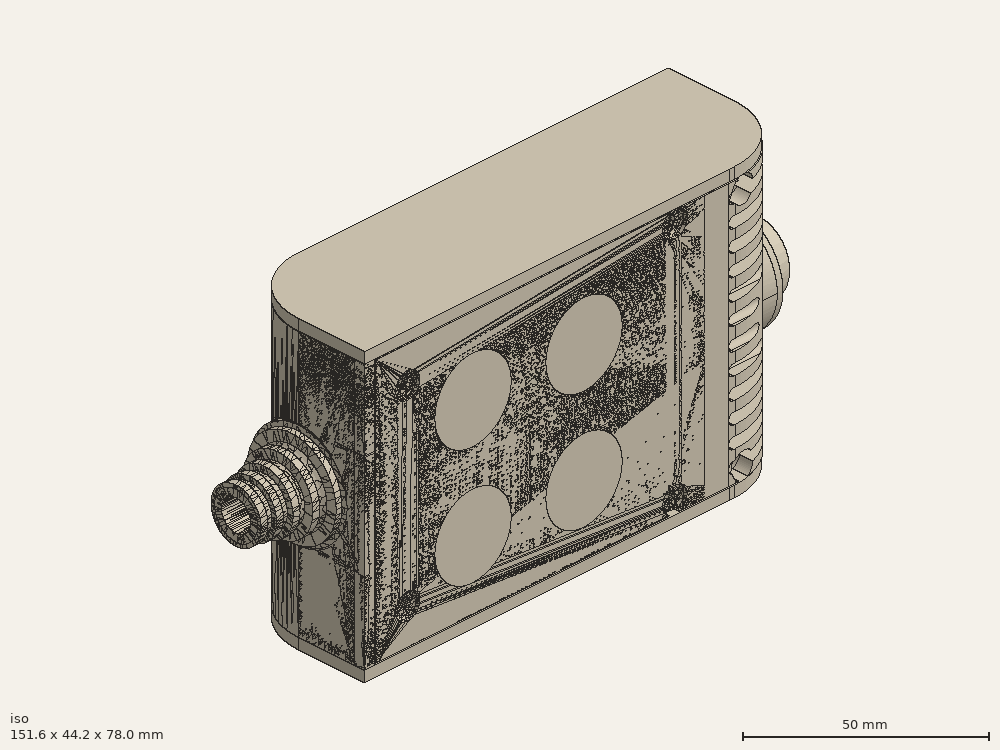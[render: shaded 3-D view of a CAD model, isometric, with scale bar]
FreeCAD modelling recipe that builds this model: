
FCSTD DOCUMENT  (FreeCAD 0.19R0.19.2)
Label: enclosure_202FCStd
License: All rights reserved
LicenseURL: http://en.wikipedia.org/wiki/All_rights_reserved
objects: Part::Revolution×152, Part::MultiFuse×146, Part::Feature×146, Sketcher::SketchObject×84, Part::Cut×70, Part::Cylinder×70, Part::Extrusion×67, Part::Fillet×58, Part::Box×36, App::MeasureDistance×4, PartDesign::Body×2, Image::ImagePlane×1
note: 831 computed .brp shape members not serialized (recipe doc carries the construction recipe); baked Part::Feature solids carry a one-line shape summary decoded from their .brp

FEATURE [Sketcher::SketchObject] Sketch  label="topSketch"
  FullyConstrained = true
  sketch-geometry (20):
    g0: LineSegment StartX=5.21097e-06 StartY=3 StartZ=0 EndX=5.21097e-06 EndY=19 EndZ=0
    g1: ArcOfCircle CenterX=19 CenterY=19 CenterZ=0 NormalX=0 NormalY=0 NormalZ=1 AngleXU=0 Radius=19 StartAngle=1.5708 EndAngle=3.14159
    g2: ArcOfCircle CenterX=19 CenterY=19 CenterZ=0 NormalX=0 NormalY=0 NormalZ=1 AngleXU=0 Radius=16 StartAngle=1.5708 EndAngle=3.14159
    g3: LineSegment StartX=114 StartY=35 StartZ=0 EndX=19 EndY=35 EndZ=0
    g4: LineSegment StartX=5.21097e-06 StartY=3 StartZ=0 EndX=5.21097e-06 EndY=0 EndZ=0
    g5: LineSegment StartX=3 StartY=0 StartZ=0 EndX=5.21097e-06 EndY=0 EndZ=0
    g6: LineSegment StartX=3 StartY=19 StartZ=0 EndX=3 EndY=0 EndZ=0
    g7: LineSegment StartX=19 StartY=38 StartZ=0 EndX=124 EndY=38 EndZ=0
    g8: Circle CenterX=119 CenterY=35 CenterZ=0 NormalX=0 NormalY=0 NormalZ=1 AngleXU=0 Radius=1
    g9: Circle CenterX=121 CenterY=35 CenterZ=0 NormalX=0 NormalY=0 NormalZ=1 AngleXU=0 Radius=1
    g10: Circle CenterX=121 CenterY=33 CenterZ=0 NormalX=0 NormalY=0 NormalZ=1 AngleXU=0 Radius=1
    g11: BSplineCurve PolesCount=3 KnotsCount=2 Degree=2 IsPeriodic=0
    g12: GeomPoint X=119 Y=35 Z=0
    g13: GeomPoint X=121 Y=33 Z=0
    g14: LineSegment StartX=119 StartY=35 StartZ=0 EndX=114 EndY=35 EndZ=0
    g15: ArcOfCircle CenterX=105 CenterY=19 CenterZ=0 NormalX=0 NormalY=0 NormalZ=1 AngleXU=0 Radius=19 StartAngle=5.7297 EndAngle=6.28319
    g16: ArcOfCircle CenterX=105 CenterY=19 CenterZ=0 NormalX=0 NormalY=0 NormalZ=1 AngleXU=0 Radius=16 StartAngle=5.60905 EndAngle=6.28319
    g17: LineSegment StartX=121 StartY=33 StartZ=0 EndX=121 EndY=19 EndZ=0
    g18: LineSegment StartX=124 StartY=38 StartZ=0 EndX=124 EndY=19 EndZ=0
    g19: LineSegment StartX=117.5 StartY=9.01251 StartZ=0 EndX=121.163 EndY=9.0125 EndZ=0
  constraints (46):
    c: Vertical(g0)
    c: Block(g0)
    c: Coincident(g1,g0)
    c: Block(g1)
    c: Coincident(g2,g1)
    c: Block(g2)
    c: Coincident(g3,g2)
    c: Horizontal(g3)
    c: Tangent(g3,g2)
    c: Coincident(g4,g0)
    c: Distance(g4) = 3
    c: Vertical(g4)
    c: Coincident(g5,g4)
    c: Horizontal(g5)
    c: Coincident(g6,g2)
    c: Coincident(g6,g5)
    c: Vertical(g6)
    c: Horizontal(g7)
    c: Distance(g7) = 105
    c: Coincident(g7,g1)
    c: Block(g3)
    c: Weight(g8) = 1
    c: Equal(g8,g9)
    c: Equal(g8,g10)
    c: InternalAlignment(g8,g11)
    c: InternalAlignment(g9,g11)
    c: InternalAlignment(g10,g11)
    c: InternalAlignment(g12,g11)
    c: InternalAlignment(g13,g11)
    c: Block(g11)
    c: Coincident(g14,g11)
    c: Coincident(g14,g3)
    c: Horizontal(g14)
    c: Block(g15)
    c: Coincident(g16,g15)
    c: Block(g16)
    c: Coincident(g17,g11)
    c: Coincident(g17,g16)
    c: Vertical(g17)
    c: Distance(g17) = 14
    c: Coincident(g18,g7)
    c: Coincident(g18,g15)
    c: Vertical(g18)
    c: Distance(g18) = 19
    c: Coincident(g19,g16)
    c: Coincident(g19,g15)
FEATURE [Sketcher::SketchObject] Sketch001  label="bottomSketch"
  FullyConstrained = true
  sketch-geometry (32):
    g0: LineSegment StartX=3.3 StartY=-6.03275e-07 StartZ=0 EndX=98 EndY=-6.03275e-07 EndZ=0
    g1: ArcOfCircle CenterX=98 CenterY=19 CenterZ=0 NormalX=0 NormalY=0 NormalZ=1 AngleXU=0 Radius=19 StartAngle=4.71239 EndAngle=5.71103
    g2: LineSegment StartX=6.3 StartY=8 StartZ=0 EndX=3.3 EndY=8 EndZ=0
    g3: LineSegment StartX=3.3 StartY=8 StartZ=0 EndX=3.3 EndY=-6.03275e-07 EndZ=0
    g4: ArcOfCircle CenterX=8.3 CenterY=5 CenterZ=0 NormalX=0 NormalY=0 NormalZ=1 AngleXU=0 Radius=2 StartAngle=3.14159 EndAngle=4.71239
    g5: LineSegment StartX=6.3 StartY=8 StartZ=0 EndX=6.3 EndY=5 EndZ=0
    g6: ArcOfCircle CenterX=98 CenterY=19 CenterZ=0 NormalX=0 NormalY=0 NormalZ=1 AngleXU=0 Radius=12.7 StartAngle=4.71239 EndAngle=6.28319
    g7: LineSegment StartX=94.7 StartY=3 StartZ=0 EndX=8.3 EndY=3 EndZ=0
    g8-g12: Circle x5 (B-spline internal-alignment scaffolding for g13; pole/knot coordinates omitted)
    g13: BSplineCurve PolesCount=5 KnotsCount=3 Degree=3 IsPeriodic=0
    g14: GeomPoint X=98 Y=6.3 Z=0
    g15: GeomPoint X=96.3938 Y=4.71946 Z=0
    g16: GeomPoint X=94.7 Y=3 Z=0
    g17-g23: Circle x7 (B-spline internal-alignment scaffolding for g24; pole/knot coordinates omitted)
    g24: BSplineCurve PolesCount=7 KnotsCount=5 Degree=3 IsPeriodic=0
    g25-g29: GeomPoint x5 (B-spline internal-alignment scaffolding for g24; pole/knot coordinates omitted)
    g30: ArcOfCircle CenterX=98 CenterY=19 CenterZ=0 NormalX=0 NormalY=0 NormalZ=1 AngleXU=0 Radius=15.7 StartAngle=5.81226 EndAngle=6.28319
    g31: LineSegment StartX=110.7 StartY=19 StartZ=0 EndX=113.7 EndY=19 EndZ=0
  constraints (41):
    c: Horizontal(g0)
    c: Coincident(g1,g0)
    c: Block(g1)
    c: Horizontal(g2)
    c: Distance(g2) = 3
    c: Coincident(g3,g2)
    c: Vertical(g3)
    c: Coincident(g3,g0)
    c: Block(g4)
    c: Block(g2)
    c: Coincident(g5,g2)
    c: Coincident(g5,g4)
    c: Vertical(g5)
    c: Coincident(g6,g1)
    c: Block(g6)
    c: Coincident(g7,g4)
    c: Horizontal(g7)
    c: Block(g0)
    c: Block(g7)
    c: Block(g3)
    c: Coincident(g13,g6)
    c: Weight(g8) = 1
    c: Equal(g8, g9-g12) x4
    c: Coincident(g13,g7)
    c: InternalAlignment(g8-g12 -> g13) x5
    c: InternalAlignment(g14,g13)
    c: InternalAlignment(g15,g13)
    c: InternalAlignment(g16,g13)
    c: Block(g13)
    c: Weight(g17) = 1
    c: Equal(g17, g18-g23) x6
    c: Coincident(g24,g1)
    c: InternalAlignment(g17-g23 -> g24) x7
    c: InternalAlignment(g25-g29 -> g24) x5
    c: Block(g24)
    c: Coincident(g30,g24)
    c: Coincident(g31,g6)
    c: Coincident(g31,g30)
    c: Horizontal(g31)
    c: Block(g31)
    c: Block(g30)
FEATURE [Part::Extrusion] Extrude  label="top"
  Base = -> Sketch
  Dir = (0,0,1)
  DirMode = 2
  FaceMakerClass = Part::FaceMakerBullseye
  LengthFwd = 72
  LengthRev = 0
  Solid = true
  Symmetric = false
FEATURE [Part::Extrusion] Extrude001  label="bottom"
  Base = -> Sketch001
  Dir = (0,0,1)
  DirMode = 2
  FaceMakerClass = Part::FaceMakerBullseye
  LengthFwd = 71.4
  LengthRev = 0
  Placement = pos=(0,0,0.3) rot=(0,0,1;0rad)
  Solid = true
  Symmetric = false
FEATURE [Sketcher::SketchObject] Sketch002  label="topSketch001"
  FullyConstrained = true
  sketch-geometry (8):
    g0: ArcOfCircle CenterX=19 CenterY=19.0975 CenterZ=0 NormalX=0 NormalY=0 NormalZ=1 AngleXU=0 Radius=18.9025 StartAngle=1.5708 EndAngle=3.14674
    g1: LineSegment StartX=0.0977805 StartY=19.0003 StartZ=0 EndX=0.0977805 EndY=0.000251602 EndZ=0
    g2: LineSegment StartX=19 StartY=38 StartZ=0 EndX=124 EndY=38 EndZ=0
    g3: LineSegment StartX=0.0977805 StartY=0.000251602 StartZ=0 EndX=105.098 EndY=0.000251602 EndZ=0
    g4: LineSegment StartX=124 StartY=38 StartZ=0 EndX=125.616 EndY=38 EndZ=0
    g5: LineSegment StartX=105.098 StartY=0.000251602 StartZ=0 EndX=106.713 EndY=0.000251602 EndZ=0
    g6: ArcOfCircle CenterX=106.616 CenterY=19 CenterZ=0 NormalX=0 NormalY=0 NormalZ=1 AngleXU=0 Radius=19 StartAngle=4.71754 EndAngle=6.28319
    g7: LineSegment StartX=125.616 StartY=38 StartZ=0 EndX=125.616 EndY=19 EndZ=0
  constraints (21):
    c: Block(g0)
    c: Coincident(g1,g0)
    c: Vertical(g1)
    c: Horizontal(g2)
    c: Distance(g2) = 105
    c: Coincident(g2,g0)
    c: Distance(g1) = 19
    c: Coincident(g3,g1)
    c: Horizontal(g3)
    c: Distance(g3) = 105
    c: Coincident(g4,g2)
    c: Horizontal(g4)
    c: Distance(g4) = 1.61553
    c: Horizontal(g5)
    c: Equal(g4,g5) = 1.61553
    c: Coincident(g5,g3)
    c: Block(g6)
    c: Coincident(g6,g5)
    c: Coincident(g7,g4)
    c: Coincident(g7,g6)
    c: Vertical(g7)
FEATURE [Part::Extrusion] Extrude002  label="sideA"
  Base = -> Sketch002
  Dir = (0,0,1)
  DirMode = 2
  FaceMakerClass = Part::FaceMakerBullseye
  LengthFwd = 3
  LengthRev = 0
  Placement = pos=(0,0,-3) rot=(0,0,1;0rad)
  Solid = true
  Symmetric = false
FEATURE [Sketcher::SketchObject] Sketch003  label="topSketch002"
  FullyConstrained = true
  sketch-geometry (6):
    g0: LineSegment StartX=19 StartY=38 StartZ=0 EndX=117 EndY=38 EndZ=0
    g1: ArcOfCircle CenterX=19 CenterY=19 CenterZ=0 NormalX=0 NormalY=0 NormalZ=1 AngleXU=0 Radius=19 StartAngle=1.5708 EndAngle=3.14159
    g2: LineSegment StartX=117 StartY=38 StartZ=0 EndX=117 EndY=19 EndZ=0
    g3: LineSegment StartX=98 StartY=1.0161e-12 StartZ=0 EndX=5.22862e-06 EndY=1.0161e-12 EndZ=0
    g4: LineSegment StartX=5.22862e-06 StartY=19 StartZ=0 EndX=5.22862e-06 EndY=1.0161e-12 EndZ=0
    g5: ArcOfCircle CenterX=98 CenterY=19 CenterZ=0 NormalX=0 NormalY=0 NormalZ=1 AngleXU=0 Radius=19 StartAngle=4.71239 EndAngle=6.28319
  constraints (16):
    c: Horizontal(g0)
    c: Distance(g0) = 98
    c: Coincident(g1,g0)
    c: Block(g1)
    c: Coincident(g2,g0)
    c: Vertical(g2)
    c: Distance(g2) = 19
    c: Horizontal(g3)
    c: Coincident(g4,g1)
    c: Vertical(g4)
    c: Coincident(g3,g4)
    c: Block(g3)
    c: Coincident(g5,g2)
    c: Coincident(g5,g3)
    c: Block(g0)
    c: Block(g5)
FEATURE [Sketcher::SketchObject] Sketch004
  FullyConstrained = true
  MapMode = 3
  Placement = pos=(0,0,0) rot=(1,0,0;1.5708rad)
  Support = -> [Extrude]
  sketch-geometry (8):
    g0: Circle CenterX=80.351 CenterY=-67.6202 CenterZ=0 NormalX=0 NormalY=0 NormalZ=1 AngleXU=0 Radius=2
    g1: Circle CenterX=80.351 CenterY=-67.6202 CenterZ=0 NormalX=0 NormalY=0 NormalZ=1 AngleXU=0 Radius=3
    g2: Circle CenterX=80.351 CenterY=-4.92017 CenterZ=0 NormalX=0 NormalY=0 NormalZ=1 AngleXU=0 Radius=2
    g3: Circle CenterX=80.351 CenterY=-4.92017 CenterZ=0 NormalX=0 NormalY=0 NormalZ=1 AngleXU=0 Radius=3
    g4: Circle CenterX=23.851 CenterY=-4.92017 CenterZ=0 NormalX=0 NormalY=0 NormalZ=1 AngleXU=0 Radius=2
    g5: Circle CenterX=23.851 CenterY=-4.92017 CenterZ=0 NormalX=0 NormalY=0 NormalZ=1 AngleXU=0 Radius=3
    g6: Circle CenterX=23.851 CenterY=-67.6202 CenterZ=0 NormalX=0 NormalY=0 NormalZ=1 AngleXU=0 Radius=2
    g7: Circle CenterX=23.851 CenterY=-67.6202 CenterZ=0 NormalX=0 NormalY=0 NormalZ=1 AngleXU=0 Radius=3
  constraints (8):
    c: Block(g3)
    c: Block(g2)
    c: Block(g1)
    c: Block(g0)
    c: Block(g6)
    c: Block(g7)
    c: Block(g4)
    c: Block(g5)
FEATURE [Part::Extrusion] Extrude004
  Base = -> Sketch004
  Dir = (0,-1,2e-16)
  DirMode = 2
  FaceMakerClass = Part::FaceMakerBullseye
  LengthFwd = 6
  LengthRev = 0
  Placement = pos=(0,9,0) rot=(0,0,1;0rad)
  Solid = true
  Symmetric = false
FEATURE [Sketcher::SketchObject] Sketch005
  FullyConstrained = true
  MapMode = 3
  Placement = pos=(0,0,0) rot=(1,0,0;1.5708rad)
  Support = -> [Extrude]
  sketch-geometry (8):
    g0: Circle CenterX=80.351 CenterY=-67.6202 CenterZ=0 NormalX=0 NormalY=0 NormalZ=1 AngleXU=0 Radius=3
    g1: Circle CenterX=80.351 CenterY=-4.92017 CenterZ=0 NormalX=0 NormalY=0 NormalZ=1 AngleXU=0 Radius=3
    g2: Circle CenterX=23.851 CenterY=-4.92017 CenterZ=0 NormalX=0 NormalY=0 NormalZ=1 AngleXU=0 Radius=3
    g3: Circle CenterX=23.851 CenterY=-67.6202 CenterZ=0 NormalX=0 NormalY=0 NormalZ=1 AngleXU=0 Radius=3
    g4: Circle CenterX=23.851 CenterY=-67.6202 CenterZ=0 NormalX=0 NormalY=0 NormalZ=1 AngleXU=0 Radius=5
    g5: Circle CenterX=80.351 CenterY=-67.6202 CenterZ=0 NormalX=0 NormalY=0 NormalZ=1 AngleXU=0 Radius=5
    g6: Circle CenterX=23.851 CenterY=-4.92017 CenterZ=0 NormalX=0 NormalY=0 NormalZ=1 AngleXU=0 Radius=5
    g7: Circle CenterX=80.351 CenterY=-4.92017 CenterZ=0 NormalX=0 NormalY=0 NormalZ=1 AngleXU=0 Radius=5
  constraints (8):
    c: Block(g1)
    c: Block(g0)
    c: Block(g3)
    c: Block(g2)
    c: Block(g5)
    c: Block(g4)
    c: Block(g6)
    c: Block(g7)
FEATURE [Part::Extrusion] Extrude005
  Base = -> Sketch005
  Dir = (0,-1,2e-16)
  DirMode = 2
  FaceMakerClass = Part::FaceMakerBullseye
  LengthFwd = 2
  LengthRev = 0
  Solid = true
  Symmetric = false
FEATURE [Sketcher::SketchObject] Sketch006
  FullyConstrained = true
  MapMode = 3
  Placement = pos=(0,0,0) rot=(1,0,0;1.5708rad)
  sketch-geometry (8):
    g0: Circle CenterX=80.351 CenterY=-67.6202 CenterZ=0 NormalX=0 NormalY=0 NormalZ=1 AngleXU=0 Radius=3
    g1: Circle CenterX=80.351 CenterY=-4.92017 CenterZ=0 NormalX=0 NormalY=0 NormalZ=1 AngleXU=0 Radius=3
    g2: Circle CenterX=23.851 CenterY=-4.92017 CenterZ=0 NormalX=0 NormalY=0 NormalZ=1 AngleXU=0 Radius=3
    g3: Circle CenterX=23.851 CenterY=-67.6202 CenterZ=0 NormalX=0 NormalY=0 NormalZ=1 AngleXU=0 Radius=3
    g4: Circle CenterX=23.851 CenterY=-67.6202 CenterZ=0 NormalX=0 NormalY=0 NormalZ=1 AngleXU=0 Radius=5
    g5: Circle CenterX=80.351 CenterY=-67.6202 CenterZ=0 NormalX=0 NormalY=0 NormalZ=1 AngleXU=0 Radius=5
    g6: Circle CenterX=23.851 CenterY=-4.92017 CenterZ=0 NormalX=0 NormalY=0 NormalZ=1 AngleXU=0 Radius=5
    g7: Circle CenterX=80.351 CenterY=-4.92017 CenterZ=0 NormalX=0 NormalY=0 NormalZ=1 AngleXU=0 Radius=5
  constraints (8):
    c: Block(g1)
    c: Block(g0)
    c: Block(g3)
    c: Block(g2)
    c: Block(g5)
    c: Block(g4)
    c: Block(g6)
    c: Block(g7)
FEATURE [Part::Extrusion] Extrude007
  Base = -> Sketch006
  Dir = (0,-1,2e-16)
  DirMode = 2
  FaceMakerClass = Part::FaceMakerBullseye
  LengthFwd = 2
  LengthRev = 0
  Solid = true
  Symmetric = false
FEATURE [Part::Fillet] Fillet
  Base = -> Extrude007
  Edges = 4 edges r=1.99: [Edge6,Edge12,Edge18,Edge24]
FEATURE [Part::Cut] Cut
  Base = -> Extrude005
  Placement = pos=(0,5,0) rot=(0,0,1;0rad)
  Tool = -> Fillet
FEATURE [Part::MultiFuse] Fusion  label="pCBScrews"
  Placement = pos=(-2.5,0,72.3) rot=(0,0,1;0rad)
  Shapes = -> [Extrude004,Cut]
FEATURE [App::MeasureDistance] Distance  label="Distance: 0.69 mm"
  Distance = 0.685967
  P1 = (24.0138,2.9647,0.3)
  P2 = (23.8901,3,-0.373787)
FEATURE [App::MeasureDistance] Distance001  label="Distance: 0.53 mm"
  Distance = 0.533607
  P1 = (80.2939,3,72.2334)
  P2 = (80.281,2.99661,71.7)
FEATURE [Part::Fillet] Fillet001
  Base = -> Extrude001
  Edges = 1 edges r=2.4: [Edge17]
FEATURE [Part::Fillet] Fillet002  label="bottom001"
  Base = -> Fillet001
  Edges = 1 edges r=2.4: [Edge36]
FEATURE [Part::Fillet] Fillet003  label="top001"
  Base = -> Extrude
  Edges = 1 edges r=2: [Edge1]
FEATURE [Sketcher::SketchObject] Sketch007
  FullyConstrained = true
  sketch-geometry (16):
    g0: LineSegment StartX=4 StartY=0 StartZ=0 EndX=4 EndY=2.4 EndZ=0
    g1: LineSegment StartX=4 StartY=2.4 StartZ=0 EndX=7 EndY=2.4 EndZ=0
    g2: LineSegment StartX=4 StartY=0 StartZ=0 EndX=5.7 EndY=0 EndZ=0
    g3: LineSegment StartX=5.7 StartY=0 StartZ=0 EndX=5.7 EndY=-5.6 EndZ=0
    g4-g8: Circle x5 (B-spline internal-alignment scaffolding for g9; pole/knot coordinates omitted)
    g9: BSplineCurve PolesCount=5 KnotsCount=3 Degree=3 IsPeriodic=0
    g10: GeomPoint X=7 Y=2.4 Z=0
    g11: GeomPoint X=10.4582 Y=-1.55472 Z=0
    g12: GeomPoint X=14 Y=-5.6 Z=0
    g13: LineSegment StartX=14 StartY=-5.6 StartZ=0 EndX=14 EndY=-14.1 EndZ=0
    g14: LineSegment StartX=14 StartY=-14.1 StartZ=0 EndX=6.5 EndY=-14.1 EndZ=0
    g15: LineSegment StartX=5.7 StartY=-5.6 StartZ=0 EndX=6.5 EndY=-14.1 EndZ=0
  constraints (28):
    c: Distance(g0) = 2.4
    c: Vertical(g0)
    c: Block(g0)
    c: Coincident(g1,g0)
    c: Horizontal(g1)
    c: Distance(g1) = 3
    c: Coincident(g2,g0)
    c: Horizontal(g2)
    c: Distance(g2) = 1.7
    c: Coincident(g3,g2)
    c: Vertical(g3)
    c: Distance(g3) = 5.6
    c: Coincident(g9,g1)
    c: Weight(g4) = 1
    c: Equal(g4, g5-g8) x4
    c: InternalAlignment(g4-g8 -> g9) x5
    c: InternalAlignment(g10,g9)
    c: InternalAlignment(g11,g9)
    c: InternalAlignment(g12,g9)
    c: Block(g9)
    c: Coincident(g13,g9)
    c: Vertical(g13)
    c: Distance(g13) = 8.5
    c: Coincident(g14,g13)
    c: Horizontal(g14)
    c: Distance(g14) = 7.5
    c: Coincident(g15,g3)
    c: Coincident(g15,g14)
FEATURE [Part::Feature] Face
  shape: bbox 10 x 16.5 x 2e-07 mm, 1 faces, 0 solids (baked)
FEATURE [Part::Revolution] Revolve  label="plugHousing"
  Angle = 360
  Axis = (0,1,0)
  Base = (0,0,0)
  FaceMakerClass = Part::FaceMakerBullseye
  Placement = pos=(0,0,36.15) rot=(0,0,1;0rad)
  Solid = false
  Source = -> Face
  Symmetric = false
FEATURE [Part::Feature] Face001
  shape: bbox 10 x 16.5 x 2e-07 mm, 1 faces, 0 solids (baked)
FEATURE [Part::Revolution] Revolve001  label="plugHousing001"
  Angle = 360
  Axis = (0,1,0)
  Base = (0,0,0)
  FaceMakerClass = Part::FaceMakerBullseye
  Placement = pos=(0,0,36.15) rot=(0,0,1;0rad)
  Solid = false
  Source = -> Face001
  Symmetric = false
FEATURE [Part::MultiFuse] Fusion001  label="plugHousing002"
  Placement = pos=(0,0,0) rot=(0,0,1;1.5708rad)
  Shapes = -> [Revolve001,Revolve]
FEATURE [Part::Feature] Face002
  shape: bbox 10 x 16.5 x 2e-07 mm, 1 faces, 0 solids (baked)
FEATURE [Part::Revolution] Revolve003  label="plugHousing005"
  Angle = 360
  Axis = (0,1,0)
  Base = (0,0,0)
  FaceMakerClass = Part::FaceMakerBullseye
  Placement = pos=(0,0,36.15) rot=(0,0,1;0rad)
  Solid = false
  Source = -> Face002
  Symmetric = false
FEATURE [Part::Feature] Face003
  shape: bbox 10 x 16.5 x 2e-07 mm, 1 faces, 0 solids (baked)
FEATURE [Part::Revolution] Revolve002  label="plugHousing003"
  Angle = 360
  Axis = (0,1,0)
  Base = (0,0,0)
  FaceMakerClass = Part::FaceMakerBullseye
  Placement = pos=(0,0,36.15) rot=(0,0,1;0rad)
  Solid = false
  Source = -> Face003
  Symmetric = false
FEATURE [Part::MultiFuse] Fusion002  label="plugHousing004"
  Placement = pos=(0,0,0) rot=(0,0,1;1.5708rad)
  Shapes = -> [Revolve002,Revolve003]
FEATURE [Part::MultiFuse] Fusion003  label="plugHousing006"
  Placement = pos=(0,19,0) rot=(0,0,1;3.14159rad)
  Shapes = -> [Fusion002,Fusion001]
FEATURE [Part::Feature] Face004
  shape: bbox 10 x 16.5 x 2e-07 mm, 1 faces, 0 solids (baked)
FEATURE [Part::Revolution] Revolve006  label="plugHousing010"
  Angle = 360
  Axis = (0,1,0)
  Base = (0,0,0)
  FaceMakerClass = Part::FaceMakerBullseye
  Placement = pos=(0,0,36.15) rot=(0,0,1;0rad)
  Solid = false
  Source = -> Face004
  Symmetric = false
FEATURE [Part::Feature] Face005
  shape: bbox 10 x 16.5 x 2e-07 mm, 1 faces, 0 solids (baked)
FEATURE [Part::Revolution] Revolve007  label="plugHousing011"
  Angle = 360
  Axis = (0,1,0)
  Base = (0,0,0)
  FaceMakerClass = Part::FaceMakerBullseye
  Placement = pos=(0,0,36.15) rot=(0,0,1;0rad)
  Solid = false
  Source = -> Face005
  Symmetric = false
FEATURE [Part::Feature] Face006
  shape: bbox 10 x 16.5 x 2e-07 mm, 1 faces, 0 solids (baked)
FEATURE [Part::Revolution] Revolve004  label="plugHousing007"
  Angle = 360
  Axis = (0,1,0)
  Base = (0,0,0)
  FaceMakerClass = Part::FaceMakerBullseye
  Placement = pos=(0,0,36.15) rot=(0,0,1;0rad)
  Solid = false
  Source = -> Face006
  Symmetric = false
FEATURE [Part::MultiFuse] Fusion004  label="plugHousing009"
  Placement = pos=(0,0,0) rot=(0,0,1;1.5708rad)
  Shapes = -> [Revolve004,Revolve007]
FEATURE [Part::Feature] Face007
  shape: bbox 10 x 16.5 x 2e-07 mm, 1 faces, 0 solids (baked)
FEATURE [Part::Revolution] Revolve005  label="plugHousing008"
  Angle = 360
  Axis = (0,1,0)
  Base = (0,0,0)
  FaceMakerClass = Part::FaceMakerBullseye
  Placement = pos=(0,0,36.15) rot=(0,0,1;0rad)
  Solid = false
  Source = -> Face007
  Symmetric = false
FEATURE [Part::MultiFuse] Fusion005  label="plugHousing012"
  Placement = pos=(0,0,0) rot=(0,0,1;1.5708rad)
  Shapes = -> [Revolve006,Revolve005]
FEATURE [Part::MultiFuse] Fusion006  label="plugHousing013"
  Placement = pos=(0,19,0) rot=(0,0,1;3.14159rad)
  Shapes = -> [Fusion005,Fusion004]
FEATURE [Part::MultiFuse] Fusion007  label="plugHousing014"
  Placement = pos=(122.621,0,-0.15) rot=(0,0,1;0rad)
  Shapes = -> [Fusion003,Fusion006]
FEATURE [Part::Cylinder] Cylinder002
  Angle = 360
  AttacherType = Attacher::AttachEngine3D
  Height = 20
  Placement = pos=(0,0,36.15) rot=(0,0,1;0rad)
  Radius = 4
FEATURE [Part::Cylinder] Cylinder003
  Angle = 360
  AttacherType = Attacher::AttachEngine3D
  Height = 10
  Placement = pos=(0,0,36.15) rot=(0,0,1;0rad)
  Radius = 4
FEATURE [Part::MultiFuse] Fusion009  label="removeToCreateHoleForPlugHousing"
  Placement = pos=(70,19,36.15) rot=(0,1,0;1.5708rad)
  Shapes = -> [Cylinder002,Cylinder003]
FEATURE [Part::Cylinder] Cylinder004
  Angle = 360
  AttacherType = Attacher::AttachEngine3D
  Height = 20
  Placement = pos=(0,0,36.15) rot=(0,0,1;0rad)
  Radius = 4
FEATURE [Part::Cylinder] Cylinder005
  Angle = 360
  AttacherType = Attacher::AttachEngine3D
  Height = 10
  Placement = pos=(0,0,36.15) rot=(0,0,1;0rad)
  Radius = 4
FEATURE [Part::MultiFuse] Fusion010  label="removeToCreateHoleForPlugHousing001"
  Placement = pos=(70,19,36.15) rot=(0,1,0;1.5708rad)
  Shapes = -> [Cylinder004,Cylinder005]
FEATURE [Part::Cut] Cut001
  Base = -> Fillet003
  Tool = -> Fusion010
FEATURE [Part::Cut] Cut002  label="Bottom"
  Base = -> Fillet002
  Tool = -> Fusion009
FEATURE [Part::Feature] Face008
  shape: bbox 10 x 16.5 x 2e-07 mm, 1 faces, 0 solids (baked)
FEATURE [Part::Revolution] Revolve011  label="plugHousing021"
  Angle = 360
  Axis = (0,1,0)
  Base = (0,0,0)
  FaceMakerClass = Part::FaceMakerBullseye
  Placement = pos=(0,0,36.15) rot=(0,0,1;0rad)
  Solid = false
  Source = -> Face008
  Symmetric = false
FEATURE [Part::Feature] Face009
  shape: bbox 10 x 16.5 x 2e-07 mm, 1 faces, 0 solids (baked)
FEATURE [Part::Revolution] Revolve012  label="plugHousing022"
  Angle = 360
  Axis = (0,1,0)
  Base = (0,0,0)
  FaceMakerClass = Part::FaceMakerBullseye
  Placement = pos=(0,0,36.15) rot=(0,0,1;0rad)
  Solid = false
  Source = -> Face009
  Symmetric = false
FEATURE [Part::Feature] Face010 .. Face013  x4 (patterned run collapsed; names and placements below)
  shape: bbox 10 x 16.5 x 2e-07 mm, 1 faces, 0 solids (baked)
FEATURE [Part::Revolution] Revolve015  label="plugHousing027"
  Angle = 360
  Axis = (0,1,0)
  Base = (0,0,0)
  FaceMakerClass = Part::FaceMakerBullseye
  Placement = pos=(0,0,36.15) rot=(0,0,1;0rad)
  Solid = false
  Source = -> Face013
  Symmetric = false
FEATURE [Part::Feature] Face014
  shape: bbox 10 x 16.5 x 2e-07 mm, 1 faces, 0 solids (baked)
FEATURE [Part::Feature] Face015
  shape: bbox 10 x 16.5 x 2e-07 mm, 1 faces, 0 solids (baked)
FEATURE [Part::Feature] Face016
  shape: bbox 10 x 16.5 x 2e-07 mm, 1 faces, 0 solids (baked)
FEATURE [Part::Revolution] Revolve019  label="plugHousing033"
  Angle = 360
  Axis = (0,1,0)
  Base = (0,0,0)
  FaceMakerClass = Part::FaceMakerBullseye
  Placement = pos=(0,0,36.15) rot=(0,0,1;0rad)
  Solid = false
  Source = -> Face016
  Symmetric = false
FEATURE [Part::Feature] Face017
  shape: bbox 10 x 16.5 x 2e-07 mm, 1 faces, 0 solids (baked)
FEATURE [Part::Revolution] Revolve020  label="plugHousing034"
  Angle = 360
  Axis = (0,1,0)
  Base = (0,0,0)
  FaceMakerClass = Part::FaceMakerBullseye
  Placement = pos=(0,0,36.15) rot=(0,0,1;0rad)
  Solid = false
  Source = -> Face017
  Symmetric = false
FEATURE [Part::Feature] Face018
  shape: bbox 10 x 16.5 x 2e-07 mm, 1 faces, 0 solids (baked)
FEATURE [Part::Revolution] Revolve016  label="plugHousing030"
  Angle = 360
  Axis = (0,1,0)
  Base = (0,0,0)
  FaceMakerClass = Part::FaceMakerBullseye
  Placement = pos=(0,0,36.15) rot=(0,0,1;0rad)
  Solid = false
  Source = -> Face018
  Symmetric = false
FEATURE [Part::MultiFuse] Fusion020  label="plugHousing038"
  Placement = pos=(0,0,0) rot=(0,0,1;1.5708rad)
  Shapes = -> [Revolve016,Revolve020]
FEATURE [Part::Feature] Face019
  shape: bbox 10 x 16.5 x 2e-07 mm, 1 faces, 0 solids (baked)
FEATURE [Part::Feature] Face020
  shape: bbox 10 x 16.5 x 2e-07 mm, 1 faces, 0 solids (baked)
FEATURE [Part::Revolution] Revolve017  label="plugHousing031"
  Angle = 360
  Axis = (0,1,0)
  Base = (0,0,0)
  FaceMakerClass = Part::FaceMakerBullseye
  Placement = pos=(0,0,36.15) rot=(0,0,1;0rad)
  Solid = false
  Source = -> Face020
  Symmetric = false
FEATURE [Part::MultiFuse] Fusion021  label="plugHousing039"
  Placement = pos=(0,0,0) rot=(0,0,1;1.5708rad)
  Shapes = -> [Revolve019,Revolve017]
FEATURE [Part::MultiFuse] Fusion023  label="plugHousing041"
  Placement = pos=(0,19,0) rot=(0,0,1;3.14159rad)
  Shapes = -> [Fusion021,Fusion020]
FEATURE [Part::Revolution] Revolve022  label="plugHousing043"
  Angle = 360
  Axis = (0,1,0)
  Base = (0,0,0)
  FaceMakerClass = Part::FaceMakerBullseye
  Placement = pos=(0,0,36.15) rot=(0,0,1;0rad)
  Solid = false
  Source = -> Face019
  Symmetric = false
FEATURE [Part::Feature] Face021
  shape: bbox 10 x 16.5 x 2e-07 mm, 1 faces, 0 solids (baked)
FEATURE [Part::Revolution] Revolve023  label="plugHousing044"
  Angle = 360
  Axis = (0,1,0)
  Base = (0,0,0)
  FaceMakerClass = Part::FaceMakerBullseye
  Placement = pos=(0,0,36.15) rot=(0,0,1;0rad)
  Solid = false
  Source = -> Face021
  Symmetric = false
FEATURE [Part::Feature] Face022
  shape: bbox 10 x 16.5 x 2e-07 mm, 1 faces, 0 solids (baked)
FEATURE [Part::Revolution] Revolve018  label="plugHousing032"
  Angle = 360
  Axis = (0,1,0)
  Base = (0,0,0)
  FaceMakerClass = Part::FaceMakerBullseye
  Placement = pos=(0,0,36.15) rot=(0,0,1;0rad)
  Solid = false
  Source = -> Face022
  Symmetric = false
FEATURE [Part::MultiFuse] Fusion022  label="plugHousing040"
  Placement = pos=(0,0,0) rot=(0,0,1;1.5708rad)
  Shapes = -> [Revolve018,Revolve023]
FEATURE [Part::Feature] Face023
  shape: bbox 10 x 16.5 x 2e-07 mm, 1 faces, 0 solids (baked)
FEATURE [Part::Revolution] Revolve021  label="plugHousing035"
  Angle = 360
  Axis = (0,1,0)
  Base = (0,0,0)
  FaceMakerClass = Part::FaceMakerBullseye
  Placement = pos=(0,0,36.15) rot=(0,0,1;0rad)
  Solid = false
  Source = -> Face023
  Symmetric = false
FEATURE [Part::MultiFuse] Fusion018  label="plugHousing036"
  Placement = pos=(0,0,0) rot=(0,0,1;1.5708rad)
  Shapes = -> [Revolve022,Revolve021]
FEATURE [Part::MultiFuse] Fusion019  label="plugHousing037"
  Placement = pos=(0,19,0) rot=(0,0,1;3.14159rad)
  Shapes = -> [Fusion018,Fusion022]
FEATURE [Part::MultiFuse] Fusion024  label="plugHousing042"
  Placement = pos=(122.621,0,-0.15) rot=(0,0,1;0rad)
  Shapes = -> [Fusion023,Fusion019]
FEATURE [Part::Cylinder] Cylinder006
  Angle = 360
  AttacherType = Attacher::AttachEngine3D
  Height = 20
  Placement = pos=(0,0,36.15) rot=(0,0,1;0rad)
  Radius = 14.3
FEATURE [Part::Cylinder] Cylinder007
  Angle = 360
  AttacherType = Attacher::AttachEngine3D
  Height = 10
  Placement = pos=(0,0,36.15) rot=(0,0,1;0rad)
  Radius = 4
FEATURE [Part::MultiFuse] Fusion026  label="removeToCreteHoleForPlugHousing"
  Placement = pos=(70,19,36) rot=(0,1,0;1.5708rad)
  Shapes = -> [Cylinder006,Cylinder007]
FEATURE [Part::Box] Box001  label="Cube001"
  AttacherType = Attacher::AttachEngine3D
  Height = 28
  Length = 3
  Placement = pos=(110.7,19,22) rot=(0,0,1;0rad)
  Width = 15.7
FEATURE [Part::Cut] Cut003  label="top002"
  Base = -> Cut001
  Tool = -> Fusion007
FEATURE [Part::Revolution] Revolve008  label="plugHousing015"
  Angle = 360
  Axis = (0,1,0)
  Base = (0,0,0)
  FaceMakerClass = Part::FaceMakerBullseye
  Placement = pos=(0,0,36.15) rot=(0,0,1;0rad)
  Solid = false
  Source = -> Face010
  Symmetric = false
FEATURE [Part::MultiFuse] Fusion013  label="plugHousing020"
  Placement = pos=(0,0,0) rot=(0,0,1;1.5708rad)
  Shapes = -> [Revolve008,Revolve012]
FEATURE [Part::Cut] Cut004  label="top003"
  Base = -> Cut003
  Placement = pos=(1,0,0) rot=(0,0,1;0rad)
  Tool = -> Fusion026
FEATURE [Part::Cylinder] Cylinder008
  Angle = 360
  AttacherType = Attacher::AttachEngine3D
  Height = 20
  Placement = pos=(0,0,36.15) rot=(0,0,1;0rad)
  Radius = 10.3
FEATURE [Part::Cylinder] Cylinder009
  Angle = 360
  AttacherType = Attacher::AttachEngine3D
  Height = 10
  Placement = pos=(0,0,36.15) rot=(0,0,1;0rad)
  Radius = 4
FEATURE [Part::MultiFuse] Fusion027  label="removeToCreteHoleForPlugHousing001"
  Placement = pos=(70,19,36) rot=(0,1,0;1.5708rad)
  Shapes = -> [Cylinder008,Cylinder009]
FEATURE [Part::Cut] Cut005  label="plugHousingTab"
  Base = -> Box001
  Tool = -> Fusion027
FEATURE [Part::MultiFuse] Fusion028  label="plugHousing045"
  Shapes = -> [Fusion024,Cut005]
FEATURE [Part::Box] Box002  label="Cube002"
  AttacherType = Attacher::AttachEngine3D
  Height = 28.8
  Length = 3
  Placement = pos=(107.3,28,21.6) rot=(0,0,1;0rad)
  Width = 7
FEATURE [Part::Box] Box003  label="Cube003"
  AttacherType = Attacher::AttachEngine3D
  Height = 3
  Length = 6.4
  Placement = pos=(107.3,28,18.6) rot=(0,0,1;0rad)
  Width = 7
FEATURE [Part::Box] Box004  label="Cube004"
  AttacherType = Attacher::AttachEngine3D
  Height = 3
  Length = 6.4
  Placement = pos=(107.3,28,50.4) rot=(0,0,1;0rad)
  Width = 7
FEATURE [Part::MultiFuse] Fusion029  label="plugHousingBracketHolder"
  Shapes = -> [Box004,Box002,Box003]
FEATURE [Part::Cylinder] Cylinder010
  Angle = 360
  AttacherType = Attacher::AttachEngine3D
  Height = 20
  Placement = pos=(0,0,36.15) rot=(0,0,1;0rad)
  Radius = 14.3
FEATURE [Part::Cylinder] Cylinder011
  Angle = 360
  AttacherType = Attacher::AttachEngine3D
  Height = 10
  Placement = pos=(0,0,36.15) rot=(0,0,1;0rad)
  Radius = 4
FEATURE [Part::MultiFuse] Fusion030  label="removeToCreteHoleForPlugHousing002"
  Placement = pos=(70,19,36) rot=(0,1,0;1.5708rad)
  Shapes = -> [Cylinder010,Cylinder011]
FEATURE [Part::Cut] Cut006  label="plugHousingBracketHolder001"
  Base = -> Fusion029
  Tool = -> Fusion030
FEATURE [Part::Cylinder] Cylinder012
  Angle = 360
  AttacherType = Attacher::AttachEngine3D
  Height = 20
  Placement = pos=(0,0,36.15) rot=(0,0,1;0rad)
  Radius = 7
FEATURE [Part::Cylinder] Cylinder013
  Angle = 360
  AttacherType = Attacher::AttachEngine3D
  Height = 10
  Placement = pos=(0,0,36.15) rot=(0,0,1;0rad)
  Radius = 4
FEATURE [Part::MultiFuse] Fusion032  label="removeToCreteHoleForPlugHousing003"
  Placement = pos=(70,19,36) rot=(0,1,0;1.5708rad)
  Shapes = -> [Cylinder012,Cylinder013]
FEATURE [Part::Cut] Cut007  label="bottom002"
  Base = -> Cut002
  Tool = -> Fusion032
FEATURE [Sketcher::SketchObject] Sketch008
  FullyConstrained = true
  sketch-geometry (54):
    g0: LineSegment StartX=-4.2 StartY=0 StartZ=0 EndX=-6.2 EndY=0 EndZ=0
    g1: LineSegment StartX=-14 StartY=-18 StartZ=0 EndX=-14 EndY=-26.5 EndZ=0
    g2: LineSegment StartX=-4.2 StartY=0 StartZ=0 EndX=-4.2 EndY=-13.4877 EndZ=0
    g3: Circle CenterX=-4.2 CenterY=-13.4877 CenterZ=0 NormalX=0 NormalY=0 NormalZ=1 AngleXU=0 Radius=1
    g4: Circle CenterX=-4.2 CenterY=-26.5 CenterZ=0 NormalX=0 NormalY=0 NormalZ=1 AngleXU=0 Radius=1
    g5: Circle CenterX=-8.2 CenterY=-26.5 CenterZ=0 NormalX=0 NormalY=0 NormalZ=1 AngleXU=0 Radius=1
    g6: BSplineCurve PolesCount=3 KnotsCount=2 Degree=2 IsPeriodic=0
    g7: GeomPoint X=-4.2 Y=-13.4877 Z=0
    g8: GeomPoint X=-8.2 Y=-26.5 Z=0
    g9: LineSegment StartX=-14 StartY=-26.5 StartZ=0 EndX=-8.2 EndY=-26.5 EndZ=0
    g10: LineSegment StartX=-10.15 StartY=-12 StartZ=0 EndX=-10.15 EndY=-14 EndZ=0
    g11: LineSegment StartX=-12.8401 StartY=-16 StartZ=0 EndX=-10.1571 EndY=-16 EndZ=0
    g12: LineSegment StartX=-10.15 StartY=-14 StartZ=0 EndX=-8.70761 EndY=-14 EndZ=0
    g13: LineSegment StartX=-12.8401 StartY=-16 StartZ=0 EndX=-12.8401 EndY=-17.6958 EndZ=0
    g14: LineSegment StartX=-10.15 StartY=-12 StartZ=0 EndX=-7.79258 EndY=-12 EndZ=0
    g15: Circle CenterX=-6.2215 CenterY=-2 CenterZ=0 NormalX=0 NormalY=0 NormalZ=1 AngleXU=0 Radius=1
    g16: Circle CenterX=-6.22762 CenterY=-2.58724 CenterZ=0 NormalX=0 NormalY=0 NormalZ=1 AngleXU=0 Radius=1
    g17: Circle CenterX=-6.32538 CenterY=-4 CenterZ=0 NormalX=0 NormalY=0 NormalZ=1 AngleXU=0 Radius=1
    g18: BSplineCurve PolesCount=3 KnotsCount=2 Degree=2 IsPeriodic=0
    g19: GeomPoint X=-6.2215 Y=-2 Z=0
    g20: GeomPoint X=-6.32538 Y=-4 Z=0
    g21: Circle CenterX=-6.48644 CenterY=-5.99526 CenterZ=0 NormalX=0 NormalY=0 NormalZ=1 AngleXU=0 Radius=1
    g22: Circle CenterX=-6.58486 CenterY=-6.99526 CenterZ=0 NormalX=0 NormalY=0 NormalZ=1 AngleXU=0 Radius=1
    g23: Circle CenterX=-6.77343 CenterY=-8 CenterZ=0 NormalX=0 NormalY=0 NormalZ=1 AngleXU=0 Radius=1
    g24: BSplineCurve PolesCount=3 KnotsCount=2 Degree=2 IsPeriodic=0
    g25: GeomPoint X=-6.48644 Y=-5.99526 Z=0
    g26: GeomPoint X=-6.77343 Y=-8 Z=0
    g27: Circle CenterX=-7.19003 CenterY=-10 CenterZ=0 NormalX=0 NormalY=0 NormalZ=1 AngleXU=0 Radius=1
    g28: Circle CenterX=-7.44407 CenterY=-11.0915 CenterZ=0 NormalX=0 NormalY=0 NormalZ=1 AngleXU=0 Radius=1
    g29: Circle CenterX=-7.79258 CenterY=-12 CenterZ=0 NormalX=0 NormalY=0 NormalZ=1 AngleXU=0 Radius=1
    g30: BSplineCurve PolesCount=3 KnotsCount=2 Degree=2 IsPeriodic=0
    g31: GeomPoint X=-7.19003 Y=-10 Z=0
    g32: GeomPoint X=-7.79258 Y=-12 Z=0
    g33: Circle CenterX=-8.70761 CenterY=-14 CenterZ=0 NormalX=0 NormalY=0 NormalZ=1 AngleXU=0 Radius=1
    g34: Circle CenterX=-9.33087 CenterY=-15.1837 CenterZ=0 NormalX=0 NormalY=0 NormalZ=1 AngleXU=0 Radius=1
    g35: Circle CenterX=-10.1571 CenterY=-16 CenterZ=0 NormalX=0 NormalY=0 NormalZ=1 AngleXU=0 Radius=1
    g36: BSplineCurve PolesCount=3 KnotsCount=2 Degree=2 IsPeriodic=0
    g37: GeomPoint X=-8.70761 Y=-14 Z=0
    g38: GeomPoint X=-10.1571 Y=-16 Z=0
    g39: Circle CenterX=-12.8401 CenterY=-17.6958 CenterZ=0 NormalX=0 NormalY=0 NormalZ=1 AngleXU=0 Radius=1
    g40: Circle CenterX=-13.3521 CenterY=-17.9027 CenterZ=0 NormalX=0 NormalY=0 NormalZ=1 AngleXU=0 Radius=1
    g41: Circle CenterX=-14 CenterY=-18 CenterZ=0 NormalX=0 NormalY=0 NormalZ=1 AngleXU=0 Radius=1
    g42: BSplineCurve PolesCount=3 KnotsCount=2 Degree=2 IsPeriodic=0
    g43: GeomPoint X=-12.8401 Y=-17.6958 Z=0
    g44: GeomPoint X=-14 Y=-18 Z=0
    g45: LineSegment StartX=-6.2 StartY=0 StartZ=0 EndX=-7.2 EndY=0 EndZ=0
    g46: LineSegment StartX=-7.2 StartY=0 StartZ=0 EndX=-7.2 EndY=-2 EndZ=0
    g47: LineSegment StartX=-7.2 StartY=-2 StartZ=0 EndX=-6.2215 EndY=-2 EndZ=0
    g48: LineSegment StartX=-6.32538 StartY=-4 StartZ=0 EndX=-7.65538 EndY=-4 EndZ=0
    g49: LineSegment StartX=-7.65538 StartY=-4 StartZ=0 EndX=-7.65538 EndY=-5.99526 EndZ=0
    g50: LineSegment StartX=-7.65538 StartY=-5.99526 StartZ=0 EndX=-6.48644 EndY=-5.99526 EndZ=0
    g51: LineSegment StartX=-6.77343 StartY=-8 StartZ=0 EndX=-8.43343 EndY=-8 EndZ=0
    g52: LineSegment StartX=-8.43343 StartY=-8 StartZ=0 EndX=-8.43343 EndY=-10 EndZ=0
    g53: LineSegment StartX=-8.43343 StartY=-10 StartZ=0 EndX=-7.19003 EndY=-10 EndZ=0
  constraints (112):
    c: Horizontal(g0)
    c: Distance(g0) = 2
    c: Block(g0)
    c: Vertical(g1)
    c: Coincident(g2,g0)
    c: Vertical(g2)
    c: Block(g2)
    c: Coincident(g6,g2)
    c: Weight(g3) = 1
    c: Equal(g3,g4)
    c: Equal(g3,g5)
    c: InternalAlignment(g3,g6)
    c: InternalAlignment(g4,g6)
    c: InternalAlignment(g5,g6)
    c: InternalAlignment(g7,g6)
    c: InternalAlignment(g8,g6)
    c: Block(g6)
    c: Coincident(g9,g1)
    c: Coincident(g9,g6)
    c: Horizontal(g9)
    c: Vertical(g10)
    c: Block(g10)
    c: Horizontal(g11)
    c: Block(g11)
    c: Coincident(g12,g10)
    c: Horizontal(g12)
    c: Block(g12)
    c: Coincident(g13,g11)
    c: Vertical(g13)
    c: Block(g13)
    c: Coincident(g14,g10)
    c: Horizontal(g14)
    c: Block(g14)
    c: Block(g9)
    c: Block(g1)
    c: Weight(g15) = 1
    c: Equal(g15,g16)
    c: Equal(g15,g17)
    c: InternalAlignment(g15,g18)
    c: InternalAlignment(g16,g18)
    c: InternalAlignment(g17,g18)
    c: InternalAlignment(g19,g18)
    c: InternalAlignment(g20,g18)
    c: Weight(g21) = 1
    c: Equal(g21,g22)
    c: Equal(g21,g23)
    c: InternalAlignment(g21,g24)
    c: InternalAlignment(g22,g24)
    c: InternalAlignment(g23,g24)
    c: InternalAlignment(g25,g24)
    c: InternalAlignment(g26,g24)
    c: Weight(g27) = 1
    c: Equal(g27,g28)
    c: Equal(g27,g29)
    c: Coincident(g30,g14)
    c: InternalAlignment(g27,g30)
    c: InternalAlignment(g28,g30)
    c: InternalAlignment(g29,g30)
    c: InternalAlignment(g31,g30)
    c: InternalAlignment(g32,g30)
    c: Coincident(g36,g12)
    c: Weight(g33) = 1
    c: Equal(g33,g34)
    c: Equal(g33,g35)
    c: Coincident(g36,g11)
    c: InternalAlignment(g33,g36)
    c: InternalAlignment(g34,g36)
    c: InternalAlignment(g35,g36)
    c: InternalAlignment(g37,g36)
    c: InternalAlignment(g38,g36)
    c: Coincident(g42,g13)
    c: Weight(g39) = 1
    c: Equal(g39,g40)
    c: Equal(g39,g41)
    c: Coincident(g42,g1)
    c: InternalAlignment(g39,g42)
    c: InternalAlignment(g40,g42)
    c: InternalAlignment(g41,g42)
    c: InternalAlignment(g43,g42)
    c: InternalAlignment(g44,g42)
    c: Block(g18)
    c: Block(g24)
    c: Block(g30)
    c: Block(g36)
    c: Block(g42)
    c: Horizontal(g45)
    c: Coincident(g45,g0)
    c: Vertical(g46)
    c: Coincident(g46,g45)
    c: Coincident(g47,g46)
    c: Coincident(g47,g18)
    c: Horizontal(g47)
    c: Block(g46)
    c: Coincident(g48,g18)
    c: Horizontal(g48)
    c: Distance(g48) = 1.33
    c: Vertical(g49)
    c: Coincident(g49,g48)
    c: Coincident(g50,g49)
    c: Coincident(g50,g24)
    c: Horizontal(g50)
    c: Tangent(g50,g22)
    c: Horizontal(g51)
    c: Coincident(g51,g24)
    c: Block(g51)
    c: Vertical(g52)
    c: Block(g52)
    c: Coincident(g52,g51)
    c: Coincident(g53,g52)
    c: Coincident(g53,g30)
    c: Horizontal(g53)
    c: Distance(g1) = 8.5
FEATURE [Part::Feature] Face024
  shape: bbox 9.8 x 26.5 x 2e-07 mm, 1 faces, 0 solids (baked)
FEATURE [Part::Revolution] Revolve024
  Angle = 360
  Axis = (0,1,0)
  Base = (0,0,0)
  FaceMakerClass = Part::FaceMakerBullseye
  Placement = pos=(0,0,0) rot=(0,0,1;1.5708rad)
  Solid = false
  Source = -> Face024
  Symmetric = false
FEATURE [Part::Feature] Face025
  shape: bbox 9.8 x 26.5 x 2e-07 mm, 1 faces, 0 solids (baked)
FEATURE [Part::Revolution] Revolve025
  Angle = 360
  Axis = (0,1,0)
  Base = (0,0,0)
  FaceMakerClass = Part::FaceMakerBullseye
  Placement = pos=(0,0,0) rot=(0,0,1;1.5708rad)
  Solid = false
  Source = -> Face025
  Symmetric = false
FEATURE [Part::MultiFuse] Fusion033
  Placement = pos=(-18,19,36) rot=(0,0,1;0rad)
  Shapes = -> [Revolve025,Revolve024]
FEATURE [Part::Cylinder] Cylinder014
  Angle = 360
  AttacherType = Attacher::AttachEngine3D
  Height = 20
  Placement = pos=(0,0,36.15) rot=(0,0,1;0rad)
  Radius = 14.3
FEATURE [Part::Cylinder] Cylinder015
  Angle = 360
  AttacherType = Attacher::AttachEngine3D
  Height = 10
  Placement = pos=(0,0,36.15) rot=(0,0,1;0rad)
  Radius = 4
FEATURE [Part::MultiFuse] Fusion034  label="removeToCreteHoleForPlugHousing004"
  Placement = pos=(-42,19,36) rot=(0,1,0;1.5708rad)
  Shapes = -> [Cylinder014,Cylinder015]
FEATURE [Part::Cut] Cut008  label="top004"
  Base = -> Cut004
  Placement = pos=(-1,0,0) rot=(0,0,1;0rad)
  Tool = -> Fusion034
FEATURE [Part::Box] Box005  label="Cube005"
  AttacherType = Attacher::AttachEngine3D
  Height = 28
  Length = 3
  Placement = pos=(110.7,19,22) rot=(0,0,1;0rad)
  Width = 15.7
FEATURE [Part::Cylinder] Cylinder016
  Angle = 360
  AttacherType = Attacher::AttachEngine3D
  Height = 10
  Placement = pos=(0,0,36.15) rot=(0,0,1;0rad)
  Radius = 4
FEATURE [Part::Cylinder] Cylinder017
  Angle = 360
  AttacherType = Attacher::AttachEngine3D
  Height = 20
  Placement = pos=(0,0,36.15) rot=(0,0,1;0rad)
  Radius = 10.3
FEATURE [Part::MultiFuse] Fusion035  label="removeToCreteHoleForPlugHousing005"
  Placement = pos=(70,19,36) rot=(0,1,0;1.5708rad)
  Shapes = -> [Cylinder017,Cylinder016]
FEATURE [Part::Cut] Cut009  label="plugHousingTab001"
  Base = -> Box005
  Placement = pos=(-107.4,-14,0) rot=(0,0,1;0rad)
  Tool = -> Fusion035
FEATURE [Part::Box] Box006  label="Cube006"
  AttacherType = Attacher::AttachEngine3D
  Height = 28
  Length = 3
  Placement = pos=(110.7,19,22) rot=(0,0,1;0rad)
  Width = 15.7
FEATURE [Part::Cylinder] Cylinder018
  Angle = 360
  AttacherType = Attacher::AttachEngine3D
  Height = 10
  Placement = pos=(0,0,36.15) rot=(0,0,1;0rad)
  Radius = 4
FEATURE [Part::Cylinder] Cylinder019
  Angle = 360
  AttacherType = Attacher::AttachEngine3D
  Height = 20
  Placement = pos=(0,0,36.15) rot=(0,0,1;0rad)
  Radius = 10.3
FEATURE [Part::MultiFuse] Fusion036  label="removeToCreteHoleForPlugHousing006"
  Placement = pos=(70,19,36) rot=(0,1,0;1.5708rad)
  Shapes = -> [Cylinder019,Cylinder018]
FEATURE [Part::Cut] Cut010  label="plugHousingTab002"
  Base = -> Box006
  Placement = pos=(-107.4,-14,0) rot=(0,0,1;0rad)
  Tool = -> Fusion036
FEATURE [Part::MultiFuse] Fusion037
  Placement = pos=(9.6,23,0) rot=(0,0,1;3.14159rad)
  Shapes = -> [Cut009,Cut010]
FEATURE [Part::Box] Box  label="Cube"
  AttacherType = Attacher::AttachEngine3D
  Height = 10
  Length = 3
  Placement = pos=(3.3,4,12) rot=(0,0,1;0rad)
  Width = 10
FEATURE [Part::Fillet] Fillet004
  Base = -> Fusion028
  Edges = 1 edges r=2: [Edge25]
FEATURE [Part::Fillet] Fillet005  label="plugHousing046"
  Base = -> Fillet004
  Edges = 1 edges r=2: [Edge8]
FEATURE [Part::Fillet] Fillet006
  Base = -> Box
  Edges = 1 edges r=2: [Edge11]
FEATURE [Part::Box] Box007  label="Cube007"
  AttacherType = Attacher::AttachEngine3D
  Height = 10
  Length = 3
  Placement = pos=(3.3,4,50) rot=(0,0,1;0rad)
  Width = 10
FEATURE [Part::Fillet] Fillet007
  Base = -> Box007
  Edges = 1 edges r=2: [Edge12]
FEATURE [Part::Box] Box008  label="Cube008"
  AttacherType = Attacher::AttachEngine3D
  Height = 28
  Length = 4
  Placement = pos=(5,0,22) rot=(0,0,1;0rad)
  Width = 10
FEATURE [Part::Fillet] Fillet008
  Base = -> Box008
  Edges = 1 edges r=1: [Edge7]
FEATURE [Part::Fillet] Fillet009
  Base = -> Fillet008
  Edges = 1 edges r=2: [Edge5]
FEATURE [Part::Fillet] Fillet010
  Base = -> Fillet009
  Edges = 1 edges r=2: [Edge2]
FEATURE [Sketcher::SketchObject] Sketch009  label="topSketch003"
  FullyConstrained = true
  sketch-geometry (4):
    g0: LineSegment StartX=16.8446 StartY=31.512 StartZ=0 EndX=16.3251 EndY=34.4666 EndZ=0
    g1: ArcOfCircle CenterX=19 CenterY=19.2524 CenterZ=0 NormalX=0 NormalY=0 NormalZ=1 AngleXU=0 Radius=15.4476 StartAngle=1.74483 EndAngle=2.72717
    g2: ArcOfCircle CenterX=19 CenterY=19.2524 CenterZ=0 NormalX=0 NormalY=0 NormalZ=1 AngleXU=0 Radius=12.4476 StartAngle=1.74483 EndAngle=2.73189
    g3: LineSegment StartX=4.86004 StartY=25.4725 StartZ=0 EndX=7.58253 EndY=24.2107 EndZ=0
  constraints (7):
    c: Block(g0)
    c: Coincident(g1,g0)
    c: Coincident(g2,g0)
    c: Coincident(g3,g1)
    c: Coincident(g3,g2)
    c: Block(g1)
    c: Block(g2)
FEATURE [Part::Extrusion] Extrude008
  Base = -> Sketch009
  Dir = (0,0,1)
  DirMode = 2
  FaceMakerClass = Part::FaceMakerBullseye
  LengthFwd = 10
  LengthRev = 0
  Placement = pos=(0,0,31) rot=(0,0,1;0rad)
  Solid = true
  Symmetric = false
FEATURE [Part::Cylinder] Cylinder020
  Angle = 360
  AttacherType = Attacher::AttachEngine3D
  Height = 20
  Placement = pos=(0,0,36.15) rot=(0,0,1;0rad)
  Radius = 8.2
FEATURE [Part::Cylinder] Cylinder021
  Angle = 360
  AttacherType = Attacher::AttachEngine3D
  Height = 10
  Placement = pos=(0,0,36.15) rot=(0,0,1;0rad)
  Radius = 4
FEATURE [Part::MultiFuse] Fusion038  label="removeToCreteHoleForPlugHousing007"
  Placement = pos=(-42,19,36) rot=(0,1,0;1.5708rad)
  Shapes = -> [Cylinder020,Cylinder021]
FEATURE [Part::Cut] Cut011
  Base = -> Extrude008
  Tool = -> Fusion038
FEATURE [Part::Fillet] Fillet011
  Base = -> Cut011
  Edges = 1 edges r=2: [Edge1]
FEATURE [Part::Fillet] Fillet012
  Base = -> Fillet011
  Edges = 1 edges r=2.5: [Edge1]
FEATURE [Part::Fillet] Fillet013
  Base = -> Fillet012
  Edges = 1 edges r=2.5: [Edge2]
FEATURE [Part::Box] Box010  label="Cube010"
  AttacherType = Attacher::AttachEngine3D
  Height = 16
  Length = 8
  Placement = pos=(12.7,31.52,28) rot=(0,0,1;0rad)
  Width = 4
FEATURE [Sketcher::SketchObject] Sketch010  label="topSketch004"
  FullyConstrained = true
  sketch-geometry (4):
    g0: LineSegment StartX=16.8446 StartY=31.512 StartZ=0 EndX=16.3251 EndY=34.4666 EndZ=0
    g1: ArcOfCircle CenterX=19 CenterY=19.2524 CenterZ=0 NormalX=0 NormalY=0 NormalZ=1 AngleXU=0 Radius=15.4476 StartAngle=1.74483 EndAngle=2.72717
    g2: ArcOfCircle CenterX=19 CenterY=19.2524 CenterZ=0 NormalX=0 NormalY=0 NormalZ=1 AngleXU=0 Radius=12.4476 StartAngle=1.74483 EndAngle=2.73189
    g3: LineSegment StartX=4.86004 StartY=25.4725 StartZ=0 EndX=7.58253 EndY=24.2107 EndZ=0
  constraints (7):
    c: Block(g0)
    c: Coincident(g1,g0)
    c: Coincident(g2,g0)
    c: Coincident(g3,g1)
    c: Coincident(g3,g2)
    c: Block(g1)
    c: Block(g2)
FEATURE [Part::Cylinder] Cylinder022
  Angle = 360
  AttacherType = Attacher::AttachEngine3D
  Height = 10
  Placement = pos=(0,0,36.15) rot=(0,0,1;0rad)
  Radius = 4
FEATURE [Sketcher::SketchObject] Sketch011  label="topSketch005"
  FullyConstrained = true
  sketch-geometry (4):
    g0: LineSegment StartX=16.8446 StartY=31.512 StartZ=0 EndX=16.3251 EndY=34.4666 EndZ=0
    g1: ArcOfCircle CenterX=19 CenterY=19.2524 CenterZ=0 NormalX=0 NormalY=0 NormalZ=1 AngleXU=0 Radius=15.4476 StartAngle=1.74483 EndAngle=2.72717
    g2: ArcOfCircle CenterX=19 CenterY=19.2524 CenterZ=0 NormalX=0 NormalY=0 NormalZ=1 AngleXU=0 Radius=12.4476 StartAngle=1.74483 EndAngle=2.73189
    g3: LineSegment StartX=4.86004 StartY=25.4725 StartZ=0 EndX=7.58253 EndY=24.2107 EndZ=0
  constraints (7):
    c: Block(g0)
    c: Coincident(g1,g0)
    c: Coincident(g2,g0)
    c: Coincident(g3,g1)
    c: Coincident(g3,g2)
    c: Block(g1)
    c: Block(g2)
FEATURE [Part::Extrusion] Extrude010
  Base = -> Sketch011
  Dir = (0,0,1)
  DirMode = 2
  FaceMakerClass = Part::FaceMakerBullseye
  LengthFwd = 10.6
  LengthRev = 0
  Placement = pos=(0,0,31) rot=(0,0,1;0rad)
  Solid = true
  Symmetric = false
FEATURE [Part::Cylinder] Cylinder023
  Angle = 360
  AttacherType = Attacher::AttachEngine3D
  Height = 20
  Placement = pos=(0,0,36.15) rot=(0,0,1;0rad)
  Radius = 8.2
FEATURE [Part::MultiFuse] Fusion039  label="removeToCreteHoleForPlugHousing008"
  Placement = pos=(-42,19,36) rot=(0,1,0;1.5708rad)
  Shapes = -> [Cylinder023,Cylinder022]
FEATURE [Part::Cut] Cut012
  Base = -> Extrude010
  Placement = pos=(0,0,-0.3) rot=(0,0,1;0rad)
  Tool = -> Fusion039
FEATURE [Part::Cut] Cut013
  Base = -> Box010
  Tool = -> Cut012
FEATURE [Part::Fillet] Fillet014
  Base = -> Cut013
  Edges = 1 edges r=0.7: [Edge13]
FEATURE [Part::Fillet] Fillet015
  Base = -> Fillet014
  Edges = 1 edges r=0.7: [Edge13]
FEATURE [Part::Fillet] Fillet016
  Base = -> Fillet015
  Edges = 1 edges r=0.7: [Edge16]
FEATURE [Part::Fillet] Fillet017
  Base = -> Fillet016
  Edges = 1 edges r=0.7: [Edge11]
FEATURE [Part::Fillet] Fillet018
  Base = -> Fillet017
  Edges = 1 edges r=0.7: [Edge10]
FEATURE [Part::Fillet] Fillet019
  Base = -> Fillet018
  Edges = 1 edges r=1.2: [Edge5]
FEATURE [Part::Fillet] Fillet020
  Base = -> Fillet019
  Edges = 1 edges r=1.2: [Edge12]
FEATURE [Part::Fillet] Fillet021
  Base = -> Fillet020
  Edges = 1 edges r=2: [Edge1]
  Placement = pos=(0.3,0,0) rot=(0,0,1;0rad)
FEATURE [Part::MultiFuse] Fusion040  label="top005"
  Shapes = -> [Cut008,Fillet021]
FEATURE [Part::MultiFuse] Fusion041  label="wireHolder"
  Shapes = -> [Fusion033,Fillet013]
FEATURE [Part::MultiFuse] Fusion042
  Shapes = -> [Fillet007,Fusion041]
FEATURE [Part::MultiFuse] Fusion043  label="wireHolder001"
  Shapes = -> [Fusion042,Fillet010]
FEATURE [Part::MultiFuse] Fusion044  label="wireHolder002"
  Shapes = -> [Fillet006,Fusion037,Fusion043]
FEATURE [Part::Feature] Face026
  shape: bbox 11 x 6 x 2e-07 mm, 1 faces, 0 solids (baked)
FEATURE [Part::Revolution] Revolve026
  Angle = 360
  Axis = (0,1,0)
  Base = (0,0,0)
  FaceMakerClass = Part::FaceMakerBullseye
  Placement = pos=(30.3,-1,19.7) rot=(0,0,1;0rad)
  Solid = false
  Source = -> Face026
  Symmetric = false
FEATURE [Sketcher::SketchObject] Sketch013  label="topSketch006"
  FullyConstrained = true
  sketch-geometry (13):
    g0: LineSegment StartX=117 StartY=19 StartZ=0 EndX=117 EndY=38 EndZ=0
    g1: ArcOfCircle CenterX=98 CenterY=19 CenterZ=0 NormalX=0 NormalY=0 NormalZ=1 AngleXU=0 Radius=19 StartAngle=5.7297 EndAngle=6.28319
    g2: LineSegment StartX=0 StartY=3 StartZ=0 EndX=0 EndY=19 EndZ=0
    g3: LineSegment StartX=19 StartY=38 StartZ=0 EndX=117 EndY=38 EndZ=0
    g4: ArcOfCircle CenterX=19 CenterY=19 CenterZ=0 NormalX=0 NormalY=0 NormalZ=1 AngleXU=0 Radius=19 StartAngle=1.5708 EndAngle=3.14159
    g5: ArcOfCircle CenterX=19 CenterY=19 CenterZ=0 NormalX=0 NormalY=0 NormalZ=1 AngleXU=0 Radius=16 StartAngle=1.5708 EndAngle=3.14159
    g6: ArcOfCircle CenterX=98 CenterY=19 CenterZ=0 NormalX=0 NormalY=0 NormalZ=1 AngleXU=0 Radius=16 StartAngle=5.60905 EndAngle=6.28319
    g7: LineSegment StartX=114 StartY=19 StartZ=0 EndX=114 EndY=35 EndZ=0
    g8: LineSegment StartX=110.5 StartY=9.01251 StartZ=0 EndX=114.163 EndY=9.01251 EndZ=0
    g9: LineSegment StartX=114 StartY=35 StartZ=0 EndX=19 EndY=35 EndZ=0
    g10: LineSegment StartX=0 StartY=3 StartZ=0 EndX=0 EndY=0 EndZ=0
    g11: LineSegment StartX=3 StartY=0 StartZ=0 EndX=0 EndY=0 EndZ=0
    g12: LineSegment StartX=3 StartY=19 StartZ=0 EndX=3 EndY=0 EndZ=0
  constraints (33):
    c: Vertical(g0)
    c: Distance(g0) = 19
    c: Block(g0)
    c: Coincident(g1,g0)
    c: Block(g1)
    c: Vertical(g2)
    c: Block(g2)
    c: Coincident(g3,g0)
    c: Horizontal(g3)
    c: Distance(g3) = 98
    c: Coincident(g4,g3)
    c: Coincident(g4,g2)
    c: Block(g4)
    c: Coincident(g5,g4)
    c: Coincident(g6,g1)
    c: Block(g6)
    c: Block(g5)
    c: Coincident(g7,g6)
    c: Vertical(g7)
    c: Coincident(g8,g6)
    c: Coincident(g8,g1)
    c: Coincident(g9,g7)
    c: Coincident(g9,g5)
    c: Horizontal(g9)
    c: Tangent(g9,g5)
    c: Coincident(g10,g2)
    c: Distance(g10) = 3
    c: Vertical(g10)
    c: Coincident(g11,g10)
    c: Horizontal(g11)
    c: Coincident(g12,g5)
    c: Coincident(g12,g11)
    c: Vertical(g12)
FEATURE [Part::Extrusion] Extrude011  label="top006"
  Base = -> Sketch013
  Dir = (0,0,1)
  DirMode = 2
  FaceMakerClass = Part::FaceMakerBullseye
  LengthFwd = 72
  LengthRev = 0
  Solid = true
  Symmetric = false
FEATURE [Sketcher::SketchObject] Sketch014
  FullyConstrained = true
  MapMode = 3
  Placement = pos=(0,0,0) rot=(1,0,0;1.5708rad)
  Support = -> [Extrude011]
  sketch-geometry (8):
    g0: Circle CenterX=80.351 CenterY=-67.6202 CenterZ=0 NormalX=0 NormalY=0 NormalZ=1 AngleXU=0 Radius=2
    g1: Circle CenterX=80.351 CenterY=-67.6202 CenterZ=0 NormalX=0 NormalY=0 NormalZ=1 AngleXU=0 Radius=3
    g2: Circle CenterX=80.351 CenterY=-4.92017 CenterZ=0 NormalX=0 NormalY=0 NormalZ=1 AngleXU=0 Radius=2
    g3: Circle CenterX=80.351 CenterY=-4.92017 CenterZ=0 NormalX=0 NormalY=0 NormalZ=1 AngleXU=0 Radius=3
    g4: Circle CenterX=23.851 CenterY=-4.92017 CenterZ=0 NormalX=0 NormalY=0 NormalZ=1 AngleXU=0 Radius=2
    g5: Circle CenterX=23.851 CenterY=-4.92017 CenterZ=0 NormalX=0 NormalY=0 NormalZ=1 AngleXU=0 Radius=3
    g6: Circle CenterX=23.851 CenterY=-67.6202 CenterZ=0 NormalX=0 NormalY=0 NormalZ=1 AngleXU=0 Radius=2
    g7: Circle CenterX=23.851 CenterY=-67.6202 CenterZ=0 NormalX=0 NormalY=0 NormalZ=1 AngleXU=0 Radius=3
  constraints (8):
    c: Block(g3)
    c: Block(g2)
    c: Block(g1)
    c: Block(g0)
    c: Block(g6)
    c: Block(g7)
    c: Block(g4)
    c: Block(g5)
FEATURE [Part::Feature] Face027
  shape: bbox 11 x 6 x 2e-07 mm, 1 faces, 0 solids (baked)
FEATURE [Part::Revolution] Revolve027
  Angle = 360
  Axis = (0,1,0)
  Base = (0,0,0)
  FaceMakerClass = Part::FaceMakerBullseye
  Placement = pos=(30.3,-1,51.7) rot=(0,0,1;0rad)
  Solid = false
  Source = -> Face027
  Symmetric = false
FEATURE [Part::Feature] Face028
  shape: bbox 11 x 6 x 2e-07 mm, 1 faces, 0 solids (baked)
FEATURE [Part::Revolution] Revolve028
  Angle = 360
  Axis = (0,1,0)
  Base = (0,0,0)
  FaceMakerClass = Part::FaceMakerBullseye
  Placement = pos=(62.3,-1,19.7) rot=(0,0,1;0rad)
  Solid = false
  Source = -> Face028
  Symmetric = false
FEATURE [Part::Feature] Face029
  shape: bbox 11 x 6 x 2e-07 mm, 1 faces, 0 solids (baked)
FEATURE [Part::Revolution] Revolve029
  Angle = 360
  Axis = (0,1,0)
  Base = (0,0,0)
  FaceMakerClass = Part::FaceMakerBullseye
  Placement = pos=(62.3,-1,51.7) rot=(0,0,1;0rad)
  Solid = false
  Source = -> Face029
  Symmetric = false
FEATURE [Part::Feature] Wire
  shape: bbox 11 x 5.2 x 2e-07 mm, 0 faces, 0 solids (baked)
FEATURE [Part::Revolution] Revolve030
  Angle = 360
  Axis = (0,1,0)
  Base = (0,0,0)
  FaceMakerClass = Part::FaceMakerBullseye
  Placement = pos=(30.3,38,19.7) rot=(0,0,1;0rad)
  Solid = true
  Source = -> Wire
  Symmetric = false
FEATURE [Part::Feature] Wire001
  shape: bbox 11 x 5.2 x 2e-07 mm, 0 faces, 0 solids (baked)
FEATURE [Part::Revolution] Revolve031
  Angle = 360
  Axis = (0,1,0)
  Base = (0,0,0)
  FaceMakerClass = Part::FaceMakerBullseye
  Placement = pos=(30.3,38,51.7) rot=(0,0,1;0rad)
  Solid = true
  Source = -> Wire001
  Symmetric = false
FEATURE [Part::Feature] Wire002
  shape: bbox 11 x 5.2 x 2e-07 mm, 0 faces, 0 solids (baked)
FEATURE [Part::Revolution] Revolve032
  Angle = 360
  Axis = (0,1,0)
  Base = (0,0,0)
  FaceMakerClass = Part::FaceMakerBullseye
  Placement = pos=(62.3,38,51.7) rot=(0,0,1;0rad)
  Solid = true
  Source = -> Wire002
  Symmetric = false
FEATURE [Part::Feature] Wire003
  shape: bbox 11 x 5.2 x 2e-07 mm, 0 faces, 0 solids (baked)
FEATURE [Part::Revolution] Revolve033
  Angle = 360
  Axis = (0,1,0)
  Base = (0,0,0)
  FaceMakerClass = Part::FaceMakerBullseye
  Placement = pos=(62.3,38,19.7) rot=(0,0,1;0rad)
  Solid = true
  Source = -> Wire003
  Symmetric = false
FEATURE [Part::MultiFuse] Fusion045  label="altRandScrewHousing"
  Shapes = -> [Revolve029,Revolve027,Revolve028,Revolve026]
FEATURE [Part::MultiFuse] Fusion046  label="fanScrewHousing"
  Shapes = -> [Revolve033,Revolve032,Revolve031,Revolve030]
FEATURE [Sketcher::SketchObject] Sketch015
  FullyConstrained = true
  sketch-geometry (17):
    g0: Circle CenterX=-3.5 CenterY=23.5 CenterZ=0 NormalX=0 NormalY=0 NormalZ=1 AngleXU=0 Radius=1
    g1: Circle CenterX=-1 CenterY=15.25 CenterZ=0 NormalX=0 NormalY=0 NormalZ=1 AngleXU=0 Radius=1
    g2: Circle CenterX=-3.5 CenterY=7 CenterZ=0 NormalX=0 NormalY=0 NormalZ=1 AngleXU=0 Radius=1
    g3: BSplineCurve PolesCount=3 KnotsCount=2 Degree=2 IsPeriodic=0
    g4: GeomPoint X=-3.5 Y=23.5 Z=0
    g5: GeomPoint X=-3.5 Y=7 Z=0
    g6: Circle CenterX=-4.8 CenterY=30.5 CenterZ=0 NormalX=0 NormalY=0 NormalZ=1 AngleXU=0 Radius=1
    g7: Circle CenterX=-3.5 CenterY=30.5 CenterZ=0 NormalX=0 NormalY=0 NormalZ=1 AngleXU=0 Radius=1
    g8: Circle CenterX=-3.5 CenterY=29.2 CenterZ=0 NormalX=0 NormalY=0 NormalZ=1 AngleXU=0 Radius=1
    g9: BSplineCurve PolesCount=3 KnotsCount=2 Degree=2 IsPeriodic=0
    g10: GeomPoint X=-4.8 Y=30.5 Z=0
    g11: GeomPoint X=-3.5 Y=29.2 Z=0
    g12: LineSegment StartX=-3.5 StartY=29.2 StartZ=0 EndX=-3.5 EndY=23.5 EndZ=0
    g13: LineSegment StartX=-4.8 StartY=30.5 StartZ=0 EndX=0 EndY=30.5 EndZ=0
    g14: LineSegment StartX=-3.5 StartY=0.3 StartZ=0 EndX=0 EndY=0.3 EndZ=0
    g15: LineSegment StartX=-3.5 StartY=0.3 StartZ=0 EndX=-3.5 EndY=7 EndZ=0
    g16: LineSegment StartX=0 StartY=0.3 StartZ=0 EndX=0 EndY=30.5 EndZ=0
  constraints (33):
    c: Weight(g0) = 1
    c: Equal(g0,g1)
    c: Equal(g0,g2)
    c: InternalAlignment(g0,g3)
    c: InternalAlignment(g1,g3)
    c: InternalAlignment(g2,g3)
    c: InternalAlignment(g4,g3)
    c: InternalAlignment(g5,g3)
    c: Block(g3)
    c: Weight(g6) = 1
    c: Equal(g6,g7)
    c: Equal(g6,g8)
    c: InternalAlignment(g6,g9)
    c: InternalAlignment(g7,g9)
    c: InternalAlignment(g8,g9)
    c: InternalAlignment(g10,g9)
    c: InternalAlignment(g11,g9)
    c: Block(g9)
    c: Coincident(g12,g9)
    c: Coincident(g12,g3)
    c: Vertical(g12)
    c: Coincident(g13,g9)
    c: Horizontal(g13)
    c: Distance(g13) = 4.8
    c: Horizontal(g14)
    c: Block(g14)
    c: Coincident(g15,g14)
    c: Coincident(g15,g3)
    c: Vertical(g15)
    c: Coincident(g16,g14)
    c: Coincident(g16,g13)
    c: Vertical(g16)
    c: Tangent(g16,g1)
FEATURE [Sketcher::SketchObject] Sketch016
  FullyConstrained = true
  sketch-geometry (16):
    g0: Circle CenterX=-3.5 CenterY=23.5 CenterZ=0 NormalX=0 NormalY=0 NormalZ=1 AngleXU=0 Radius=1
    g1: Circle CenterX=-1 CenterY=15.25 CenterZ=0 NormalX=0 NormalY=0 NormalZ=1 AngleXU=0 Radius=1
    g2: Circle CenterX=-3.5 CenterY=7 CenterZ=0 NormalX=0 NormalY=0 NormalZ=1 AngleXU=0 Radius=1
    g3: BSplineCurve PolesCount=3 KnotsCount=2 Degree=2 IsPeriodic=0
    g4: GeomPoint X=-3.5 Y=23.5 Z=0
    g5: GeomPoint X=-3.5 Y=7 Z=0
    g6: LineSegment StartX=-3.5 StartY=28.2 StartZ=0 EndX=-3.5 EndY=23.5 EndZ=0
    g7: LineSegment StartX=0 StartY=29.5 StartZ=0 EndX=0 EndY=30 EndZ=0
    g8: LineSegment StartX=-3.5 StartY=28.2 StartZ=0 EndX=-3.5 EndY=30 EndZ=0
    g9: LineSegment StartX=0 StartY=30 StartZ=0 EndX=0 EndY=30.5 EndZ=0
    g10: LineSegment StartX=0 StartY=30.5 StartZ=0 EndX=-3.5 EndY=30.5 EndZ=0
    g11: LineSegment StartX=-3.5 StartY=30.5 StartZ=0 EndX=-3.5 EndY=30 EndZ=0
    g12: LineSegment StartX=0 StartY=29.5 StartZ=0 EndX=0 EndY=5 EndZ=0
    g13: LineSegment StartX=-3.5 StartY=0.3 StartZ=0 EndX=-3.5 EndY=7 EndZ=0
    g14: LineSegment StartX=-3.5 StartY=0.3 StartZ=0 EndX=0 EndY=0.3 EndZ=0
    g15: LineSegment StartX=0 StartY=5 StartZ=0 EndX=0 EndY=0.3 EndZ=0
  constraints (39):
    c: Weight(g0) = 1
    c: Equal(g0,g1)
    c: Equal(g0,g2)
    c: InternalAlignment(g0,g3)
    c: InternalAlignment(g1,g3)
    c: InternalAlignment(g2,g3)
    c: InternalAlignment(g4,g3)
    c: InternalAlignment(g5,g3)
    c: Block(g3)
    c: Coincident(g6,g3)
    c: Vertical(g6)
    c: Vertical(g7)
    c: Distance(g7) = 0.5
    c: Coincident(g8,g6)
    c: Vertical(g8)
    c: Block(g6)
    c: Block(g7)
    c: Vertical(g9)
    c: Equal(g7,g9) = 0.5
    c: Block(g9)
    c: Coincident(g9,g7)
    c: Horizontal(g10)
    c: Coincident(g10,g9)
    c: Coincident(g11,g10)
    c: Coincident(g11,g8)
    c: Vertical(g11)
    c: Block(g11)
    c: Coincident(g12,g7)
    c: Vertical(g12)
    c: Coincident(g13,g3)
    c: Vertical(g13)
    c: Distance(g13) = 6.7
    c: Coincident(g14,g13)
    c: Horizontal(g14)
    c: Block(g14)
    c: Coincident(g15,g12)
    c: Coincident(g15,g14)
    c: Vertical(g15)
    c: Block(g15)
FEATURE [Sketcher::SketchObject] Sketch017
  FullyConstrained = true
  sketch-geometry (11):
    g0: LineSegment StartX=-3.5 StartY=1e-16 StartZ=0 EndX=-1.6 EndY=1e-16 EndZ=0
    g1: LineSegment StartX=-1.6 StartY=1e-16 StartZ=0 EndX=-1.6 EndY=1.5 EndZ=0
    g2: LineSegment StartX=-3.5 StartY=1.5 StartZ=0 EndX=-1.6 EndY=1.5 EndZ=0
    g3: LineSegment StartX=-3.5 StartY=1e-16 StartZ=0 EndX=-4.8 EndY=1e-16 EndZ=0
    g4: Circle CenterX=-3.5 CenterY=1.3 CenterZ=0 NormalX=0 NormalY=0 NormalZ=1 AngleXU=0 Radius=1
    g5: Circle CenterX=-3.5 CenterY=1e-16 CenterZ=0 NormalX=0 NormalY=0 NormalZ=1 AngleXU=0 Radius=1
    g6: Circle CenterX=-4.8 CenterY=1e-16 CenterZ=0 NormalX=0 NormalY=0 NormalZ=1 AngleXU=0 Radius=1
    g7: BSplineCurve PolesCount=3 KnotsCount=2 Degree=2 IsPeriodic=0
    g8: GeomPoint X=-3.5 Y=1.3 Z=0
    g9: GeomPoint X=-4.8 Y=1e-16 Z=0
    g10: LineSegment StartX=-3.5 StartY=1.3 StartZ=0 EndX=-3.5 EndY=1.5 EndZ=0
  constraints (24):
    c: Horizontal(g0)
    c: Distance(g0) = 1.9
    c: Block(g0)
    c: Coincident(g1,g0)
    c: Vertical(g1)
    c: Coincident(g2,g1)
    c: Horizontal(g2)
    c: Coincident(g3,g0)
    c: Horizontal(g3)
    c: Distance(g3) = 1.3
    c: Weight(g4) = 1
    c: Equal(g4,g5)
    c: Coincident(g5,g0)
    c: Equal(g4,g6)
    c: Coincident(g7,g3)
    c: InternalAlignment(g4,g7)
    c: InternalAlignment(g5,g7)
    c: InternalAlignment(g6,g7)
    c: InternalAlignment(g8,g7)
    c: InternalAlignment(g9,g7)
    c: Coincident(g10,g7)
    c: Coincident(g10,g2)
    c: Vertical(g10)
    c: Block(g10)
FEATURE [Part::Feature] Face035
  shape: bbox 3.2 x 1.5 x 2e-07 mm, 1 faces, 0 solids (baked)
FEATURE [Part::Revolution] Revolve039  label="backCaseScrewRetainer"
  Angle = 360
  Axis = (0,1,0)
  Base = (0,0,0)
  FaceMakerClass = Part::FaceMakerBullseye
  Placement = pos=(12.5,3,62) rot=(0,0,1;0rad)
  Solid = false
  Source = -> Face035
  Symmetric = false
FEATURE [Part::Feature] Face036
  shape: bbox 3.2 x 1.5 x 2e-07 mm, 1 faces, 0 solids (baked)
FEATURE [Part::Feature] Face039
  shape: bbox 4.8 x 30.2 x 2e-07 mm, 1 faces, 0 solids (baked)
FEATURE [Part::Revolution] Revolve043  label="frontCaseScrewPost002"
  Angle = 360
  Axis = (0,1,0)
  Base = (0,0,0)
  FaceMakerClass = Part::FaceMakerBullseye
  Placement = pos=(89.5,4.5,3.5) rot=(0,0,1;0rad)
  Solid = false
  Source = -> Face039
  Symmetric = false
FEATURE [Part::Feature] Face042
  shape: bbox 4.8 x 30.2 x 2e-07 mm, 1 faces, 0 solids (baked)
FEATURE [Part::Revolution] Revolve046  label="frontCaseScrewPost003"
  Angle = 360
  Axis = (0,1,0)
  Base = (0,0,0)
  FaceMakerClass = Part::FaceMakerBullseye
  Placement = pos=(89.5,4.5,68.5) rot=(0,0,1;0rad)
  Solid = false
  Source = -> Face042
  Symmetric = false
FEATURE [Part::Feature] Face043
  shape: bbox 3.2 x 1.5 x 2e-07 mm, 1 faces, 0 solids (baked)
FEATURE [Part::Revolution] Revolve047  label="frontCaseScrewRetainer002"
  Angle = 360
  Axis = (0,1,0)
  Base = (0,0,0)
  FaceMakerClass = Part::FaceMakerBullseye
  Placement = pos=(89.5,3,68.5) rot=(0,0,1;0rad)
  Solid = false
  Source = -> Face043
  Symmetric = false
FEATURE [Part::Feature] Face044
  shape: bbox 3.2 x 1.5 x 2e-07 mm, 1 faces, 0 solids (baked)
FEATURE [Part::Revolution] Revolve048  label="frontCaseScrewRetainer003"
  Angle = 360
  Axis = (0,1,0)
  Base = (0,0,0)
  FaceMakerClass = Part::FaceMakerBullseye
  Placement = pos=(89.5,3,3.5) rot=(0,0,1;0rad)
  Solid = false
  Source = -> Face044
  Symmetric = false
FEATURE [App::MeasureDistance] Distance002  label="Distance: 1.67 mm"
  Distance = 1.66921
  P1 = (99.2361,4.7524,71.7)
  P2 = (99.2347,6.42161,71.7)
FEATURE [Sketcher::SketchObject] Sketch018
  FullyConstrained = true
  sketch-geometry (7):
    g0: LineSegment StartX=0 StartY=0 StartZ=0 EndX=0 EndY=6 EndZ=0
    g1: Circle CenterX=0 CenterY=0 CenterZ=0 NormalX=0 NormalY=0 NormalZ=1 AngleXU=0 Radius=1
    g2: Circle CenterX=8 CenterY=6 CenterZ=0 NormalX=0 NormalY=0 NormalZ=1 AngleXU=0 Radius=1
    g3: BSplineCurve PolesCount=3 KnotsCount=2 Degree=2 IsPeriodic=0
    g4: GeomPoint X=0 Y=0 Z=0
    g5: GeomPoint X=8 Y=6 Z=0
    g6: LineSegment StartX=0 StartY=6 StartZ=0 EndX=8 EndY=6 EndZ=0
  constraints (14):
    c: Coincident(g0,g-1)
    c: Distance(g0) = 6
    c: Vertical(g0)
    c: Coincident(g3,g0)
    c: Weight(g1) = 1
    c: Equal(g1,g2)
    c: InternalAlignment(g1,g3)
    c: InternalAlignment(g2,g3)
    c: InternalAlignment(g4,g3)
    c: InternalAlignment(g5,g3)
    c: Block(g3)
    c: Coincident(g6,g0)
    c: Coincident(g6,g3)
    c: Horizontal(g6)
FEATURE [Part::Extrusion] Extrude012  label="caseScrewPillarBracket"
  Base = -> Sketch018
  Dir = (0,0,1)
  DirMode = 2
  FaceMakerClass = Part::FaceMakerBullseye
  LengthFwd = 2.4
  LengthRev = 0
  Placement = pos=(15.76,29,8.8) rot=(0,1,0;0rad)
  Solid = true
  Symmetric = false
FEATURE [Sketcher::SketchObject] Sketch019
  FullyConstrained = true
  sketch-geometry (7):
    g0: LineSegment StartX=0 StartY=0 StartZ=0 EndX=0 EndY=6 EndZ=0
    g1: Circle CenterX=0 CenterY=0 CenterZ=0 NormalX=0 NormalY=0 NormalZ=1 AngleXU=0 Radius=1
    g2: Circle CenterX=8 CenterY=6 CenterZ=0 NormalX=0 NormalY=0 NormalZ=1 AngleXU=0 Radius=1
    g3: BSplineCurve PolesCount=3 KnotsCount=2 Degree=2 IsPeriodic=0
    g4: GeomPoint X=0 Y=0 Z=0
    g5: GeomPoint X=8 Y=6 Z=0
    g6: LineSegment StartX=0 StartY=6 StartZ=0 EndX=8 EndY=6 EndZ=0
  constraints (14):
    c: Coincident(g0,g-1)
    c: Distance(g0) = 6
    c: Vertical(g0)
    c: Coincident(g3,g0)
    c: Weight(g1) = 1
    c: Equal(g1,g2)
    c: InternalAlignment(g1,g3)
    c: InternalAlignment(g2,g3)
    c: InternalAlignment(g4,g3)
    c: InternalAlignment(g5,g3)
    c: Block(g3)
    c: Coincident(g6,g0)
    c: Coincident(g6,g3)
    c: Horizontal(g6)
FEATURE [Part::Extrusion] Extrude013  label="caseScrewPillarBracket001"
  Base = -> Sketch019
  Dir = (0,0,1)
  DirMode = 2
  FaceMakerClass = Part::FaceMakerBullseye
  LengthFwd = 2.4
  LengthRev = 0
  Placement = pos=(15.76,29,60.8) rot=(0,0,1;0rad)
  Solid = true
  Symmetric = false
FEATURE [Sketcher::SketchObject] Sketch020
  FullyConstrained = true
  sketch-geometry (7):
    g0: LineSegment StartX=0 StartY=0 StartZ=0 EndX=0 EndY=6 EndZ=0
    g1: Circle CenterX=0 CenterY=0 CenterZ=0 NormalX=0 NormalY=0 NormalZ=1 AngleXU=0 Radius=1
    g2: Circle CenterX=8 CenterY=6 CenterZ=0 NormalX=0 NormalY=0 NormalZ=1 AngleXU=0 Radius=1
    g3: BSplineCurve PolesCount=3 KnotsCount=2 Degree=2 IsPeriodic=0
    g4: GeomPoint X=0 Y=0 Z=0
    g5: GeomPoint X=8 Y=6 Z=0
    g6: LineSegment StartX=0 StartY=6 StartZ=0 EndX=8 EndY=6 EndZ=0
  constraints (14):
    c: Coincident(g0,g-1)
    c: Distance(g0) = 6
    c: Vertical(g0)
    c: Coincident(g3,g0)
    c: Weight(g1) = 1
    c: Equal(g1,g2)
    c: InternalAlignment(g1,g3)
    c: InternalAlignment(g2,g3)
    c: InternalAlignment(g4,g3)
    c: InternalAlignment(g5,g3)
    c: Block(g3)
    c: Coincident(g6,g0)
    c: Coincident(g6,g3)
    c: Horizontal(g6)
FEATURE [Part::Extrusion] Extrude014  label="caseScrewPillarBracket002"
  Base = -> Sketch020
  Dir = (0,0,1)
  DirMode = 2
  FaceMakerClass = Part::FaceMakerBullseye
  LengthFwd = 2.4
  LengthRev = 0
  Placement = pos=(13.7,29,13.26) rot=(0,-1,0;1.5708rad)
  Solid = true
  Symmetric = false
FEATURE [Sketcher::SketchObject] Sketch021
  FullyConstrained = true
  sketch-geometry (7):
    g0: LineSegment StartX=0 StartY=0 StartZ=0 EndX=0 EndY=6 EndZ=0
    g1: Circle CenterX=0 CenterY=0 CenterZ=0 NormalX=0 NormalY=0 NormalZ=1 AngleXU=0 Radius=1
    g2: Circle CenterX=8 CenterY=6 CenterZ=0 NormalX=0 NormalY=0 NormalZ=1 AngleXU=0 Radius=1
    g3: BSplineCurve PolesCount=3 KnotsCount=2 Degree=2 IsPeriodic=0
    g4: GeomPoint X=0 Y=0 Z=0
    g5: GeomPoint X=8 Y=6 Z=0
    g6: LineSegment StartX=0 StartY=6 StartZ=0 EndX=8 EndY=6 EndZ=0
  constraints (14):
    c: Coincident(g0,g-1)
    c: Distance(g0) = 6
    c: Vertical(g0)
    c: Coincident(g3,g0)
    c: Weight(g1) = 1
    c: Equal(g1,g2)
    c: InternalAlignment(g1,g3)
    c: InternalAlignment(g2,g3)
    c: InternalAlignment(g4,g3)
    c: InternalAlignment(g5,g3)
    c: Block(g3)
    c: Coincident(g6,g0)
    c: Coincident(g6,g3)
    c: Horizontal(g6)
FEATURE [Part::Extrusion] Extrude015  label="caseScrewPillarBracket003"
  Base = -> Sketch021
  Dir = (0,0,1)
  DirMode = 2
  FaceMakerClass = Part::FaceMakerBullseye
  LengthFwd = 2.4
  LengthRev = 0
  Placement = pos=(11.3,29,58.74) rot=(0,1,0;1.5708rad)
  Solid = true
  Symmetric = false
FEATURE [Sketcher::SketchObject] Sketch022
  FullyConstrained = true
  sketch-geometry (7):
    g0: LineSegment StartX=0 StartY=0 StartZ=0 EndX=0 EndY=6 EndZ=0
    g1: Circle CenterX=0 CenterY=0 CenterZ=0 NormalX=0 NormalY=0 NormalZ=1 AngleXU=0 Radius=1
    g2: Circle CenterX=8 CenterY=6 CenterZ=0 NormalX=0 NormalY=0 NormalZ=1 AngleXU=0 Radius=1
    g3: BSplineCurve PolesCount=3 KnotsCount=2 Degree=2 IsPeriodic=0
    g4: GeomPoint X=0 Y=0 Z=0
    g5: GeomPoint X=8 Y=6 Z=0
    g6: LineSegment StartX=0 StartY=6 StartZ=0 EndX=8 EndY=6 EndZ=0
  constraints (14):
    c: Coincident(g0,g-1)
    c: Distance(g0) = 6
    c: Vertical(g0)
    c: Coincident(g3,g0)
    c: Weight(g1) = 1
    c: Equal(g1,g2)
    c: InternalAlignment(g1,g3)
    c: InternalAlignment(g2,g3)
    c: InternalAlignment(g4,g3)
    c: InternalAlignment(g5,g3)
    c: Block(g3)
    c: Coincident(g6,g0)
    c: Coincident(g6,g3)
    c: Horizontal(g6)
FEATURE [Part::Extrusion] Extrude016  label="caseScrewPillarBracket004"
  Base = -> Sketch022
  Dir = (0,0,1)
  DirMode = 2
  FaceMakerClass = Part::FaceMakerBullseye
  LengthFwd = 2.4
  LengthRev = 0
  Placement = pos=(88.3,29,65.23) rot=(0,1,0;1.5708rad)
  Solid = true
  Symmetric = false
FEATURE [Sketcher::SketchObject] Sketch023
  FullyConstrained = true
  sketch-geometry (7):
    g0: LineSegment StartX=0 StartY=0 StartZ=0 EndX=0 EndY=6 EndZ=0
    g1: Circle CenterX=0 CenterY=0 CenterZ=0 NormalX=0 NormalY=0 NormalZ=1 AngleXU=0 Radius=1
    g2: Circle CenterX=8 CenterY=6 CenterZ=0 NormalX=0 NormalY=0 NormalZ=1 AngleXU=0 Radius=1
    g3: BSplineCurve PolesCount=3 KnotsCount=2 Degree=2 IsPeriodic=0
    g4: GeomPoint X=0 Y=0 Z=0
    g5: GeomPoint X=8 Y=6 Z=0
    g6: LineSegment StartX=0 StartY=6 StartZ=0 EndX=8 EndY=6 EndZ=0
  constraints (14):
    c: Coincident(g0,g-1)
    c: Distance(g0) = 6
    c: Vertical(g0)
    c: Coincident(g3,g0)
    c: Weight(g1) = 1
    c: Equal(g1,g2)
    c: InternalAlignment(g1,g3)
    c: InternalAlignment(g2,g3)
    c: InternalAlignment(g4,g3)
    c: InternalAlignment(g5,g3)
    c: Block(g3)
    c: Coincident(g6,g0)
    c: Coincident(g6,g3)
    c: Horizontal(g6)
FEATURE [Part::Extrusion] Extrude017  label="caseScrewPillarBracket005"
  Base = -> Sketch023
  Dir = (0,0,1)
  DirMode = 2
  FaceMakerClass = Part::FaceMakerBullseye
  LengthFwd = 2.4
  LengthRev = 0
  Placement = pos=(90.7,29,6.77) rot=(0,-1,0;1.5708rad)
  Solid = true
  Symmetric = false
FEATURE [Sketcher::SketchObject] Sketch024
  FullyConstrained = true
  sketch-geometry (7):
    g0: LineSegment StartX=0 StartY=0 StartZ=0 EndX=0 EndY=6 EndZ=0
    g1: Circle CenterX=0 CenterY=0 CenterZ=0 NormalX=0 NormalY=0 NormalZ=1 AngleXU=0 Radius=1
    g2: Circle CenterX=8 CenterY=6 CenterZ=0 NormalX=0 NormalY=0 NormalZ=1 AngleXU=0 Radius=1
    g3: BSplineCurve PolesCount=3 KnotsCount=2 Degree=2 IsPeriodic=0
    g4: GeomPoint X=0 Y=0 Z=0
    g5: GeomPoint X=8 Y=6 Z=0
    g6: LineSegment StartX=0 StartY=6 StartZ=0 EndX=8 EndY=6 EndZ=0
  constraints (14):
    c: Coincident(g0,g-1)
    c: Distance(g0) = 6
    c: Vertical(g0)
    c: Coincident(g3,g0)
    c: Weight(g1) = 1
    c: Equal(g1,g2)
    c: InternalAlignment(g1,g3)
    c: InternalAlignment(g2,g3)
    c: InternalAlignment(g4,g3)
    c: InternalAlignment(g5,g3)
    c: Block(g3)
    c: Coincident(g6,g0)
    c: Coincident(g6,g3)
    c: Horizontal(g6)
FEATURE [Part::Extrusion] Extrude018  label="caseScrewPillarBracket006"
  Base = -> Sketch024
  Dir = (0,0,1)
  DirMode = 2
  FaceMakerClass = Part::FaceMakerBullseye
  LengthFwd = 2.4
  LengthRev = 0
  Placement = pos=(103.7,29,6.77) rot=(0,-1,0;1.5708rad)
  Solid = true
  Symmetric = false
FEATURE [Sketcher::SketchObject] Sketch025
  FullyConstrained = true
  sketch-geometry (7):
    g0: LineSegment StartX=0 StartY=0 StartZ=0 EndX=0 EndY=6 EndZ=0
    g1: Circle CenterX=0 CenterY=0 CenterZ=0 NormalX=0 NormalY=0 NormalZ=1 AngleXU=0 Radius=1
    g2: Circle CenterX=8 CenterY=6 CenterZ=0 NormalX=0 NormalY=0 NormalZ=1 AngleXU=0 Radius=1
    g3: BSplineCurve PolesCount=3 KnotsCount=2 Degree=2 IsPeriodic=0
    g4: GeomPoint X=0 Y=0 Z=0
    g5: GeomPoint X=8 Y=6 Z=0
    g6: LineSegment StartX=0 StartY=6 StartZ=0 EndX=8 EndY=6 EndZ=0
  constraints (14):
    c: Coincident(g0,g-1)
    c: Distance(g0) = 6
    c: Vertical(g0)
    c: Coincident(g3,g0)
    c: Weight(g1) = 1
    c: Equal(g1,g2)
    c: InternalAlignment(g1,g3)
    c: InternalAlignment(g2,g3)
    c: InternalAlignment(g4,g3)
    c: InternalAlignment(g5,g3)
    c: Block(g3)
    c: Coincident(g6,g0)
    c: Coincident(g6,g3)
    c: Horizontal(g6)
FEATURE [Part::Extrusion] Extrude019  label="caseScrewPillarBracket007"
  Base = -> Sketch025
  Dir = (0,0,1)
  DirMode = 2
  FaceMakerClass = Part::FaceMakerBullseye
  LengthFwd = 2.4
  LengthRev = 0
  Placement = pos=(101.3,29,65.23) rot=(0,1,0;1.5708rad)
  Solid = true
  Symmetric = false
FEATURE [Part::Box] Box011  label="frontCaseScrewPillarBracket"
  AttacherType = Attacher::AttachEngine3D
  Height = 2.4
  Length = 16
  Placement = pos=(87,28,2.3) rot=(0,0,1;0rad)
  Width = 7
FEATURE [Part::Box] Box012  label="frontCaseScrewPillarBracket001"
  AttacherType = Attacher::AttachEngine3D
  Height = 2.4
  Length = 16
  Placement = pos=(87,28,67.3) rot=(0,0,1;0rad)
  Width = 7
FEATURE [Sketcher::SketchObject] Sketch026
  FullyConstrained = true
  sketch-geometry (17):
    g0: Circle CenterX=-3.5 CenterY=23.5 CenterZ=0 NormalX=0 NormalY=0 NormalZ=1 AngleXU=0 Radius=1
    g1: Circle CenterX=-1 CenterY=15.25 CenterZ=0 NormalX=0 NormalY=0 NormalZ=1 AngleXU=0 Radius=1
    g2: Circle CenterX=-3.5 CenterY=7 CenterZ=0 NormalX=0 NormalY=0 NormalZ=1 AngleXU=0 Radius=1
    g3: BSplineCurve PolesCount=3 KnotsCount=2 Degree=2 IsPeriodic=0
    g4: GeomPoint X=-3.5 Y=23.5 Z=0
    g5: GeomPoint X=-3.5 Y=7 Z=0
    g6: Circle CenterX=-4.8 CenterY=30.5 CenterZ=0 NormalX=0 NormalY=0 NormalZ=1 AngleXU=0 Radius=1
    g7: Circle CenterX=-3.5 CenterY=30.5 CenterZ=0 NormalX=0 NormalY=0 NormalZ=1 AngleXU=0 Radius=1
    g8: Circle CenterX=-3.5 CenterY=29.2 CenterZ=0 NormalX=0 NormalY=0 NormalZ=1 AngleXU=0 Radius=1
    g9: BSplineCurve PolesCount=3 KnotsCount=2 Degree=2 IsPeriodic=0
    g10: GeomPoint X=-4.8 Y=30.5 Z=0
    g11: GeomPoint X=-3.5 Y=29.2 Z=0
    g12: LineSegment StartX=-3.5 StartY=29.2 StartZ=0 EndX=-3.5 EndY=23.5 EndZ=0
    g13: LineSegment StartX=-4.8 StartY=30.5 StartZ=0 EndX=0 EndY=30.5 EndZ=0
    g14: LineSegment StartX=-3.5 StartY=5 StartZ=0 EndX=-3.5 EndY=7 EndZ=0
    g15: LineSegment StartX=0 StartY=5 StartZ=0 EndX=0 EndY=30.5 EndZ=0
    g16: LineSegment StartX=-3.5 StartY=5 StartZ=0 EndX=0 EndY=5 EndZ=0
  constraints (33):
    c: Weight(g0) = 1
    c: Equal(g0,g1)
    c: Equal(g0,g2)
    c: InternalAlignment(g0,g3)
    c: InternalAlignment(g1,g3)
    c: InternalAlignment(g2,g3)
    c: InternalAlignment(g4,g3)
    c: InternalAlignment(g5,g3)
    c: Block(g3)
    c: Weight(g6) = 1
    c: Equal(g6,g7)
    c: Equal(g6,g8)
    c: InternalAlignment(g6,g9)
    c: InternalAlignment(g7,g9)
    c: InternalAlignment(g8,g9)
    c: InternalAlignment(g10,g9)
    c: InternalAlignment(g11,g9)
    c: Block(g9)
    c: Coincident(g12,g9)
    c: Coincident(g12,g3)
    c: Vertical(g12)
    c: Coincident(g13,g9)
    c: Horizontal(g13)
    c: Distance(g13) = 4.8
    c: Coincident(g14,g3)
    c: Vertical(g14)
    c: Coincident(g15,g13)
    c: Vertical(g15)
    c: Tangent(g15,g1)
    c: Distance(g14) = 2
    c: Coincident(g16,g14)
    c: Horizontal(g16)
    c: Coincident(g15,g16)
FEATURE [Part::Feature] Face050
  shape: bbox 4.8 x 25.5 x 2e-07 mm, 1 faces, 0 solids (baked)
FEATURE [Part::Revolution] Revolve054  label="moreFrontCaseScrewPost001"
  Angle = 360
  Axis = (0,1,0)
  Base = (0,0,0)
  FaceMakerClass = Part::FaceMakerBullseye
  Placement = pos=(102.5,4.5,3.5) rot=(0,0,1;0rad)
  Solid = false
  Source = -> Face050
  Symmetric = false
FEATURE [Part::Feature] Face051
  shape: bbox 4.8 x 25.5 x 2e-07 mm, 1 faces, 0 solids (baked)
FEATURE [Part::Revolution] Revolve055  label="moreFrontCaseScrewPost002"
  Angle = 360
  Axis = (0,1,0)
  Base = (0,0,0)
  FaceMakerClass = Part::FaceMakerBullseye
  Placement = pos=(102.5,4.5,68.5) rot=(0,0,1;0rad)
  Solid = false
  Source = -> Face051
  Symmetric = false
FEATURE [Sketcher::SketchObject] Sketch027
  FullyConstrained = true
  sketch-geometry (10):
    g0: LineSegment StartX=-1.6 StartY=4.7 StartZ=0 EndX=-1.6 EndY=1.7 EndZ=0
    g1: LineSegment StartX=-3.5 StartY=4.7 StartZ=0 EndX=-1.6 EndY=4.7 EndZ=0
    g2: LineSegment StartX=-1.6 StartY=1.7 StartZ=0 EndX=-1.6 EndY=1.5 EndZ=0
    g3: LineSegment StartX=-1.6 StartY=1.5 StartZ=0 EndX=-5.2 EndY=1.5 EndZ=0
    g4: Circle CenterX=-3.5 CenterY=4.7 CenterZ=0 NormalX=0 NormalY=0 NormalZ=1 AngleXU=0 Radius=1
    g5: Circle CenterX=-3.59627 CenterY=2.99743 CenterZ=0 NormalX=0 NormalY=0 NormalZ=1 AngleXU=0 Radius=1
    g6: Circle CenterX=-5.2 CenterY=1.5 CenterZ=0 NormalX=0 NormalY=0 NormalZ=1 AngleXU=0 Radius=1
    g7: BSplineCurve PolesCount=3 KnotsCount=2 Degree=2 IsPeriodic=0
    g8: GeomPoint X=-3.5 Y=4.7 Z=0
    g9: GeomPoint X=-5.2 Y=1.5 Z=0
  constraints (23):
    c: Vertical(g0)
    c: Distance(g0) = 3
    c: Coincident(g1,g0)
    c: Horizontal(g1)
    c: Block(g0)
    c: Block(g1)
    c: Coincident(g2,g0)
    c: Vertical(g2)
    c: Distance(g2) = 0.2
    c: Coincident(g3,g2)
    c: Horizontal(g3)
    c: Block(g3)
    c: Coincident(g7,g1)
    c: Weight(g4) = 1
    c: Equal(g4,g5)
    c: Equal(g4,g6)
    c: Coincident(g7,g3)
    c: InternalAlignment(g4,g7)
    c: InternalAlignment(g5,g7)
    c: InternalAlignment(g6,g7)
    c: InternalAlignment(g8,g7)
    c: InternalAlignment(g9,g7)
    c: Block(g7)
FEATURE [Sketcher::SketchObject] Sketch028
  FullyConstrained = true
  sketch-geometry (18):
    g0: LineSegment StartX=0 StartY=3e-16 StartZ=0 EndX=0 EndY=1.7 EndZ=0
    g1: LineSegment StartX=-3.5 StartY=0 StartZ=0 EndX=-3.5 EndY=0.9 EndZ=0
    g2: Circle CenterX=-2.7 CenterY=1.7 CenterZ=0 NormalX=0 NormalY=0 NormalZ=1 AngleXU=0 Radius=1
    g3: Circle CenterX=-3.5 CenterY=1.7 CenterZ=0 NormalX=0 NormalY=0 NormalZ=1 AngleXU=0 Radius=1
    g4: Circle CenterX=-3.5 CenterY=0.9 CenterZ=0 NormalX=0 NormalY=0 NormalZ=1 AngleXU=0 Radius=1
    g5: BSplineCurve PolesCount=3 KnotsCount=2 Degree=2 IsPeriodic=0
    g6: GeomPoint X=-2.7 Y=1.7 Z=0
    g7: GeomPoint X=-3.5 Y=0.9 Z=0
    g8: LineSegment StartX=-3.5 StartY=0 StartZ=0 EndX=-3.5 EndY=-7 EndZ=0
    g9: LineSegment StartX=0 StartY=3e-16 StartZ=0 EndX=0 EndY=-7 EndZ=0
    g10: LineSegment StartX=-3.5 StartY=-7 StartZ=0 EndX=0 EndY=-7 EndZ=0
    g11: LineSegment StartX=-2.7 StartY=1.7 StartZ=0 EndX=-1.6 EndY=1.7 EndZ=0
    g12: LineSegment StartX=0 StartY=1.7 StartZ=0 EndX=0 EndY=4.5 EndZ=0
    g13: LineSegment StartX=0 StartY=4.5 StartZ=0 EndX=0 EndY=10.8 EndZ=0
    g14: LineSegment StartX=0 StartY=10.8 StartZ=0 EndX=-2 EndY=10.8 EndZ=0
    g15: LineSegment StartX=-1.6 StartY=4.7 StartZ=0 EndX=-1.6 EndY=1.7 EndZ=0
    g16: LineSegment StartX=-1.6 StartY=4.7 StartZ=0 EndX=-2 EndY=4.7 EndZ=0
    g17: LineSegment StartX=-2 StartY=4.7 StartZ=0 EndX=-2 EndY=10.8 EndZ=0
  constraints (44):
    c: Vertical(g0)
    c: Vertical(g1)
    c: Distance(g1) = 0.9
    c: Block(g0)
    c: Distance(g0) = 1.7
    c: Weight(g2) = 1
    c: Equal(g2,g3)
    c: Equal(g2,g4)
    c: Coincident(g5,g1)
    c: InternalAlignment(g2,g5)
    c: InternalAlignment(g3,g5)
    c: InternalAlignment(g4,g5)
    c: InternalAlignment(g6,g5)
    c: InternalAlignment(g7,g5)
    c: Block(g5)
    c: Coincident(g8,g1)
    c: Vertical(g8)
    c: Distance(g8) = 7
    c: Vertical(g9)
    c: Equal(g8,g9) = 7
    c: Coincident(g9,g0)
    c: Coincident(g10,g8)
    c: Coincident(g10,g9)
    c: Horizontal(g10)
    c: Coincident(g11,g5)
    c: Horizontal(g11)
    c: Coincident(g12,g0)
    c: Vertical(g12)
    c: Distance(g12) = 2.8
    c: Coincident(g13,g12)
    c: Vertical(g13)
    c: Distance(g13) = 6.3
    c: Coincident(g14,g13)
    c: Horizontal(g14)
    c: Distance(g14) = 2
    c: Vertical(g15)
    c: Distance(g15) = 3
    c: Block(g11)
    c: Coincident(g15,g11)
    c: Coincident(g16,g15)
    c: Horizontal(g16)
    c: Coincident(g17,g16)
    c: Coincident(g17,g14)
    c: Vertical(g17)
FEATURE [Part::Revolution] Revolve040  label="backCaseScrewRetainer001"
  Angle = 360
  Axis = (0,1,0)
  Base = (0,0,0)
  FaceMakerClass = Part::FaceMakerBullseye
  Placement = pos=(12.5,3,10) rot=(0,0,1;0rad)
  Solid = false
  Source = -> Face036
  Symmetric = false
FEATURE [Part::Feature] Face055
  shape: bbox 3.5 x 30.2 x 2e-07 mm, 1 faces, 0 solids (baked)
FEATURE [Part::Revolution] Revolve059  label="backCaseScrewPost"
  Angle = 360
  Axis = (0,1,0)
  Base = (0,0,0)
  FaceMakerClass = Part::FaceMakerBullseye
  Placement = pos=(12.5,4.5,10) rot=(0,0,1;0rad)
  Solid = false
  Source = -> Face055
  Symmetric = false
FEATURE [Part::Feature] Face056
  shape: bbox 3.5 x 30.2 x 2e-07 mm, 1 faces, 0 solids (baked)
FEATURE [Part::Revolution] Revolve060  label="backCaseScrewPost001"
  Angle = 360
  Axis = (0,1,0)
  Base = (0,0,0)
  FaceMakerClass = Part::FaceMakerBullseye
  Placement = pos=(12.5,4.5,62) rot=(0,0,1;0rad)
  Solid = false
  Source = -> Face056
  Symmetric = false
FEATURE [Part::Feature] Face057
  shape: bbox 3.5 x 17.8 x 2e-07 mm, 1 faces, 0 solids (baked)
FEATURE [Part::Revolution] Revolve061  label="removeToCreateScrewAndThreadedInsertHole"
  Angle = 360
  Axis = (0,1,0)
  Base = (0,0,0)
  FaceMakerClass = Part::FaceMakerBullseye
  Placement = pos=(12.5,0,10) rot=(0,0,1;0rad)
  Solid = false
  Source = -> Face057
  Symmetric = false
FEATURE [Part::Feature] Face058
  shape: bbox 3.5 x 17.8 x 2e-07 mm, 1 faces, 0 solids (baked)
FEATURE [Part::Revolution] Revolve062  label="removeToCreateScrewAndThreadedInsertHole001"
  Angle = 360
  Axis = (0,1,0)
  Base = (0,0,0)
  FaceMakerClass = Part::FaceMakerBullseye
  Placement = pos=(12.5,0,62) rot=(0,0,1;0rad)
  Solid = false
  Source = -> Face058
  Symmetric = false
FEATURE [Part::Feature] Face059
  shape: bbox 3.5 x 17.8 x 2e-07 mm, 1 faces, 0 solids (baked)
FEATURE [Part::Revolution] Revolve063  label="removeToCreateScrewAndThreadedInsertHole002"
  Angle = 360
  Axis = (0,1,0)
  Base = (0,0,0)
  FaceMakerClass = Part::FaceMakerBullseye
  Placement = pos=(89.5,0,68.5) rot=(0,0,1;0rad)
  Solid = false
  Source = -> Face059
  Symmetric = false
FEATURE [Part::Feature] Face060
  shape: bbox 3.5 x 17.8 x 2e-07 mm, 1 faces, 0 solids (baked)
FEATURE [Part::Revolution] Revolve064  label="removeToCreateScrewAndThreadedInsertHole003"
  Angle = 360
  Axis = (0,1,0)
  Base = (0,0,0)
  FaceMakerClass = Part::FaceMakerBullseye
  Placement = pos=(89.5,0,3.5) rot=(0,0,1;0rad)
  Solid = false
  Source = -> Face060
  Symmetric = false
FEATURE [Part::Feature] Face061
  shape: bbox 3.5 x 17.8 x 2e-07 mm, 1 faces, 0 solids (baked)
FEATURE [Part::Revolution] Revolve065  label="removeToCreateScrewAndThreadedInsertHole004"
  Angle = 360
  Axis = (0,1,0)
  Base = (0,0,0)
  FaceMakerClass = Part::FaceMakerBullseye
  Placement = pos=(102.5,4.7,3.5) rot=(0,0,1;0rad)
  Solid = false
  Source = -> Face061
  Symmetric = false
FEATURE [Part::Feature] Face062
  shape: bbox 3.5 x 17.8 x 2e-07 mm, 1 faces, 0 solids (baked)
FEATURE [Part::Revolution] Revolve066  label="removeToCreateScrewAndThreadedInsertHole005"
  Angle = 360
  Axis = (0,1,0)
  Base = (0,0,0)
  FaceMakerClass = Part::FaceMakerBullseye
  Placement = pos=(102.5,4.7,68.5) rot=(0,0,1;0rad)
  Solid = false
  Source = -> Face062
  Symmetric = false
FEATURE [Part::MultiFuse] Fusion047  label="makeHoles"
  Shapes = -> [Revolve066,Revolve065,Revolve064,Revolve063,Revolve062,Revolve061]
FEATURE [Part::Feature] Face063
  shape: bbox 3.6 x 3.2 x 2e-07 mm, 1 faces, 0 solids (baked)
FEATURE [Part::Revolution] Revolve067  label="moreFrontCaseScrewRetainer002"
  Angle = 360
  Axis = (0,1,0)
  Base = (0,0,0)
  FaceMakerClass = Part::FaceMakerBullseye
  Placement = pos=(102.5,4.5,68.5) rot=(0,0,1;0rad)
  Solid = false
  Source = -> Face063
  Symmetric = false
FEATURE [Part::Feature] Face064
  shape: bbox 3.6 x 3.2 x 2e-07 mm, 1 faces, 0 solids (baked)
FEATURE [Part::Revolution] Revolve068  label="moreFrontCaseScrewRetainer003"
  Angle = 360
  Axis = (0,1,0)
  Base = (0,0,0)
  FaceMakerClass = Part::FaceMakerBullseye
  Placement = pos=(102.5,4.5,3.5) rot=(0,0,1;0rad)
  Solid = false
  Source = -> Face064
  Symmetric = false
FEATURE [Part::Feature] Face065
  shape: bbox 3.5 x 17.8 x 2e-07 mm, 1 faces, 0 solids (baked)
FEATURE [Part::Revolution] Revolve069  label="removeToCreateScrewAndThreadedInsertHole006"
  Angle = 360
  Axis = (0,1,0)
  Base = (0,0,0)
  FaceMakerClass = Part::FaceMakerBullseye
  Placement = pos=(12.5,0,10) rot=(0,0,1;0rad)
  Solid = false
  Source = -> Face065
  Symmetric = false
FEATURE [Part::Feature] Face066
  shape: bbox 3.5 x 17.8 x 2e-07 mm, 1 faces, 0 solids (baked)
FEATURE [Part::Revolution] Revolve070  label="removeToCreateScrewAndThreadedInsertHole007"
  Angle = 360
  Axis = (0,1,0)
  Base = (0,0,0)
  FaceMakerClass = Part::FaceMakerBullseye
  Placement = pos=(12.5,0,62) rot=(0,0,1;0rad)
  Solid = false
  Source = -> Face066
  Symmetric = false
FEATURE [Part::Feature] Face067
  shape: bbox 3.5 x 17.8 x 2e-07 mm, 1 faces, 0 solids (baked)
FEATURE [Part::Revolution] Revolve071  label="removeToCreateScrewAndThreadedInsertHole008"
  Angle = 360
  Axis = (0,1,0)
  Base = (0,0,0)
  FaceMakerClass = Part::FaceMakerBullseye
  Placement = pos=(89.5,0,68.5) rot=(0,0,1;0rad)
  Solid = false
  Source = -> Face067
  Symmetric = false
FEATURE [Part::Feature] Face068
  shape: bbox 3.5 x 17.8 x 2e-07 mm, 1 faces, 0 solids (baked)
FEATURE [Part::Revolution] Revolve072  label="removeToCreateScrewAndThreadedInsertHole009"
  Angle = 360
  Axis = (0,1,0)
  Base = (0,0,0)
  FaceMakerClass = Part::FaceMakerBullseye
  Placement = pos=(89.5,0,3.5) rot=(0,0,1;0rad)
  Solid = false
  Source = -> Face068
  Symmetric = false
FEATURE [Part::Feature] Face069
  shape: bbox 3.5 x 17.8 x 2e-07 mm, 1 faces, 0 solids (baked)
FEATURE [Part::Feature] Face070
  shape: bbox 3.5 x 17.8 x 2e-07 mm, 1 faces, 0 solids (baked)
FEATURE [Part::Revolution] Revolve073  label="removeToCreateScrewAndThreadedInsertHole010"
  Angle = 360
  Axis = (0,1,0)
  Base = (0,0,0)
  FaceMakerClass = Part::FaceMakerBullseye
  Placement = pos=(102.5,4.7,3.5) rot=(0,0,1;0rad)
  Solid = false
  Source = -> Face069
  Symmetric = false
FEATURE [Part::Revolution] Revolve074  label="removeToCreateScrewAndThreadedInsertHole011"
  Angle = 360
  Axis = (0,1,0)
  Base = (0,0,0)
  FaceMakerClass = Part::FaceMakerBullseye
  Placement = pos=(102.5,4.7,68.5) rot=(0,0,1;0rad)
  Solid = false
  Source = -> Face070
  Symmetric = false
FEATURE [Part::MultiFuse] Fusion048  label="makeHoles001"
  Shapes = -> [Revolve074,Revolve073,Revolve072,Revolve071,Revolve070,Revolve069]
FEATURE [Part::MultiFuse] Fusion049  label="caseScrewRetainers"
  Shapes = -> [Revolve067,Revolve068,Revolve048,Revolve047,Revolve039,Revolve040]
FEATURE [Part::Cut] Cut015  label="caseScrewRetainers001"
  Base = -> Fusion049
  Tool = -> Fusion048
FEATURE [Part::MultiFuse] Fusion050  label="casePillars"
  Shapes = -> [Revolve055,Revolve054,Revolve043,Revolve046,Revolve059,Revolve060]
FEATURE [Part::Feature] Face071 .. Face076  x6 (patterned run collapsed; names and placements below)
  shape: bbox 3.5 x 17.8 x 2e-07 mm, 1 faces, 0 solids (baked)
FEATURE [Part::Revolution] Revolve075  label="removeToCreateScrewAndThreadedInsertHole012"
  Angle = 360
  Axis = (0,1,0)
  Base = (0,0,0)
  FaceMakerClass = Part::FaceMakerBullseye
  Placement = pos=(12.5,0,10) rot=(0,0,1;0rad)
  Solid = false
  Source = -> Face071
  Symmetric = false
FEATURE [Part::Revolution] Revolve076  label="removeToCreateScrewAndThreadedInsertHole013"
  Angle = 360
  Axis = (0,1,0)
  Base = (0,0,0)
  FaceMakerClass = Part::FaceMakerBullseye
  Placement = pos=(12.5,0,62) rot=(0,0,1;0rad)
  Solid = false
  Source = -> Face072
  Symmetric = false
FEATURE [Part::Revolution] Revolve077  label="removeToCreateScrewAndThreadedInsertHole014"
  Angle = 360
  Axis = (0,1,0)
  Base = (0,0,0)
  FaceMakerClass = Part::FaceMakerBullseye
  Placement = pos=(89.5,0,68.5) rot=(0,0,1;0rad)
  Solid = false
  Source = -> Face073
  Symmetric = false
FEATURE [Part::Revolution] Revolve078  label="removeToCreateScrewAndThreadedInsertHole015"
  Angle = 360
  Axis = (0,1,0)
  Base = (0,0,0)
  FaceMakerClass = Part::FaceMakerBullseye
  Placement = pos=(89.5,0,3.5) rot=(0,0,1;0rad)
  Solid = false
  Source = -> Face074
  Symmetric = false
FEATURE [Part::Revolution] Revolve079  label="removeToCreateScrewAndThreadedInsertHole016"
  Angle = 360
  Axis = (0,1,0)
  Base = (0,0,0)
  FaceMakerClass = Part::FaceMakerBullseye
  Placement = pos=(102.5,4.7,3.5) rot=(0,0,1;0rad)
  Solid = false
  Source = -> Face075
  Symmetric = false
FEATURE [Part::Revolution] Revolve080  label="removeToCreateScrewAndThreadedInsertHole017"
  Angle = 360
  Axis = (0,1,0)
  Base = (0,0,0)
  FaceMakerClass = Part::FaceMakerBullseye
  Placement = pos=(102.5,4.7,68.5) rot=(0,0,1;0rad)
  Solid = false
  Source = -> Face076
  Symmetric = false
FEATURE [Part::MultiFuse] Fusion051  label="makeHoles002"
  Shapes = -> [Revolve080,Revolve079,Revolve078,Revolve077,Revolve076,Revolve075]
FEATURE [Part::Cut] Cut016  label="caesPillars"
  Base = -> Fusion050
  Tool = -> Fusion051
FEATURE [Part::Revolution] Revolve009  label="plugHousing016"
  Angle = 360
  Axis = (0,1,0)
  Base = (0,0,0)
  FaceMakerClass = Part::FaceMakerBullseye
  Placement = pos=(0,0,36.15) rot=(0,0,1;0rad)
  Solid = false
  Source = -> Face012
  Symmetric = false
FEATURE [Part::MultiFuse] Fusion014  label="plugHousing023"
  Placement = pos=(0,0,0) rot=(0,0,1;1.5708rad)
  Shapes = -> [Revolve011,Revolve009]
FEATURE [Part::Revolution] Revolve010  label="plugHousing017"
  Angle = 360
  Axis = (0,1,0)
  Base = (0,0,0)
  FaceMakerClass = Part::FaceMakerBullseye
  Placement = pos=(0,0,36.15) rot=(0,0,1;0rad)
  Solid = false
  Source = -> Face014
  Symmetric = false
FEATURE [Part::MultiFuse] Fusion015  label="plugHousing024"
  Placement = pos=(0,0,0) rot=(0,0,1;1.5708rad)
  Shapes = -> [Revolve010,Revolve015]
FEATURE [Part::Revolution] Revolve014  label="plugHousing026"
  Angle = 360
  Axis = (0,1,0)
  Base = (0,0,0)
  FaceMakerClass = Part::FaceMakerBullseye
  Placement = pos=(0,0,36.15) rot=(0,0,1;0rad)
  Solid = false
  Source = -> Face011
  Symmetric = false
FEATURE [Part::Revolution] Revolve013  label="plugHousing025"
  Angle = 360
  Axis = (0,1,0)
  Base = (0,0,0)
  FaceMakerClass = Part::FaceMakerBullseye
  Placement = pos=(0,0,36.15) rot=(0,0,1;0rad)
  Solid = false
  Source = -> Face015
  Symmetric = false
FEATURE [Part::MultiFuse] Fusion016  label="plugHousing028"
  Placement = pos=(0,19,0) rot=(0,0,1;3.14159rad)
  Shapes = -> [Fusion014,Fusion013]
FEATURE [Part::MultiFuse] Fusion011  label="plugHousing018"
  Placement = pos=(0,0,0) rot=(0,0,1;1.5708rad)
  Shapes = -> [Revolve014,Revolve013]
FEATURE [Part::MultiFuse] Fusion012  label="plugHousing019"
  Placement = pos=(0,19,0) rot=(0,0,1;3.14159rad)
  Shapes = -> [Fusion011,Fusion015]
FEATURE [Part::MultiFuse] Fusion017  label="plugHousing029"
  Placement = pos=(122.621,0,-0.15) rot=(0,0,1;0rad)
  Shapes = -> [Fusion016,Fusion012]
FEATURE [Part::MultiFuse] Fusion052  label="casePillarRetainers"
  Shapes = -> [Extrude012,Extrude013,Extrude014,Extrude015,Extrude016,Extrude017,Extrude018,Extrude019,Box011,Box012]
FEATURE [Part::Feature] Face077
  shape: bbox 3.5 x 17.8 x 2e-07 mm, 1 faces, 0 solids (baked)
FEATURE [Part::Revolution] Revolve081  label="removeToCreateScrewAndThreadedInsertHole018"
  Angle = 360
  Axis = (0,1,0)
  Base = (0,0,0)
  FaceMakerClass = Part::FaceMakerBullseye
  Placement = pos=(62.3,30.3,19.7) rot=(0,0,1;0rad)
  Solid = false
  Source = -> Face077
  Symmetric = false
FEATURE [Part::Feature] Face078
  shape: bbox 3.5 x 17.8 x 2e-07 mm, 1 faces, 0 solids (baked)
FEATURE [Part::Revolution] Revolve082  label="removeToCreateScrewAndThreadedInsertHole019"
  Angle = 360
  Axis = (0,1,0)
  Base = (0,0,0)
  FaceMakerClass = Part::FaceMakerBullseye
  Placement = pos=(62.3,30.3,51.7) rot=(0,0,1;0rad)
  Solid = false
  Source = -> Face078
  Symmetric = false
FEATURE [Part::Feature] Face079
  shape: bbox 3.5 x 17.8 x 2e-07 mm, 1 faces, 0 solids (baked)
FEATURE [Part::Revolution] Revolve083  label="removeToCreateScrewAndThreadedInsertHole020"
  Angle = 360
  Axis = (0,1,0)
  Base = (0,0,0)
  FaceMakerClass = Part::FaceMakerBullseye
  Placement = pos=(30.3,30.3,19.7) rot=(0,0,1;0rad)
  Solid = false
  Source = -> Face079
  Symmetric = false
FEATURE [Part::Feature] Face080
  shape: bbox 3.5 x 17.8 x 2e-07 mm, 1 faces, 0 solids (baked)
FEATURE [Part::Revolution] Revolve084  label="removeToCreateScrewAndThreadedInsertHole021"
  Angle = 360
  Axis = (0,1,0)
  Base = (0,0,0)
  FaceMakerClass = Part::FaceMakerBullseye
  Placement = pos=(30.3,30.3,51.7) rot=(0,0,1;0rad)
  Solid = false
  Source = -> Face080
  Symmetric = false
FEATURE [Part::MultiFuse] Fusion053  label="createThreadedInsertHolesForFan"
  Shapes = -> [Revolve081,Revolve082,Revolve083,Revolve084]
FEATURE [Part::Cut] Cut017  label="fanScrewHousing001"
  Base = -> Fusion046
  Tool = -> Fusion053
FEATURE [Part::Feature] Face081
  shape: bbox 3.5 x 17.8 x 2e-07 mm, 1 faces, 0 solids (baked)
FEATURE [Part::Revolution] Revolve085  label="removeToCreateScrewAndThreadedInsertHole022"
  Angle = 360
  Axis = (0,1,0)
  Base = (0,0,0)
  FaceMakerClass = Part::FaceMakerBullseye
  Placement = pos=(62.3,30.3,19.7) rot=(0,0,1;0rad)
  Solid = false
  Source = -> Face081
  Symmetric = false
FEATURE [Part::Feature] Face082
  shape: bbox 3.5 x 17.8 x 2e-07 mm, 1 faces, 0 solids (baked)
FEATURE [Part::Revolution] Revolve086  label="removeToCreateScrewAndThreadedInsertHole023"
  Angle = 360
  Axis = (0,1,0)
  Base = (0,0,0)
  FaceMakerClass = Part::FaceMakerBullseye
  Placement = pos=(62.3,30.3,51.7) rot=(0,0,1;0rad)
  Solid = false
  Source = -> Face082
  Symmetric = false
FEATURE [Part::Feature] Face083
  shape: bbox 3.5 x 17.8 x 2e-07 mm, 1 faces, 0 solids (baked)
FEATURE [Part::Revolution] Revolve087  label="removeToCreateScrewAndThreadedInsertHole024"
  Angle = 360
  Axis = (0,1,0)
  Base = (0,0,0)
  FaceMakerClass = Part::FaceMakerBullseye
  Placement = pos=(30.3,30.3,19.7) rot=(0,0,1;0rad)
  Solid = false
  Source = -> Face083
  Symmetric = false
FEATURE [Part::Feature] Face084
  shape: bbox 3.5 x 17.8 x 2e-07 mm, 1 faces, 0 solids (baked)
FEATURE [Part::Revolution] Revolve088  label="removeToCreateScrewAndThreadedInsertHole025"
  Angle = 360
  Axis = (0,1,0)
  Base = (0,0,0)
  FaceMakerClass = Part::FaceMakerBullseye
  Placement = pos=(30.3,30.3,51.7) rot=(0,0,1;0rad)
  Solid = false
  Source = -> Face084
  Symmetric = false
FEATURE [Part::MultiFuse] Fusion054  label="createThreadedInsertHolesForFan001"
  Shapes = -> [Revolve085,Revolve086,Revolve087,Revolve088]
FEATURE [Part::Cut] Cut018  label="top007"
  Base = -> Fusion040
  Tool = -> Fusion054
FEATURE [Sketcher::SketchObject] Sketch029
  FullyConstrained = false
  Placement = pos=(0,0,0) rot=(1,0,0;1.5708rad)
  sketch-geometry (24):
    g0: ArcOfCircle CenterX=-4 CenterY=-10.5 CenterZ=0 NormalX=0 NormalY=0 NormalZ=1 AngleXU=0 Radius=1.5 StartAngle=6e-16 EndAngle=3.14159
    g1: ArcOfCircle CenterX=-34.2 CenterY=-10.5 CenterZ=0 NormalX=0 NormalY=0 NormalZ=1 AngleXU=0 Radius=1.5 StartAngle=0 EndAngle=3.14159
    g2: ArcOfCircle CenterX=-34.2 CenterY=-27.7 CenterZ=0 NormalX=0 NormalY=0 NormalZ=1 AngleXU=0 Radius=1.5 StartAngle=3.14159 EndAngle=6.28319
    g3: ArcOfCircle CenterX=-4 CenterY=-27.7 CenterZ=0 NormalX=0 NormalY=0 NormalZ=1 AngleXU=0 Radius=1.5 StartAngle=3.1416 EndAngle=6.28319
    g4: ArcOfCircle CenterX=-10 CenterY=-4.3 CenterZ=0 NormalX=0 NormalY=0 NormalZ=1 AngleXU=0 Radius=1.5 StartAngle=2e-16 EndAngle=3.14159
    g5: ArcOfCircle CenterX=-16.1 CenterY=-1.8 CenterZ=0 NormalX=0 NormalY=0 NormalZ=1 AngleXU=0 Radius=1.5 StartAngle=5e-16 EndAngle=3.14159
    g6: ArcOfCircle CenterX=-22.1 CenterY=-1.8 CenterZ=0 NormalX=0 NormalY=0 NormalZ=1 AngleXU=0 Radius=1.5 StartAngle=5e-16 EndAngle=3.14159
    g7: ArcOfCircle CenterX=-28.2 CenterY=-4.3 CenterZ=0 NormalX=0 NormalY=0 NormalZ=1 AngleXU=0 Radius=1.5 StartAngle=2e-16 EndAngle=3.14159
    g8: ArcOfCircle CenterX=-10 CenterY=-33.9 CenterZ=0 NormalX=0 NormalY=0 NormalZ=1 AngleXU=0 Radius=1.5 StartAngle=3.14159 EndAngle=6.28319
    g9: ArcOfCircle CenterX=-16.1 CenterY=-36.4 CenterZ=0 NormalX=0 NormalY=0 NormalZ=1 AngleXU=0 Radius=1.5 StartAngle=3.14159 EndAngle=6.28319
    g10: ArcOfCircle CenterX=-22.1 CenterY=-36.4 CenterZ=0 NormalX=0 NormalY=0 NormalZ=1 AngleXU=0 Radius=1.5 StartAngle=3.14159 EndAngle=6.28319
    g11: ArcOfCircle CenterX=-28.2 CenterY=-33.9 CenterZ=0 NormalX=0 NormalY=0 NormalZ=1 AngleXU=0 Radius=1.5 StartAngle=3.14159 EndAngle=6.28319
    g12: LineSegment StartX=-35.7 StartY=-10.5 StartZ=0 EndX=-35.7 EndY=-27.7 EndZ=0
    g13: LineSegment StartX=-32.7 StartY=-10.5 StartZ=0 EndX=-32.7 EndY=-27.7 EndZ=0
    g14: LineSegment StartX=-29.7 StartY=-33.9 StartZ=0 EndX=-29.7 EndY=-4.3 EndZ=0
    g15: LineSegment StartX=-26.7 StartY=-33.9 StartZ=0 EndX=-26.7 EndY=-4.3 EndZ=0
    g16: LineSegment StartX=-2.5 StartY=-10.5 StartZ=0 EndX=-2.5 EndY=-27.7 EndZ=0
    g17: LineSegment StartX=-8.5 StartY=-4.3 StartZ=0 EndX=-8.5 EndY=-33.9 EndZ=0
    g18: LineSegment StartX=-5.5 StartY=-10.5 StartZ=0 EndX=-5.5 EndY=-27.7 EndZ=0
    g19: LineSegment StartX=-11.5 StartY=-4.3 StartZ=0 EndX=-11.5 EndY=-33.9 EndZ=0
    g20: LineSegment StartX=-14.6 StartY=-1.8 StartZ=0 EndX=-14.6 EndY=-36.4 EndZ=0
    g21: LineSegment StartX=-17.6 StartY=-1.8 StartZ=0 EndX=-17.6 EndY=-36.4 EndZ=0
    g22: LineSegment StartX=-20.6 StartY=-36.4 StartZ=0 EndX=-20.6 EndY=-1.8 EndZ=0
    g23: LineSegment StartX=-23.6 StartY=-1.8 StartZ=0 EndX=-23.6 EndY=-36.4 EndZ=0
  constraints (48):
    c: Block(g0)
    c: Block(g1)
    c: Block(g2)
    c: Block(g3)
    c: Block(g4)
    c: Block(g5)
    c: Block(g6)
    c: Block(g7)
    c: Block(g8)
    c: Block(g9)
    c: Block(g10)
    c: Block(g11)
    c: Coincident(g12,g1)
    c: Coincident(g12,g2)
    c: Vertical(g12)
    c: Coincident(g13,g1)
    c: Coincident(g13,g2)
    c: Vertical(g13)
    c: Coincident(g14,g11)
    c: Coincident(g14,g7)
    c: Vertical(g14)
    c: Coincident(g15,g11)
    c: Coincident(g15,g7)
    c: Vertical(g15)
    c: Coincident(g16,g0)
    c: Coincident(g16,g3)
    c: Vertical(g16)
    c: Coincident(g17,g4)
    c: Coincident(g17,g8)
    c: Vertical(g17)
    c: Coincident(g18,g0)
    c: Coincident(g18,g3)
    c: Vertical(g18)
    c: Coincident(g19,g4)
    c: Coincident(g19,g8)
    c: Vertical(g19)
    c: Coincident(g20,g5)
    c: Coincident(g20,g9)
    c: Vertical(g20)
    c: Coincident(g21,g5)
    c: Coincident(g21,g9)
    c: Vertical(g21)
    c: Coincident(g22,g10)
    c: Coincident(g22,g6)
    c: Vertical(g22)
    c: Coincident(g23,g6)
    c: Coincident(g23,g10)
    c: Vertical(g23)
FEATURE [Part::Extrusion] Extrude020  label="removeToCreateFanGrillHoles"
  Base = -> Sketch029
  Dir = (0,-1,6e-16)
  DirMode = 2
  FaceMakerClass = Part::FaceMakerBullseye
  LengthFwd = 10
  LengthRev = 0
  Placement = pos=(65.4,44,54.82) rot=(0,0,1;0rad)
  Solid = true
  Symmetric = false
FEATURE [Part::MultiFuse] Fusion055  label="top008"
  Shapes = -> [Cut017,Cut018]
FEATURE [Part::Cut] Cut019  label="top009"
  Base = -> Fusion055
  Tool = -> Extrude020
FEATURE [App::MeasureDistance] Distance003  label="Distance: 71.95 mm"
  Distance = 71.9513
  P1 = (117,38,72)
  P2 = (117,38,0.0487319)
FEATURE [Sketcher::SketchObject] Sketch030
  FullyConstrained = true
  Placement = pos=(117,19,0) rot=(0.57735,0.57735,0.57735;2.0944rad)
  sketch-geometry (48):
    g0: LineSegment StartX=-49.19 StartY=69.25 StartZ=0 EndX=-49.19 EndY=66.25 EndZ=0
    g1: LineSegment StartX=-49.19 StartY=63.5 StartZ=0 EndX=-49.19 EndY=60.5 EndZ=0
    g2: LineSegment StartX=-49.19 StartY=57.75 StartZ=0 EndX=-49.19 EndY=54.75 EndZ=0
    g3: LineSegment StartX=-49.19 StartY=52 StartZ=0 EndX=-49.19 EndY=49 EndZ=0
    g4: LineSegment StartX=-49.19 StartY=46.25 StartZ=0 EndX=-49.19 EndY=43.25 EndZ=0
    g5: LineSegment StartX=-49.19 StartY=40.5 StartZ=0 EndX=-49.19 EndY=37.5 EndZ=0
    g6: LineSegment StartX=-49.19 StartY=34.5 StartZ=0 EndX=-49.19 EndY=31.5 EndZ=0
    g7: LineSegment StartX=-49.19 StartY=28.75 StartZ=0 EndX=-49.19 EndY=25.75 EndZ=0
    g8: LineSegment StartX=-49.19 StartY=23 StartZ=0 EndX=-49.19 EndY=20 EndZ=0
    g9: LineSegment StartX=-49.19 StartY=17.25 StartZ=0 EndX=-49.19 EndY=14.25 EndZ=0
    g10: LineSegment StartX=-49.19 StartY=11.5 StartZ=0 EndX=-49.19 EndY=8.5 EndZ=0
    g11: LineSegment StartX=-49.19 StartY=5.75 StartZ=0 EndX=-49.19 EndY=2.75 EndZ=0
    g12: ArcOfCircle CenterX=-1.5 CenterY=67.75 CenterZ=0 NormalX=0 NormalY=0 NormalZ=1 AngleXU=0 Radius=1.5 StartAngle=4.71239 EndAngle=7.85398
    g13: ArcOfCircle CenterX=-1.5 CenterY=62 CenterZ=0 NormalX=0 NormalY=0 NormalZ=1 AngleXU=0 Radius=1.5 StartAngle=4.71239 EndAngle=7.85398
    g14: ArcOfCircle CenterX=-1.5 CenterY=56.25 CenterZ=0 NormalX=0 NormalY=0 NormalZ=1 AngleXU=0 Radius=1.5 StartAngle=4.71239 EndAngle=7.85398
    g15: ArcOfCircle CenterX=-11.49 CenterY=50.5 CenterZ=0 NormalX=0 NormalY=0 NormalZ=1 AngleXU=0 Radius=1.5 StartAngle=4.71239 EndAngle=7.85398
    g16: ArcOfCircle CenterX=-16.28 CenterY=44.75 CenterZ=0 NormalX=0 NormalY=0 NormalZ=1 AngleXU=0 Radius=1.5 StartAngle=4.71239 EndAngle=7.85398
    g17: ArcOfCircle CenterX=-18.2337 CenterY=39 CenterZ=0 NormalX=0 NormalY=0 NormalZ=1 AngleXU=0 Radius=1.5 StartAngle=4.71485 EndAngle=7.85398
    g18: ArcOfCircle CenterX=-16.2837 CenterY=27.25 CenterZ=0 NormalX=0 NormalY=0 NormalZ=1 AngleXU=0 Radius=1.5 StartAngle=4.71485 EndAngle=7.85398
    g19: ArcOfCircle CenterX=-18.2337 CenterY=33 CenterZ=0 NormalX=0 NormalY=0 NormalZ=1 AngleXU=0 Radius=1.5 StartAngle=4.71485 EndAngle=7.85398
    g20: ArcOfCircle CenterX=-11.49 CenterY=21.5 CenterZ=0 NormalX=0 NormalY=0 NormalZ=1 AngleXU=0 Radius=1.5 StartAngle=4.71239 EndAngle=7.85398
    g21: ArcOfCircle CenterX=-1.5 CenterY=4.25 CenterZ=0 NormalX=0 NormalY=0 NormalZ=1 AngleXU=0 Radius=1.5 StartAngle=4.71239 EndAngle=7.85398
    g22: ArcOfCircle CenterX=-1.5 CenterY=10 CenterZ=0 NormalX=0 NormalY=0 NormalZ=1 AngleXU=0 Radius=1.5 StartAngle=4.71239 EndAngle=7.85398
    g23: ArcOfCircle CenterX=-1.5 CenterY=15.75 CenterZ=0 NormalX=0 NormalY=0 NormalZ=1 AngleXU=0 Radius=1.5 StartAngle=4.71239 EndAngle=7.85398
    g24: LineSegment StartX=-49.19 StartY=69.25 StartZ=0 EndX=-1.5 EndY=69.25 EndZ=0
    g25: LineSegment StartX=-49.19 StartY=66.25 StartZ=0 EndX=-1.5 EndY=66.25 EndZ=0
    g26: LineSegment StartX=-49.19 StartY=63.5 StartZ=0 EndX=-1.5 EndY=63.5 EndZ=0
    g27: LineSegment StartX=-49.19 StartY=60.5 StartZ=0 EndX=-1.5 EndY=60.5 EndZ=0
    g28: LineSegment StartX=-49.19 StartY=57.75 StartZ=0 EndX=-1.5 EndY=57.75 EndZ=0
    g29: LineSegment StartX=-49.19 StartY=54.75 StartZ=0 EndX=-1.5 EndY=54.75 EndZ=0
    g30: LineSegment StartX=-49.19 StartY=52 StartZ=0 EndX=-11.49 EndY=52 EndZ=0
    g31: LineSegment StartX=-49.19 StartY=49 StartZ=0 EndX=-11.49 EndY=49 EndZ=0
    g32: LineSegment StartX=-49.19 StartY=46.25 StartZ=0 EndX=-16.28 EndY=46.25 EndZ=0
    g33: LineSegment StartX=-49.19 StartY=43.25 StartZ=0 EndX=-16.28 EndY=43.25 EndZ=0
    g34: LineSegment StartX=-49.19 StartY=40.5 StartZ=0 EndX=-18.2337 EndY=40.5 EndZ=0
    g35: LineSegment StartX=-49.19 StartY=37.5 StartZ=0 EndX=-18.23 EndY=37.5 EndZ=0
    g36: LineSegment StartX=-49.19 StartY=34.5 StartZ=0 EndX=-18.2337 EndY=34.5 EndZ=0
    g37: LineSegment StartX=-49.19 StartY=31.5 StartZ=0 EndX=-18.23 EndY=31.5 EndZ=0
    g38: LineSegment StartX=-49.19 StartY=28.75 StartZ=0 EndX=-16.2837 EndY=28.75 EndZ=0
    g39: LineSegment StartX=-49.19 StartY=25.75 StartZ=0 EndX=-16.28 EndY=25.75 EndZ=0
    g40: LineSegment StartX=-49.19 StartY=23 StartZ=0 EndX=-11.49 EndY=23 EndZ=0
    g41: LineSegment StartX=-49.19 StartY=20 StartZ=0 EndX=-11.49 EndY=20 EndZ=0
    g42: LineSegment StartX=-49.19 StartY=17.25 StartZ=0 EndX=-1.5 EndY=17.25 EndZ=0
    g43: LineSegment StartX=-49.19 StartY=14.25 StartZ=0 EndX=-1.5 EndY=14.25 EndZ=0
    g44: LineSegment StartX=-49.19 StartY=11.5 StartZ=0 EndX=-1.5 EndY=11.5 EndZ=0
    g45: LineSegment StartX=-49.19 StartY=8.5 StartZ=0 EndX=-1.5 EndY=8.5 EndZ=0
    g46: LineSegment StartX=-49.19 StartY=5.75 StartZ=0 EndX=-1.5 EndY=5.75 EndZ=0
    g47: LineSegment StartX=-49.19 StartY=2.75 StartZ=0 EndX=-1.5 EndY=2.75 EndZ=0
  constraints (120):
    c: Vertical(g0)
    c: Distance(g0) = 3
    c: Block(g0)
    c: Vertical(g1)
    c: Distance(g1) = 3
    c: Vertical(g2)
    c: Equal(g0,g2) = 3
    c: Block(g2)
    c: Vertical(g3)
    c: Equal(g1,g3) = 3
    c: Vertical(g4)
    c: Equal(g0,g4) = 3
    c: Block(g4)
    c: Vertical(g5)
    c: Equal(g1,g5) = 3
    c: Vertical(g6)
    c: Equal(g0,g6) = 3
    c: Block(g6)
    c: Vertical(g7)
    c: Equal(g1,g7) = 3
    c: Vertical(g8)
    c: Equal(g0,g8) = 3
    c: Block(g8)
    c: Vertical(g9)
    c: Equal(g1,g9) = 3
    c: Vertical(g10)
    c: Equal(g0,g10) = 3
    c: Block(g10)
    c: Vertical(g11)
    c: Equal(g1,g11) = 3
    c: Block(g12)
    c: Block(g13)
    c: Block(g14)
    c: Block(g15)
    c: Block(g16)
    c: Block(g17)
    c: Block(g18)
    c: Block(g19)
    c: Block(g20)
    c: Block(g21)
    c: Block(g22)
    c: Block(g23)
    c: Block(g11)
    c: Block(g9)
    c: Block(g7)
    c: Block(g5)
    c: Block(g3)
    c: Block(g1)
    c: Coincident(g24,g0)
    c: Coincident(g24,g12)
    c: Horizontal(g24)
    c: Coincident(g25,g0)
    c: Coincident(g25,g12)
    c: Horizontal(g25)
    c: Coincident(g26,g1)
    c: Coincident(g26,g13)
    c: Horizontal(g26)
    c: Coincident(g27,g1)
    c: Coincident(g27,g13)
    c: Horizontal(g27)
    c: Coincident(g28,g2)
    c: Coincident(g28,g14)
    c: Horizontal(g28)
    c: Coincident(g29,g2)
    c: Coincident(g29,g14)
    c: Horizontal(g29)
    c: Coincident(g30,g3)
    c: Coincident(g30,g15)
    c: Horizontal(g30)
    c: Coincident(g31,g3)
    c: Coincident(g31,g15)
    c: Horizontal(g31)
    c: Coincident(g32,g4)
    c: Coincident(g32,g16)
    c: Horizontal(g32)
    c: Coincident(g33,g4)
    c: Coincident(g33,g16)
    c: Horizontal(g33)
    c: Coincident(g34,g5)
    c: Coincident(g34,g17)
    c: Horizontal(g34)
    c: Coincident(g35,g5)
    c: Coincident(g35,g17)
    c: Horizontal(g35)
    c: Coincident(g36,g6)
    c: Coincident(g36,g19)
    c: Horizontal(g36)
    c: Coincident(g37,g6)
    c: Coincident(g37,g19)
    c: Horizontal(g37)
    c: Coincident(g38,g7)
    c: Coincident(g38,g18)
    c: Horizontal(g38)
    c: Coincident(g39,g7)
    c: Coincident(g39,g18)
    c: Horizontal(g39)
    c: Coincident(g40,g8)
    c: Coincident(g40,g20)
    c: Horizontal(g40)
    c: Coincident(g41,g8)
    c: Coincident(g41,g20)
    c: Horizontal(g41)
    c: Coincident(g42,g9)
    c: Coincident(g42,g23)
    c: Horizontal(g42)
    c: Coincident(g43,g9)
    c: Coincident(g43,g23)
    c: Horizontal(g43)
    c: Coincident(g44,g10)
    c: Coincident(g44,g22)
    c: Horizontal(g44)
    c: Coincident(g45,g10)
    c: Coincident(g45,g22)
    c: Horizontal(g45)
    c: Coincident(g46,g11)
    c: Coincident(g46,g21)
    c: Horizontal(g46)
    c: Coincident(g47,g11)
    c: Coincident(g47,g21)
    c: Horizontal(g47)
FEATURE [Sketcher::SketchObject] Sketch031
  FullyConstrained = true
  Placement = pos=(117,19,0) rot=(0.57735,0.57735,0.57735;2.0944rad)
  sketch-geometry (24):
    g0: ArcOfCircle CenterX=-49.19 CenterY=67.75 CenterZ=0 NormalX=0 NormalY=0 NormalZ=1 AngleXU=0 Radius=1.5 StartAngle=1.5708 EndAngle=4.71239
    g1: ArcOfCircle CenterX=-49.19 CenterY=62 CenterZ=0 NormalX=0 NormalY=0 NormalZ=1 AngleXU=0 Radius=1.5 StartAngle=1.5708 EndAngle=4.71239
    g2: ArcOfCircle CenterX=-49.19 CenterY=56.25 CenterZ=0 NormalX=0 NormalY=0 NormalZ=1 AngleXU=0 Radius=1.5 StartAngle=1.5708 EndAngle=4.71239
    g3: ArcOfCircle CenterX=-49.19 CenterY=50.5 CenterZ=0 NormalX=0 NormalY=0 NormalZ=1 AngleXU=0 Radius=1.5 StartAngle=1.5708 EndAngle=4.71239
    g4: ArcOfCircle CenterX=-49.19 CenterY=44.75 CenterZ=0 NormalX=0 NormalY=0 NormalZ=1 AngleXU=0 Radius=1.5 StartAngle=1.5708 EndAngle=4.71239
    g5: ArcOfCircle CenterX=-49.19 CenterY=39 CenterZ=0 NormalX=0 NormalY=0 NormalZ=1 AngleXU=0 Radius=1.5 StartAngle=1.5708 EndAngle=4.71239
    g6: ArcOfCircle CenterX=-49.19 CenterY=33 CenterZ=0 NormalX=0 NormalY=0 NormalZ=1 AngleXU=0 Radius=1.5 StartAngle=1.5708 EndAngle=4.71239
    g7: ArcOfCircle CenterX=-49.19 CenterY=27.25 CenterZ=0 NormalX=0 NormalY=0 NormalZ=1 AngleXU=0 Radius=1.5 StartAngle=1.5708 EndAngle=4.71239
    g8: ArcOfCircle CenterX=-49.19 CenterY=21.5 CenterZ=0 NormalX=0 NormalY=0 NormalZ=1 AngleXU=0 Radius=1.5 StartAngle=1.5708 EndAngle=4.71239
    g9: ArcOfCircle CenterX=-49.19 CenterY=15.75 CenterZ=0 NormalX=0 NormalY=0 NormalZ=1 AngleXU=0 Radius=1.5 StartAngle=1.5708 EndAngle=4.71239
    g10: ArcOfCircle CenterX=-49.19 CenterY=10 CenterZ=0 NormalX=0 NormalY=0 NormalZ=1 AngleXU=0 Radius=1.5 StartAngle=1.5708 EndAngle=4.71239
    g11: ArcOfCircle CenterX=-49.19 CenterY=4.25 CenterZ=0 NormalX=0 NormalY=0 NormalZ=1 AngleXU=0 Radius=1.5 StartAngle=1.5708 EndAngle=4.71239
    g12: LineSegment StartX=-49.19 StartY=69.25 StartZ=0 EndX=-49.19 EndY=66.25 EndZ=0
    g13: LineSegment StartX=-49.19 StartY=63.5 StartZ=0 EndX=-49.19 EndY=60.5 EndZ=0
    g14: LineSegment StartX=-49.19 StartY=57.75 StartZ=0 EndX=-49.19 EndY=54.75 EndZ=0
    g15: LineSegment StartX=-49.19 StartY=52 StartZ=0 EndX=-49.19 EndY=49 EndZ=0
    g16: LineSegment StartX=-49.19 StartY=46.25 StartZ=0 EndX=-49.19 EndY=43.25 EndZ=0
    g17: LineSegment StartX=-49.19 StartY=40.5 StartZ=0 EndX=-49.19 EndY=37.5 EndZ=0
    g18: LineSegment StartX=-49.19 StartY=34.5 StartZ=0 EndX=-49.19 EndY=31.5 EndZ=0
    g19: LineSegment StartX=-49.19 StartY=28.75 StartZ=0 EndX=-49.19 EndY=25.75 EndZ=0
    g20: LineSegment StartX=-49.19 StartY=23 StartZ=0 EndX=-49.19 EndY=20 EndZ=0
    g21: LineSegment StartX=-49.19 StartY=17.25 StartZ=0 EndX=-49.19 EndY=14.25 EndZ=0
    g22: LineSegment StartX=-49.19 StartY=11.5 StartZ=0 EndX=-49.19 EndY=8.5 EndZ=0
    g23: LineSegment StartX=-49.19 StartY=5.75 StartZ=0 EndX=-49.19 EndY=2.75 EndZ=0
  constraints (48):
    c: Block(g0)
    c: Block(g1)
    c: Block(g2)
    c: Block(g3)
    c: Block(g4)
    c: Block(g5)
    c: Block(g6)
    c: Block(g7)
    c: Block(g8)
    c: Block(g9)
    c: Block(g10)
    c: Block(g11)
    c: Coincident(g12,g0)
    c: Coincident(g12,g0)
    c: Vertical(g12)
    c: Vertical(g13)
    c: Coincident(g13,g1)
    c: Vertical(g14)
    c: Coincident(g14,g2)
    c: Vertical(g15)
    c: Coincident(g15,g3)
    c: Vertical(g16)
    c: Coincident(g16,g4)
    c: Vertical(g17)
    c: Coincident(g17,g5)
    c: Vertical(g18)
    c: Coincident(g18,g6)
    c: Vertical(g19)
    c: Coincident(g19,g7)
    c: Vertical(g20)
    c: Coincident(g20,g8)
    c: Vertical(g21)
    c: Coincident(g21,g9)
    c: Vertical(g22)
    c: Coincident(g22,g10)
    c: Vertical(g23)
    c: Coincident(g23,g11)
    c: Block(g23)
    c: Block(g22)
    c: Block(g21)
    c: Block(g20)
    c: Block(g13)
    c: Block(g14)
    c: Block(g15)
    c: Block(g16)
    c: Block(g17)
    c: Block(g18)
    c: Block(g19)
FEATURE [Part::Extrusion] Extrude022
  Base = -> Sketch030
  Dir = (1,-2e-16,2e-16)
  DirMode = 2
  FaceMakerClass = Part::FaceMakerBullseye
  LengthFwd = 19
  LengthRev = 0
  Placement = pos=(-19,0,0) rot=(0,0,1;0rad)
  Solid = true
  Symmetric = false
FEATURE [Part::Fillet] Fillet022
  Base = -> Extrude022
  Edges = 24 edges r=1.49: [Edge6,Edge11,Edge18,Edge23,Edge30,Edge35,Edge42,Edge47,Edge54,Edge59,Edge66,Edge71,Edge78,Edge83,Edge90,Edge95,Edge102,Edge107,Edge114,Edge119,Edge126,Edge131,Edge138,Edge143]
FEATURE [Part::Cut] Cut020  label="top010"
  Base = -> Cut019
  Tool = -> Fillet022
FEATURE [Sketcher::SketchObject] Sketch032
  FullyConstrained = true
  Placement = pos=(117,19,0) rot=(0.57735,0.57735,0.57735;2.0944rad)
  sketch-geometry (48):
    g0: LineSegment StartX=-49.19 StartY=69.25 StartZ=0 EndX=-49.19 EndY=66.25 EndZ=0
    g1: LineSegment StartX=-49.19 StartY=63.5 StartZ=0 EndX=-49.19 EndY=60.5 EndZ=0
    g2: LineSegment StartX=-49.19 StartY=57.75 StartZ=0 EndX=-49.19 EndY=54.75 EndZ=0
    g3: LineSegment StartX=-49.19 StartY=52 StartZ=0 EndX=-49.19 EndY=49 EndZ=0
    g4: LineSegment StartX=-49.19 StartY=46.25 StartZ=0 EndX=-49.19 EndY=43.25 EndZ=0
    g5: LineSegment StartX=-49.19 StartY=40.5 StartZ=0 EndX=-49.19 EndY=37.5 EndZ=0
    g6: LineSegment StartX=-49.19 StartY=34.5 StartZ=0 EndX=-49.19 EndY=31.5 EndZ=0
    g7: LineSegment StartX=-49.19 StartY=28.75 StartZ=0 EndX=-49.19 EndY=25.75 EndZ=0
    g8: LineSegment StartX=-49.19 StartY=23 StartZ=0 EndX=-49.19 EndY=20 EndZ=0
    g9: LineSegment StartX=-49.19 StartY=17.25 StartZ=0 EndX=-49.19 EndY=14.25 EndZ=0
    g10: LineSegment StartX=-49.19 StartY=11.5 StartZ=0 EndX=-49.19 EndY=8.5 EndZ=0
    g11: LineSegment StartX=-49.19 StartY=5.75 StartZ=0 EndX=-49.19 EndY=2.75 EndZ=0
    g12: ArcOfCircle CenterX=-1.5 CenterY=67.75 CenterZ=0 NormalX=0 NormalY=0 NormalZ=1 AngleXU=0 Radius=1.5 StartAngle=4.71239 EndAngle=7.85398
    g13: ArcOfCircle CenterX=-1.5 CenterY=62 CenterZ=0 NormalX=0 NormalY=0 NormalZ=1 AngleXU=0 Radius=1.5 StartAngle=4.71239 EndAngle=7.85398
    g14: ArcOfCircle CenterX=-1.5 CenterY=56.25 CenterZ=0 NormalX=0 NormalY=0 NormalZ=1 AngleXU=0 Radius=1.5 StartAngle=4.71239 EndAngle=7.85398
    g15: ArcOfCircle CenterX=-11.49 CenterY=50.5 CenterZ=0 NormalX=0 NormalY=0 NormalZ=1 AngleXU=0 Radius=1.5 StartAngle=4.71239 EndAngle=7.85398
    g16: ArcOfCircle CenterX=-16.28 CenterY=44.75 CenterZ=0 NormalX=0 NormalY=0 NormalZ=1 AngleXU=0 Radius=1.5 StartAngle=4.71239 EndAngle=7.85398
    g17: ArcOfCircle CenterX=-18.2337 CenterY=39 CenterZ=0 NormalX=0 NormalY=0 NormalZ=1 AngleXU=0 Radius=1.5 StartAngle=4.71485 EndAngle=7.85398
    g18: ArcOfCircle CenterX=-16.2837 CenterY=27.25 CenterZ=0 NormalX=0 NormalY=0 NormalZ=1 AngleXU=0 Radius=1.5 StartAngle=4.71485 EndAngle=7.85398
    g19: ArcOfCircle CenterX=-18.2337 CenterY=33 CenterZ=0 NormalX=0 NormalY=0 NormalZ=1 AngleXU=0 Radius=1.5 StartAngle=4.71485 EndAngle=7.85398
    g20: ArcOfCircle CenterX=-11.49 CenterY=21.5 CenterZ=0 NormalX=0 NormalY=0 NormalZ=1 AngleXU=0 Radius=1.5 StartAngle=4.71239 EndAngle=7.85398
    g21: ArcOfCircle CenterX=-1.5 CenterY=4.25 CenterZ=0 NormalX=0 NormalY=0 NormalZ=1 AngleXU=0 Radius=1.5 StartAngle=4.71239 EndAngle=7.85398
    g22: ArcOfCircle CenterX=-1.5 CenterY=10 CenterZ=0 NormalX=0 NormalY=0 NormalZ=1 AngleXU=0 Radius=1.5 StartAngle=4.71239 EndAngle=7.85398
    g23: ArcOfCircle CenterX=-1.5 CenterY=15.75 CenterZ=0 NormalX=0 NormalY=0 NormalZ=1 AngleXU=0 Radius=1.5 StartAngle=4.71239 EndAngle=7.85398
    g24: LineSegment StartX=-49.19 StartY=69.25 StartZ=0 EndX=-1.5 EndY=69.25 EndZ=0
    g25: LineSegment StartX=-49.19 StartY=66.25 StartZ=0 EndX=-1.5 EndY=66.25 EndZ=0
    g26: LineSegment StartX=-49.19 StartY=63.5 StartZ=0 EndX=-1.5 EndY=63.5 EndZ=0
    g27: LineSegment StartX=-49.19 StartY=60.5 StartZ=0 EndX=-1.5 EndY=60.5 EndZ=0
    g28: LineSegment StartX=-49.19 StartY=57.75 StartZ=0 EndX=-1.5 EndY=57.75 EndZ=0
    g29: LineSegment StartX=-49.19 StartY=54.75 StartZ=0 EndX=-1.5 EndY=54.75 EndZ=0
    g30: LineSegment StartX=-49.19 StartY=52 StartZ=0 EndX=-11.49 EndY=52 EndZ=0
    g31: LineSegment StartX=-49.19 StartY=49 StartZ=0 EndX=-11.49 EndY=49 EndZ=0
    g32: LineSegment StartX=-49.19 StartY=46.25 StartZ=0 EndX=-16.28 EndY=46.25 EndZ=0
    g33: LineSegment StartX=-49.19 StartY=43.25 StartZ=0 EndX=-16.28 EndY=43.25 EndZ=0
    g34: LineSegment StartX=-49.19 StartY=40.5 StartZ=0 EndX=-18.2337 EndY=40.5 EndZ=0
    g35: LineSegment StartX=-49.19 StartY=37.5 StartZ=0 EndX=-18.23 EndY=37.5 EndZ=0
    g36: LineSegment StartX=-49.19 StartY=34.5 StartZ=0 EndX=-18.2337 EndY=34.5 EndZ=0
    g37: LineSegment StartX=-49.19 StartY=31.5 StartZ=0 EndX=-18.23 EndY=31.5 EndZ=0
    g38: LineSegment StartX=-49.19 StartY=28.75 StartZ=0 EndX=-16.2837 EndY=28.75 EndZ=0
    g39: LineSegment StartX=-49.19 StartY=25.75 StartZ=0 EndX=-16.28 EndY=25.75 EndZ=0
    g40: LineSegment StartX=-49.19 StartY=23 StartZ=0 EndX=-11.49 EndY=23 EndZ=0
    g41: LineSegment StartX=-49.19 StartY=20 StartZ=0 EndX=-11.49 EndY=20 EndZ=0
    g42: LineSegment StartX=-49.19 StartY=17.25 StartZ=0 EndX=-1.5 EndY=17.25 EndZ=0
    g43: LineSegment StartX=-49.19 StartY=14.25 StartZ=0 EndX=-1.5 EndY=14.25 EndZ=0
    g44: LineSegment StartX=-49.19 StartY=11.5 StartZ=0 EndX=-1.5 EndY=11.5 EndZ=0
    g45: LineSegment StartX=-49.19 StartY=8.5 StartZ=0 EndX=-1.5 EndY=8.5 EndZ=0
    g46: LineSegment StartX=-49.19 StartY=5.75 StartZ=0 EndX=-1.5 EndY=5.75 EndZ=0
    g47: LineSegment StartX=-49.19 StartY=2.75 StartZ=0 EndX=-1.5 EndY=2.75 EndZ=0
  constraints (120):
    c: Vertical(g0)
    c: Distance(g0) = 3
    c: Block(g0)
    c: Vertical(g1)
    c: Distance(g1) = 3
    c: Vertical(g2)
    c: Equal(g0,g2) = 3
    c: Block(g2)
    c: Vertical(g3)
    c: Equal(g1,g3) = 3
    c: Vertical(g4)
    c: Equal(g0,g4) = 3
    c: Block(g4)
    c: Vertical(g5)
    c: Equal(g1,g5) = 3
    c: Vertical(g6)
    c: Equal(g0,g6) = 3
    c: Block(g6)
    c: Vertical(g7)
    c: Equal(g1,g7) = 3
    c: Vertical(g8)
    c: Equal(g0,g8) = 3
    c: Block(g8)
    c: Vertical(g9)
    c: Equal(g1,g9) = 3
    c: Vertical(g10)
    c: Equal(g0,g10) = 3
    c: Block(g10)
    c: Vertical(g11)
    c: Equal(g1,g11) = 3
    c: Block(g12)
    c: Block(g13)
    c: Block(g14)
    c: Block(g15)
    c: Block(g16)
    c: Block(g17)
    c: Block(g18)
    c: Block(g19)
    c: Block(g20)
    c: Block(g21)
    c: Block(g22)
    c: Block(g23)
    c: Block(g11)
    c: Block(g9)
    c: Block(g7)
    c: Block(g5)
    c: Block(g3)
    c: Block(g1)
    c: Coincident(g24,g0)
    c: Coincident(g24,g12)
    c: Horizontal(g24)
    c: Coincident(g25,g0)
    c: Coincident(g25,g12)
    c: Horizontal(g25)
    c: Coincident(g26,g1)
    c: Coincident(g26,g13)
    c: Horizontal(g26)
    c: Coincident(g27,g1)
    c: Coincident(g27,g13)
    c: Horizontal(g27)
    c: Coincident(g28,g2)
    c: Coincident(g28,g14)
    c: Horizontal(g28)
    c: Coincident(g29,g2)
    c: Coincident(g29,g14)
    c: Horizontal(g29)
    c: Coincident(g30,g3)
    c: Coincident(g30,g15)
    c: Horizontal(g30)
    c: Coincident(g31,g3)
    c: Coincident(g31,g15)
    c: Horizontal(g31)
    c: Coincident(g32,g4)
    c: Coincident(g32,g16)
    c: Horizontal(g32)
    c: Coincident(g33,g4)
    c: Coincident(g33,g16)
    c: Horizontal(g33)
    c: Coincident(g34,g5)
    c: Coincident(g34,g17)
    c: Horizontal(g34)
    c: Coincident(g35,g5)
    c: Coincident(g35,g17)
    c: Horizontal(g35)
    c: Coincident(g36,g6)
    c: Coincident(g36,g19)
    c: Horizontal(g36)
    c: Coincident(g37,g6)
    c: Coincident(g37,g19)
    c: Horizontal(g37)
    c: Coincident(g38,g7)
    c: Coincident(g38,g18)
    c: Horizontal(g38)
    c: Coincident(g39,g7)
    c: Coincident(g39,g18)
    c: Horizontal(g39)
    c: Coincident(g40,g8)
    c: Coincident(g40,g20)
    c: Horizontal(g40)
    c: Coincident(g41,g8)
    c: Coincident(g41,g20)
    c: Horizontal(g41)
    c: Coincident(g42,g9)
    c: Coincident(g42,g23)
    c: Horizontal(g42)
    c: Coincident(g43,g9)
    c: Coincident(g43,g23)
    c: Horizontal(g43)
    c: Coincident(g44,g10)
    c: Coincident(g44,g22)
    c: Horizontal(g44)
    c: Coincident(g45,g10)
    c: Coincident(g45,g22)
    c: Horizontal(g45)
    c: Coincident(g46,g11)
    c: Coincident(g46,g21)
    c: Horizontal(g46)
    c: Coincident(g47,g11)
    c: Coincident(g47,g21)
    c: Horizontal(g47)
FEATURE [Part::Extrusion] Extrude023
  Base = -> Sketch032
  Dir = (1,-2e-16,2e-16)
  DirMode = 2
  FaceMakerClass = Part::FaceMakerBullseye
  LengthFwd = 19
  LengthRev = 0
  Placement = pos=(-19,0,0) rot=(0,0,1;0rad)
  Solid = true
  Symmetric = false
FEATURE [Part::Fillet] Fillet023
  Base = -> Extrude023
  Edges = <same value as first occurrence — deduplicated (x6 in doc)>
  Placement = pos=(0,0.05,0) rot=(0,0,1;0rad)
FEATURE [Part::Cut] Cut014  label="bottom003"
  Base = -> Cut007
  Tool = -> Fusion047
FEATURE [Part::Cut] Cut021  label="bottom004"
  Base = -> Cut014
  Tool = -> Fillet023
FEATURE [Sketcher::SketchObject] Sketch033
  FullyConstrained = true
  Placement = pos=(117,19,0) rot=(0.57735,0.57735,0.57735;2.0944rad)
  sketch-geometry (8):
    g0: LineSegment StartX=-49.19 StartY=69.25 StartZ=0 EndX=-49.19 EndY=66.25 EndZ=0
    g1: LineSegment StartX=-49.19 StartY=5.75 StartZ=0 EndX=-49.19 EndY=2.75 EndZ=0
    g2: ArcOfCircle CenterX=-1.5 CenterY=67.75 CenterZ=0 NormalX=0 NormalY=0 NormalZ=1 AngleXU=0 Radius=1.5 StartAngle=4.71239 EndAngle=7.85398
    g3: ArcOfCircle CenterX=-1.5 CenterY=4.25 CenterZ=0 NormalX=0 NormalY=0 NormalZ=1 AngleXU=0 Radius=1.5 StartAngle=4.71239 EndAngle=7.85398
    g4: LineSegment StartX=-49.19 StartY=69.25 StartZ=0 EndX=-1.5 EndY=69.25 EndZ=0
    g5: LineSegment StartX=-49.19 StartY=66.25 StartZ=0 EndX=-1.5 EndY=66.25 EndZ=0
    g6: LineSegment StartX=-49.19 StartY=5.75 StartZ=0 EndX=-1.5 EndY=5.75 EndZ=0
    g7: LineSegment StartX=-49.19 StartY=2.75 StartZ=0 EndX=-1.5 EndY=2.75 EndZ=0
  constraints (19):
    c: Vertical(g0)
    c: Distance(g0) = 3
    c: Block(g0)
    c: Vertical(g1)
    c: Block(g2)
    c: Block(g3)
    c: Block(g1)
    c: Coincident(g4,g0)
    c: Coincident(g4,g2)
    c: Horizontal(g4)
    c: Coincident(g5,g0)
    c: Coincident(g5,g2)
    c: Horizontal(g5)
    c: Coincident(g6,g1)
    c: Coincident(g6,g3)
    c: Horizontal(g6)
    c: Coincident(g7,g1)
    c: Coincident(g7,g3)
    c: Horizontal(g7)
FEATURE [Sketcher::SketchObject] Sketch034
  FullyConstrained = true
  Placement = pos=(117,19,0) rot=(0.57735,0.57735,0.57735;2.0944rad)
  sketch-geometry (8):
    g0: LineSegment StartX=-49.19 StartY=63.5 StartZ=0 EndX=-49.19 EndY=60.5 EndZ=0
    g1: LineSegment StartX=-49.19 StartY=11.5 StartZ=0 EndX=-49.19 EndY=8.5 EndZ=0
    g2: ArcOfCircle CenterX=-1.5 CenterY=62 CenterZ=0 NormalX=0 NormalY=0 NormalZ=1 AngleXU=0 Radius=1.5 StartAngle=4.71239 EndAngle=7.85398
    g3: ArcOfCircle CenterX=-1.5 CenterY=10 CenterZ=0 NormalX=0 NormalY=0 NormalZ=1 AngleXU=0 Radius=1.5 StartAngle=4.71239 EndAngle=7.85398
    g4: LineSegment StartX=-49.19 StartY=63.5 StartZ=0 EndX=-1.5 EndY=63.5 EndZ=0
    g5: LineSegment StartX=-49.19 StartY=60.5 StartZ=0 EndX=-1.5 EndY=60.5 EndZ=0
    g6: LineSegment StartX=-49.19 StartY=11.5 StartZ=0 EndX=-1.5 EndY=11.5 EndZ=0
    g7: LineSegment StartX=-49.19 StartY=8.5 StartZ=0 EndX=-1.5 EndY=8.5 EndZ=0
  constraints (19):
    c: Vertical(g0)
    c: Distance(g0) = 3
    c: Vertical(g1)
    c: Block(g1)
    c: Block(g2)
    c: Block(g3)
    c: Block(g0)
    c: Coincident(g4,g0)
    c: Coincident(g4,g2)
    c: Horizontal(g4)
    c: Coincident(g5,g0)
    c: Coincident(g5,g2)
    c: Horizontal(g5)
    c: Coincident(g6,g1)
    c: Coincident(g6,g3)
    c: Horizontal(g6)
    c: Coincident(g7,g1)
    c: Coincident(g7,g3)
    c: Horizontal(g7)
FEATURE [Part::Extrusion] Extrude024
  Base = -> Sketch033
  Dir = (1,0,0)
  DirMode = 2
  FaceMakerClass = Part::FaceMakerBullseye
  LengthFwd = 10
  LengthRev = 0
  Solid = true
  Symmetric = false
FEATURE [Part::Extrusion] Extrude025
  Base = -> Sketch034
  Dir = (1,0,0)
  DirMode = 2
  FaceMakerClass = Part::FaceMakerBullseye
  LengthFwd = 10
  LengthRev = 0
  Solid = true
  Symmetric = false
FEATURE [Part::Fillet] Fillet024  label="removeFromtMoreFrontCaseScrewRetainers"
  Base = -> Extrude024
  Edges = 4 edges r=1.49: [Edge6,Edge11,Edge18,Edge23]
  Placement = pos=(-11,0,0) rot=(0,0,1;0rad)
FEATURE [Part::Fillet] Fillet025  label="removeFromtMoreFrontCaseScrewRetainers001"
  Base = -> Extrude025
  Edges = 4 edges r=1.49: [Edge6,Edge11,Edge18,Edge23]
  Placement = pos=(-19,0,0) rot=(0,0,1;0rad)
FEATURE [Part::Cut] Cut022
  Base = -> Cut015
  Tool = -> Fillet025
FEATURE [Part::Cut] Cut023  label="screwRetainers"
  Base = -> Cut022
  Tool = -> Fillet024
FEATURE [Part::MultiFuse] Fusion056  label="bottom005"
  Shapes = -> [Fusion044,Cut021]
FEATURE [Part::MultiFuse] Fusion057  label="casePillars001"
  Shapes = -> [Cut016,Fusion052]
FEATURE [Part::MultiFuse] Fusion058  label="bottom006"
  Shapes = -> [Fusion056,Cut023]
FEATURE [Part::MultiFuse] Fusion059  label="bottom007"
  Shapes = -> [Fusion058,Fillet005]
FEATURE [Part::MultiFuse] Fusion060  label="bottom008"
  Shapes = -> [Fusion059,Fusion]
FEATURE [Part::MultiFuse] Fusion061  label="top011"
  Shapes = -> [Cut006,Cut020]
FEATURE [Part::MultiFuse] Fusion062  label="top012"
  Shapes = -> [Fusion057,Fusion061]
FEATURE [Sketcher::SketchObject] Sketch035  label="topSketch007"
  FullyConstrained = true
  sketch-geometry (6):
    g0: LineSegment StartX=19 StartY=38 StartZ=0 EndX=117 EndY=38 EndZ=0
    g1: ArcOfCircle CenterX=19 CenterY=19 CenterZ=0 NormalX=0 NormalY=0 NormalZ=1 AngleXU=0 Radius=19 StartAngle=1.5708 EndAngle=3.14159
    g2: LineSegment StartX=117 StartY=38 StartZ=0 EndX=117 EndY=19 EndZ=0
    g3: LineSegment StartX=98 StartY=1.0161e-12 StartZ=0 EndX=5.22862e-06 EndY=1.0161e-12 EndZ=0
    g4: LineSegment StartX=5.22862e-06 StartY=19 StartZ=0 EndX=5.22862e-06 EndY=1.0161e-12 EndZ=0
    g5: ArcOfCircle CenterX=98 CenterY=19 CenterZ=0 NormalX=0 NormalY=0 NormalZ=1 AngleXU=0 Radius=19 StartAngle=4.71239 EndAngle=6.28319
  constraints (16):
    c: Horizontal(g0)
    c: Distance(g0) = 98
    c: Coincident(g1,g0)
    c: Block(g1)
    c: Coincident(g2,g0)
    c: Vertical(g2)
    c: Distance(g2) = 19
    c: Horizontal(g3)
    c: Coincident(g4,g1)
    c: Vertical(g4)
    c: Coincident(g3,g4)
    c: Block(g3)
    c: Coincident(g5,g2)
    c: Coincident(g5,g3)
    c: Block(g0)
    c: Block(g5)
FEATURE [Part::Extrusion] Extrude026  label="sideA001"
  Base = -> Sketch035
  Dir = (0,0,1)
  DirMode = 2
  FaceMakerClass = Part::FaceMakerBullseye
  LengthFwd = 3
  LengthRev = 0
  Placement = pos=(0,0,-2.7) rot=(0,0,1;0rad)
  Solid = true
  Symmetric = false
FEATURE [Sketcher::SketchObject] Sketch036  label="topSketch008"
  FullyConstrained = true
  sketch-geometry (6):
    g0: LineSegment StartX=19 StartY=38 StartZ=0 EndX=117 EndY=38 EndZ=0
    g1: ArcOfCircle CenterX=19 CenterY=19 CenterZ=0 NormalX=0 NormalY=0 NormalZ=1 AngleXU=0 Radius=19 StartAngle=1.5708 EndAngle=3.14159
    g2: LineSegment StartX=117 StartY=38 StartZ=0 EndX=117 EndY=19 EndZ=0
    g3: LineSegment StartX=98 StartY=1.0161e-12 StartZ=0 EndX=5.22862e-06 EndY=1.0161e-12 EndZ=0
    g4: LineSegment StartX=5.22862e-06 StartY=19 StartZ=0 EndX=5.22862e-06 EndY=1.0161e-12 EndZ=0
    g5: ArcOfCircle CenterX=98 CenterY=19 CenterZ=0 NormalX=0 NormalY=0 NormalZ=1 AngleXU=0 Radius=19 StartAngle=4.71239 EndAngle=6.28319
  constraints (16):
    c: Horizontal(g0)
    c: Distance(g0) = 98
    c: Coincident(g1,g0)
    c: Block(g1)
    c: Coincident(g2,g0)
    c: Vertical(g2)
    c: Distance(g2) = 19
    c: Horizontal(g3)
    c: Coincident(g4,g1)
    c: Vertical(g4)
    c: Coincident(g3,g4)
    c: Block(g3)
    c: Coincident(g5,g2)
    c: Coincident(g5,g3)
    c: Block(g0)
    c: Block(g5)
FEATURE [Part::Extrusion] Extrude027  label="sideB001"
  Base = -> Sketch036
  Dir = (0,0,1)
  DirMode = 2
  FaceMakerClass = Part::FaceMakerBullseye
  LengthFwd = 3
  LengthRev = 0
  Placement = pos=(0,0,71.7) rot=(0,0,1;0rad)
  Solid = true
  Symmetric = false
FEATURE [Part::MultiFuse] Fusion064  label="removeFromBottom"
  Shapes = -> [Extrude026,Extrude027]
FEATURE [Part::Cut] Cut024  label="bottom009"
  Base = -> Fusion060
  Tool = -> Fusion064
FEATURE [Sketcher::SketchObject] Sketch037  label="topSketch009"
  FullyConstrained = true
  sketch-geometry (8):
    g0: ArcOfCircle CenterX=19 CenterY=19.1201 CenterZ=0 NormalX=0 NormalY=0 NormalZ=1 AngleXU=0 Radius=18.8799 StartAngle=1.5708 EndAngle=3.14793
    g1: LineSegment StartX=0.120501 StartY=19.0004 StartZ=0 EndX=0.120501 EndY=0.000382114 EndZ=0
    g2: LineSegment StartX=19 StartY=38 StartZ=0 EndX=124 EndY=38 EndZ=0
    g3: LineSegment StartX=0.120501 StartY=0.000382114 StartZ=0 EndX=105.121 EndY=0.000382114 EndZ=0
    g4: LineSegment StartX=124 StartY=38 StartZ=0 EndX=125.616 EndY=38 EndZ=0
    g5: LineSegment StartX=105.121 StartY=0.000382114 StartZ=0 EndX=106.736 EndY=0.000382114 EndZ=0
    g6: ArcOfCircle CenterX=106.616 CenterY=19 CenterZ=0 NormalX=0 NormalY=0 NormalZ=1 AngleXU=0 Radius=19 StartAngle=4.71873 EndAngle=6.28319
    g7: LineSegment StartX=125.616 StartY=38 StartZ=0 EndX=125.616 EndY=19 EndZ=0
  constraints (21):
    c: Block(g0)
    c: Coincident(g1,g0)
    c: Vertical(g1)
    c: Horizontal(g2)
    c: Distance(g2) = 105
    c: Coincident(g2,g0)
    c: Distance(g1) = 19
    c: Coincident(g3,g1)
    c: Horizontal(g3)
    c: Distance(g3) = 105
    c: Coincident(g4,g2)
    c: Horizontal(g4)
    c: Distance(g4) = 1.61553
    c: Horizontal(g5)
    c: Equal(g4,g5) = 1.61553
    c: Coincident(g5,g3)
    c: Block(g6)
    c: Coincident(g6,g5)
    c: Coincident(g7,g4)
    c: Coincident(g7,g6)
    c: Vertical(g7)
FEATURE [Part::Extrusion] Extrude028  label="sideB"
  Base = -> Sketch037
  Dir = (0,0,1)
  DirMode = 2
  FaceMakerClass = Part::FaceMakerBullseye
  LengthFwd = 3
  LengthRev = 0
  Placement = pos=(0,0,72) rot=(0,0,1;0rad)
  Solid = true
  Symmetric = false
FEATURE [Sketcher::SketchObject] Sketch038  label="topSketch010"
  FullyConstrained = true
  sketch-geometry (22):
    g0: LineSegment StartX=5.21097e-06 StartY=3 StartZ=0 EndX=5.21097e-06 EndY=19 EndZ=0
    g1: ArcOfCircle CenterX=19 CenterY=19 CenterZ=0 NormalX=0 NormalY=0 NormalZ=1 AngleXU=0 Radius=19 StartAngle=1.5708 EndAngle=3.14159
    g2: ArcOfCircle CenterX=19 CenterY=19 CenterZ=0 NormalX=0 NormalY=0 NormalZ=1 AngleXU=0 Radius=16 StartAngle=1.5708 EndAngle=3.14159
    g3: LineSegment StartX=114 StartY=35 StartZ=0 EndX=19 EndY=35 EndZ=0
    g4: LineSegment StartX=5.21097e-06 StartY=3 StartZ=0 EndX=5.21097e-06 EndY=0 EndZ=0
    g5: LineSegment StartX=3 StartY=0 StartZ=0 EndX=5.21097e-06 EndY=0 EndZ=0
    g6: LineSegment StartX=3 StartY=19 StartZ=0 EndX=3 EndY=0 EndZ=0
    g7: LineSegment StartX=19 StartY=38 StartZ=0 EndX=124 EndY=38 EndZ=0
    g8: Circle CenterX=119 CenterY=35 CenterZ=0 NormalX=0 NormalY=0 NormalZ=1 AngleXU=0 Radius=1
    g9: Circle CenterX=121 CenterY=35 CenterZ=0 NormalX=0 NormalY=0 NormalZ=1 AngleXU=0 Radius=1
    g10: Circle CenterX=121 CenterY=33 CenterZ=0 NormalX=0 NormalY=0 NormalZ=1 AngleXU=0 Radius=1
    g11: BSplineCurve PolesCount=3 KnotsCount=2 Degree=2 IsPeriodic=0
    g12: GeomPoint X=119 Y=35 Z=0
    g13: GeomPoint X=121 Y=33 Z=0
    g14: LineSegment StartX=119 StartY=35 StartZ=0 EndX=114 EndY=35 EndZ=0
    g15: ArcOfCircle CenterX=105 CenterY=19 CenterZ=0 NormalX=0 NormalY=0 NormalZ=1 AngleXU=0 Radius=16 StartAngle=5.60905 EndAngle=6.28319
    g16: LineSegment StartX=121 StartY=33 StartZ=0 EndX=121 EndY=19 EndZ=0
    g17: LineSegment StartX=117.5 StartY=9.01251 StartZ=0 EndX=121.163 EndY=9.0125 EndZ=0
    g18: ArcOfCircle CenterX=105 CenterY=19 CenterZ=0 NormalX=0 NormalY=0 NormalZ=1 AngleXU=0 Radius=20.6155 StartAngle=5.7297 EndAngle=6.28319
    g19: LineSegment StartX=121.163 StartY=9.0125 StartZ=0 EndX=122.538 EndY=8.16329 EndZ=0
    g20: LineSegment StartX=124 StartY=38 StartZ=0 EndX=125.616 EndY=38 EndZ=0
    g21: LineSegment StartX=125.616 StartY=19 StartZ=0 EndX=125.616 EndY=38 EndZ=0
  constraints (49):
    c: Vertical(g0)
    c: Block(g0)
    c: Coincident(g1,g0)
    c: Block(g1)
    c: Coincident(g2,g1)
    c: Block(g2)
    c: Coincident(g3,g2)
    c: Horizontal(g3)
    c: Tangent(g3,g2)
    c: Coincident(g4,g0)
    c: Distance(g4) = 3
    c: Vertical(g4)
    c: Coincident(g5,g4)
    c: Horizontal(g5)
    c: Coincident(g6,g2)
    c: Coincident(g6,g5)
    c: Vertical(g6)
    c: Horizontal(g7)
    c: Distance(g7) = 105
    c: Coincident(g7,g1)
    c: Block(g3)
    c: Weight(g8) = 1
    c: Equal(g8,g9)
    c: Equal(g8,g10)
    c: InternalAlignment(g8,g11)
    c: InternalAlignment(g9,g11)
    c: InternalAlignment(g10,g11)
    c: InternalAlignment(g12,g11)
    c: InternalAlignment(g13,g11)
    c: Block(g11)
    c: Coincident(g14,g11)
    c: Coincident(g14,g3)
    c: Horizontal(g14)
    c: Block(g15)
    c: Coincident(g16,g11)
    c: Coincident(g16,g15)
    c: Vertical(g16)
    c: Distance(g16) = 14
    c: Coincident(g17,g15)
    c: Block(g18)
    c: Coincident(g19,g18)
    c: Coincident(g20,g7)
    c: Horizontal(g20)
    c: Vertical(g21)
    c: Coincident(g20,g21)
    c: Block(g20)
    c: Block(g21)
    c: Block(g19)
    c: Block(g17)
FEATURE [Part::Extrusion] Extrude029
  Base = -> Sketch038
  Dir = (0,0,1)
  DirMode = 2
  FaceMakerClass = Part::FaceMakerBullseye
  LengthFwd = 72
  LengthRev = 0
  Solid = true
  Symmetric = false
FEATURE [Part::Feature] Face085
  shape: bbox 4.8 x 25.5 x 2e-07 mm, 1 faces, 0 solids (baked)
FEATURE [Part::Revolution] Revolve089  label="moreFrontCaseScrewPost003"
  Angle = 360
  Axis = (0,1,0)
  Base = (0,0,0)
  FaceMakerClass = Part::FaceMakerBullseye
  Placement = pos=(109.5,4.5,3.5) rot=(0,0,1;0rad)
  Solid = false
  Source = -> Face085
  Symmetric = false
FEATURE [Part::Feature] Face086
  shape: bbox 4.8 x 25.5 x 2e-07 mm, 1 faces, 0 solids (baked)
FEATURE [Part::Revolution] Revolve090  label="moreFrontCaseScrewPost004"
  Angle = 360
  Axis = (0,1,0)
  Base = (0,0,0)
  FaceMakerClass = Part::FaceMakerBullseye
  Placement = pos=(109.5,4.5,68.5) rot=(0,0,1;0rad)
  Solid = false
  Source = -> Face086
  Symmetric = false
FEATURE [Part::Fillet] Fillet026  label="top013"
  Base = -> Extrude029
  Edges = 1 edges r=2: [Edge35]
FEATURE [Sketcher::SketchObject] Sketch039
  FullyConstrained = true
  sketch-geometry (7):
    g0: LineSegment StartX=0 StartY=0 StartZ=0 EndX=0 EndY=6 EndZ=0
    g1: Circle CenterX=0 CenterY=0 CenterZ=0 NormalX=0 NormalY=0 NormalZ=1 AngleXU=0 Radius=1
    g2: Circle CenterX=8 CenterY=6 CenterZ=0 NormalX=0 NormalY=0 NormalZ=1 AngleXU=0 Radius=1
    g3: BSplineCurve PolesCount=3 KnotsCount=2 Degree=2 IsPeriodic=0
    g4: GeomPoint X=0 Y=0 Z=0
    g5: GeomPoint X=8 Y=6 Z=0
    g6: LineSegment StartX=0 StartY=6 StartZ=0 EndX=8 EndY=6 EndZ=0
  constraints (14):
    c: Coincident(g0,g-1)
    c: Distance(g0) = 6
    c: Vertical(g0)
    c: Coincident(g3,g0)
    c: Weight(g1) = 1
    c: Equal(g1,g2)
    c: InternalAlignment(g1,g3)
    c: InternalAlignment(g2,g3)
    c: InternalAlignment(g4,g3)
    c: InternalAlignment(g5,g3)
    c: Block(g3)
    c: Coincident(g6,g0)
    c: Coincident(g6,g3)
    c: Horizontal(g6)
FEATURE [Sketcher::SketchObject] Sketch040
  FullyConstrained = true
  sketch-geometry (7):
    g0: LineSegment StartX=0 StartY=0 StartZ=0 EndX=0 EndY=6 EndZ=0
    g1: Circle CenterX=0 CenterY=0 CenterZ=0 NormalX=0 NormalY=0 NormalZ=1 AngleXU=0 Radius=1
    g2: Circle CenterX=8 CenterY=6 CenterZ=0 NormalX=0 NormalY=0 NormalZ=1 AngleXU=0 Radius=1
    g3: BSplineCurve PolesCount=3 KnotsCount=2 Degree=2 IsPeriodic=0
    g4: GeomPoint X=0 Y=0 Z=0
    g5: GeomPoint X=8 Y=6 Z=0
    g6: LineSegment StartX=0 StartY=6 StartZ=0 EndX=8 EndY=6 EndZ=0
  constraints (14):
    c: Coincident(g0,g-1)
    c: Distance(g0) = 6
    c: Vertical(g0)
    c: Coincident(g3,g0)
    c: Weight(g1) = 1
    c: Equal(g1,g2)
    c: InternalAlignment(g1,g3)
    c: InternalAlignment(g2,g3)
    c: InternalAlignment(g4,g3)
    c: InternalAlignment(g5,g3)
    c: Block(g3)
    c: Coincident(g6,g0)
    c: Coincident(g6,g3)
    c: Horizontal(g6)
FEATURE [Sketcher::SketchObject] Sketch041
  FullyConstrained = true
  sketch-geometry (7):
    g0: LineSegment StartX=0 StartY=0 StartZ=0 EndX=0 EndY=6 EndZ=0
    g1: Circle CenterX=0 CenterY=0 CenterZ=0 NormalX=0 NormalY=0 NormalZ=1 AngleXU=0 Radius=1
    g2: Circle CenterX=8 CenterY=6 CenterZ=0 NormalX=0 NormalY=0 NormalZ=1 AngleXU=0 Radius=1
    g3: BSplineCurve PolesCount=3 KnotsCount=2 Degree=2 IsPeriodic=0
    g4: GeomPoint X=0 Y=0 Z=0
    g5: GeomPoint X=8 Y=6 Z=0
    g6: LineSegment StartX=0 StartY=6 StartZ=0 EndX=8 EndY=6 EndZ=0
  constraints (14):
    c: Coincident(g0,g-1)
    c: Distance(g0) = 6
    c: Vertical(g0)
    c: Coincident(g3,g0)
    c: Weight(g1) = 1
    c: Equal(g1,g2)
    c: InternalAlignment(g1,g3)
    c: InternalAlignment(g2,g3)
    c: InternalAlignment(g4,g3)
    c: InternalAlignment(g5,g3)
    c: Block(g3)
    c: Coincident(g6,g0)
    c: Coincident(g6,g3)
    c: Horizontal(g6)
FEATURE [Sketcher::SketchObject] Sketch042
  FullyConstrained = true
  sketch-geometry (7):
    g0: LineSegment StartX=0 StartY=0 StartZ=0 EndX=0 EndY=6 EndZ=0
    g1: Circle CenterX=0 CenterY=0 CenterZ=0 NormalX=0 NormalY=0 NormalZ=1 AngleXU=0 Radius=1
    g2: Circle CenterX=8 CenterY=6 CenterZ=0 NormalX=0 NormalY=0 NormalZ=1 AngleXU=0 Radius=1
    g3: BSplineCurve PolesCount=3 KnotsCount=2 Degree=2 IsPeriodic=0
    g4: GeomPoint X=0 Y=0 Z=0
    g5: GeomPoint X=8 Y=6 Z=0
    g6: LineSegment StartX=0 StartY=6 StartZ=0 EndX=8 EndY=6 EndZ=0
  constraints (14):
    c: Coincident(g0,g-1)
    c: Distance(g0) = 6
    c: Vertical(g0)
    c: Coincident(g3,g0)
    c: Weight(g1) = 1
    c: Equal(g1,g2)
    c: InternalAlignment(g1,g3)
    c: InternalAlignment(g2,g3)
    c: InternalAlignment(g4,g3)
    c: InternalAlignment(g5,g3)
    c: Block(g3)
    c: Coincident(g6,g0)
    c: Coincident(g6,g3)
    c: Horizontal(g6)
FEATURE [Part::Extrusion] Extrude030  label="caseScrewPillarBracket008"
  Base = -> Sketch039
  Dir = (0,0,1)
  DirMode = 2
  FaceMakerClass = Part::FaceMakerBullseye
  LengthFwd = 2.4
  LengthRev = 0
  Placement = pos=(15.76,29,8.8) rot=(0,1,0;0rad)
  Solid = true
  Symmetric = false
FEATURE [Part::Extrusion] Extrude031  label="caseScrewPillarBracket009"
  Base = -> Sketch040
  Dir = (0,0,1)
  DirMode = 2
  FaceMakerClass = Part::FaceMakerBullseye
  LengthFwd = 2.4
  LengthRev = 0
  Placement = pos=(15.76,29,60.8) rot=(0,0,1;0rad)
  Solid = true
  Symmetric = false
FEATURE [Part::Extrusion] Extrude032  label="caseScrewPillarBracket010"
  Base = -> Sketch041
  Dir = (0,0,1)
  DirMode = 2
  FaceMakerClass = Part::FaceMakerBullseye
  LengthFwd = 2.4
  LengthRev = 0
  Placement = pos=(13.7,29,13.26) rot=(0,-1,0;1.5708rad)
  Solid = true
  Symmetric = false
FEATURE [Part::Extrusion] Extrude033  label="caseScrewPillarBracket011"
  Base = -> Sketch042
  Dir = (0,0,1)
  DirMode = 2
  FaceMakerClass = Part::FaceMakerBullseye
  LengthFwd = 2.4
  LengthRev = 0
  Placement = pos=(11.3,29,58.74) rot=(0,1,0;1.5708rad)
  Solid = true
  Symmetric = false
FEATURE [Sketcher::SketchObject] Sketch043
  FullyConstrained = true
  sketch-geometry (7):
    g0: LineSegment StartX=0 StartY=0 StartZ=0 EndX=0 EndY=6 EndZ=0
    g1: Circle CenterX=0 CenterY=0 CenterZ=0 NormalX=0 NormalY=0 NormalZ=1 AngleXU=0 Radius=1
    g2: Circle CenterX=8 CenterY=6 CenterZ=0 NormalX=0 NormalY=0 NormalZ=1 AngleXU=0 Radius=1
    g3: BSplineCurve PolesCount=3 KnotsCount=2 Degree=2 IsPeriodic=0
    g4: GeomPoint X=0 Y=0 Z=0
    g5: GeomPoint X=8 Y=6 Z=0
    g6: LineSegment StartX=0 StartY=6 StartZ=0 EndX=8 EndY=6 EndZ=0
  constraints (14):
    c: Coincident(g0,g-1)
    c: Distance(g0) = 6
    c: Vertical(g0)
    c: Coincident(g3,g0)
    c: Weight(g1) = 1
    c: Equal(g1,g2)
    c: InternalAlignment(g1,g3)
    c: InternalAlignment(g2,g3)
    c: InternalAlignment(g4,g3)
    c: InternalAlignment(g5,g3)
    c: Block(g3)
    c: Coincident(g6,g0)
    c: Coincident(g6,g3)
    c: Horizontal(g6)
FEATURE [Part::Extrusion] Extrude034  label="caseScrewPillarBracket012"
  Base = -> Sketch043
  Dir = (0,0,1)
  DirMode = 2
  FaceMakerClass = Part::FaceMakerBullseye
  LengthFwd = 2.4
  LengthRev = 0
  Placement = pos=(88.3,29,65.23) rot=(0,1,0;1.5708rad)
  Solid = true
  Symmetric = false
FEATURE [Sketcher::SketchObject] Sketch044
  FullyConstrained = true
  sketch-geometry (7):
    g0: LineSegment StartX=0 StartY=0 StartZ=0 EndX=0 EndY=6 EndZ=0
    g1: Circle CenterX=0 CenterY=0 CenterZ=0 NormalX=0 NormalY=0 NormalZ=1 AngleXU=0 Radius=1
    g2: Circle CenterX=8 CenterY=6 CenterZ=0 NormalX=0 NormalY=0 NormalZ=1 AngleXU=0 Radius=1
    g3: BSplineCurve PolesCount=3 KnotsCount=2 Degree=2 IsPeriodic=0
    g4: GeomPoint X=0 Y=0 Z=0
    g5: GeomPoint X=8 Y=6 Z=0
    g6: LineSegment StartX=0 StartY=6 StartZ=0 EndX=8 EndY=6 EndZ=0
  constraints (14):
    c: Coincident(g0,g-1)
    c: Distance(g0) = 6
    c: Vertical(g0)
    c: Coincident(g3,g0)
    c: Weight(g1) = 1
    c: Equal(g1,g2)
    c: InternalAlignment(g1,g3)
    c: InternalAlignment(g2,g3)
    c: InternalAlignment(g4,g3)
    c: InternalAlignment(g5,g3)
    c: Block(g3)
    c: Coincident(g6,g0)
    c: Coincident(g6,g3)
    c: Horizontal(g6)
FEATURE [Part::Extrusion] Extrude035  label="caseScrewPillarBracket013"
  Base = -> Sketch044
  Dir = (0,0,1)
  DirMode = 2
  FaceMakerClass = Part::FaceMakerBullseye
  LengthFwd = 2.4
  LengthRev = 0
  Placement = pos=(90.7,29,6.77) rot=(0,-1,0;1.5708rad)
  Solid = true
  Symmetric = false
FEATURE [Sketcher::SketchObject] Sketch045
  FullyConstrained = true
  sketch-geometry (7):
    g0: LineSegment StartX=0 StartY=0 StartZ=0 EndX=0 EndY=6 EndZ=0
    g1: Circle CenterX=0 CenterY=0 CenterZ=0 NormalX=0 NormalY=0 NormalZ=1 AngleXU=0 Radius=1
    g2: Circle CenterX=8 CenterY=6 CenterZ=0 NormalX=0 NormalY=0 NormalZ=1 AngleXU=0 Radius=1
    g3: BSplineCurve PolesCount=3 KnotsCount=2 Degree=2 IsPeriodic=0
    g4: GeomPoint X=0 Y=0 Z=0
    g5: GeomPoint X=8 Y=6 Z=0
    g6: LineSegment StartX=0 StartY=6 StartZ=0 EndX=8 EndY=6 EndZ=0
  constraints (14):
    c: Coincident(g0,g-1)
    c: Distance(g0) = 6
    c: Vertical(g0)
    c: Coincident(g3,g0)
    c: Weight(g1) = 1
    c: Equal(g1,g2)
    c: InternalAlignment(g1,g3)
    c: InternalAlignment(g2,g3)
    c: InternalAlignment(g4,g3)
    c: InternalAlignment(g5,g3)
    c: Block(g3)
    c: Coincident(g6,g0)
    c: Coincident(g6,g3)
    c: Horizontal(g6)
FEATURE [Sketcher::SketchObject] Sketch046
  FullyConstrained = true
  sketch-geometry (7):
    g0: LineSegment StartX=0 StartY=0 StartZ=0 EndX=0 EndY=6 EndZ=0
    g1: Circle CenterX=0 CenterY=0 CenterZ=0 NormalX=0 NormalY=0 NormalZ=1 AngleXU=0 Radius=1
    g2: Circle CenterX=8 CenterY=6 CenterZ=0 NormalX=0 NormalY=0 NormalZ=1 AngleXU=0 Radius=1
    g3: BSplineCurve PolesCount=3 KnotsCount=2 Degree=2 IsPeriodic=0
    g4: GeomPoint X=0 Y=0 Z=0
    g5: GeomPoint X=8 Y=6 Z=0
    g6: LineSegment StartX=0 StartY=6 StartZ=0 EndX=8 EndY=6 EndZ=0
  constraints (14):
    c: Coincident(g0,g-1)
    c: Distance(g0) = 6
    c: Vertical(g0)
    c: Coincident(g3,g0)
    c: Weight(g1) = 1
    c: Equal(g1,g2)
    c: InternalAlignment(g1,g3)
    c: InternalAlignment(g2,g3)
    c: InternalAlignment(g4,g3)
    c: InternalAlignment(g5,g3)
    c: Block(g3)
    c: Coincident(g6,g0)
    c: Coincident(g6,g3)
    c: Horizontal(g6)
FEATURE [Part::Extrusion] Extrude036  label="caseScrewPillarBracket014"
  Base = -> Sketch045
  Dir = (0,0,1)
  DirMode = 2
  FaceMakerClass = Part::FaceMakerBullseye
  LengthFwd = 2.4
  LengthRev = 0
  Placement = pos=(110.7,29,6.77) rot=(0,-1,0;1.5708rad)
  Solid = true
  Symmetric = false
FEATURE [Part::Extrusion] Extrude037  label="caseScrewPillarBracket015"
  Base = -> Sketch046
  Dir = (0,0,1)
  DirMode = 2
  FaceMakerClass = Part::FaceMakerBullseye
  LengthFwd = 2.4
  LengthRev = 0
  Placement = pos=(108.3,29,65.23) rot=(0,1,0;1.5708rad)
  Solid = true
  Symmetric = false
FEATURE [Part::Box] Box013  label="frontCaseScrewPillarBracket002"
  AttacherType = Attacher::AttachEngine3D
  Height = 2.4
  Length = 22
  Placement = pos=(87,28,2.3) rot=(0,0,1;0rad)
  Width = 7
FEATURE [Part::Box] Box014  label="frontCaseScrewPillarBracket003"
  AttacherType = Attacher::AttachEngine3D
  Height = 2.4
  Length = 22
  Placement = pos=(87,28,67.3) rot=(0,0,1;0rad)
  Width = 7
FEATURE [Part::Feature] Face087
  shape: bbox 4.8 x 30.2 x 2e-07 mm, 1 faces, 0 solids (baked)
FEATURE [Part::Revolution] Revolve091  label="frontCaseScrewPost004"
  Angle = 360
  Axis = (0,1,0)
  Base = (0,0,0)
  FaceMakerClass = Part::FaceMakerBullseye
  Placement = pos=(89.5,4.5,3.5) rot=(0,0,1;0rad)
  Solid = false
  Source = -> Face087
  Symmetric = false
FEATURE [Part::Feature] Face088
  shape: bbox 4.8 x 30.2 x 2e-07 mm, 1 faces, 0 solids (baked)
FEATURE [Part::Revolution] Revolve092  label="frontCaseScrewPost005"
  Angle = 360
  Axis = (0,1,0)
  Base = (0,0,0)
  FaceMakerClass = Part::FaceMakerBullseye
  Placement = pos=(89.5,4.5,68.5) rot=(0,0,1;0rad)
  Solid = false
  Source = -> Face088
  Symmetric = false
FEATURE [Part::Feature] Face089
  shape: bbox 3.5 x 30.2 x 2e-07 mm, 1 faces, 0 solids (baked)
FEATURE [Part::Revolution] Revolve093  label="backCaseScrewPost002"
  Angle = 360
  Axis = (0,1,0)
  Base = (0,0,0)
  FaceMakerClass = Part::FaceMakerBullseye
  Placement = pos=(12.5,4.5,10) rot=(0,0,1;0rad)
  Solid = false
  Source = -> Face089
  Symmetric = false
FEATURE [Part::Feature] Face090
  shape: bbox 3.5 x 30.2 x 2e-07 mm, 1 faces, 0 solids (baked)
FEATURE [Part::Revolution] Revolve094  label="backCaseScrewPost003"
  Angle = 360
  Axis = (0,1,0)
  Base = (0,0,0)
  FaceMakerClass = Part::FaceMakerBullseye
  Placement = pos=(12.5,4.5,62) rot=(0,0,1;0rad)
  Solid = false
  Source = -> Face090
  Symmetric = false
FEATURE [Part::Box] Box015  label="Cube011"
  AttacherType = Attacher::AttachEngine3D
  Height = 28.8
  Length = 3
  Placement = pos=(107.3,28,21.6) rot=(0,0,1;0rad)
  Width = 7
FEATURE [Part::Box] Box016  label="Cube012"
  AttacherType = Attacher::AttachEngine3D
  Height = 3
  Length = 7.4
  Placement = pos=(107.3,28,18.6) rot=(0,0,1;0rad)
  Width = 7
FEATURE [Part::Box] Box017  label="Cube013"
  AttacherType = Attacher::AttachEngine3D
  Height = 3
  Length = 7.4
  Placement = pos=(107.3,28,50.4) rot=(0,0,1;0rad)
  Width = 7
FEATURE [Part::Cylinder] Cylinder024
  Angle = 360
  AttacherType = Attacher::AttachEngine3D
  Height = 20
  Placement = pos=(0,0,36.15) rot=(0,0,1;0rad)
  Radius = 14.3
FEATURE [Part::Cylinder] Cylinder025
  Angle = 360
  AttacherType = Attacher::AttachEngine3D
  Height = 10
  Placement = pos=(0,0,36.15) rot=(0,0,1;0rad)
  Radius = 4
FEATURE [Part::MultiFuse] Fusion066  label="removeToCreteHoleForPlugHousing009"
  Placement = pos=(70,19,36) rot=(0,1,0;1.5708rad)
  Shapes = -> [Cylinder024,Cylinder025]
FEATURE [Part::MultiFuse] Fusion065  label="plugHousingBracketHolder002"
  Shapes = -> [Box017,Box015,Box016]
FEATURE [Part::Cut] Cut025  label="plugHousingBracketHolder003"
  Base = -> Fusion065
  Placement = pos=(7,0,0) rot=(0,0,1;0rad)
  Tool = -> Fusion066
FEATURE [Sketcher::SketchObject] Sketch047
  FullyConstrained = false
  Placement = pos=(0,0,0) rot=(1,0,0;1.5708rad)
  sketch-geometry (24):
    g0: ArcOfCircle CenterX=-4 CenterY=-10.5 CenterZ=0 NormalX=0 NormalY=0 NormalZ=1 AngleXU=0 Radius=1.5 StartAngle=6e-16 EndAngle=3.14159
    g1: ArcOfCircle CenterX=-34.2 CenterY=-10.5 CenterZ=0 NormalX=0 NormalY=0 NormalZ=1 AngleXU=0 Radius=1.5 StartAngle=0 EndAngle=3.14159
    g2: ArcOfCircle CenterX=-34.2 CenterY=-27.7 CenterZ=0 NormalX=0 NormalY=0 NormalZ=1 AngleXU=0 Radius=1.5 StartAngle=3.14159 EndAngle=6.28319
    g3: ArcOfCircle CenterX=-4 CenterY=-27.7 CenterZ=0 NormalX=0 NormalY=0 NormalZ=1 AngleXU=0 Radius=1.5 StartAngle=3.1416 EndAngle=6.28319
    g4: ArcOfCircle CenterX=-10 CenterY=-4.3 CenterZ=0 NormalX=0 NormalY=0 NormalZ=1 AngleXU=0 Radius=1.5 StartAngle=2e-16 EndAngle=3.14159
    g5: ArcOfCircle CenterX=-16.1 CenterY=-1.8 CenterZ=0 NormalX=0 NormalY=0 NormalZ=1 AngleXU=0 Radius=1.5 StartAngle=5e-16 EndAngle=3.14159
    g6: ArcOfCircle CenterX=-22.1 CenterY=-1.8 CenterZ=0 NormalX=0 NormalY=0 NormalZ=1 AngleXU=0 Radius=1.5 StartAngle=5e-16 EndAngle=3.14159
    g7: ArcOfCircle CenterX=-28.2 CenterY=-4.3 CenterZ=0 NormalX=0 NormalY=0 NormalZ=1 AngleXU=0 Radius=1.5 StartAngle=2e-16 EndAngle=3.14159
    g8: ArcOfCircle CenterX=-10 CenterY=-33.9 CenterZ=0 NormalX=0 NormalY=0 NormalZ=1 AngleXU=0 Radius=1.5 StartAngle=3.14159 EndAngle=6.28319
    g9: ArcOfCircle CenterX=-16.1 CenterY=-36.4 CenterZ=0 NormalX=0 NormalY=0 NormalZ=1 AngleXU=0 Radius=1.5 StartAngle=3.14159 EndAngle=6.28319
    g10: ArcOfCircle CenterX=-22.1 CenterY=-36.4 CenterZ=0 NormalX=0 NormalY=0 NormalZ=1 AngleXU=0 Radius=1.5 StartAngle=3.14159 EndAngle=6.28319
    g11: ArcOfCircle CenterX=-28.2 CenterY=-33.9 CenterZ=0 NormalX=0 NormalY=0 NormalZ=1 AngleXU=0 Radius=1.5 StartAngle=3.14159 EndAngle=6.28319
    g12: LineSegment StartX=-35.7 StartY=-10.5 StartZ=0 EndX=-35.7 EndY=-27.7 EndZ=0
    g13: LineSegment StartX=-32.7 StartY=-10.5 StartZ=0 EndX=-32.7 EndY=-27.7 EndZ=0
    g14: LineSegment StartX=-29.7 StartY=-33.9 StartZ=0 EndX=-29.7 EndY=-4.3 EndZ=0
    g15: LineSegment StartX=-26.7 StartY=-33.9 StartZ=0 EndX=-26.7 EndY=-4.3 EndZ=0
    g16: LineSegment StartX=-2.5 StartY=-10.5 StartZ=0 EndX=-2.5 EndY=-27.7 EndZ=0
    g17: LineSegment StartX=-8.5 StartY=-4.3 StartZ=0 EndX=-8.5 EndY=-33.9 EndZ=0
    g18: LineSegment StartX=-5.5 StartY=-10.5 StartZ=0 EndX=-5.5 EndY=-27.7 EndZ=0
    g19: LineSegment StartX=-11.5 StartY=-4.3 StartZ=0 EndX=-11.5 EndY=-33.9 EndZ=0
    g20: LineSegment StartX=-14.6 StartY=-1.8 StartZ=0 EndX=-14.6 EndY=-36.4 EndZ=0
    g21: LineSegment StartX=-17.6 StartY=-1.8 StartZ=0 EndX=-17.6 EndY=-36.4 EndZ=0
    g22: LineSegment StartX=-20.6 StartY=-36.4 StartZ=0 EndX=-20.6 EndY=-1.8 EndZ=0
    g23: LineSegment StartX=-23.6 StartY=-1.8 StartZ=0 EndX=-23.6 EndY=-36.4 EndZ=0
  constraints (48):
    c: Block(g0)
    c: Block(g1)
    c: Block(g2)
    c: Block(g3)
    c: Block(g4)
    c: Block(g5)
    c: Block(g6)
    c: Block(g7)
    c: Block(g8)
    c: Block(g9)
    c: Block(g10)
    c: Block(g11)
    c: Coincident(g12,g1)
    c: Coincident(g12,g2)
    c: Vertical(g12)
    c: Coincident(g13,g1)
    c: Coincident(g13,g2)
    c: Vertical(g13)
    c: Coincident(g14,g11)
    c: Coincident(g14,g7)
    c: Vertical(g14)
    c: Coincident(g15,g11)
    c: Coincident(g15,g7)
    c: Vertical(g15)
    c: Coincident(g16,g0)
    c: Coincident(g16,g3)
    c: Vertical(g16)
    c: Coincident(g17,g4)
    c: Coincident(g17,g8)
    c: Vertical(g17)
    c: Coincident(g18,g0)
    c: Coincident(g18,g3)
    c: Vertical(g18)
    c: Coincident(g19,g4)
    c: Coincident(g19,g8)
    c: Vertical(g19)
    c: Coincident(g20,g5)
    c: Coincident(g20,g9)
    c: Vertical(g20)
    c: Coincident(g21,g5)
    c: Coincident(g21,g9)
    c: Vertical(g21)
    c: Coincident(g22,g10)
    c: Coincident(g22,g6)
    c: Vertical(g22)
    c: Coincident(g23,g6)
    c: Coincident(g23,g10)
    c: Vertical(g23)
FEATURE [Part::Extrusion] Extrude038  label="removeToCreateFanGrillHoles001"
  Base = -> Sketch047
  Dir = (0,-1,6e-16)
  DirMode = 2
  FaceMakerClass = Part::FaceMakerBullseye
  LengthFwd = 10
  LengthRev = 0
  Placement = pos=(65.4,44,54.82) rot=(0,0,1;0rad)
  Solid = true
  Symmetric = false
FEATURE [Part::Feature] Wire004
  shape: bbox 11 x 5.2 x 2e-07 mm, 0 faces, 0 solids (baked)
FEATURE [Part::Revolution] Revolve095
  Angle = 360
  Axis = (0,1,0)
  Base = (0,0,0)
  FaceMakerClass = Part::FaceMakerBullseye
  Placement = pos=(30.3,38,19.7) rot=(0,0,1;0rad)
  Solid = true
  Source = -> Wire004
  Symmetric = false
FEATURE [Part::Feature] Wire005
  shape: bbox 11 x 5.2 x 2e-07 mm, 0 faces, 0 solids (baked)
FEATURE [Part::Revolution] Revolve096
  Angle = 360
  Axis = (0,1,0)
  Base = (0,0,0)
  FaceMakerClass = Part::FaceMakerBullseye
  Placement = pos=(30.3,38,51.7) rot=(0,0,1;0rad)
  Solid = true
  Source = -> Wire005
  Symmetric = false
FEATURE [Part::Feature] Wire006
  shape: bbox 11 x 5.2 x 2e-07 mm, 0 faces, 0 solids (baked)
FEATURE [Part::Revolution] Revolve097
  Angle = 360
  Axis = (0,1,0)
  Base = (0,0,0)
  FaceMakerClass = Part::FaceMakerBullseye
  Placement = pos=(62.3,38,51.7) rot=(0,0,1;0rad)
  Solid = true
  Source = -> Wire006
  Symmetric = false
FEATURE [Part::Feature] Wire007
  shape: bbox 11 x 5.2 x 2e-07 mm, 0 faces, 0 solids (baked)
FEATURE [Part::Revolution] Revolve098
  Angle = 360
  Axis = (0,1,0)
  Base = (0,0,0)
  FaceMakerClass = Part::FaceMakerBullseye
  Placement = pos=(62.3,38,19.7) rot=(0,0,1;0rad)
  Solid = true
  Source = -> Wire007
  Symmetric = false
FEATURE [Part::MultiFuse] Fusion067  label="fanScrewHousing002"
  Shapes = -> [Revolve098,Revolve097,Revolve096,Revolve095]
FEATURE [Part::Feature] Face091 .. Face094  x4 (patterned run collapsed; names and placements below)
  shape: bbox 3.5 x 17.8 x 2e-07 mm, 1 faces, 0 solids (baked)
FEATURE [Part::Revolution] Revolve099  label="removeToCreateScrewAndThreadedInsertHole026"
  Angle = 360
  Axis = (0,1,0)
  Base = (0,0,0)
  FaceMakerClass = Part::FaceMakerBullseye
  Placement = pos=(62.3,30.3,19.7) rot=(0,0,1;0rad)
  Solid = false
  Source = -> Face091
  Symmetric = false
FEATURE [Part::Revolution] Revolve100  label="removeToCreateScrewAndThreadedInsertHole027"
  Angle = 360
  Axis = (0,1,0)
  Base = (0,0,0)
  FaceMakerClass = Part::FaceMakerBullseye
  Placement = pos=(62.3,30.3,51.7) rot=(0,0,1;0rad)
  Solid = false
  Source = -> Face092
  Symmetric = false
FEATURE [Part::Revolution] Revolve101  label="removeToCreateScrewAndThreadedInsertHole028"
  Angle = 360
  Axis = (0,1,0)
  Base = (0,0,0)
  FaceMakerClass = Part::FaceMakerBullseye
  Placement = pos=(30.3,30.3,19.7) rot=(0,0,1;0rad)
  Solid = false
  Source = -> Face093
  Symmetric = false
FEATURE [Part::Revolution] Revolve102  label="removeToCreateScrewAndThreadedInsertHole029"
  Angle = 360
  Axis = (0,1,0)
  Base = (0,0,0)
  FaceMakerClass = Part::FaceMakerBullseye
  Placement = pos=(30.3,30.3,51.7) rot=(0,0,1;0rad)
  Solid = false
  Source = -> Face094
  Symmetric = false
FEATURE [Part::MultiFuse] Fusion068  label="createThreadedInsertHolesForFan002"
  Shapes = -> [Revolve099,Revolve100,Revolve101,Revolve102]
FEATURE [Part::Cut] Cut026  label="fanScrewHousing003"
  Base = -> Fusion067
  Tool = -> Fusion068
FEATURE [Sketcher::SketchObject] Sketch048
  FullyConstrained = false
  Placement = pos=(0,0,0) rot=(1,0,0;1.5708rad)
  sketch-geometry (24):
    g0: ArcOfCircle CenterX=-4 CenterY=-10.5 CenterZ=0 NormalX=0 NormalY=0 NormalZ=1 AngleXU=0 Radius=1.5 StartAngle=6e-16 EndAngle=3.14159
    g1: ArcOfCircle CenterX=-34.2 CenterY=-10.5 CenterZ=0 NormalX=0 NormalY=0 NormalZ=1 AngleXU=0 Radius=1.5 StartAngle=0 EndAngle=3.14159
    g2: ArcOfCircle CenterX=-34.2 CenterY=-27.7 CenterZ=0 NormalX=0 NormalY=0 NormalZ=1 AngleXU=0 Radius=1.5 StartAngle=3.14159 EndAngle=6.28319
    g3: ArcOfCircle CenterX=-4 CenterY=-27.7 CenterZ=0 NormalX=0 NormalY=0 NormalZ=1 AngleXU=0 Radius=1.5 StartAngle=3.1416 EndAngle=6.28319
    g4: ArcOfCircle CenterX=-10 CenterY=-4.3 CenterZ=0 NormalX=0 NormalY=0 NormalZ=1 AngleXU=0 Radius=1.5 StartAngle=2e-16 EndAngle=3.14159
    g5: ArcOfCircle CenterX=-16.1 CenterY=-1.8 CenterZ=0 NormalX=0 NormalY=0 NormalZ=1 AngleXU=0 Radius=1.5 StartAngle=5e-16 EndAngle=3.14159
    g6: ArcOfCircle CenterX=-22.1 CenterY=-1.8 CenterZ=0 NormalX=0 NormalY=0 NormalZ=1 AngleXU=0 Radius=1.5 StartAngle=5e-16 EndAngle=3.14159
    g7: ArcOfCircle CenterX=-28.2 CenterY=-4.3 CenterZ=0 NormalX=0 NormalY=0 NormalZ=1 AngleXU=0 Radius=1.5 StartAngle=2e-16 EndAngle=3.14159
    g8: ArcOfCircle CenterX=-10 CenterY=-33.9 CenterZ=0 NormalX=0 NormalY=0 NormalZ=1 AngleXU=0 Radius=1.5 StartAngle=3.14159 EndAngle=6.28319
    g9: ArcOfCircle CenterX=-16.1 CenterY=-36.4 CenterZ=0 NormalX=0 NormalY=0 NormalZ=1 AngleXU=0 Radius=1.5 StartAngle=3.14159 EndAngle=6.28319
    g10: ArcOfCircle CenterX=-22.1 CenterY=-36.4 CenterZ=0 NormalX=0 NormalY=0 NormalZ=1 AngleXU=0 Radius=1.5 StartAngle=3.14159 EndAngle=6.28319
    g11: ArcOfCircle CenterX=-28.2 CenterY=-33.9 CenterZ=0 NormalX=0 NormalY=0 NormalZ=1 AngleXU=0 Radius=1.5 StartAngle=3.14159 EndAngle=6.28319
    g12: LineSegment StartX=-35.7 StartY=-10.5 StartZ=0 EndX=-35.7 EndY=-27.7 EndZ=0
    g13: LineSegment StartX=-32.7 StartY=-10.5 StartZ=0 EndX=-32.7 EndY=-27.7 EndZ=0
    g14: LineSegment StartX=-29.7 StartY=-33.9 StartZ=0 EndX=-29.7 EndY=-4.3 EndZ=0
    g15: LineSegment StartX=-26.7 StartY=-33.9 StartZ=0 EndX=-26.7 EndY=-4.3 EndZ=0
    g16: LineSegment StartX=-2.5 StartY=-10.5 StartZ=0 EndX=-2.5 EndY=-27.7 EndZ=0
    g17: LineSegment StartX=-8.5 StartY=-4.3 StartZ=0 EndX=-8.5 EndY=-33.9 EndZ=0
    g18: LineSegment StartX=-5.5 StartY=-10.5 StartZ=0 EndX=-5.5 EndY=-27.7 EndZ=0
    g19: LineSegment StartX=-11.5 StartY=-4.3 StartZ=0 EndX=-11.5 EndY=-33.9 EndZ=0
    g20: LineSegment StartX=-14.6 StartY=-1.8 StartZ=0 EndX=-14.6 EndY=-36.4 EndZ=0
    g21: LineSegment StartX=-17.6 StartY=-1.8 StartZ=0 EndX=-17.6 EndY=-36.4 EndZ=0
    g22: LineSegment StartX=-20.6 StartY=-36.4 StartZ=0 EndX=-20.6 EndY=-1.8 EndZ=0
    g23: LineSegment StartX=-23.6 StartY=-1.8 StartZ=0 EndX=-23.6 EndY=-36.4 EndZ=0
  constraints (48):
    c: Block(g0)
    c: Block(g1)
    c: Block(g2)
    c: Block(g3)
    c: Block(g4)
    c: Block(g5)
    c: Block(g6)
    c: Block(g7)
    c: Block(g8)
    c: Block(g9)
    c: Block(g10)
    c: Block(g11)
    c: Coincident(g12,g1)
    c: Coincident(g12,g2)
    c: Vertical(g12)
    c: Coincident(g13,g1)
    c: Coincident(g13,g2)
    c: Vertical(g13)
    c: Coincident(g14,g11)
    c: Coincident(g14,g7)
    c: Vertical(g14)
    c: Coincident(g15,g11)
    c: Coincident(g15,g7)
    c: Vertical(g15)
    c: Coincident(g16,g0)
    c: Coincident(g16,g3)
    c: Vertical(g16)
    c: Coincident(g17,g4)
    c: Coincident(g17,g8)
    c: Vertical(g17)
    c: Coincident(g18,g0)
    c: Coincident(g18,g3)
    c: Vertical(g18)
    c: Coincident(g19,g4)
    c: Coincident(g19,g8)
    c: Vertical(g19)
    c: Coincident(g20,g5)
    c: Coincident(g20,g9)
    c: Vertical(g20)
    c: Coincident(g21,g5)
    c: Coincident(g21,g9)
    c: Vertical(g21)
    c: Coincident(g22,g10)
    c: Coincident(g22,g6)
    c: Vertical(g22)
    c: Coincident(g23,g6)
    c: Coincident(g23,g10)
    c: Vertical(g23)
FEATURE [Part::Extrusion] Extrude039  label="removeToCreateFanGrillHoles002"
  Base = -> Sketch048
  Dir = (0,-1,6e-16)
  DirMode = 2
  FaceMakerClass = Part::FaceMakerBullseye
  LengthFwd = 10
  LengthRev = 0
  Placement = pos=(65.4,44,54.82) rot=(0,0,1;0rad)
  Solid = true
  Symmetric = false
FEATURE [Part::Cut] Cut027  label="fanScrewHousing004"
  Base = -> Cut026
  Tool = -> Extrude038
FEATURE [Part::Cut] Cut028  label="top014"
  Base = -> Fillet026
  Tool = -> Extrude039
FEATURE [Part::Feature] Face095 .. Face098  x4 (patterned run collapsed; names and placements below)
  shape: bbox 3.5 x 17.8 x 2e-07 mm, 1 faces, 0 solids (baked)
FEATURE [Part::Revolution] Revolve103  label="removeToCreateScrewAndThreadedInsertHole030"
  Angle = 360
  Axis = (0,1,0)
  Base = (0,0,0)
  FaceMakerClass = Part::FaceMakerBullseye
  Placement = pos=(62.3,30.3,19.7) rot=(0,0,1;0rad)
  Solid = false
  Source = -> Face095
  Symmetric = false
FEATURE [Part::Revolution] Revolve104  label="removeToCreateScrewAndThreadedInsertHole031"
  Angle = 360
  Axis = (0,1,0)
  Base = (0,0,0)
  FaceMakerClass = Part::FaceMakerBullseye
  Placement = pos=(62.3,30.3,51.7) rot=(0,0,1;0rad)
  Solid = false
  Source = -> Face096
  Symmetric = false
FEATURE [Part::Revolution] Revolve105  label="removeToCreateScrewAndThreadedInsertHole032"
  Angle = 360
  Axis = (0,1,0)
  Base = (0,0,0)
  FaceMakerClass = Part::FaceMakerBullseye
  Placement = pos=(30.3,30.3,19.7) rot=(0,0,1;0rad)
  Solid = false
  Source = -> Face097
  Symmetric = false
FEATURE [Part::Revolution] Revolve106  label="removeToCreateScrewAndThreadedInsertHole033"
  Angle = 360
  Axis = (0,1,0)
  Base = (0,0,0)
  FaceMakerClass = Part::FaceMakerBullseye
  Placement = pos=(30.3,30.3,51.7) rot=(0,0,1;0rad)
  Solid = false
  Source = -> Face098
  Symmetric = false
FEATURE [Part::MultiFuse] Fusion069  label="createThreadedInsertHolesForFan003"
  Shapes = -> [Revolve103,Revolve104,Revolve105,Revolve106]
FEATURE [Part::Cut] Cut029  label="top015"
  Base = -> Cut028
  Tool = -> Fusion054
FEATURE [Part::Cut] Cut030  label="fanScrewHousing005"
  Base = -> Cut027
  Tool = -> Fusion069
FEATURE [Part::Cylinder] Cylinder026  label="removeToCreteHoleForPlugHousing010"
  Angle = 360
  AttacherType = Attacher::AttachEngine3D
  Height = 20
  Placement = pos=(-2,19,36) rot=(0,1,0;1.5708rad)
  Radius = 14.3
FEATURE [Part::Box] Box018  label="removeToCreteHoleForPlugHousing011"
  AttacherType = Attacher::AttachEngine3D
  Height = 28.6
  Length = 10
  Placement = pos=(-2,0,21.7) rot=(0,0,1;0rad)
  Width = 19
FEATURE [Part::Box] Box019  label="wireHolderBottomCaseBit"
  AttacherType = Attacher::AttachEngine3D
  Height = 28
  Length = 3
  Placement = pos=(0,0,22) rot=(0,0,1;0rad)
  Width = 21
FEATURE [Part::Cylinder] Cylinder027  label="removeToCreteHoleForPlugHousing012"
  Angle = 360
  AttacherType = Attacher::AttachEngine3D
  Height = 20
  Placement = pos=(-2,19,36) rot=(0,1,0;1.5708rad)
  Radius = 14.3
FEATURE [Part::Cut] Cut031  label="wireHolderBottomCaseBit001"
  Base = -> Box019
  Tool = -> Cylinder027
FEATURE [Part::MultiFuse] Fusion070  label="removeToCreteHoleForPlugHousing013"
  Shapes = -> [Box018,Cylinder026]
FEATURE [Part::Cut] Cut032  label="top016"
  Base = -> Cut029
  Tool = -> Fusion070
FEATURE [Part::Cylinder] Cylinder028
  Angle = 360
  AttacherType = Attacher::AttachEngine3D
  Height = 20
  Placement = pos=(0,0,36.15) rot=(0,0,1;0rad)
  Radius = 14.3
FEATURE [Part::Cylinder] Cylinder029
  Angle = 360
  AttacherType = Attacher::AttachEngine3D
  Height = 10
  Placement = pos=(0,0,36.15) rot=(0,0,1;0rad)
  Radius = 4
FEATURE [Part::MultiFuse] Fusion071  label="removeToCreteHoleForPlugHousing014"
  Placement = pos=(70,19,36) rot=(0,1,0;1.5708rad)
  Shapes = -> [Cylinder028,Cylinder029]
FEATURE [Sketcher::SketchObject] Sketch049  label="topSketch011"
  FullyConstrained = true
  sketch-geometry (4):
    g0: ArcOfCircle CenterX=105 CenterY=19 CenterZ=0 NormalX=0 NormalY=0 NormalZ=1 AngleXU=0 Radius=20.6155 StartAngle=5.54125 EndAngle=6.28319
    g1: ArcOfCircle CenterX=105 CenterY=19 CenterZ=0 NormalX=0 NormalY=0 NormalZ=1 AngleXU=0 Radius=13 StartAngle=5.54125 EndAngle=6.28319
    g2: LineSegment StartX=118 StartY=19 StartZ=0 EndX=125.616 EndY=19 EndZ=0
    g3: LineSegment StartX=114.583 StartY=10.2157 StartZ=0 EndX=120.197 EndY=5.06982 EndZ=0
  constraints (7):
    c: Block(g0)
    c: Block(g1)
    c: Coincident(g2,g1)
    c: Coincident(g2,g0)
    c: Horizontal(g2)
    c: Coincident(g3,g1)
    c: Coincident(g3,g0)
FEATURE [Part::Box] Box020  label="removeToCreteHoleForPlugHousing015"
  AttacherType = Attacher::AttachEngine3D
  Height = 28.6
  Length = 20
  Placement = pos=(106.15,0,21.7) rot=(0,0,1;0rad)
  Width = 19
FEATURE [Part::MultiFuse] Fusion072  label="removeToCreteHoleForPlugHousing016"
  Shapes = -> [Box020,Fusion071]
FEATURE [Part::Cut] Cut033  label="removeToCreteHoleForPlugHousing017"
  Base = -> Cut032
  Tool = -> Fusion072
FEATURE [Part::Cylinder] Cylinder030
  Angle = 360
  AttacherType = Attacher::AttachEngine3D
  Height = 20
  Placement = pos=(0,0,36.15) rot=(0,0,1;0rad)
  Radius = 14.3
FEATURE [Part::Cylinder] Cylinder031
  Angle = 360
  AttacherType = Attacher::AttachEngine3D
  Height = 10
  Placement = pos=(0,0,36.15) rot=(0,0,1;0rad)
  Radius = 4
FEATURE [Part::Box] Box021  label="removeToCreteHoleForPlugHousing019"
  AttacherType = Attacher::AttachEngine3D
  Height = 28.6
  Length = 20
  Placement = pos=(106.15,0,21.7) rot=(0,0,1;0rad)
  Width = 19
FEATURE [Part::MultiFuse] Fusion074  label="removeToCreteHoleForPlugHousing020"
  Placement = pos=(70,19,36) rot=(0,1,0;1.5708rad)
  Shapes = -> [Cylinder030,Cylinder031]
FEATURE [Part::MultiFuse] Fusion073  label="removeToCreteHoleForPlugHousing018"
  Placement = pos=(0,0,28.3) rot=(0,0,1;0rad)
  Shapes = -> [Box021,Fusion074]
FEATURE [Part::Cylinder] Cylinder032
  Angle = 360
  AttacherType = Attacher::AttachEngine3D
  Height = 20
  Placement = pos=(0,0,36.15) rot=(0,0,1;0rad)
  Radius = 14.3
FEATURE [Part::Cylinder] Cylinder033
  Angle = 360
  AttacherType = Attacher::AttachEngine3D
  Height = 10
  Placement = pos=(0,0,36.15) rot=(0,0,1;0rad)
  Radius = 4
FEATURE [Part::Box] Box022  label="removeToCreteHoleForPlugHousing021"
  AttacherType = Attacher::AttachEngine3D
  Height = 28.6
  Length = 20
  Placement = pos=(106.15,0,21.7) rot=(0,0,1;0rad)
  Width = 19
FEATURE [Part::MultiFuse] Fusion076  label="removeToCreteHoleForPlugHousing023"
  Placement = pos=(70,19,36) rot=(0,1,0;1.5708rad)
  Shapes = -> [Cylinder032,Cylinder033]
FEATURE [Part::MultiFuse] Fusion075  label="removeToCreteHoleForPlugHousing022"
  Placement = pos=(0,0,-28.3) rot=(0,0,1;0rad)
  Shapes = -> [Box022,Fusion076]
FEATURE [Part::MultiFuse] Fusion077  label="removeToCreatePlugHousingBottomBit"
  Shapes = -> [Fusion075,Fusion073]
FEATURE [Part::Cylinder] Cylinder034
  Angle = 360
  AttacherType = Attacher::AttachEngine3D
  Height = 20
  Placement = pos=(0,0,36.15) rot=(0,0,1;0rad)
  Radius = 14
FEATURE [Part::Cylinder] Cylinder035
  Angle = 360
  AttacherType = Attacher::AttachEngine3D
  Height = 10
  Placement = pos=(0,0,36.15) rot=(0,0,1;0rad)
  Radius = 4
FEATURE [Part::MultiFuse] Fusion078  label="removeToCreteHoleForPlugHousing024"
  Placement = pos=(70,19,36) rot=(0,1,0;1.5708rad)
  Shapes = -> [Cylinder034,Cylinder035]
FEATURE [Part::MultiFuse] Fusion079  label="removeToCreatePlugHousingBottomBit001"
  Shapes = -> [Fusion078,Fusion077]
FEATURE [Part::Extrusion] Extrude040  label="bottomPlugHousingBit"
  Base = -> Sketch049
  Dir = (0,0,1)
  DirMode = 2
  FaceMakerClass = Part::FaceMakerBullseye
  LengthFwd = 72
  LengthRev = 0
  Solid = true
  Symmetric = false
FEATURE [Part::Cut] Cut034  label="bottomPlugHousingBit001"
  Base = -> Extrude040
  Placement = pos=(-0.09,0,0) rot=(0,0,1;0rad)
  Tool = -> Fusion079
FEATURE [Part::Box] Box023  label="Cube014"
  AttacherType = Attacher::AttachEngine3D
  Height = 16
  Length = 8
  Placement = pos=(12.7,31.52,28) rot=(0,0,1;0rad)
  Width = 4
FEATURE [Part::Cylinder] Cylinder036
  Angle = 360
  AttacherType = Attacher::AttachEngine3D
  Height = 10
  Placement = pos=(0,0,36.15) rot=(0,0,1;0rad)
  Radius = 4
FEATURE [Part::Cylinder] Cylinder037
  Angle = 360
  AttacherType = Attacher::AttachEngine3D
  Height = 20
  Placement = pos=(0,0,36.15) rot=(0,0,1;0rad)
  Radius = 8.2
FEATURE [Part::MultiFuse] Fusion080  label="removeToCreteHoleForPlugHousing025"
  Placement = pos=(-42,19,36) rot=(0,1,0;1.5708rad)
  Shapes = -> [Cylinder037,Cylinder036]
FEATURE [Sketcher::SketchObject] Sketch050  label="topSketch012"
  FullyConstrained = true
  sketch-geometry (4):
    g0: LineSegment StartX=16.8446 StartY=31.512 StartZ=0 EndX=16.3251 EndY=34.4666 EndZ=0
    g1: ArcOfCircle CenterX=19 CenterY=19.2524 CenterZ=0 NormalX=0 NormalY=0 NormalZ=1 AngleXU=0 Radius=15.4476 StartAngle=1.74483 EndAngle=2.72717
    g2: ArcOfCircle CenterX=19 CenterY=19.2524 CenterZ=0 NormalX=0 NormalY=0 NormalZ=1 AngleXU=0 Radius=12.4476 StartAngle=1.74483 EndAngle=2.73189
    g3: LineSegment StartX=4.86004 StartY=25.4725 StartZ=0 EndX=7.58253 EndY=24.2107 EndZ=0
  constraints (7):
    c: Block(g0)
    c: Coincident(g1,g0)
    c: Coincident(g2,g0)
    c: Coincident(g3,g1)
    c: Coincident(g3,g2)
    c: Block(g1)
    c: Block(g2)
FEATURE [Part::Extrusion] Extrude041
  Base = -> Sketch050
  Dir = (0,0,1)
  DirMode = 2
  FaceMakerClass = Part::FaceMakerBullseye
  LengthFwd = 10.6
  LengthRev = 0
  Placement = pos=(0,0,31) rot=(0,0,1;0rad)
  Solid = true
  Symmetric = false
FEATURE [Part::Cut] Cut035
  Base = -> Extrude041
  Placement = pos=(0,0,-0.3) rot=(0,0,1;0rad)
  Tool = -> Fusion080
FEATURE [Part::Cut] Cut036
  Base = -> Box023
  Tool = -> Cut035
FEATURE [Part::Fillet] Fillet027
  Base = -> Cut036
  Edges = 1 edges r=0.7: [Edge13]
FEATURE [Part::Fillet] Fillet028
  Base = -> Fillet027
  Edges = 1 edges r=0.7: [Edge13]
FEATURE [Part::Fillet] Fillet029
  Base = -> Fillet028
  Edges = 1 edges r=0.7: [Edge16]
FEATURE [Part::Fillet] Fillet030
  Base = -> Fillet029
  Edges = 1 edges r=0.7: [Edge11]
FEATURE [Part::Fillet] Fillet031
  Base = -> Fillet030
  Edges = 1 edges r=0.7: [Edge10]
FEATURE [Part::Fillet] Fillet032
  Base = -> Fillet031
  Edges = 1 edges r=1.2: [Edge5]
FEATURE [Part::Fillet] Fillet033
  Base = -> Fillet032
  Edges = 1 edges r=1.2: [Edge12]
FEATURE [Part::Fillet] Fillet034  label="wireHousingRetainer"
  Base = -> Fillet033
  Edges = 1 edges r=2: [Edge1]
  Placement = pos=(0.3,0,0) rot=(0,0,1;0rad)
FEATURE [Part::Feature] Face099
  shape: bbox 3.5 x 17.8 x 2e-07 mm, 1 faces, 0 solids (baked)
FEATURE [Part::Revolution] Revolve107  label="removeToCreateScrewAndThreadedInsertHole034"
  Angle = 360
  Axis = (0,1,0)
  Base = (0,0,0)
  FaceMakerClass = Part::FaceMakerBullseye
  Placement = pos=(12.5,0,10) rot=(0,0,1;0rad)
  Solid = false
  Source = -> Face099
  Symmetric = false
FEATURE [Part::Feature] Face100
  shape: bbox 3.5 x 17.8 x 2e-07 mm, 1 faces, 0 solids (baked)
FEATURE [Part::Revolution] Revolve108  label="removeToCreateScrewAndThreadedInsertHole035"
  Angle = 360
  Axis = (0,1,0)
  Base = (0,0,0)
  FaceMakerClass = Part::FaceMakerBullseye
  Placement = pos=(12.5,0,62) rot=(0,0,1;0rad)
  Solid = false
  Source = -> Face100
  Symmetric = false
FEATURE [Part::Feature] Face101
  shape: bbox 3.5 x 17.8 x 2e-07 mm, 1 faces, 0 solids (baked)
FEATURE [Part::Revolution] Revolve109  label="removeToCreateScrewAndThreadedInsertHole036"
  Angle = 360
  Axis = (0,1,0)
  Base = (0,0,0)
  FaceMakerClass = Part::FaceMakerBullseye
  Placement = pos=(89.5,0,68.5) rot=(0,0,1;0rad)
  Solid = false
  Source = -> Face101
  Symmetric = false
FEATURE [Part::Feature] Face102
  shape: bbox 3.5 x 17.8 x 2e-07 mm, 1 faces, 0 solids (baked)
FEATURE [Part::Revolution] Revolve110  label="removeToCreateScrewAndThreadedInsertHole037"
  Angle = 360
  Axis = (0,1,0)
  Base = (0,0,0)
  FaceMakerClass = Part::FaceMakerBullseye
  Placement = pos=(89.5,0,3.5) rot=(0,0,1;0rad)
  Solid = false
  Source = -> Face102
  Symmetric = false
FEATURE [Part::Feature] Face103
  shape: bbox 3.5 x 17.8 x 2e-07 mm, 1 faces, 0 solids (baked)
FEATURE [Part::Revolution] Revolve111  label="removeToCreateScrewAndThreadedInsertHole038"
  Angle = 360
  Axis = (0,1,0)
  Base = (0,0,0)
  FaceMakerClass = Part::FaceMakerBullseye
  Placement = pos=(109.5,4.7,3.5) rot=(0,0,1;0rad)
  Solid = false
  Source = -> Face103
  Symmetric = false
FEATURE [Part::Feature] Face104
  shape: bbox 3.5 x 17.8 x 2e-07 mm, 1 faces, 0 solids (baked)
FEATURE [Part::Revolution] Revolve112  label="removeToCreateScrewAndThreadedInsertHole039"
  Angle = 360
  Axis = (0,1,0)
  Base = (0,0,0)
  FaceMakerClass = Part::FaceMakerBullseye
  Placement = pos=(109.5,4.7,68.5) rot=(0,0,1;0rad)
  Solid = false
  Source = -> Face104
  Symmetric = false
FEATURE [Part::MultiFuse] Fusion081  label="removeToCreateScrewAndThreadedInsertHole040"
  Shapes = -> [Revolve107,Revolve108,Revolve109,Revolve110,Revolve111,Revolve112]
FEATURE [Part::MultiFuse] Fusion082  label="casePillars002"
  Shapes = -> [Revolve094,Revolve092,Revolve090,Revolve089,Revolve091,Revolve093]
FEATURE [Part::Cut] Cut037  label="casePillars003"
  Base = -> Fusion082
  Tool = -> Fusion081
FEATURE [Sketcher::SketchObject] Sketch051
  FullyConstrained = true
  Placement = pos=(117,19,0) rot=(0.57735,0.57735,0.57735;2.0944rad)
  sketch-geometry (48):
    g0: LineSegment StartX=-49.19 StartY=69.25 StartZ=0 EndX=-49.19 EndY=66.25 EndZ=0
    g1: LineSegment StartX=-49.19 StartY=63.5 StartZ=0 EndX=-49.19 EndY=60.5 EndZ=0
    g2: LineSegment StartX=-49.19 StartY=57.75 StartZ=0 EndX=-49.19 EndY=54.75 EndZ=0
    g3: LineSegment StartX=-49.19 StartY=52 StartZ=0 EndX=-49.19 EndY=49 EndZ=0
    g4: LineSegment StartX=-49.19 StartY=46.25 StartZ=0 EndX=-49.19 EndY=43.25 EndZ=0
    g5: LineSegment StartX=-49.19 StartY=40.5 StartZ=0 EndX=-49.19 EndY=37.5 EndZ=0
    g6: LineSegment StartX=-49.19 StartY=34.5 StartZ=0 EndX=-49.19 EndY=31.5 EndZ=0
    g7: LineSegment StartX=-49.19 StartY=28.75 StartZ=0 EndX=-49.19 EndY=25.75 EndZ=0
    g8: LineSegment StartX=-49.19 StartY=23 StartZ=0 EndX=-49.19 EndY=20 EndZ=0
    g9: LineSegment StartX=-49.19 StartY=17.25 StartZ=0 EndX=-49.19 EndY=14.25 EndZ=0
    g10: LineSegment StartX=-49.19 StartY=11.5 StartZ=0 EndX=-49.19 EndY=8.5 EndZ=0
    g11: LineSegment StartX=-49.19 StartY=5.75 StartZ=0 EndX=-49.19 EndY=2.75 EndZ=0
    g12: ArcOfCircle CenterX=-1.5 CenterY=67.75 CenterZ=0 NormalX=0 NormalY=0 NormalZ=1 AngleXU=0 Radius=1.5 StartAngle=4.71239 EndAngle=7.85398
    g13: ArcOfCircle CenterX=-1.5 CenterY=62 CenterZ=0 NormalX=0 NormalY=0 NormalZ=1 AngleXU=0 Radius=1.5 StartAngle=4.71239 EndAngle=7.85398
    g14: ArcOfCircle CenterX=-1.5 CenterY=56.25 CenterZ=0 NormalX=0 NormalY=0 NormalZ=1 AngleXU=0 Radius=1.5 StartAngle=4.71239 EndAngle=7.85398
    g15: ArcOfCircle CenterX=-11.49 CenterY=50.5 CenterZ=0 NormalX=0 NormalY=0 NormalZ=1 AngleXU=0 Radius=1.5 StartAngle=4.71239 EndAngle=7.85398
    g16: ArcOfCircle CenterX=-16.28 CenterY=44.75 CenterZ=0 NormalX=0 NormalY=0 NormalZ=1 AngleXU=0 Radius=1.5 StartAngle=4.71239 EndAngle=7.85398
    g17: ArcOfCircle CenterX=-18.2337 CenterY=39 CenterZ=0 NormalX=0 NormalY=0 NormalZ=1 AngleXU=0 Radius=1.5 StartAngle=4.71485 EndAngle=7.85398
    g18: ArcOfCircle CenterX=-16.2837 CenterY=27.25 CenterZ=0 NormalX=0 NormalY=0 NormalZ=1 AngleXU=0 Radius=1.5 StartAngle=4.71485 EndAngle=7.85398
    g19: ArcOfCircle CenterX=-18.2337 CenterY=33 CenterZ=0 NormalX=0 NormalY=0 NormalZ=1 AngleXU=0 Radius=1.5 StartAngle=4.71485 EndAngle=7.85398
    g20: ArcOfCircle CenterX=-11.49 CenterY=21.5 CenterZ=0 NormalX=0 NormalY=0 NormalZ=1 AngleXU=0 Radius=1.5 StartAngle=4.71239 EndAngle=7.85398
    g21: ArcOfCircle CenterX=-1.5 CenterY=4.25 CenterZ=0 NormalX=0 NormalY=0 NormalZ=1 AngleXU=0 Radius=1.5 StartAngle=4.71239 EndAngle=7.85398
    g22: ArcOfCircle CenterX=-1.5 CenterY=10 CenterZ=0 NormalX=0 NormalY=0 NormalZ=1 AngleXU=0 Radius=1.5 StartAngle=4.71239 EndAngle=7.85398
    g23: ArcOfCircle CenterX=-1.5 CenterY=15.75 CenterZ=0 NormalX=0 NormalY=0 NormalZ=1 AngleXU=0 Radius=1.5 StartAngle=4.71239 EndAngle=7.85398
    g24: LineSegment StartX=-49.19 StartY=69.25 StartZ=0 EndX=-1.5 EndY=69.25 EndZ=0
    g25: LineSegment StartX=-49.19 StartY=66.25 StartZ=0 EndX=-1.5 EndY=66.25 EndZ=0
    g26: LineSegment StartX=-49.19 StartY=63.5 StartZ=0 EndX=-1.5 EndY=63.5 EndZ=0
    g27: LineSegment StartX=-49.19 StartY=60.5 StartZ=0 EndX=-1.5 EndY=60.5 EndZ=0
    g28: LineSegment StartX=-49.19 StartY=57.75 StartZ=0 EndX=-1.5 EndY=57.75 EndZ=0
    g29: LineSegment StartX=-49.19 StartY=54.75 StartZ=0 EndX=-1.5 EndY=54.75 EndZ=0
    g30: LineSegment StartX=-49.19 StartY=52 StartZ=0 EndX=-11.49 EndY=52 EndZ=0
    g31: LineSegment StartX=-49.19 StartY=49 StartZ=0 EndX=-11.49 EndY=49 EndZ=0
    g32: LineSegment StartX=-49.19 StartY=46.25 StartZ=0 EndX=-16.28 EndY=46.25 EndZ=0
    g33: LineSegment StartX=-49.19 StartY=43.25 StartZ=0 EndX=-16.28 EndY=43.25 EndZ=0
    g34: LineSegment StartX=-49.19 StartY=40.5 StartZ=0 EndX=-18.2337 EndY=40.5 EndZ=0
    g35: LineSegment StartX=-49.19 StartY=37.5 StartZ=0 EndX=-18.23 EndY=37.5 EndZ=0
    g36: LineSegment StartX=-49.19 StartY=34.5 StartZ=0 EndX=-18.2337 EndY=34.5 EndZ=0
    g37: LineSegment StartX=-49.19 StartY=31.5 StartZ=0 EndX=-18.23 EndY=31.5 EndZ=0
    g38: LineSegment StartX=-49.19 StartY=28.75 StartZ=0 EndX=-16.2837 EndY=28.75 EndZ=0
    g39: LineSegment StartX=-49.19 StartY=25.75 StartZ=0 EndX=-16.28 EndY=25.75 EndZ=0
    g40: LineSegment StartX=-49.19 StartY=23 StartZ=0 EndX=-11.49 EndY=23 EndZ=0
    g41: LineSegment StartX=-49.19 StartY=20 StartZ=0 EndX=-11.49 EndY=20 EndZ=0
    g42: LineSegment StartX=-49.19 StartY=17.25 StartZ=0 EndX=-1.5 EndY=17.25 EndZ=0
    g43: LineSegment StartX=-49.19 StartY=14.25 StartZ=0 EndX=-1.5 EndY=14.25 EndZ=0
    g44: LineSegment StartX=-49.19 StartY=11.5 StartZ=0 EndX=-1.5 EndY=11.5 EndZ=0
    g45: LineSegment StartX=-49.19 StartY=8.5 StartZ=0 EndX=-1.5 EndY=8.5 EndZ=0
    g46: LineSegment StartX=-49.19 StartY=5.75 StartZ=0 EndX=-1.5 EndY=5.75 EndZ=0
    g47: LineSegment StartX=-49.19 StartY=2.75 StartZ=0 EndX=-1.5 EndY=2.75 EndZ=0
  constraints (120):
    c: Vertical(g0)
    c: Distance(g0) = 3
    c: Block(g0)
    c: Vertical(g1)
    c: Distance(g1) = 3
    c: Vertical(g2)
    c: Equal(g0,g2) = 3
    c: Block(g2)
    c: Vertical(g3)
    c: Equal(g1,g3) = 3
    c: Vertical(g4)
    c: Equal(g0,g4) = 3
    c: Block(g4)
    c: Vertical(g5)
    c: Equal(g1,g5) = 3
    c: Vertical(g6)
    c: Equal(g0,g6) = 3
    c: Block(g6)
    c: Vertical(g7)
    c: Equal(g1,g7) = 3
    c: Vertical(g8)
    c: Equal(g0,g8) = 3
    c: Block(g8)
    c: Vertical(g9)
    c: Equal(g1,g9) = 3
    c: Vertical(g10)
    c: Equal(g0,g10) = 3
    c: Block(g10)
    c: Vertical(g11)
    c: Equal(g1,g11) = 3
    c: Block(g12)
    c: Block(g13)
    c: Block(g14)
    c: Block(g15)
    c: Block(g16)
    c: Block(g17)
    c: Block(g18)
    c: Block(g19)
    c: Block(g20)
    c: Block(g21)
    c: Block(g22)
    c: Block(g23)
    c: Block(g11)
    c: Block(g9)
    c: Block(g7)
    c: Block(g5)
    c: Block(g3)
    c: Block(g1)
    c: Coincident(g24,g0)
    c: Coincident(g24,g12)
    c: Horizontal(g24)
    c: Coincident(g25,g0)
    c: Coincident(g25,g12)
    c: Horizontal(g25)
    c: Coincident(g26,g1)
    c: Coincident(g26,g13)
    c: Horizontal(g26)
    c: Coincident(g27,g1)
    c: Coincident(g27,g13)
    c: Horizontal(g27)
    c: Coincident(g28,g2)
    c: Coincident(g28,g14)
    c: Horizontal(g28)
    c: Coincident(g29,g2)
    c: Coincident(g29,g14)
    c: Horizontal(g29)
    c: Coincident(g30,g3)
    c: Coincident(g30,g15)
    c: Horizontal(g30)
    c: Coincident(g31,g3)
    c: Coincident(g31,g15)
    c: Horizontal(g31)
    c: Coincident(g32,g4)
    c: Coincident(g32,g16)
    c: Horizontal(g32)
    c: Coincident(g33,g4)
    c: Coincident(g33,g16)
    c: Horizontal(g33)
    c: Coincident(g34,g5)
    c: Coincident(g34,g17)
    c: Horizontal(g34)
    c: Coincident(g35,g5)
    c: Coincident(g35,g17)
    c: Horizontal(g35)
    c: Coincident(g36,g6)
    c: Coincident(g36,g19)
    c: Horizontal(g36)
    c: Coincident(g37,g6)
    c: Coincident(g37,g19)
    c: Horizontal(g37)
    c: Coincident(g38,g7)
    c: Coincident(g38,g18)
    c: Horizontal(g38)
    c: Coincident(g39,g7)
    c: Coincident(g39,g18)
    c: Horizontal(g39)
    c: Coincident(g40,g8)
    c: Coincident(g40,g20)
    c: Horizontal(g40)
    c: Coincident(g41,g8)
    c: Coincident(g41,g20)
    c: Horizontal(g41)
    c: Coincident(g42,g9)
    c: Coincident(g42,g23)
    c: Horizontal(g42)
    c: Coincident(g43,g9)
    c: Coincident(g43,g23)
    c: Horizontal(g43)
    c: Coincident(g44,g10)
    c: Coincident(g44,g22)
    c: Horizontal(g44)
    c: Coincident(g45,g10)
    c: Coincident(g45,g22)
    c: Horizontal(g45)
    c: Coincident(g46,g11)
    c: Coincident(g46,g21)
    c: Horizontal(g46)
    c: Coincident(g47,g11)
    c: Coincident(g47,g21)
    c: Horizontal(g47)
FEATURE [Part::Extrusion] Extrude042
  Base = -> Sketch051
  Dir = (1,-2e-16,2e-16)
  DirMode = 2
  FaceMakerClass = Part::FaceMakerBullseye
  LengthFwd = 19
  LengthRev = 0
  Placement = pos=(-19,0,0) rot=(0,0,1;0rad)
  Solid = true
  Symmetric = false
FEATURE [Part::Fillet] Fillet035  label="removeToCreateVentalationHoles"
  Base = -> Extrude042
  Edges = <same value as first occurrence — deduplicated (x6 in doc)>
  Placement = pos=(7,0,0) rot=(0,0,1;0rad)
FEATURE [Part::Cut] Cut038  label="top017"
  Base = -> Cut033
  Tool = -> Fillet035
FEATURE [Sketcher::SketchObject] Sketch052  label="bottomSketch001"
  FullyConstrained = true
  sketch-geometry (45):
    g0: LineSegment StartX=6.29999 StartY=8 StartZ=0 EndX=3.29999 EndY=8 EndZ=0
    g1: LineSegment StartX=3.29999 StartY=8 StartZ=0 EndX=3.29999 EndY=-6.03275e-07 EndZ=0
    g2: ArcOfCircle CenterX=8.29999 CenterY=5 CenterZ=0 NormalX=0 NormalY=0 NormalZ=1 AngleXU=0 Radius=2 StartAngle=3.14159 EndAngle=4.71239
    g3: LineSegment StartX=6.29999 StartY=8 StartZ=0 EndX=6.29999 EndY=5 EndZ=0
    g4: ArcOfCircle CenterX=105 CenterY=19 CenterZ=0 NormalX=0 NormalY=0 NormalZ=1 AngleXU=0 Radius=12.7 StartAngle=4.71239 EndAngle=5.94289
    g5-g11: Circle x7 (B-spline internal-alignment scaffolding for g12; pole/knot coordinates omitted)
    g12: BSplineCurve PolesCount=7 KnotsCount=5 Degree=3 IsPeriodic=0
    g13-g17: GeomPoint x5 (B-spline internal-alignment scaffolding for g12; pole/knot coordinates omitted)
    g18: ArcOfCircle CenterX=105 CenterY=19 CenterZ=0 NormalX=0 NormalY=0 NormalZ=1 AngleXU=0 Radius=15.7 StartAngle=5.81226 EndAngle=6.28319
    g19: BSplineCurve PolesCount=5 KnotsCount=3 Degree=3 IsPeriodic=0
    g20: LineSegment StartX=8.29999 StartY=3 StartZ=0 EndX=101.7 EndY=3 EndZ=0
    g21: LineSegment StartX=3.29999 StartY=-6.03275e-07 StartZ=0 EndX=105 EndY=-6.03275e-07 EndZ=0
    g22: LineSegment StartX=120.974 StartY=8.71251 StartZ=0 EndX=122.332 EndY=7.83778 EndZ=0
    g23: LineSegment StartX=105 StartY=-6.03274e-07 StartZ=0 EndX=113 EndY=-6.03274e-07 EndZ=0
    g24: ArcOfCircle CenterX=105 CenterY=19 CenterZ=0 NormalX=0 NormalY=0 NormalZ=1 AngleXU=0 Radius=20.6155 StartAngle=5.11091 EndAngle=5.71103
    g25: ArcOfCircle CenterX=117.7 CenterY=19 CenterZ=0 NormalX=0 NormalY=0 NormalZ=1 AngleXU=0 Radius=3 StartAngle=1.2e-15 EndAngle=2.10468
    g26: Circle CenterX=116.345 CenterY=16.3232 CenterZ=0 NormalX=0 NormalY=0 NormalZ=1 AngleXU=0 Radius=1
    g27: Circle CenterX=117.24 CenterY=15.7584 CenterZ=0 NormalX=0 NormalY=0 NormalZ=1 AngleXU=0 Radius=1
    g28: Circle CenterX=116.972 CenterY=14.7612 CenterZ=0 NormalX=0 NormalY=0 NormalZ=1 AngleXU=0 Radius=1
    g29: BSplineCurve PolesCount=3 KnotsCount=2 Degree=2 IsPeriodic=0
    g30: GeomPoint X=116.345 Y=16.3232 Z=0
    g31: GeomPoint X=116.972 Y=14.7612 Z=0
    g32: Circle CenterX=115.828 CenterY=17.157 CenterZ=0 NormalX=0 NormalY=0 NormalZ=1 AngleXU=0 Radius=1
    g33: Circle CenterX=115.841 CenterY=16.639 CenterZ=0 NormalX=0 NormalY=0 NormalZ=1 AngleXU=0 Radius=1
    g34: Circle CenterX=116.345 CenterY=16.3232 CenterZ=0 NormalX=0 NormalY=0 NormalZ=1 AngleXU=0 Radius=1
    g35: BSplineCurve PolesCount=3 KnotsCount=2 Degree=2 IsPeriodic=0
    g36: GeomPoint X=115.828 Y=17.157 Z=0
    g37: GeomPoint X=116.345 Y=16.3232 Z=0
    g38: LineSegment StartX=115.828 StartY=17.157 StartZ=0 EndX=115.828 EndY=20.8307 EndZ=0
    g39: Circle CenterX=115.828 CenterY=20.8307 CenterZ=0 NormalX=0 NormalY=0 NormalZ=1 AngleXU=0 Radius=1
    g40: Circle CenterX=115.831 CenterY=21.3396 CenterZ=0 NormalX=0 NormalY=0 NormalZ=1 AngleXU=0 Radius=1
    g41: Circle CenterX=116.173 CenterY=21.5825 CenterZ=0 NormalX=0 NormalY=0 NormalZ=1 AngleXU=0 Radius=1
    g42: BSplineCurve PolesCount=3 KnotsCount=2 Degree=2 IsPeriodic=0
    g43: GeomPoint X=115.828 Y=20.8307 Z=0
    g44: GeomPoint X=116.173 Y=21.5825 Z=0
  constraints (70):
    c: Horizontal(g0)
    c: Distance(g0) = 3
    c: Coincident(g1,g0)
    c: Vertical(g1)
    c: Block(g2)
    c: Block(g0)
    c: Coincident(g3,g0)
    c: Coincident(g3,g2)
    c: Vertical(g3)
    c: Block(g1)
    c: Block(g4)
    c: Coincident(g19,g4)
    c: Block(g19)
    c: Equal(g5, g6-g11) x6
    c: InternalAlignment(g5-g11 -> g12) x7
    c: InternalAlignment(g13-g17 -> g12) x5
    c: Block(g12)
    c: Coincident(g18,g12)
    c: Block(g18)
    c: Coincident(g20,g2)
    c: Coincident(g20,g19)
    c: Horizontal(g20)
    c: Distance(g20) = 93.4
    c: Coincident(g21,g1)
    c: Horizontal(g21)
    c: Distance(g21) = 101.7
    c: Horizontal(g23)
    c: Distance(g23) = 8
    c: Coincident(g24,g23)
    c: Block(g23)
    c: Coincident(g22,g24)
    c: Block(g24)
    c: Block(g22)
    c: Distance(g22) = 1.61553
    c: Coincident(g25,g18)
    c: Block(g25)
    c: Weight(g26) = 1
    c: Equal(g26,g27)
    c: Equal(g26,g28)
    c: Coincident(g29,g4)
    c: InternalAlignment(g26,g29)
    c: InternalAlignment(g27,g29)
    c: InternalAlignment(g28,g29)
    c: InternalAlignment(g30,g29)
    c: InternalAlignment(g31,g29)
    c: Block(g29)
    c: Weight(g32) = 1
    c: Equal(g32,g33)
    c: Equal(g32,g34)
    c: Coincident(g35,g29)
    c: InternalAlignment(g32,g35)
    c: InternalAlignment(g33,g35)
    c: InternalAlignment(g34,g35)
    c: InternalAlignment(g36,g35)
    c: InternalAlignment(g37,g35)
    c: Block(g35)
    c: Coincident(g38,g35)
    c: Vertical(g38)
    c: Block(g38)
    c: Coincident(g42,g38)
    c: Weight(g39) = 1
    c: Equal(g39,g40)
    c: Equal(g39,g41)
    c: Coincident(g42,g25)
    c: InternalAlignment(g39,g42)
    c: InternalAlignment(g40,g42)
    c: InternalAlignment(g41,g42)
    c: InternalAlignment(g43,g42)
    c: InternalAlignment(g44,g42)
    c: Block(g42)
FEATURE [Part::Extrusion] Extrude043  label="bottom010"
  Base = -> Sketch052
  Dir = (0,0,1)
  DirMode = 2
  FaceMakerClass = Part::FaceMakerBullseye
  LengthFwd = 71.4
  LengthRev = 0
  Placement = pos=(0,0,0.3) rot=(0,0,1;0rad)
  Solid = true
  Symmetric = false
FEATURE [Sketcher::SketchObject] Sketch053  label="topSketch013"
  FullyConstrained = true
  sketch-geometry (22):
    g0: LineSegment StartX=5.21097e-06 StartY=3 StartZ=0 EndX=5.21097e-06 EndY=19 EndZ=0
    g1: ArcOfCircle CenterX=19 CenterY=19 CenterZ=0 NormalX=0 NormalY=0 NormalZ=1 AngleXU=0 Radius=19 StartAngle=1.5708 EndAngle=3.14159
    g2: ArcOfCircle CenterX=19 CenterY=19 CenterZ=0 NormalX=0 NormalY=0 NormalZ=1 AngleXU=0 Radius=16 StartAngle=1.5708 EndAngle=3.14159
    g3: LineSegment StartX=114 StartY=35 StartZ=0 EndX=19 EndY=35 EndZ=0
    g4: LineSegment StartX=5.21097e-06 StartY=3 StartZ=0 EndX=5.21097e-06 EndY=0 EndZ=0
    g5: LineSegment StartX=3 StartY=0 StartZ=0 EndX=5.21097e-06 EndY=0 EndZ=0
    g6: LineSegment StartX=3 StartY=19 StartZ=0 EndX=3 EndY=0 EndZ=0
    g7: LineSegment StartX=19 StartY=38 StartZ=0 EndX=124 EndY=38 EndZ=0
    g8: Circle CenterX=119 CenterY=35 CenterZ=0 NormalX=0 NormalY=0 NormalZ=1 AngleXU=0 Radius=1
    g9: Circle CenterX=121 CenterY=35 CenterZ=0 NormalX=0 NormalY=0 NormalZ=1 AngleXU=0 Radius=1
    g10: Circle CenterX=121 CenterY=33 CenterZ=0 NormalX=0 NormalY=0 NormalZ=1 AngleXU=0 Radius=1
    g11: BSplineCurve PolesCount=3 KnotsCount=2 Degree=2 IsPeriodic=0
    g12: GeomPoint X=119 Y=35 Z=0
    g13: GeomPoint X=121 Y=33 Z=0
    g14: LineSegment StartX=119 StartY=35 StartZ=0 EndX=114 EndY=35 EndZ=0
    g15: ArcOfCircle CenterX=105 CenterY=19 CenterZ=0 NormalX=0 NormalY=0 NormalZ=1 AngleXU=0 Radius=16 StartAngle=5.60905 EndAngle=6.28319
    g16: LineSegment StartX=121 StartY=33 StartZ=0 EndX=121 EndY=19 EndZ=0
    g17: LineSegment StartX=117.5 StartY=9.01251 StartZ=0 EndX=121.163 EndY=9.0125 EndZ=0
    g18: ArcOfCircle CenterX=105 CenterY=19 CenterZ=0 NormalX=0 NormalY=0 NormalZ=1 AngleXU=0 Radius=20.6155 StartAngle=5.7297 EndAngle=6.28319
    g19: LineSegment StartX=121.163 StartY=9.0125 StartZ=0 EndX=122.538 EndY=8.16329 EndZ=0
    g20: LineSegment StartX=124 StartY=38 StartZ=0 EndX=125.616 EndY=38 EndZ=0
    g21: LineSegment StartX=125.616 StartY=19 StartZ=0 EndX=125.616 EndY=38 EndZ=0
  constraints (50):
    c: Vertical(g0)
    c: Block(g0)
    c: Coincident(g1,g0)
    c: Block(g1)
    c: Coincident(g2,g1)
    c: Block(g2)
    c: Coincident(g3,g2)
    c: Horizontal(g3)
    c: Tangent(g3,g2)
    c: Coincident(g4,g0)
    c: Distance(g4) = 3
    c: Vertical(g4)
    c: Coincident(g5,g4)
    c: Horizontal(g5)
    c: Coincident(g6,g2)
    c: Coincident(g6,g5)
    c: Vertical(g6)
    c: Horizontal(g7)
    c: Distance(g7) = 105
    c: Coincident(g7,g1)
    c: Block(g3)
    c: Weight(g8) = 1
    c: Equal(g8,g9)
    c: Equal(g8,g10)
    c: InternalAlignment(g8,g11)
    c: InternalAlignment(g9,g11)
    c: InternalAlignment(g10,g11)
    c: InternalAlignment(g12,g11)
    c: InternalAlignment(g13,g11)
    c: Block(g11)
    c: Coincident(g14,g11)
    c: Coincident(g14,g3)
    c: Horizontal(g14)
    c: Block(g15)
    c: Coincident(g16,g11)
    c: Coincident(g16,g15)
    c: Vertical(g16)
    c: Distance(g16) = 14
    c: Coincident(g17,g15)
    c: Block(g18)
    c: Coincident(g19,g18)
    c: Coincident(g20,g7)
    c: Horizontal(g20)
    c: Vertical(g21)
    c: Coincident(g20,g21)
    c: Block(g20)
    c: Block(g21)
    c: Block(g19)
    c: Block(g17)
    c: Distance(g20) = 1.61553
FEATURE [Part::Extrusion] Extrude044
  Base = -> Sketch053
  Dir = (0,0,1)
  DirMode = 2
  FaceMakerClass = Part::FaceMakerBullseye
  LengthFwd = 72
  LengthRev = 0
  Solid = true
  Symmetric = false
FEATURE [Part::Fillet] Fillet036  label="top018"
  Base = -> Extrude044
  Edges = 1 edges r=2: [Edge41]
FEATURE [Sketcher::SketchObject] Sketch054
  FullyConstrained = false
  Placement = pos=(0,0,0) rot=(1,0,0;1.5708rad)
  sketch-geometry (24):
    g0: ArcOfCircle CenterX=-4 CenterY=-10.5 CenterZ=0 NormalX=0 NormalY=0 NormalZ=1 AngleXU=0 Radius=1.5 StartAngle=6e-16 EndAngle=3.14159
    g1: ArcOfCircle CenterX=-34.2 CenterY=-10.5 CenterZ=0 NormalX=0 NormalY=0 NormalZ=1 AngleXU=0 Radius=1.5 StartAngle=0 EndAngle=3.14159
    g2: ArcOfCircle CenterX=-34.2 CenterY=-27.7 CenterZ=0 NormalX=0 NormalY=0 NormalZ=1 AngleXU=0 Radius=1.5 StartAngle=3.14159 EndAngle=6.28319
    g3: ArcOfCircle CenterX=-4 CenterY=-27.7 CenterZ=0 NormalX=0 NormalY=0 NormalZ=1 AngleXU=0 Radius=1.5 StartAngle=3.1416 EndAngle=6.28319
    g4: ArcOfCircle CenterX=-10 CenterY=-4.3 CenterZ=0 NormalX=0 NormalY=0 NormalZ=1 AngleXU=0 Radius=1.5 StartAngle=2e-16 EndAngle=3.14159
    g5: ArcOfCircle CenterX=-16.1 CenterY=-1.8 CenterZ=0 NormalX=0 NormalY=0 NormalZ=1 AngleXU=0 Radius=1.5 StartAngle=5e-16 EndAngle=3.14159
    g6: ArcOfCircle CenterX=-22.1 CenterY=-1.8 CenterZ=0 NormalX=0 NormalY=0 NormalZ=1 AngleXU=0 Radius=1.5 StartAngle=5e-16 EndAngle=3.14159
    g7: ArcOfCircle CenterX=-28.2 CenterY=-4.3 CenterZ=0 NormalX=0 NormalY=0 NormalZ=1 AngleXU=0 Radius=1.5 StartAngle=2e-16 EndAngle=3.14159
    g8: ArcOfCircle CenterX=-10 CenterY=-33.9 CenterZ=0 NormalX=0 NormalY=0 NormalZ=1 AngleXU=0 Radius=1.5 StartAngle=3.14159 EndAngle=6.28319
    g9: ArcOfCircle CenterX=-16.1 CenterY=-36.4 CenterZ=0 NormalX=0 NormalY=0 NormalZ=1 AngleXU=0 Radius=1.5 StartAngle=3.14159 EndAngle=6.28319
    g10: ArcOfCircle CenterX=-22.1 CenterY=-36.4 CenterZ=0 NormalX=0 NormalY=0 NormalZ=1 AngleXU=0 Radius=1.5 StartAngle=3.14159 EndAngle=6.28319
    g11: ArcOfCircle CenterX=-28.2 CenterY=-33.9 CenterZ=0 NormalX=0 NormalY=0 NormalZ=1 AngleXU=0 Radius=1.5 StartAngle=3.14159 EndAngle=6.28319
    g12: LineSegment StartX=-35.7 StartY=-10.5 StartZ=0 EndX=-35.7 EndY=-27.7 EndZ=0
    g13: LineSegment StartX=-32.7 StartY=-10.5 StartZ=0 EndX=-32.7 EndY=-27.7 EndZ=0
    g14: LineSegment StartX=-29.7 StartY=-33.9 StartZ=0 EndX=-29.7 EndY=-4.3 EndZ=0
    g15: LineSegment StartX=-26.7 StartY=-33.9 StartZ=0 EndX=-26.7 EndY=-4.3 EndZ=0
    g16: LineSegment StartX=-2.5 StartY=-10.5 StartZ=0 EndX=-2.5 EndY=-27.7 EndZ=0
    g17: LineSegment StartX=-8.5 StartY=-4.3 StartZ=0 EndX=-8.5 EndY=-33.9 EndZ=0
    g18: LineSegment StartX=-5.5 StartY=-10.5 StartZ=0 EndX=-5.5 EndY=-27.7 EndZ=0
    g19: LineSegment StartX=-11.5 StartY=-4.3 StartZ=0 EndX=-11.5 EndY=-33.9 EndZ=0
    g20: LineSegment StartX=-14.6 StartY=-1.8 StartZ=0 EndX=-14.6 EndY=-36.4 EndZ=0
    g21: LineSegment StartX=-17.6 StartY=-1.8 StartZ=0 EndX=-17.6 EndY=-36.4 EndZ=0
    g22: LineSegment StartX=-20.6 StartY=-36.4 StartZ=0 EndX=-20.6 EndY=-1.8 EndZ=0
    g23: LineSegment StartX=-23.6 StartY=-1.8 StartZ=0 EndX=-23.6 EndY=-36.4 EndZ=0
  constraints (48):
    c: Block(g0)
    c: Block(g1)
    c: Block(g2)
    c: Block(g3)
    c: Block(g4)
    c: Block(g5)
    c: Block(g6)
    c: Block(g7)
    c: Block(g8)
    c: Block(g9)
    c: Block(g10)
    c: Block(g11)
    c: Coincident(g12,g1)
    c: Coincident(g12,g2)
    c: Vertical(g12)
    c: Coincident(g13,g1)
    c: Coincident(g13,g2)
    c: Vertical(g13)
    c: Coincident(g14,g11)
    c: Coincident(g14,g7)
    c: Vertical(g14)
    c: Coincident(g15,g11)
    c: Coincident(g15,g7)
    c: Vertical(g15)
    c: Coincident(g16,g0)
    c: Coincident(g16,g3)
    c: Vertical(g16)
    c: Coincident(g17,g4)
    c: Coincident(g17,g8)
    c: Vertical(g17)
    c: Coincident(g18,g0)
    c: Coincident(g18,g3)
    c: Vertical(g18)
    c: Coincident(g19,g4)
    c: Coincident(g19,g8)
    c: Vertical(g19)
    c: Coincident(g20,g5)
    c: Coincident(g20,g9)
    c: Vertical(g20)
    c: Coincident(g21,g5)
    c: Coincident(g21,g9)
    c: Vertical(g21)
    c: Coincident(g22,g10)
    c: Coincident(g22,g6)
    c: Vertical(g22)
    c: Coincident(g23,g6)
    c: Coincident(g23,g10)
    c: Vertical(g23)
FEATURE [Part::Extrusion] Extrude045  label="removeToCreateFanGrillHoles003"
  Base = -> Sketch054
  Dir = (0,-1,6e-16)
  DirMode = 2
  FaceMakerClass = Part::FaceMakerBullseye
  LengthFwd = 10
  LengthRev = 0
  Placement = pos=(65.4,44,54.82) rot=(0,0,1;0rad)
  Solid = true
  Symmetric = false
FEATURE [Part::Feature] Face105 .. Face108  x4 (patterned run collapsed; names and placements below)
  shape: bbox 3.5 x 17.8 x 2e-07 mm, 1 faces, 0 solids (baked)
FEATURE [Part::Revolution] Revolve113  label="removeToCreateScrewAndThreadedInsertHole041"
  Angle = 360
  Axis = (0,1,0)
  Base = (0,0,0)
  FaceMakerClass = Part::FaceMakerBullseye
  Placement = pos=(62.3,30.3,19.7) rot=(0,0,1;0rad)
  Solid = false
  Source = -> Face105
  Symmetric = false
FEATURE [Part::Revolution] Revolve114  label="removeToCreateScrewAndThreadedInsertHole042"
  Angle = 360
  Axis = (0,1,0)
  Base = (0,0,0)
  FaceMakerClass = Part::FaceMakerBullseye
  Placement = pos=(62.3,30.3,51.7) rot=(0,0,1;0rad)
  Solid = false
  Source = -> Face106
  Symmetric = false
FEATURE [Part::Revolution] Revolve115  label="removeToCreateScrewAndThreadedInsertHole043"
  Angle = 360
  Axis = (0,1,0)
  Base = (0,0,0)
  FaceMakerClass = Part::FaceMakerBullseye
  Placement = pos=(30.3,30.3,19.7) rot=(0,0,1;0rad)
  Solid = false
  Source = -> Face107
  Symmetric = false
FEATURE [Part::Revolution] Revolve116  label="removeToCreateScrewAndThreadedInsertHole044"
  Angle = 360
  Axis = (0,1,0)
  Base = (0,0,0)
  FaceMakerClass = Part::FaceMakerBullseye
  Placement = pos=(30.3,30.3,51.7) rot=(0,0,1;0rad)
  Solid = false
  Source = -> Face108
  Symmetric = false
FEATURE [Part::MultiFuse] Fusion083  label="createThreadedInsertHolesForFan004"
  Shapes = -> [Revolve113,Revolve114,Revolve115,Revolve116]
FEATURE [Part::Box] Box024  label="removeToCreteHoleForPlugHousing026"
  AttacherType = Attacher::AttachEngine3D
  Height = 28.6
  Length = 10
  Placement = pos=(-2,0,21.7) rot=(0,0,1;0rad)
  Width = 19
FEATURE [Part::Cylinder] Cylinder038  label="removeToCreteHoleForPlugHousing027"
  Angle = 360
  AttacherType = Attacher::AttachEngine3D
  Height = 20
  Placement = pos=(-2,19,36) rot=(0,1,0;1.5708rad)
  Radius = 14.3
FEATURE [Part::MultiFuse] Fusion084  label="removeToCreteHoleForPlugHousing028"
  Shapes = -> [Box024,Cylinder038]
FEATURE [Part::Cylinder] Cylinder039
  Angle = 360
  AttacherType = Attacher::AttachEngine3D
  Height = 20
  Placement = pos=(0,0,36.15) rot=(0,0,1;0rad)
  Radius = 14.3
FEATURE [Part::Cylinder] Cylinder040
  Angle = 360
  AttacherType = Attacher::AttachEngine3D
  Height = 10
  Placement = pos=(0,0,36.15) rot=(0,0,1;0rad)
  Radius = 4
FEATURE [Part::Box] Box025  label="removeToCreteHoleForPlugHousing030"
  AttacherType = Attacher::AttachEngine3D
  Height = 28.6
  Length = 20
  Placement = pos=(106.15,0,21.7) rot=(0,0,1;0rad)
  Width = 19
FEATURE [Part::MultiFuse] Fusion086  label="removeToCreteHoleForPlugHousing031"
  Placement = pos=(70,19,36) rot=(0,1,0;1.5708rad)
  Shapes = -> [Cylinder039,Cylinder040]
FEATURE [Part::MultiFuse] Fusion085  label="removeToCreteHoleForPlugHousing029"
  Shapes = -> [Box025,Fusion086]
FEATURE [Sketcher::SketchObject] Sketch055
  FullyConstrained = true
  Placement = pos=(117,19,0) rot=(0.57735,0.57735,0.57735;2.0944rad)
  sketch-geometry (48):
    g0: LineSegment StartX=-49.19 StartY=69.25 StartZ=0 EndX=-49.19 EndY=66.25 EndZ=0
    g1: LineSegment StartX=-49.19 StartY=63.5 StartZ=0 EndX=-49.19 EndY=60.5 EndZ=0
    g2: LineSegment StartX=-49.19 StartY=57.75 StartZ=0 EndX=-49.19 EndY=54.75 EndZ=0
    g3: LineSegment StartX=-49.19 StartY=52 StartZ=0 EndX=-49.19 EndY=49 EndZ=0
    g4: LineSegment StartX=-49.19 StartY=46.25 StartZ=0 EndX=-49.19 EndY=43.25 EndZ=0
    g5: LineSegment StartX=-49.19 StartY=40.5 StartZ=0 EndX=-49.19 EndY=37.5 EndZ=0
    g6: LineSegment StartX=-49.19 StartY=34.5 StartZ=0 EndX=-49.19 EndY=31.5 EndZ=0
    g7: LineSegment StartX=-49.19 StartY=28.75 StartZ=0 EndX=-49.19 EndY=25.75 EndZ=0
    g8: LineSegment StartX=-49.19 StartY=23 StartZ=0 EndX=-49.19 EndY=20 EndZ=0
    g9: LineSegment StartX=-49.19 StartY=17.25 StartZ=0 EndX=-49.19 EndY=14.25 EndZ=0
    g10: LineSegment StartX=-49.19 StartY=11.5 StartZ=0 EndX=-49.19 EndY=8.5 EndZ=0
    g11: LineSegment StartX=-49.19 StartY=5.75 StartZ=0 EndX=-49.19 EndY=2.75 EndZ=0
    g12: ArcOfCircle CenterX=-1.5 CenterY=67.75 CenterZ=0 NormalX=0 NormalY=0 NormalZ=1 AngleXU=0 Radius=1.5 StartAngle=4.71239 EndAngle=7.85398
    g13: ArcOfCircle CenterX=-1.5 CenterY=62 CenterZ=0 NormalX=0 NormalY=0 NormalZ=1 AngleXU=0 Radius=1.5 StartAngle=4.71239 EndAngle=7.85398
    g14: ArcOfCircle CenterX=-1.5 CenterY=56.25 CenterZ=0 NormalX=0 NormalY=0 NormalZ=1 AngleXU=0 Radius=1.5 StartAngle=4.71239 EndAngle=7.85398
    g15: ArcOfCircle CenterX=-11.49 CenterY=50.5 CenterZ=0 NormalX=0 NormalY=0 NormalZ=1 AngleXU=0 Radius=1.5 StartAngle=4.71239 EndAngle=7.85398
    g16: ArcOfCircle CenterX=-16.28 CenterY=44.75 CenterZ=0 NormalX=0 NormalY=0 NormalZ=1 AngleXU=0 Radius=1.5 StartAngle=4.71239 EndAngle=7.85398
    g17: ArcOfCircle CenterX=-18.2337 CenterY=39 CenterZ=0 NormalX=0 NormalY=0 NormalZ=1 AngleXU=0 Radius=1.5 StartAngle=4.71485 EndAngle=7.85398
    g18: ArcOfCircle CenterX=-16.2837 CenterY=27.25 CenterZ=0 NormalX=0 NormalY=0 NormalZ=1 AngleXU=0 Radius=1.5 StartAngle=4.71485 EndAngle=7.85398
    g19: ArcOfCircle CenterX=-18.2337 CenterY=33 CenterZ=0 NormalX=0 NormalY=0 NormalZ=1 AngleXU=0 Radius=1.5 StartAngle=4.71485 EndAngle=7.85398
    g20: ArcOfCircle CenterX=-11.49 CenterY=21.5 CenterZ=0 NormalX=0 NormalY=0 NormalZ=1 AngleXU=0 Radius=1.5 StartAngle=4.71239 EndAngle=7.85398
    g21: ArcOfCircle CenterX=-1.5 CenterY=4.25 CenterZ=0 NormalX=0 NormalY=0 NormalZ=1 AngleXU=0 Radius=1.5 StartAngle=4.71239 EndAngle=7.85398
    g22: ArcOfCircle CenterX=-1.5 CenterY=10 CenterZ=0 NormalX=0 NormalY=0 NormalZ=1 AngleXU=0 Radius=1.5 StartAngle=4.71239 EndAngle=7.85398
    g23: ArcOfCircle CenterX=-1.5 CenterY=15.75 CenterZ=0 NormalX=0 NormalY=0 NormalZ=1 AngleXU=0 Radius=1.5 StartAngle=4.71239 EndAngle=7.85398
    g24: LineSegment StartX=-49.19 StartY=69.25 StartZ=0 EndX=-1.5 EndY=69.25 EndZ=0
    g25: LineSegment StartX=-49.19 StartY=66.25 StartZ=0 EndX=-1.5 EndY=66.25 EndZ=0
    g26: LineSegment StartX=-49.19 StartY=63.5 StartZ=0 EndX=-1.5 EndY=63.5 EndZ=0
    g27: LineSegment StartX=-49.19 StartY=60.5 StartZ=0 EndX=-1.5 EndY=60.5 EndZ=0
    g28: LineSegment StartX=-49.19 StartY=57.75 StartZ=0 EndX=-1.5 EndY=57.75 EndZ=0
    g29: LineSegment StartX=-49.19 StartY=54.75 StartZ=0 EndX=-1.5 EndY=54.75 EndZ=0
    g30: LineSegment StartX=-49.19 StartY=52 StartZ=0 EndX=-11.49 EndY=52 EndZ=0
    g31: LineSegment StartX=-49.19 StartY=49 StartZ=0 EndX=-11.49 EndY=49 EndZ=0
    g32: LineSegment StartX=-49.19 StartY=46.25 StartZ=0 EndX=-16.28 EndY=46.25 EndZ=0
    g33: LineSegment StartX=-49.19 StartY=43.25 StartZ=0 EndX=-16.28 EndY=43.25 EndZ=0
    g34: LineSegment StartX=-49.19 StartY=40.5 StartZ=0 EndX=-18.2337 EndY=40.5 EndZ=0
    g35: LineSegment StartX=-49.19 StartY=37.5 StartZ=0 EndX=-18.23 EndY=37.5 EndZ=0
    g36: LineSegment StartX=-49.19 StartY=34.5 StartZ=0 EndX=-18.2337 EndY=34.5 EndZ=0
    g37: LineSegment StartX=-49.19 StartY=31.5 StartZ=0 EndX=-18.23 EndY=31.5 EndZ=0
    g38: LineSegment StartX=-49.19 StartY=28.75 StartZ=0 EndX=-16.2837 EndY=28.75 EndZ=0
    g39: LineSegment StartX=-49.19 StartY=25.75 StartZ=0 EndX=-16.28 EndY=25.75 EndZ=0
    g40: LineSegment StartX=-49.19 StartY=23 StartZ=0 EndX=-11.49 EndY=23 EndZ=0
    g41: LineSegment StartX=-49.19 StartY=20 StartZ=0 EndX=-11.49 EndY=20 EndZ=0
    g42: LineSegment StartX=-49.19 StartY=17.25 StartZ=0 EndX=-1.5 EndY=17.25 EndZ=0
    g43: LineSegment StartX=-49.19 StartY=14.25 StartZ=0 EndX=-1.5 EndY=14.25 EndZ=0
    g44: LineSegment StartX=-49.19 StartY=11.5 StartZ=0 EndX=-1.5 EndY=11.5 EndZ=0
    g45: LineSegment StartX=-49.19 StartY=8.5 StartZ=0 EndX=-1.5 EndY=8.5 EndZ=0
    g46: LineSegment StartX=-49.19 StartY=5.75 StartZ=0 EndX=-1.5 EndY=5.75 EndZ=0
    g47: LineSegment StartX=-49.19 StartY=2.75 StartZ=0 EndX=-1.5 EndY=2.75 EndZ=0
  constraints (120):
    c: Vertical(g0)
    c: Distance(g0) = 3
    c: Block(g0)
    c: Vertical(g1)
    c: Distance(g1) = 3
    c: Vertical(g2)
    c: Equal(g0,g2) = 3
    c: Block(g2)
    c: Vertical(g3)
    c: Equal(g1,g3) = 3
    c: Vertical(g4)
    c: Equal(g0,g4) = 3
    c: Block(g4)
    c: Vertical(g5)
    c: Equal(g1,g5) = 3
    c: Vertical(g6)
    c: Equal(g0,g6) = 3
    c: Block(g6)
    c: Vertical(g7)
    c: Equal(g1,g7) = 3
    c: Vertical(g8)
    c: Equal(g0,g8) = 3
    c: Block(g8)
    c: Vertical(g9)
    c: Equal(g1,g9) = 3
    c: Vertical(g10)
    c: Equal(g0,g10) = 3
    c: Block(g10)
    c: Vertical(g11)
    c: Equal(g1,g11) = 3
    c: Block(g12)
    c: Block(g13)
    c: Block(g14)
    c: Block(g15)
    c: Block(g16)
    c: Block(g17)
    c: Block(g18)
    c: Block(g19)
    c: Block(g20)
    c: Block(g21)
    c: Block(g22)
    c: Block(g23)
    c: Block(g11)
    c: Block(g9)
    c: Block(g7)
    c: Block(g5)
    c: Block(g3)
    c: Block(g1)
    c: Coincident(g24,g0)
    c: Coincident(g24,g12)
    c: Horizontal(g24)
    c: Coincident(g25,g0)
    c: Coincident(g25,g12)
    c: Horizontal(g25)
    c: Coincident(g26,g1)
    c: Coincident(g26,g13)
    c: Horizontal(g26)
    c: Coincident(g27,g1)
    c: Coincident(g27,g13)
    c: Horizontal(g27)
    c: Coincident(g28,g2)
    c: Coincident(g28,g14)
    c: Horizontal(g28)
    c: Coincident(g29,g2)
    c: Coincident(g29,g14)
    c: Horizontal(g29)
    c: Coincident(g30,g3)
    c: Coincident(g30,g15)
    c: Horizontal(g30)
    c: Coincident(g31,g3)
    c: Coincident(g31,g15)
    c: Horizontal(g31)
    c: Coincident(g32,g4)
    c: Coincident(g32,g16)
    c: Horizontal(g32)
    c: Coincident(g33,g4)
    c: Coincident(g33,g16)
    c: Horizontal(g33)
    c: Coincident(g34,g5)
    c: Coincident(g34,g17)
    c: Horizontal(g34)
    c: Coincident(g35,g5)
    c: Coincident(g35,g17)
    c: Horizontal(g35)
    c: Coincident(g36,g6)
    c: Coincident(g36,g19)
    c: Horizontal(g36)
    c: Coincident(g37,g6)
    c: Coincident(g37,g19)
    c: Horizontal(g37)
    c: Coincident(g38,g7)
    c: Coincident(g38,g18)
    c: Horizontal(g38)
    c: Coincident(g39,g7)
    c: Coincident(g39,g18)
    c: Horizontal(g39)
    c: Coincident(g40,g8)
    c: Coincident(g40,g20)
    c: Horizontal(g40)
    c: Coincident(g41,g8)
    c: Coincident(g41,g20)
    c: Horizontal(g41)
    c: Coincident(g42,g9)
    c: Coincident(g42,g23)
    c: Horizontal(g42)
    c: Coincident(g43,g9)
    c: Coincident(g43,g23)
    c: Horizontal(g43)
    c: Coincident(g44,g10)
    c: Coincident(g44,g22)
    c: Horizontal(g44)
    c: Coincident(g45,g10)
    c: Coincident(g45,g22)
    c: Horizontal(g45)
    c: Coincident(g46,g11)
    c: Coincident(g46,g21)
    c: Horizontal(g46)
    c: Coincident(g47,g11)
    c: Coincident(g47,g21)
    c: Horizontal(g47)
FEATURE [Part::Extrusion] Extrude046
  Base = -> Sketch055
  Dir = (1,0,0)
  DirMode = 2
  FaceMakerClass = Part::FaceMakerBullseye
  LengthFwd = 23
  LengthRev = 0
  Placement = pos=(-19,0,0) rot=(0,0,1;0rad)
  Solid = true
  Symmetric = false
FEATURE [Part::Fillet] Fillet038  label="removeToCreateVentalationHoles001"
  Base = -> Extrude046
  Edges = <same value as first occurrence — deduplicated (x6 in doc)>
  Placement = pos=(7,0,0) rot=(0,0,1;0rad)
FEATURE [Sketcher::SketchObject] Sketch056  label="topSketch014"
  FullyConstrained = true
  sketch-geometry (22):
    g0: LineSegment StartX=5.21097e-06 StartY=3 StartZ=0 EndX=5.21097e-06 EndY=19 EndZ=0
    g1: ArcOfCircle CenterX=19 CenterY=19 CenterZ=0 NormalX=0 NormalY=0 NormalZ=1 AngleXU=0 Radius=19 StartAngle=1.5708 EndAngle=3.14159
    g2: ArcOfCircle CenterX=19 CenterY=19 CenterZ=0 NormalX=0 NormalY=0 NormalZ=1 AngleXU=0 Radius=16 StartAngle=1.5708 EndAngle=3.14159
    g3: LineSegment StartX=114 StartY=35 StartZ=0 EndX=19 EndY=35 EndZ=0
    g4: LineSegment StartX=5.21097e-06 StartY=3 StartZ=0 EndX=5.21097e-06 EndY=0 EndZ=0
    g5: LineSegment StartX=3 StartY=0 StartZ=0 EndX=5.21097e-06 EndY=0 EndZ=0
    g6: LineSegment StartX=3 StartY=19 StartZ=0 EndX=3 EndY=0 EndZ=0
    g7: LineSegment StartX=19 StartY=38 StartZ=0 EndX=124 EndY=38 EndZ=0
    g8: Circle CenterX=119 CenterY=35 CenterZ=0 NormalX=0 NormalY=0 NormalZ=1 AngleXU=0 Radius=1
    g9: Circle CenterX=121 CenterY=35 CenterZ=0 NormalX=0 NormalY=0 NormalZ=1 AngleXU=0 Radius=1
    g10: Circle CenterX=121 CenterY=33 CenterZ=0 NormalX=0 NormalY=0 NormalZ=1 AngleXU=0 Radius=1
    g11: BSplineCurve PolesCount=3 KnotsCount=2 Degree=2 IsPeriodic=0
    g12: GeomPoint X=119 Y=35 Z=0
    g13: GeomPoint X=121 Y=33 Z=0
    g14: LineSegment StartX=119 StartY=35 StartZ=0 EndX=114 EndY=35 EndZ=0
    g15: ArcOfCircle CenterX=105 CenterY=19 CenterZ=0 NormalX=0 NormalY=0 NormalZ=1 AngleXU=0 Radius=16 StartAngle=5.60905 EndAngle=6.28319
    g16: LineSegment StartX=121 StartY=33 StartZ=0 EndX=121 EndY=19 EndZ=0
    g17: LineSegment StartX=117.5 StartY=9.01251 StartZ=0 EndX=121.163 EndY=9.0125 EndZ=0
    g18: ArcOfCircle CenterX=105 CenterY=19 CenterZ=0 NormalX=0 NormalY=0 NormalZ=1 AngleXU=0 Radius=20.6155 StartAngle=5.7297 EndAngle=6.28319
    g19: LineSegment StartX=121.163 StartY=9.0125 StartZ=0 EndX=122.538 EndY=8.16329 EndZ=0
    g20: LineSegment StartX=124 StartY=38 StartZ=0 EndX=125.616 EndY=38 EndZ=0
    g21: LineSegment StartX=125.616 StartY=19 StartZ=0 EndX=125.616 EndY=38 EndZ=0
  constraints (49):
    c: Vertical(g0)
    c: Block(g0)
    c: Coincident(g1,g0)
    c: Block(g1)
    c: Coincident(g2,g1)
    c: Block(g2)
    c: Coincident(g3,g2)
    c: Horizontal(g3)
    c: Tangent(g3,g2)
    c: Coincident(g4,g0)
    c: Distance(g4) = 3
    c: Vertical(g4)
    c: Coincident(g5,g4)
    c: Horizontal(g5)
    c: Coincident(g6,g2)
    c: Coincident(g6,g5)
    c: Vertical(g6)
    c: Horizontal(g7)
    c: Distance(g7) = 105
    c: Coincident(g7,g1)
    c: Block(g3)
    c: Weight(g8) = 1
    c: Equal(g8,g9)
    c: Equal(g8,g10)
    c: InternalAlignment(g8,g11)
    c: InternalAlignment(g9,g11)
    c: InternalAlignment(g10,g11)
    c: InternalAlignment(g12,g11)
    c: InternalAlignment(g13,g11)
    c: Block(g11)
    c: Coincident(g14,g11)
    c: Coincident(g14,g3)
    c: Horizontal(g14)
    c: Block(g15)
    c: Coincident(g16,g11)
    c: Coincident(g16,g15)
    c: Vertical(g16)
    c: Distance(g16) = 14
    c: Coincident(g17,g15)
    c: Block(g18)
    c: Coincident(g19,g18)
    c: Coincident(g20,g7)
    c: Horizontal(g20)
    c: Vertical(g21)
    c: Coincident(g20,g21)
    c: Block(g20)
    c: Block(g21)
    c: Block(g19)
    c: Block(g17)
FEATURE [Part::Box] Box026  label="removeToCreteHoleForPlugHousing032"
  AttacherType = Attacher::AttachEngine3D
  Height = 28.6
  Length = 10
  Placement = pos=(-2,0,21.7) rot=(0,0,1;0rad)
  Width = 19
FEATURE [Part::Feature] Face109 .. Face112  x4 (patterned run collapsed; names and placements below)
  shape: bbox 3.5 x 17.8 x 2e-07 mm, 1 faces, 0 solids (baked)
FEATURE [Part::Revolution] Revolve117  label="removeToCreateScrewAndThreadedInsertHole045"
  Angle = 360
  Axis = (0,1,0)
  Base = (0,0,0)
  FaceMakerClass = Part::FaceMakerBullseye
  Placement = pos=(62.3,30.3,19.7) rot=(0,0,1;0rad)
  Solid = false
  Source = -> Face109
  Symmetric = false
FEATURE [Part::Revolution] Revolve118  label="removeToCreateScrewAndThreadedInsertHole046"
  Angle = 360
  Axis = (0,1,0)
  Base = (0,0,0)
  FaceMakerClass = Part::FaceMakerBullseye
  Placement = pos=(62.3,30.3,51.7) rot=(0,0,1;0rad)
  Solid = false
  Source = -> Face110
  Symmetric = false
FEATURE [Part::Revolution] Revolve119  label="removeToCreateScrewAndThreadedInsertHole047"
  Angle = 360
  Axis = (0,1,0)
  Base = (0,0,0)
  FaceMakerClass = Part::FaceMakerBullseye
  Placement = pos=(30.3,30.3,19.7) rot=(0,0,1;0rad)
  Solid = false
  Source = -> Face111
  Symmetric = false
FEATURE [Part::Revolution] Revolve120  label="removeToCreateScrewAndThreadedInsertHole048"
  Angle = 360
  Axis = (0,1,0)
  Base = (0,0,0)
  FaceMakerClass = Part::FaceMakerBullseye
  Placement = pos=(30.3,30.3,51.7) rot=(0,0,1;0rad)
  Solid = false
  Source = -> Face112
  Symmetric = false
FEATURE [Part::MultiFuse] Fusion087  label="createThreadedInsertHolesForFan005"
  Shapes = -> [Revolve117,Revolve118,Revolve119,Revolve120]
FEATURE [Part::Extrusion] Extrude047
  Base = -> Sketch056
  Dir = (0,0,1)
  DirMode = 2
  FaceMakerClass = Part::FaceMakerBullseye
  LengthFwd = 72
  LengthRev = 0
  Solid = true
  Symmetric = false
FEATURE [Part::Fillet] Fillet039  label="top019"
  Base = -> Extrude047
  Edges = 1 edges r=2: [Edge35]
FEATURE [Sketcher::SketchObject] Sketch057
  FullyConstrained = false
  Placement = pos=(0,0,0) rot=(1,0,0;1.5708rad)
  sketch-geometry (24):
    g0: ArcOfCircle CenterX=-4 CenterY=-10.5 CenterZ=0 NormalX=0 NormalY=0 NormalZ=1 AngleXU=0 Radius=1.5 StartAngle=6e-16 EndAngle=3.14159
    g1: ArcOfCircle CenterX=-34.2 CenterY=-10.5 CenterZ=0 NormalX=0 NormalY=0 NormalZ=1 AngleXU=0 Radius=1.5 StartAngle=0 EndAngle=3.14159
    g2: ArcOfCircle CenterX=-34.2 CenterY=-27.7 CenterZ=0 NormalX=0 NormalY=0 NormalZ=1 AngleXU=0 Radius=1.5 StartAngle=3.14159 EndAngle=6.28319
    g3: ArcOfCircle CenterX=-4 CenterY=-27.7 CenterZ=0 NormalX=0 NormalY=0 NormalZ=1 AngleXU=0 Radius=1.5 StartAngle=3.1416 EndAngle=6.28319
    g4: ArcOfCircle CenterX=-10 CenterY=-4.3 CenterZ=0 NormalX=0 NormalY=0 NormalZ=1 AngleXU=0 Radius=1.5 StartAngle=2e-16 EndAngle=3.14159
    g5: ArcOfCircle CenterX=-16.1 CenterY=-1.8 CenterZ=0 NormalX=0 NormalY=0 NormalZ=1 AngleXU=0 Radius=1.5 StartAngle=5e-16 EndAngle=3.14159
    g6: ArcOfCircle CenterX=-22.1 CenterY=-1.8 CenterZ=0 NormalX=0 NormalY=0 NormalZ=1 AngleXU=0 Radius=1.5 StartAngle=5e-16 EndAngle=3.14159
    g7: ArcOfCircle CenterX=-28.2 CenterY=-4.3 CenterZ=0 NormalX=0 NormalY=0 NormalZ=1 AngleXU=0 Radius=1.5 StartAngle=2e-16 EndAngle=3.14159
    g8: ArcOfCircle CenterX=-10 CenterY=-33.9 CenterZ=0 NormalX=0 NormalY=0 NormalZ=1 AngleXU=0 Radius=1.5 StartAngle=3.14159 EndAngle=6.28319
    g9: ArcOfCircle CenterX=-16.1 CenterY=-36.4 CenterZ=0 NormalX=0 NormalY=0 NormalZ=1 AngleXU=0 Radius=1.5 StartAngle=3.14159 EndAngle=6.28319
    g10: ArcOfCircle CenterX=-22.1 CenterY=-36.4 CenterZ=0 NormalX=0 NormalY=0 NormalZ=1 AngleXU=0 Radius=1.5 StartAngle=3.14159 EndAngle=6.28319
    g11: ArcOfCircle CenterX=-28.2 CenterY=-33.9 CenterZ=0 NormalX=0 NormalY=0 NormalZ=1 AngleXU=0 Radius=1.5 StartAngle=3.14159 EndAngle=6.28319
    g12: LineSegment StartX=-35.7 StartY=-10.5 StartZ=0 EndX=-35.7 EndY=-27.7 EndZ=0
    g13: LineSegment StartX=-32.7 StartY=-10.5 StartZ=0 EndX=-32.7 EndY=-27.7 EndZ=0
    g14: LineSegment StartX=-29.7 StartY=-33.9 StartZ=0 EndX=-29.7 EndY=-4.3 EndZ=0
    g15: LineSegment StartX=-26.7 StartY=-33.9 StartZ=0 EndX=-26.7 EndY=-4.3 EndZ=0
    g16: LineSegment StartX=-2.5 StartY=-10.5 StartZ=0 EndX=-2.5 EndY=-27.7 EndZ=0
    g17: LineSegment StartX=-8.5 StartY=-4.3 StartZ=0 EndX=-8.5 EndY=-33.9 EndZ=0
    g18: LineSegment StartX=-5.5 StartY=-10.5 StartZ=0 EndX=-5.5 EndY=-27.7 EndZ=0
    g19: LineSegment StartX=-11.5 StartY=-4.3 StartZ=0 EndX=-11.5 EndY=-33.9 EndZ=0
    g20: LineSegment StartX=-14.6 StartY=-1.8 StartZ=0 EndX=-14.6 EndY=-36.4 EndZ=0
    g21: LineSegment StartX=-17.6 StartY=-1.8 StartZ=0 EndX=-17.6 EndY=-36.4 EndZ=0
    g22: LineSegment StartX=-20.6 StartY=-36.4 StartZ=0 EndX=-20.6 EndY=-1.8 EndZ=0
    g23: LineSegment StartX=-23.6 StartY=-1.8 StartZ=0 EndX=-23.6 EndY=-36.4 EndZ=0
  constraints (48):
    c: Block(g0)
    c: Block(g1)
    c: Block(g2)
    c: Block(g3)
    c: Block(g4)
    c: Block(g5)
    c: Block(g6)
    c: Block(g7)
    c: Block(g8)
    c: Block(g9)
    c: Block(g10)
    c: Block(g11)
    c: Coincident(g12,g1)
    c: Coincident(g12,g2)
    c: Vertical(g12)
    c: Coincident(g13,g1)
    c: Coincident(g13,g2)
    c: Vertical(g13)
    c: Coincident(g14,g11)
    c: Coincident(g14,g7)
    c: Vertical(g14)
    c: Coincident(g15,g11)
    c: Coincident(g15,g7)
    c: Vertical(g15)
    c: Coincident(g16,g0)
    c: Coincident(g16,g3)
    c: Vertical(g16)
    c: Coincident(g17,g4)
    c: Coincident(g17,g8)
    c: Vertical(g17)
    c: Coincident(g18,g0)
    c: Coincident(g18,g3)
    c: Vertical(g18)
    c: Coincident(g19,g4)
    c: Coincident(g19,g8)
    c: Vertical(g19)
    c: Coincident(g20,g5)
    c: Coincident(g20,g9)
    c: Vertical(g20)
    c: Coincident(g21,g5)
    c: Coincident(g21,g9)
    c: Vertical(g21)
    c: Coincident(g22,g10)
    c: Coincident(g22,g6)
    c: Vertical(g22)
    c: Coincident(g23,g6)
    c: Coincident(g23,g10)
    c: Vertical(g23)
FEATURE [Part::Extrusion] Extrude048  label="removeToCreateFanGrillHoles004"
  Base = -> Sketch057
  Dir = (0,-1,6e-16)
  DirMode = 2
  FaceMakerClass = Part::FaceMakerBullseye
  LengthFwd = 10
  LengthRev = 0
  Placement = pos=(65.4,44,54.82) rot=(0,0,1;0rad)
  Solid = true
  Symmetric = false
FEATURE [Part::Cut] Cut040  label="top021"
  Base = -> Fillet039
  Tool = -> Extrude048
FEATURE [Part::Cylinder] Cylinder041  label="removeToCreteHoleForPlugHousing034"
  Angle = 360
  AttacherType = Attacher::AttachEngine3D
  Height = 20
  Placement = pos=(-2,19,36) rot=(0,1,0;1.5708rad)
  Radius = 14.3
FEATURE [Part::MultiFuse] Fusion089  label="removeToCreteHoleForPlugHousing035"
  Shapes = -> [Box026,Cylinder041]
FEATURE [Part::Cylinder] Cylinder042
  Angle = 360
  AttacherType = Attacher::AttachEngine3D
  Height = 20
  Placement = pos=(0,0,36.15) rot=(0,0,1;0rad)
  Radius = 14.3
FEATURE [Part::Cylinder] Cylinder043
  Angle = 360
  AttacherType = Attacher::AttachEngine3D
  Height = 10
  Placement = pos=(0,0,36.15) rot=(0,0,1;0rad)
  Radius = 4
FEATURE [Part::Box] Box027  label="removeToCreteHoleForPlugHousing036"
  AttacherType = Attacher::AttachEngine3D
  Height = 28.6
  Length = 20
  Placement = pos=(106.15,0,21.7) rot=(0,0,1;0rad)
  Width = 19
FEATURE [Part::Cut] Cut041  label="top022"
  Base = -> Cut040
  Tool = -> Fusion087
FEATURE [Part::Cut] Cut039  label="top020"
  Base = -> Cut041
  Tool = -> Fusion089
FEATURE [Part::MultiFuse] Fusion090  label="removeToCreteHoleForPlugHousing037"
  Placement = pos=(70,19,36) rot=(0,1,0;1.5708rad)
  Shapes = -> [Cylinder042,Cylinder043]
FEATURE [Part::MultiFuse] Fusion088  label="removeToCreteHoleForPlugHousing033"
  Shapes = -> [Box027,Fusion090]
FEATURE [Part::Cut] Cut042  label="removeToCreteHoleForPlugHousing038"
  Base = -> Cut039
  Tool = -> Fusion088
FEATURE [Part::MultiFuse] Fusion091  label="removeFromTop"
  Shapes = -> [Fillet038,Fusion085,Fusion084,Fusion083,Extrude045]
FEATURE [Part::Cut] Cut043  label="REAL TOP ====="
  Base = -> Fillet036
  Tool = -> Fusion091
FEATURE [Part::MultiFuse] Fusion092  label="caseScrewPillarBracket016"
  Shapes = -> [Extrude030,Extrude031,Extrude032,Extrude033,Extrude034,Extrude035,Extrude036,Extrude037,Box013,Box014]
FEATURE [Sketcher::SketchObject] Sketch058  label="topSketch015"
  FullyConstrained = true
  sketch-geometry (20):
    g0: LineSegment StartX=5.21097e-06 StartY=3 StartZ=0 EndX=5.21097e-06 EndY=19 EndZ=0
    g1: ArcOfCircle CenterX=19 CenterY=19 CenterZ=0 NormalX=0 NormalY=0 NormalZ=1 AngleXU=0 Radius=19 StartAngle=1.5708 EndAngle=3.14159
    g2: ArcOfCircle CenterX=19 CenterY=19 CenterZ=0 NormalX=0 NormalY=0 NormalZ=1 AngleXU=0 Radius=16 StartAngle=1.5708 EndAngle=3.14159
    g3: LineSegment StartX=114 StartY=35 StartZ=0 EndX=19 EndY=35 EndZ=0
    g4: LineSegment StartX=5.21097e-06 StartY=3 StartZ=0 EndX=5.21097e-06 EndY=0 EndZ=0
    g5: LineSegment StartX=3 StartY=0 StartZ=0 EndX=5.21097e-06 EndY=0 EndZ=0
    g6: LineSegment StartX=3 StartY=19 StartZ=0 EndX=3 EndY=0 EndZ=0
    g7: LineSegment StartX=19 StartY=38 StartZ=0 EndX=124 EndY=38 EndZ=0
    g8: Circle CenterX=119 CenterY=35 CenterZ=0 NormalX=0 NormalY=0 NormalZ=1 AngleXU=0 Radius=1
    g9: Circle CenterX=121 CenterY=35 CenterZ=0 NormalX=0 NormalY=0 NormalZ=1 AngleXU=0 Radius=1
    g10: Circle CenterX=121 CenterY=33 CenterZ=0 NormalX=0 NormalY=0 NormalZ=1 AngleXU=0 Radius=1
    g11: BSplineCurve PolesCount=3 KnotsCount=2 Degree=2 IsPeriodic=0
    g12: GeomPoint X=119 Y=35 Z=0
    g13: GeomPoint X=121 Y=33 Z=0
    g14: LineSegment StartX=119 StartY=35 StartZ=0 EndX=114 EndY=35 EndZ=0
    g15: ArcOfCircle CenterX=105 CenterY=19 CenterZ=0 NormalX=0 NormalY=0 NormalZ=1 AngleXU=0 Radius=19 StartAngle=5.7297 EndAngle=6.28319
    g16: ArcOfCircle CenterX=105 CenterY=19 CenterZ=0 NormalX=0 NormalY=0 NormalZ=1 AngleXU=0 Radius=16 StartAngle=5.60905 EndAngle=6.28319
    g17: LineSegment StartX=121 StartY=33 StartZ=0 EndX=121 EndY=19 EndZ=0
    g18: LineSegment StartX=124 StartY=38 StartZ=0 EndX=124 EndY=19 EndZ=0
    g19: LineSegment StartX=117.5 StartY=9.01251 StartZ=0 EndX=121.163 EndY=9.0125 EndZ=0
  constraints (46):
    c: Vertical(g0)
    c: Block(g0)
    c: Coincident(g1,g0)
    c: Block(g1)
    c: Coincident(g2,g1)
    c: Block(g2)
    c: Coincident(g3,g2)
    c: Horizontal(g3)
    c: Tangent(g3,g2)
    c: Coincident(g4,g0)
    c: Distance(g4) = 3
    c: Vertical(g4)
    c: Coincident(g5,g4)
    c: Horizontal(g5)
    c: Coincident(g6,g2)
    c: Coincident(g6,g5)
    c: Vertical(g6)
    c: Horizontal(g7)
    c: Distance(g7) = 105
    c: Coincident(g7,g1)
    c: Block(g3)
    c: Weight(g8) = 1
    c: Equal(g8,g9)
    c: Equal(g8,g10)
    c: InternalAlignment(g8,g11)
    c: InternalAlignment(g9,g11)
    c: InternalAlignment(g10,g11)
    c: InternalAlignment(g12,g11)
    c: InternalAlignment(g13,g11)
    c: Block(g11)
    c: Coincident(g14,g11)
    c: Coincident(g14,g3)
    c: Horizontal(g14)
    c: Block(g15)
    c: Coincident(g16,g15)
    c: Block(g16)
    c: Coincident(g17,g11)
    c: Coincident(g17,g16)
    c: Vertical(g17)
    c: Distance(g17) = 14
    c: Coincident(g18,g7)
    c: Coincident(g18,g15)
    c: Vertical(g18)
    c: Distance(g18) = 19
    c: Coincident(g19,g16)
    c: Coincident(g19,g15)
FEATURE [Part::Extrusion] Extrude049  label="top023"
  Base = -> Sketch058
  Dir = (0,0,1)
  DirMode = 2
  FaceMakerClass = Part::FaceMakerBullseye
  LengthFwd = 72
  LengthRev = 0
  Solid = true
  Symmetric = false
FEATURE [Sketcher::SketchObject] Sketch059
  FullyConstrained = true
  MapMode = 3
  Placement = pos=(0,0,0) rot=(1,0,0;1.5708rad)
  Support = -> [Extrude049]
  sketch-geometry (8):
    g0: Circle CenterX=80.351 CenterY=-67.6202 CenterZ=0 NormalX=0 NormalY=0 NormalZ=1 AngleXU=0 Radius=2
    g1: Circle CenterX=80.351 CenterY=-67.6202 CenterZ=0 NormalX=0 NormalY=0 NormalZ=1 AngleXU=0 Radius=3
    g2: Circle CenterX=80.351 CenterY=-4.92017 CenterZ=0 NormalX=0 NormalY=0 NormalZ=1 AngleXU=0 Radius=2
    g3: Circle CenterX=80.351 CenterY=-4.92017 CenterZ=0 NormalX=0 NormalY=0 NormalZ=1 AngleXU=0 Radius=3
    g4: Circle CenterX=23.851 CenterY=-4.92017 CenterZ=0 NormalX=0 NormalY=0 NormalZ=1 AngleXU=0 Radius=2
    g5: Circle CenterX=23.851 CenterY=-4.92017 CenterZ=0 NormalX=0 NormalY=0 NormalZ=1 AngleXU=0 Radius=3
    g6: Circle CenterX=23.851 CenterY=-67.6202 CenterZ=0 NormalX=0 NormalY=0 NormalZ=1 AngleXU=0 Radius=2
    g7: Circle CenterX=23.851 CenterY=-67.6202 CenterZ=0 NormalX=0 NormalY=0 NormalZ=1 AngleXU=0 Radius=3
  constraints (8):
    c: Block(g3)
    c: Block(g2)
    c: Block(g1)
    c: Block(g0)
    c: Block(g6)
    c: Block(g7)
    c: Block(g4)
    c: Block(g5)
FEATURE [Sketcher::SketchObject] Sketch060
  FullyConstrained = true
  MapMode = 3
  Placement = pos=(0,0,0) rot=(1,0,0;1.5708rad)
  Support = -> [Extrude049]
  sketch-geometry (8):
    g0: Circle CenterX=80.351 CenterY=-67.6202 CenterZ=0 NormalX=0 NormalY=0 NormalZ=1 AngleXU=0 Radius=3
    g1: Circle CenterX=80.351 CenterY=-4.92017 CenterZ=0 NormalX=0 NormalY=0 NormalZ=1 AngleXU=0 Radius=3
    g2: Circle CenterX=23.851 CenterY=-4.92017 CenterZ=0 NormalX=0 NormalY=0 NormalZ=1 AngleXU=0 Radius=3
    g3: Circle CenterX=23.851 CenterY=-67.6202 CenterZ=0 NormalX=0 NormalY=0 NormalZ=1 AngleXU=0 Radius=3
    g4: Circle CenterX=23.851 CenterY=-67.6202 CenterZ=0 NormalX=0 NormalY=0 NormalZ=1 AngleXU=0 Radius=5
    g5: Circle CenterX=80.351 CenterY=-67.6202 CenterZ=0 NormalX=0 NormalY=0 NormalZ=1 AngleXU=0 Radius=5
    g6: Circle CenterX=23.851 CenterY=-4.92017 CenterZ=0 NormalX=0 NormalY=0 NormalZ=1 AngleXU=0 Radius=5
    g7: Circle CenterX=80.351 CenterY=-4.92017 CenterZ=0 NormalX=0 NormalY=0 NormalZ=1 AngleXU=0 Radius=5
  constraints (8):
    c: Block(g1)
    c: Block(g0)
    c: Block(g3)
    c: Block(g2)
    c: Block(g5)
    c: Block(g4)
    c: Block(g6)
    c: Block(g7)
FEATURE [Sketcher::SketchObject] Sketch061
  FullyConstrained = true
  MapMode = 3
  Placement = pos=(0,0,0) rot=(1,0,0;1.5708rad)
  sketch-geometry (8):
    g0: Circle CenterX=80.351 CenterY=-67.6202 CenterZ=0 NormalX=0 NormalY=0 NormalZ=1 AngleXU=0 Radius=3
    g1: Circle CenterX=80.351 CenterY=-4.92017 CenterZ=0 NormalX=0 NormalY=0 NormalZ=1 AngleXU=0 Radius=3
    g2: Circle CenterX=23.851 CenterY=-4.92017 CenterZ=0 NormalX=0 NormalY=0 NormalZ=1 AngleXU=0 Radius=3
    g3: Circle CenterX=23.851 CenterY=-67.6202 CenterZ=0 NormalX=0 NormalY=0 NormalZ=1 AngleXU=0 Radius=3
    g4: Circle CenterX=23.851 CenterY=-67.6202 CenterZ=0 NormalX=0 NormalY=0 NormalZ=1 AngleXU=0 Radius=5
    g5: Circle CenterX=80.351 CenterY=-67.6202 CenterZ=0 NormalX=0 NormalY=0 NormalZ=1 AngleXU=0 Radius=5
    g6: Circle CenterX=23.851 CenterY=-4.92017 CenterZ=0 NormalX=0 NormalY=0 NormalZ=1 AngleXU=0 Radius=5
    g7: Circle CenterX=80.351 CenterY=-4.92017 CenterZ=0 NormalX=0 NormalY=0 NormalZ=1 AngleXU=0 Radius=5
  constraints (8):
    c: Block(g1)
    c: Block(g0)
    c: Block(g3)
    c: Block(g2)
    c: Block(g5)
    c: Block(g4)
    c: Block(g6)
    c: Block(g7)
FEATURE [Sketcher::SketchObject] Sketch062  label="topSketch016"
  FullyConstrained = true
  sketch-geometry (20):
    g0: LineSegment StartX=5.21097e-06 StartY=3 StartZ=0 EndX=5.21097e-06 EndY=19 EndZ=0
    g1: ArcOfCircle CenterX=19 CenterY=19 CenterZ=0 NormalX=0 NormalY=0 NormalZ=1 AngleXU=0 Radius=19 StartAngle=1.5708 EndAngle=3.14159
    g2: ArcOfCircle CenterX=19 CenterY=19 CenterZ=0 NormalX=0 NormalY=0 NormalZ=1 AngleXU=0 Radius=16 StartAngle=1.5708 EndAngle=3.14159
    g3: LineSegment StartX=114 StartY=35 StartZ=0 EndX=19 EndY=35 EndZ=0
    g4: LineSegment StartX=5.21097e-06 StartY=3 StartZ=0 EndX=5.21097e-06 EndY=0 EndZ=0
    g5: LineSegment StartX=3 StartY=0 StartZ=0 EndX=5.21097e-06 EndY=0 EndZ=0
    g6: LineSegment StartX=3 StartY=19 StartZ=0 EndX=3 EndY=0 EndZ=0
    g7: LineSegment StartX=19 StartY=38 StartZ=0 EndX=124 EndY=38 EndZ=0
    g8: Circle CenterX=119 CenterY=35 CenterZ=0 NormalX=0 NormalY=0 NormalZ=1 AngleXU=0 Radius=1
    g9: Circle CenterX=121 CenterY=35 CenterZ=0 NormalX=0 NormalY=0 NormalZ=1 AngleXU=0 Radius=1
    g10: Circle CenterX=121 CenterY=33 CenterZ=0 NormalX=0 NormalY=0 NormalZ=1 AngleXU=0 Radius=1
    g11: BSplineCurve PolesCount=3 KnotsCount=2 Degree=2 IsPeriodic=0
    g12: GeomPoint X=119 Y=35 Z=0
    g13: GeomPoint X=121 Y=33 Z=0
    g14: LineSegment StartX=119 StartY=35 StartZ=0 EndX=114 EndY=35 EndZ=0
    g15: ArcOfCircle CenterX=105 CenterY=19 CenterZ=0 NormalX=0 NormalY=0 NormalZ=1 AngleXU=0 Radius=19 StartAngle=5.7297 EndAngle=6.28319
    g16: ArcOfCircle CenterX=105 CenterY=19 CenterZ=0 NormalX=0 NormalY=0 NormalZ=1 AngleXU=0 Radius=16 StartAngle=5.60905 EndAngle=6.28319
    g17: LineSegment StartX=121 StartY=33 StartZ=0 EndX=121 EndY=19 EndZ=0
    g18: LineSegment StartX=124 StartY=38 StartZ=0 EndX=124 EndY=19 EndZ=0
    g19: LineSegment StartX=117.5 StartY=9.01251 StartZ=0 EndX=121.163 EndY=9.0125 EndZ=0
  constraints (46):
    c: Vertical(g0)
    c: Block(g0)
    c: Coincident(g1,g0)
    c: Block(g1)
    c: Coincident(g2,g1)
    c: Block(g2)
    c: Coincident(g3,g2)
    c: Horizontal(g3)
    c: Tangent(g3,g2)
    c: Coincident(g4,g0)
    c: Distance(g4) = 3
    c: Vertical(g4)
    c: Coincident(g5,g4)
    c: Horizontal(g5)
    c: Coincident(g6,g2)
    c: Coincident(g6,g5)
    c: Vertical(g6)
    c: Horizontal(g7)
    c: Distance(g7) = 105
    c: Coincident(g7,g1)
    c: Block(g3)
    c: Weight(g8) = 1
    c: Equal(g8,g9)
    c: Equal(g8,g10)
    c: InternalAlignment(g8,g11)
    c: InternalAlignment(g9,g11)
    c: InternalAlignment(g10,g11)
    c: InternalAlignment(g12,g11)
    c: InternalAlignment(g13,g11)
    c: Block(g11)
    c: Coincident(g14,g11)
    c: Coincident(g14,g3)
    c: Horizontal(g14)
    c: Block(g15)
    c: Coincident(g16,g15)
    c: Block(g16)
    c: Coincident(g17,g11)
    c: Coincident(g17,g16)
    c: Vertical(g17)
    c: Distance(g17) = 14
    c: Coincident(g18,g7)
    c: Coincident(g18,g15)
    c: Vertical(g18)
    c: Distance(g18) = 19
    c: Coincident(g19,g16)
    c: Coincident(g19,g15)
FEATURE [Part::Extrusion] Extrude053  label="top024"
  Base = -> Sketch062
  Dir = (0,0,1)
  DirMode = 2
  FaceMakerClass = Part::FaceMakerBullseye
  LengthFwd = 72
  LengthRev = 0
  Solid = true
  Symmetric = false
FEATURE [Sketcher::SketchObject] Sketch063
  FullyConstrained = true
  MapMode = 3
  Placement = pos=(0,0,0) rot=(1,0,0;1.5708rad)
  Support = -> [Extrude053]
  sketch-geometry (8):
    g0: Circle CenterX=80.351 CenterY=-67.6202 CenterZ=0 NormalX=0 NormalY=0 NormalZ=1 AngleXU=0 Radius=2
    g1: Circle CenterX=80.351 CenterY=-67.6202 CenterZ=0 NormalX=0 NormalY=0 NormalZ=1 AngleXU=0 Radius=3
    g2: Circle CenterX=80.351 CenterY=-4.92017 CenterZ=0 NormalX=0 NormalY=0 NormalZ=1 AngleXU=0 Radius=2
    g3: Circle CenterX=80.351 CenterY=-4.92017 CenterZ=0 NormalX=0 NormalY=0 NormalZ=1 AngleXU=0 Radius=3
    g4: Circle CenterX=23.851 CenterY=-4.92017 CenterZ=0 NormalX=0 NormalY=0 NormalZ=1 AngleXU=0 Radius=2
    g5: Circle CenterX=23.851 CenterY=-4.92017 CenterZ=0 NormalX=0 NormalY=0 NormalZ=1 AngleXU=0 Radius=3
    g6: Circle CenterX=23.851 CenterY=-67.6202 CenterZ=0 NormalX=0 NormalY=0 NormalZ=1 AngleXU=0 Radius=2
    g7: Circle CenterX=23.851 CenterY=-67.6202 CenterZ=0 NormalX=0 NormalY=0 NormalZ=1 AngleXU=0 Radius=3
  constraints (8):
    c: Block(g3)
    c: Block(g2)
    c: Block(g1)
    c: Block(g0)
    c: Block(g6)
    c: Block(g7)
    c: Block(g4)
    c: Block(g5)
FEATURE [Part::Extrusion] Extrude054
  Base = -> Sketch063
  Dir = (0,-1,2e-16)
  DirMode = 2
  FaceMakerClass = Part::FaceMakerBullseye
  LengthFwd = 6
  LengthRev = 0
  Placement = pos=(0,9,0) rot=(0,0,1;0rad)
  Solid = true
  Symmetric = false
FEATURE [Sketcher::SketchObject] Sketch064  label="topSketch017"
  FullyConstrained = true
  sketch-geometry (20):
    g0: LineSegment StartX=5.21097e-06 StartY=3 StartZ=0 EndX=5.21097e-06 EndY=19 EndZ=0
    g1: ArcOfCircle CenterX=19 CenterY=19 CenterZ=0 NormalX=0 NormalY=0 NormalZ=1 AngleXU=0 Radius=19 StartAngle=1.5708 EndAngle=3.14159
    g2: ArcOfCircle CenterX=19 CenterY=19 CenterZ=0 NormalX=0 NormalY=0 NormalZ=1 AngleXU=0 Radius=16 StartAngle=1.5708 EndAngle=3.14159
    g3: LineSegment StartX=114 StartY=35 StartZ=0 EndX=19 EndY=35 EndZ=0
    g4: LineSegment StartX=5.21097e-06 StartY=3 StartZ=0 EndX=5.21097e-06 EndY=0 EndZ=0
    g5: LineSegment StartX=3 StartY=0 StartZ=0 EndX=5.21097e-06 EndY=0 EndZ=0
    g6: LineSegment StartX=3 StartY=19 StartZ=0 EndX=3 EndY=0 EndZ=0
    g7: LineSegment StartX=19 StartY=38 StartZ=0 EndX=124 EndY=38 EndZ=0
    g8: Circle CenterX=119 CenterY=35 CenterZ=0 NormalX=0 NormalY=0 NormalZ=1 AngleXU=0 Radius=1
    g9: Circle CenterX=121 CenterY=35 CenterZ=0 NormalX=0 NormalY=0 NormalZ=1 AngleXU=0 Radius=1
    g10: Circle CenterX=121 CenterY=33 CenterZ=0 NormalX=0 NormalY=0 NormalZ=1 AngleXU=0 Radius=1
    g11: BSplineCurve PolesCount=3 KnotsCount=2 Degree=2 IsPeriodic=0
    g12: GeomPoint X=119 Y=35 Z=0
    g13: GeomPoint X=121 Y=33 Z=0
    g14: LineSegment StartX=119 StartY=35 StartZ=0 EndX=114 EndY=35 EndZ=0
    g15: ArcOfCircle CenterX=105 CenterY=19 CenterZ=0 NormalX=0 NormalY=0 NormalZ=1 AngleXU=0 Radius=19 StartAngle=5.7297 EndAngle=6.28319
    g16: ArcOfCircle CenterX=105 CenterY=19 CenterZ=0 NormalX=0 NormalY=0 NormalZ=1 AngleXU=0 Radius=16 StartAngle=5.60905 EndAngle=6.28319
    g17: LineSegment StartX=121 StartY=33 StartZ=0 EndX=121 EndY=19 EndZ=0
    g18: LineSegment StartX=124 StartY=38 StartZ=0 EndX=124 EndY=19 EndZ=0
    g19: LineSegment StartX=117.5 StartY=9.01251 StartZ=0 EndX=121.163 EndY=9.0125 EndZ=0
  constraints (46):
    c: Vertical(g0)
    c: Block(g0)
    c: Coincident(g1,g0)
    c: Block(g1)
    c: Coincident(g2,g1)
    c: Block(g2)
    c: Coincident(g3,g2)
    c: Horizontal(g3)
    c: Tangent(g3,g2)
    c: Coincident(g4,g0)
    c: Distance(g4) = 3
    c: Vertical(g4)
    c: Coincident(g5,g4)
    c: Horizontal(g5)
    c: Coincident(g6,g2)
    c: Coincident(g6,g5)
    c: Vertical(g6)
    c: Horizontal(g7)
    c: Distance(g7) = 105
    c: Coincident(g7,g1)
    c: Block(g3)
    c: Weight(g8) = 1
    c: Equal(g8,g9)
    c: Equal(g8,g10)
    c: InternalAlignment(g8,g11)
    c: InternalAlignment(g9,g11)
    c: InternalAlignment(g10,g11)
    c: InternalAlignment(g12,g11)
    c: InternalAlignment(g13,g11)
    c: Block(g11)
    c: Coincident(g14,g11)
    c: Coincident(g14,g3)
    c: Horizontal(g14)
    c: Block(g15)
    c: Coincident(g16,g15)
    c: Block(g16)
    c: Coincident(g17,g11)
    c: Coincident(g17,g16)
    c: Vertical(g17)
    c: Distance(g17) = 14
    c: Coincident(g18,g7)
    c: Coincident(g18,g15)
    c: Vertical(g18)
    c: Distance(g18) = 19
    c: Coincident(g19,g16)
    c: Coincident(g19,g15)
FEATURE [Sketcher::SketchObject] Sketch065
  FullyConstrained = true
  MapMode = 3
  Placement = pos=(0,0,0) rot=(1,0,0;1.5708rad)
  sketch-geometry (8):
    g0: Circle CenterX=80.351 CenterY=-67.6202 CenterZ=0 NormalX=0 NormalY=0 NormalZ=1 AngleXU=0 Radius=3
    g1: Circle CenterX=80.351 CenterY=-4.92017 CenterZ=0 NormalX=0 NormalY=0 NormalZ=1 AngleXU=0 Radius=3
    g2: Circle CenterX=23.851 CenterY=-4.92017 CenterZ=0 NormalX=0 NormalY=0 NormalZ=1 AngleXU=0 Radius=3
    g3: Circle CenterX=23.851 CenterY=-67.6202 CenterZ=0 NormalX=0 NormalY=0 NormalZ=1 AngleXU=0 Radius=3
    g4: Circle CenterX=23.851 CenterY=-67.6202 CenterZ=0 NormalX=0 NormalY=0 NormalZ=1 AngleXU=0 Radius=5
    g5: Circle CenterX=80.351 CenterY=-67.6202 CenterZ=0 NormalX=0 NormalY=0 NormalZ=1 AngleXU=0 Radius=5
    g6: Circle CenterX=23.851 CenterY=-4.92017 CenterZ=0 NormalX=0 NormalY=0 NormalZ=1 AngleXU=0 Radius=5
    g7: Circle CenterX=80.351 CenterY=-4.92017 CenterZ=0 NormalX=0 NormalY=0 NormalZ=1 AngleXU=0 Radius=5
  constraints (8):
    c: Block(g1)
    c: Block(g0)
    c: Block(g3)
    c: Block(g2)
    c: Block(g5)
    c: Block(g4)
    c: Block(g6)
    c: Block(g7)
FEATURE [Part::Extrusion] Extrude056
  Base = -> Sketch065
  Dir = (0,-1,2e-16)
  DirMode = 2
  FaceMakerClass = Part::FaceMakerBullseye
  LengthFwd = 2
  LengthRev = 0
  Solid = true
  Symmetric = false
FEATURE [Part::Extrusion] Extrude057  label="top025"
  Base = -> Sketch064
  Dir = (0,0,1)
  DirMode = 2
  FaceMakerClass = Part::FaceMakerBullseye
  LengthFwd = 72
  LengthRev = 0
  Solid = true
  Symmetric = false
FEATURE [Sketcher::SketchObject] Sketch066
  FullyConstrained = true
  MapMode = 3
  Placement = pos=(0,0,0) rot=(1,0,0;1.5708rad)
  Support = -> [Extrude057]
  sketch-geometry (8):
    g0: Circle CenterX=80.351 CenterY=-67.6202 CenterZ=0 NormalX=0 NormalY=0 NormalZ=1 AngleXU=0 Radius=3
    g1: Circle CenterX=80.351 CenterY=-4.92017 CenterZ=0 NormalX=0 NormalY=0 NormalZ=1 AngleXU=0 Radius=3
    g2: Circle CenterX=23.851 CenterY=-4.92017 CenterZ=0 NormalX=0 NormalY=0 NormalZ=1 AngleXU=0 Radius=3
    g3: Circle CenterX=23.851 CenterY=-67.6202 CenterZ=0 NormalX=0 NormalY=0 NormalZ=1 AngleXU=0 Radius=3
    g4: Circle CenterX=23.851 CenterY=-67.6202 CenterZ=0 NormalX=0 NormalY=0 NormalZ=1 AngleXU=0 Radius=5
    g5: Circle CenterX=80.351 CenterY=-67.6202 CenterZ=0 NormalX=0 NormalY=0 NormalZ=1 AngleXU=0 Radius=5
    g6: Circle CenterX=23.851 CenterY=-4.92017 CenterZ=0 NormalX=0 NormalY=0 NormalZ=1 AngleXU=0 Radius=5
    g7: Circle CenterX=80.351 CenterY=-4.92017 CenterZ=0 NormalX=0 NormalY=0 NormalZ=1 AngleXU=0 Radius=5
  constraints (8):
    c: Block(g1)
    c: Block(g0)
    c: Block(g3)
    c: Block(g2)
    c: Block(g5)
    c: Block(g4)
    c: Block(g6)
    c: Block(g7)
FEATURE [Part::Extrusion] Extrude055
  Base = -> Sketch066
  Dir = (0,-1,2e-16)
  DirMode = 2
  FaceMakerClass = Part::FaceMakerBullseye
  LengthFwd = 2
  LengthRev = 0
  Solid = true
  Symmetric = false
FEATURE [Part::Fillet] Fillet041
  Base = -> Extrude056
  Edges = 4 edges r=1.99: [Edge6,Edge12,Edge18,Edge24]
FEATURE [Part::Cut] Cut045
  Base = -> Extrude055
  Placement = pos=(0,6,0) rot=(0,0,1;0rad)
  Tool = -> Fillet041
FEATURE [Part::MultiFuse] Fusion095  label="pcbScrewPillars"
  Placement = pos=(-3.2,-1,72.3) rot=(0,0,1;0rad)
  Shapes = -> [Cut045,Extrude054]
FEATURE [Part::Feature] Face113
  shape: bbox 3.2 x 1.5 x 2e-07 mm, 1 faces, 0 solids (baked)
FEATURE [Part::Revolution] Revolve121  label="backCaseScrewRetainer002"
  Angle = 360
  Axis = (0,1,0)
  Base = (0,0,0)
  FaceMakerClass = Part::FaceMakerBullseye
  Placement = pos=(12.5,3,62) rot=(0,0,1;0rad)
  Solid = false
  Source = -> Face113
  Symmetric = false
FEATURE [Part::Feature] Face114
  shape: bbox 3.2 x 1.5 x 2e-07 mm, 1 faces, 0 solids (baked)
FEATURE [Part::Feature] Face115
  shape: bbox 3.2 x 1.5 x 2e-07 mm, 1 faces, 0 solids (baked)
FEATURE [Part::Feature] Face116
  shape: bbox 3.2 x 1.5 x 2e-07 mm, 1 faces, 0 solids (baked)
FEATURE [Part::Revolution] Revolve122  label="frontCaseScrewRetainer004"
  Angle = 360
  Axis = (0,1,0)
  Base = (0,0,0)
  FaceMakerClass = Part::FaceMakerBullseye
  Placement = pos=(89.5,3,68.5) rot=(0,0,1;0rad)
  Solid = false
  Source = -> Face115
  Symmetric = false
FEATURE [Part::Revolution] Revolve123  label="frontCaseScrewRetainer005"
  Angle = 360
  Axis = (0,1,0)
  Base = (0,0,0)
  FaceMakerClass = Part::FaceMakerBullseye
  Placement = pos=(89.5,3,3.5) rot=(0,0,1;0rad)
  Solid = false
  Source = -> Face116
  Symmetric = false
FEATURE [Part::Revolution] Revolve124  label="backCaseScrewRetainer003"
  Angle = 360
  Axis = (0,1,0)
  Base = (0,0,0)
  FaceMakerClass = Part::FaceMakerBullseye
  Placement = pos=(12.5,3,10) rot=(0,0,1;0rad)
  Solid = false
  Source = -> Face114
  Symmetric = false
FEATURE [Part::Feature] Face117
  shape: bbox 3.6 x 3.2 x 2e-07 mm, 1 faces, 0 solids (baked)
FEATURE [Part::Revolution] Revolve125  label="moreFrontCaseScrewRetainer004"
  Angle = 360
  Axis = (0,1,0)
  Base = (0,0,0)
  FaceMakerClass = Part::FaceMakerBullseye
  Placement = pos=(109.5,4.5,68.5) rot=(0,0,1;0rad)
  Solid = false
  Source = -> Face117
  Symmetric = false
FEATURE [Part::Feature] Face118
  shape: bbox 3.6 x 3.2 x 2e-07 mm, 1 faces, 0 solids (baked)
FEATURE [Part::Revolution] Revolve126  label="moreFrontCaseScrewRetainer005"
  Angle = 360
  Axis = (0,1,0)
  Base = (0,0,0)
  FaceMakerClass = Part::FaceMakerBullseye
  Placement = pos=(109.5,4.5,3.5) rot=(0,0,1;0rad)
  Solid = false
  Source = -> Face118
  Symmetric = false
FEATURE [Part::MultiFuse] Fusion096  label="screwRetainers001"
  Shapes = -> [Revolve126,Revolve125,Revolve124,Revolve123,Revolve122,Revolve121]
FEATURE [Part::Feature] Face119
  shape: bbox 10 x 16.5 x 2e-07 mm, 1 faces, 0 solids (baked)
FEATURE [Part::Revolution] Revolve130  label="plugHousing050"
  Angle = 360
  Axis = (0,1,0)
  Base = (0,0,0)
  FaceMakerClass = Part::FaceMakerBullseye
  Placement = pos=(0,0,36.15) rot=(0,0,1;0rad)
  Solid = false
  Source = -> Face119
  Symmetric = false
FEATURE [Part::Feature] Face120
  shape: bbox 10 x 16.5 x 2e-07 mm, 1 faces, 0 solids (baked)
FEATURE [Part::Feature] Face121
  shape: bbox 10 x 16.5 x 2e-07 mm, 1 faces, 0 solids (baked)
FEATURE [Part::Revolution] Revolve127  label="plugHousing047"
  Angle = 360
  Axis = (0,1,0)
  Base = (0,0,0)
  FaceMakerClass = Part::FaceMakerBullseye
  Placement = pos=(0,0,36.15) rot=(0,0,1;0rad)
  Solid = false
  Source = -> Face121
  Symmetric = false
FEATURE [Part::Feature] Face122
  shape: bbox 10 x 16.5 x 2e-07 mm, 1 faces, 0 solids (baked)
FEATURE [Part::Feature] Face123
  shape: bbox 10 x 16.5 x 2e-07 mm, 1 faces, 0 solids (baked)
FEATURE [Part::Revolution] Revolve128  label="plugHousing048"
  Angle = 360
  Axis = (0,1,0)
  Base = (0,0,0)
  FaceMakerClass = Part::FaceMakerBullseye
  Placement = pos=(0,0,36.15) rot=(0,0,1;0rad)
  Solid = false
  Source = -> Face123
  Symmetric = false
FEATURE [Part::MultiFuse] Fusion100  label="plugHousing054"
  Placement = pos=(0,0,0) rot=(0,0,1;1.5708rad)
  Shapes = -> [Revolve130,Revolve128]
FEATURE [Part::Feature] Face124
  shape: bbox 10 x 16.5 x 2e-07 mm, 1 faces, 0 solids (baked)
FEATURE [Part::Feature] Face125
  shape: bbox 10 x 16.5 x 2e-07 mm, 1 faces, 0 solids (baked)
FEATURE [Part::Revolution] Revolve129  label="plugHousing049"
  Angle = 360
  Axis = (0,1,0)
  Base = (0,0,0)
  FaceMakerClass = Part::FaceMakerBullseye
  Placement = pos=(0,0,36.15) rot=(0,0,1;0rad)
  Solid = false
  Source = -> Face125
  Symmetric = false
FEATURE [Part::Feature] Face126
  shape: bbox 10 x 16.5 x 2e-07 mm, 1 faces, 0 solids (baked)
FEATURE [Part::Revolution] Revolve131  label="plugHousing058"
  Angle = 360
  Axis = (0,1,0)
  Base = (0,0,0)
  FaceMakerClass = Part::FaceMakerBullseye
  Placement = pos=(0,0,36.15) rot=(0,0,1;0rad)
  Solid = false
  Source = -> Face120
  Symmetric = false
FEATURE [Part::MultiFuse] Fusion099  label="plugHousing053"
  Placement = pos=(0,0,0) rot=(0,0,1;1.5708rad)
  Shapes = -> [Revolve127,Revolve131]
FEATURE [Part::MultiFuse] Fusion102  label="plugHousing056"
  Placement = pos=(0,19,0) rot=(0,0,1;3.14159rad)
  Shapes = -> [Fusion100,Fusion099]
FEATURE [Part::Revolution] Revolve132  label="plugHousing059"
  Angle = 360
  Axis = (0,1,0)
  Base = (0,0,0)
  FaceMakerClass = Part::FaceMakerBullseye
  Placement = pos=(0,0,36.15) rot=(0,0,1;0rad)
  Solid = false
  Source = -> Face126
  Symmetric = false
FEATURE [Part::Revolution] Revolve133  label="plugHousing060"
  Angle = 360
  Axis = (0,1,0)
  Base = (0,0,0)
  FaceMakerClass = Part::FaceMakerBullseye
  Placement = pos=(0,0,36.15) rot=(0,0,1;0rad)
  Solid = false
  Source = -> Face122
  Symmetric = false
FEATURE [Part::MultiFuse] Fusion097  label="plugHousing051"
  Placement = pos=(0,0,0) rot=(0,0,1;1.5708rad)
  Shapes = -> [Revolve133,Revolve132]
FEATURE [Part::Revolution] Revolve134  label="plugHousing061"
  Angle = 360
  Axis = (0,1,0)
  Base = (0,0,0)
  FaceMakerClass = Part::FaceMakerBullseye
  Placement = pos=(0,0,36.15) rot=(0,0,1;0rad)
  Solid = false
  Source = -> Face124
  Symmetric = false
FEATURE [Part::MultiFuse] Fusion101  label="plugHousing055"
  Placement = pos=(0,0,0) rot=(0,0,1;1.5708rad)
  Shapes = -> [Revolve129,Revolve134]
FEATURE [Part::MultiFuse] Fusion098  label="plugHousing052"
  Placement = pos=(0,19,0) rot=(0,0,1;3.14159rad)
  Shapes = -> [Fusion097,Fusion101]
FEATURE [Part::MultiFuse] Fusion103  label="plugHousing057"
  Placement = pos=(122.621,0,-0.15) rot=(0,0,1;0rad)
  Shapes = -> [Fusion102,Fusion098]
FEATURE [Part::Box] Box028  label="Cube015"
  AttacherType = Attacher::AttachEngine3D
  Height = 28
  Length = 3
  Placement = pos=(110.7,19,22) rot=(0,0,1;0rad)
  Width = 15.7
FEATURE [Part::Cylinder] Cylinder044
  Angle = 360
  AttacherType = Attacher::AttachEngine3D
  Height = 20
  Placement = pos=(0,0,36.15) rot=(0,0,1;0rad)
  Radius = 10.3
FEATURE [Part::Cylinder] Cylinder045
  Angle = 360
  AttacherType = Attacher::AttachEngine3D
  Height = 10
  Placement = pos=(0,0,36.15) rot=(0,0,1;0rad)
  Radius = 4
FEATURE [Part::MultiFuse] Fusion104  label="removeToCreteHoleForPlugHousing040"
  Placement = pos=(70,19,36) rot=(0,1,0;1.5708rad)
  Shapes = -> [Cylinder044,Cylinder045]
FEATURE [Part::Cut] Cut046  label="plugHousingTab003"
  Base = -> Box028
  Tool = -> Fusion104
FEATURE [Part::MultiFuse] Fusion105  label="plugHousing062"
  Shapes = -> [Fusion103,Cut046]
FEATURE [Part::Fillet] Fillet042
  Base = -> Fusion105
  Edges = 1 edges r=2: [Edge25]
FEATURE [Part::Fillet] Fillet043  label="plugHousing063"
  Base = -> Fillet042
  Edges = 1 edges r=2: [Edge8]
  Placement = pos=(7,0,0) rot=(0,0,1;0rad)
FEATURE [Part::Feature] Face127
  shape: bbox 10 x 16.5 x 2e-07 mm, 1 faces, 0 solids (baked)
FEATURE [Part::Feature] Face128
  shape: bbox 10 x 16.5 x 2e-07 mm, 1 faces, 0 solids (baked)
FEATURE [Part::Revolution] Revolve137  label="plugHousing070"
  Angle = 360
  Axis = (0,1,0)
  Base = (0,0,0)
  FaceMakerClass = Part::FaceMakerBullseye
  Placement = pos=(0,0,36.15) rot=(0,0,1;0rad)
  Solid = false
  Source = -> Face127
  Symmetric = false
FEATURE [Part::Revolution] Revolve140  label="plugHousing073"
  Angle = 360
  Axis = (0,1,0)
  Base = (0,0,0)
  FaceMakerClass = Part::FaceMakerBullseye
  Placement = pos=(0,0,36.15) rot=(0,0,1;0rad)
  Solid = false
  Source = -> Face128
  Symmetric = false
FEATURE [Part::Feature] Face129
  shape: bbox 10 x 16.5 x 2e-07 mm, 1 faces, 0 solids (baked)
FEATURE [Part::Revolution] Revolve138  label="plugHousing071"
  Angle = 360
  Axis = (0,1,0)
  Base = (0,0,0)
  FaceMakerClass = Part::FaceMakerBullseye
  Placement = pos=(0,0,36.15) rot=(0,0,1;0rad)
  Solid = false
  Source = -> Face129
  Symmetric = false
FEATURE [Part::Feature] Face130
  shape: bbox 10 x 16.5 x 2e-07 mm, 1 faces, 0 solids (baked)
FEATURE [Part::Revolution] Revolve139  label="plugHousing072"
  Angle = 360
  Axis = (0,1,0)
  Base = (0,0,0)
  FaceMakerClass = Part::FaceMakerBullseye
  Placement = pos=(0,0,36.15) rot=(0,0,1;0rad)
  Solid = false
  Source = -> Face130
  Symmetric = false
FEATURE [Part::Feature] Face131
  shape: bbox 10 x 16.5 x 2e-07 mm, 1 faces, 0 solids (baked)
FEATURE [Part::Revolution] Revolve135  label="plugHousing068"
  Angle = 360
  Axis = (0,1,0)
  Base = (0,0,0)
  FaceMakerClass = Part::FaceMakerBullseye
  Placement = pos=(0,0,36.15) rot=(0,0,1;0rad)
  Solid = false
  Source = -> Face131
  Symmetric = false
FEATURE [Part::MultiFuse] Fusion112  label="plugHousing078"
  Placement = pos=(0,0,0) rot=(0,0,1;1.5708rad)
  Shapes = -> [Revolve135,Revolve139]
FEATURE [Part::Feature] Face132
  shape: bbox 10 x 16.5 x 2e-07 mm, 1 faces, 0 solids (baked)
FEATURE [Part::Revolution] Revolve141  label="plugHousing074"
  Angle = 360
  Axis = (0,1,0)
  Base = (0,0,0)
  FaceMakerClass = Part::FaceMakerBullseye
  Placement = pos=(0,0,36.15) rot=(0,0,1;0rad)
  Solid = false
  Source = -> Face132
  Symmetric = false
FEATURE [Part::MultiFuse] Fusion110  label="plugHousing076"
  Placement = pos=(0,0,0) rot=(0,0,1;1.5708rad)
  Shapes = -> [Revolve141,Revolve140]
FEATURE [Part::Feature] Face133
  shape: bbox 10 x 16.5 x 2e-07 mm, 1 faces, 0 solids (baked)
FEATURE [Part::Revolution] Revolve136  label="plugHousing069"
  Angle = 360
  Axis = (0,1,0)
  Base = (0,0,0)
  FaceMakerClass = Part::FaceMakerBullseye
  Placement = pos=(0,0,36.15) rot=(0,0,1;0rad)
  Solid = false
  Source = -> Face133
  Symmetric = false
FEATURE [Part::MultiFuse] Fusion106  label="plugHousing064"
  Placement = pos=(0,0,0) rot=(0,0,1;1.5708rad)
  Shapes = -> [Revolve138,Revolve136]
FEATURE [Part::MultiFuse] Fusion108  label="plugHousing066"
  Placement = pos=(0,19,0) rot=(0,0,1;3.14159rad)
  Shapes = -> [Fusion106,Fusion112]
FEATURE [Part::Feature] Face134
  shape: bbox 10 x 16.5 x 2e-07 mm, 1 faces, 0 solids (baked)
FEATURE [Part::Revolution] Revolve142  label="plugHousing075"
  Angle = 360
  Axis = (0,1,0)
  Base = (0,0,0)
  FaceMakerClass = Part::FaceMakerBullseye
  Placement = pos=(0,0,36.15) rot=(0,0,1;0rad)
  Solid = false
  Source = -> Face134
  Symmetric = false
FEATURE [Part::MultiFuse] Fusion107  label="plugHousing065"
  Placement = pos=(0,0,0) rot=(0,0,1;1.5708rad)
  Shapes = -> [Revolve137,Revolve142]
FEATURE [Part::MultiFuse] Fusion111  label="plugHousing077"
  Placement = pos=(0,19,0) rot=(0,0,1;3.14159rad)
  Shapes = -> [Fusion110,Fusion107]
FEATURE [Part::MultiFuse] Fusion109  label="plugHousing067"
  Placement = pos=(131.236,0,-0.15) rot=(0,0,1;0rad)
  Shapes = -> [Fusion108,Fusion111]
FEATURE [Part::MultiFuse] Fusion113  label="plugHousing079"
  Shapes = -> [Fillet043,Fusion109]
FEATURE [Part::Feature] Face135
  shape: bbox 3.5 x 17.8 x 2e-07 mm, 1 faces, 0 solids (baked)
FEATURE [Part::Revolution] Revolve143  label="removeToCreateScrewAndThreadedInsertHole049"
  Angle = 360
  Axis = (0,1,0)
  Base = (0,0,0)
  FaceMakerClass = Part::FaceMakerBullseye
  Placement = pos=(12.5,0,10) rot=(0,0,1;0rad)
  Solid = false
  Source = -> Face135
  Symmetric = false
FEATURE [Part::Feature] Face136
  shape: bbox 3.5 x 17.8 x 2e-07 mm, 1 faces, 0 solids (baked)
FEATURE [Part::Revolution] Revolve144  label="removeToCreateScrewAndThreadedInsertHole050"
  Angle = 360
  Axis = (0,1,0)
  Base = (0,0,0)
  FaceMakerClass = Part::FaceMakerBullseye
  Placement = pos=(12.5,0,62) rot=(0,0,1;0rad)
  Solid = false
  Source = -> Face136
  Symmetric = false
FEATURE [Part::Feature] Face137
  shape: bbox 3.5 x 17.8 x 2e-07 mm, 1 faces, 0 solids (baked)
FEATURE [Part::Revolution] Revolve145  label="removeToCreateScrewAndThreadedInsertHole051"
  Angle = 360
  Axis = (0,1,0)
  Base = (0,0,0)
  FaceMakerClass = Part::FaceMakerBullseye
  Placement = pos=(89.5,0,68.5) rot=(0,0,1;0rad)
  Solid = false
  Source = -> Face137
  Symmetric = false
FEATURE [Part::Feature] Face138
  shape: bbox 3.5 x 17.8 x 2e-07 mm, 1 faces, 0 solids (baked)
FEATURE [Part::Revolution] Revolve146  label="removeToCreateScrewAndThreadedInsertHole052"
  Angle = 360
  Axis = (0,1,0)
  Base = (0,0,0)
  FaceMakerClass = Part::FaceMakerBullseye
  Placement = pos=(89.5,0,3.5) rot=(0,0,1;0rad)
  Solid = false
  Source = -> Face138
  Symmetric = false
FEATURE [Part::Feature] Face139
  shape: bbox 3.5 x 17.8 x 2e-07 mm, 1 faces, 0 solids (baked)
FEATURE [Part::Revolution] Revolve147  label="removeToCreateScrewAndThreadedInsertHole053"
  Angle = 360
  Axis = (0,1,0)
  Base = (0,0,0)
  FaceMakerClass = Part::FaceMakerBullseye
  Placement = pos=(109.5,4.7,3.5) rot=(0,0,1;0rad)
  Solid = false
  Source = -> Face139
  Symmetric = false
FEATURE [Part::Feature] Face140
  shape: bbox 3.5 x 17.8 x 2e-07 mm, 1 faces, 0 solids (baked)
FEATURE [Part::Revolution] Revolve148  label="removeToCreateScrewAndThreadedInsertHole054"
  Angle = 360
  Axis = (0,1,0)
  Base = (0,0,0)
  FaceMakerClass = Part::FaceMakerBullseye
  Placement = pos=(109.5,4.7,68.5) rot=(0,0,1;0rad)
  Solid = false
  Source = -> Face140
  Symmetric = false
FEATURE [Part::MultiFuse] Fusion114  label="removeToCreateScrewAndThreadedInsertHole055"
  Shapes = -> [Revolve148,Revolve147,Revolve146,Revolve145,Revolve144,Revolve143]
FEATURE [Part::Cut] Cut047  label="casePillars004"
  Base = -> Cut037
  Tool = -> Fusion114
FEATURE [Part::Feature] Face141
  shape: bbox 3.5 x 17.8 x 2e-07 mm, 1 faces, 0 solids (baked)
FEATURE [Part::Feature] Face142
  shape: bbox 3.5 x 17.8 x 2e-07 mm, 1 faces, 0 solids (baked)
FEATURE [Part::Feature] Face143
  shape: bbox 3.5 x 17.8 x 2e-07 mm, 1 faces, 0 solids (baked)
FEATURE [Part::Revolution] Revolve149  label="removeToCreateScrewAndThreadedInsertHole057"
  Angle = 360
  Axis = (0,1,0)
  Base = (0,0,0)
  FaceMakerClass = Part::FaceMakerBullseye
  Placement = pos=(12.5,0,10) rot=(0,0,1;0rad)
  Solid = false
  Source = -> Face141
  Symmetric = false
FEATURE [Part::Feature] Face144
  shape: bbox 3.5 x 17.8 x 2e-07 mm, 1 faces, 0 solids (baked)
FEATURE [Part::Feature] Face145
  shape: bbox 3.5 x 17.8 x 2e-07 mm, 1 faces, 0 solids (baked)
FEATURE [Part::Feature] Face146
  shape: bbox 3.5 x 17.8 x 2e-07 mm, 1 faces, 0 solids (baked)
FEATURE [Part::Revolution] Revolve150  label="removeToCreateScrewAndThreadedInsertHole058"
  Angle = 360
  Axis = (0,1,0)
  Base = (0,0,0)
  FaceMakerClass = Part::FaceMakerBullseye
  Placement = pos=(12.5,0,62) rot=(0,0,1;0rad)
  Solid = false
  Source = -> Face146
  Symmetric = false
FEATURE [Part::Revolution] Revolve151  label="removeToCreateScrewAndThreadedInsertHole059"
  Angle = 360
  Axis = (0,1,0)
  Base = (0,0,0)
  FaceMakerClass = Part::FaceMakerBullseye
  Placement = pos=(89.5,0,68.5) rot=(0,0,1;0rad)
  Solid = false
  Source = -> Face143
  Symmetric = false
FEATURE [Part::Revolution] Revolve152  label="removeToCreateScrewAndThreadedInsertHole060"
  Angle = 360
  Axis = (0,1,0)
  Base = (0,0,0)
  FaceMakerClass = Part::FaceMakerBullseye
  Placement = pos=(89.5,0,3.5) rot=(0,0,1;0rad)
  Solid = false
  Source = -> Face142
  Symmetric = false
FEATURE [Part::Revolution] Revolve153  label="removeToCreateScrewAndThreadedInsertHole061"
  Angle = 360
  Axis = (0,1,0)
  Base = (0,0,0)
  FaceMakerClass = Part::FaceMakerBullseye
  Placement = pos=(109.5,4.7,3.5) rot=(0,0,1;0rad)
  Solid = false
  Source = -> Face145
  Symmetric = false
FEATURE [Part::Revolution] Revolve154  label="removeToCreateScrewAndThreadedInsertHole062"
  Angle = 360
  Axis = (0,1,0)
  Base = (0,0,0)
  FaceMakerClass = Part::FaceMakerBullseye
  Placement = pos=(109.5,4.7,68.5) rot=(0,0,1;0rad)
  Solid = false
  Source = -> Face144
  Symmetric = false
FEATURE [Part::MultiFuse] Fusion115  label="removeToCreateScrewAndThreadedInsertHole056"
  Shapes = -> [Revolve154,Revolve153,Revolve152,Revolve151,Revolve150,Revolve149]
FEATURE [Part::Feature] Face147
  shape: bbox 9.8 x 26.5 x 2e-07 mm, 1 faces, 0 solids (baked)
FEATURE [Part::Revolution] Revolve155
  Angle = 360
  Axis = (0,1,0)
  Base = (0,0,0)
  FaceMakerClass = Part::FaceMakerBullseye
  Placement = pos=(0,0,0) rot=(0,0,1;1.5708rad)
  Solid = false
  Source = -> Face147
  Symmetric = false
FEATURE [Part::Feature] Face148
  shape: bbox 9.8 x 26.5 x 2e-07 mm, 1 faces, 0 solids (baked)
FEATURE [Part::Revolution] Revolve156
  Angle = 360
  Axis = (0,1,0)
  Base = (0,0,0)
  FaceMakerClass = Part::FaceMakerBullseye
  Placement = pos=(0,0,0) rot=(0,0,1;1.5708rad)
  Solid = false
  Source = -> Face148
  Symmetric = false
FEATURE [Part::MultiFuse] Fusion116
  Placement = pos=(-18,19,36) rot=(0,0,1;0rad)
  Shapes = -> [Revolve156,Revolve155]
FEATURE [Part::Box] Box029  label="Cube016"
  AttacherType = Attacher::AttachEngine3D
  Height = 28
  Length = 3
  Placement = pos=(110.7,19,22) rot=(0,0,1;0rad)
  Width = 15.7
FEATURE [Part::Cylinder] Cylinder046
  Angle = 360
  AttacherType = Attacher::AttachEngine3D
  Height = 10
  Placement = pos=(0,0,36.15) rot=(0,0,1;0rad)
  Radius = 4
FEATURE [Part::Cylinder] Cylinder047
  Angle = 360
  AttacherType = Attacher::AttachEngine3D
  Height = 20
  Placement = pos=(0,0,36.15) rot=(0,0,1;0rad)
  Radius = 10.3
FEATURE [Part::MultiFuse] Fusion117  label="removeToCreteHoleForPlugHousing041"
  Placement = pos=(70,19,36) rot=(0,1,0;1.5708rad)
  Shapes = -> [Cylinder047,Cylinder046]
FEATURE [Part::Cut] Cut049  label="plugHousingTab004"
  Base = -> Box029
  Placement = pos=(-107.4,-14,0) rot=(0,0,1;0rad)
  Tool = -> Fusion117
FEATURE [Part::Box] Box030  label="Cube017"
  AttacherType = Attacher::AttachEngine3D
  Height = 28
  Length = 3
  Placement = pos=(110.7,19,22) rot=(0,0,1;0rad)
  Width = 15.7
FEATURE [Part::Cylinder] Cylinder048
  Angle = 360
  AttacherType = Attacher::AttachEngine3D
  Height = 10
  Placement = pos=(0,0,36.15) rot=(0,0,1;0rad)
  Radius = 4
FEATURE [Part::Cylinder] Cylinder049
  Angle = 360
  AttacherType = Attacher::AttachEngine3D
  Height = 20
  Placement = pos=(0,0,36.15) rot=(0,0,1;0rad)
  Radius = 10.3
FEATURE [Part::MultiFuse] Fusion118  label="removeToCreteHoleForPlugHousing042"
  Placement = pos=(70,19,36) rot=(0,1,0;1.5708rad)
  Shapes = -> [Cylinder049,Cylinder048]
FEATURE [Part::Cut] Cut050  label="plugHousingTab005"
  Base = -> Box030
  Placement = pos=(-107.4,-14,0) rot=(0,0,1;0rad)
  Tool = -> Fusion118
FEATURE [Part::MultiFuse] Fusion119
  Placement = pos=(9.6,23,0) rot=(0,0,1;3.14159rad)
  Shapes = -> [Cut049,Cut050]
FEATURE [Part::Box] Box031  label="Cube018"
  AttacherType = Attacher::AttachEngine3D
  Height = 10
  Length = 3
  Placement = pos=(3.3,4,12) rot=(0,0,1;0rad)
  Width = 10
FEATURE [Part::Fillet] Fillet044
  Base = -> Box031
  Edges = 1 edges r=2: [Edge11]
FEATURE [Part::Box] Box032  label="Cube019"
  AttacherType = Attacher::AttachEngine3D
  Height = 10
  Length = 3
  Placement = pos=(3.3,4,50) rot=(0,0,1;0rad)
  Width = 10
FEATURE [Part::Fillet] Fillet045
  Base = -> Box032
  Edges = 1 edges r=2: [Edge12]
FEATURE [Part::Box] Box033  label="Cube020"
  AttacherType = Attacher::AttachEngine3D
  Height = 28
  Length = 4
  Placement = pos=(5,0,22) rot=(0,0,1;0rad)
  Width = 10
FEATURE [Part::Fillet] Fillet046
  Base = -> Box033
  Edges = 1 edges r=1: [Edge7]
FEATURE [Part::Fillet] Fillet047
  Base = -> Fillet046
  Edges = 1 edges r=2: [Edge5]
FEATURE [Part::Fillet] Fillet048
  Base = -> Fillet047
  Edges = 1 edges r=2: [Edge2]
FEATURE [Part::Cylinder] Cylinder050
  Angle = 360
  AttacherType = Attacher::AttachEngine3D
  Height = 20
  Placement = pos=(0,0,36.15) rot=(0,0,1;0rad)
  Radius = 8.2
FEATURE [Part::Cylinder] Cylinder051
  Angle = 360
  AttacherType = Attacher::AttachEngine3D
  Height = 10
  Placement = pos=(0,0,36.15) rot=(0,0,1;0rad)
  Radius = 4
FEATURE [Part::MultiFuse] Fusion120  label="removeToCreteHoleForPlugHousing043"
  Placement = pos=(-42,19,36) rot=(0,1,0;1.5708rad)
  Shapes = -> [Cylinder050,Cylinder051]
FEATURE [Sketcher::SketchObject] Sketch067  label="topSketch018"
  FullyConstrained = true
  sketch-geometry (4):
    g0: LineSegment StartX=16.8446 StartY=31.512 StartZ=0 EndX=16.3251 EndY=34.4666 EndZ=0
    g1: ArcOfCircle CenterX=19 CenterY=19.2524 CenterZ=0 NormalX=0 NormalY=0 NormalZ=1 AngleXU=0 Radius=15.4476 StartAngle=1.74483 EndAngle=2.72717
    g2: ArcOfCircle CenterX=19 CenterY=19.2524 CenterZ=0 NormalX=0 NormalY=0 NormalZ=1 AngleXU=0 Radius=12.4476 StartAngle=1.74483 EndAngle=2.73189
    g3: LineSegment StartX=4.86004 StartY=25.4725 StartZ=0 EndX=7.58253 EndY=24.2107 EndZ=0
  constraints (7):
    c: Block(g0)
    c: Coincident(g1,g0)
    c: Coincident(g2,g0)
    c: Coincident(g3,g1)
    c: Coincident(g3,g2)
    c: Block(g1)
    c: Block(g2)
FEATURE [Part::Extrusion] Extrude058
  Base = -> Sketch067
  Dir = (0,0,1)
  DirMode = 2
  FaceMakerClass = Part::FaceMakerBullseye
  LengthFwd = 10
  LengthRev = 0
  Placement = pos=(0,0,31) rot=(0,0,1;0rad)
  Solid = true
  Symmetric = false
FEATURE [Part::Cut] Cut051
  Base = -> Extrude058
  Tool = -> Fusion120
FEATURE [Part::Fillet] Fillet049
  Base = -> Cut051
  Edges = 1 edges r=2: [Edge1]
FEATURE [Part::Fillet] Fillet050
  Base = -> Fillet049
  Edges = 1 edges r=2.5: [Edge1]
FEATURE [Part::Fillet] Fillet051
  Base = -> Fillet050
  Edges = 1 edges r=2.5: [Edge2]
FEATURE [Part::MultiFuse] Fusion121  label="wireHolder003"
  Shapes = -> [Fusion116,Fillet051]
FEATURE [Part::MultiFuse] Fusion122
  Shapes = -> [Fillet045,Fusion121]
FEATURE [Part::MultiFuse] Fusion123  label="wireHolder004"
  Shapes = -> [Fusion122,Fillet048]
FEATURE [Part::MultiFuse] Fusion124  label="wireHolder005"
  Shapes = -> [Fillet044,Fusion119,Fusion123]
FEATURE [Sketcher::SketchObject] Sketch068  label="topSketch019"
  FullyConstrained = true
  sketch-geometry (6):
    g0: LineSegment StartX=19 StartY=38 StartZ=0 EndX=117 EndY=38 EndZ=0
    g1: ArcOfCircle CenterX=19 CenterY=19 CenterZ=0 NormalX=0 NormalY=0 NormalZ=1 AngleXU=0 Radius=19 StartAngle=1.5708 EndAngle=3.14159
    g2: LineSegment StartX=117 StartY=38 StartZ=0 EndX=117 EndY=19 EndZ=0
    g3: LineSegment StartX=98 StartY=1.0161e-12 StartZ=0 EndX=5.22862e-06 EndY=1.0161e-12 EndZ=0
    g4: LineSegment StartX=5.22862e-06 StartY=19 StartZ=0 EndX=5.22862e-06 EndY=1.0161e-12 EndZ=0
    g5: ArcOfCircle CenterX=98 CenterY=19 CenterZ=0 NormalX=0 NormalY=0 NormalZ=1 AngleXU=0 Radius=19 StartAngle=4.71239 EndAngle=6.28319
  constraints (16):
    c: Horizontal(g0)
    c: Distance(g0) = 98
    c: Coincident(g1,g0)
    c: Block(g1)
    c: Coincident(g2,g0)
    c: Vertical(g2)
    c: Distance(g2) = 19
    c: Horizontal(g3)
    c: Coincident(g4,g1)
    c: Vertical(g4)
    c: Coincident(g3,g4)
    c: Block(g3)
    c: Coincident(g5,g2)
    c: Coincident(g5,g3)
    c: Block(g0)
    c: Block(g5)
FEATURE [Part::Extrusion] Extrude059  label="sideA002"
  Base = -> Sketch068
  Dir = (0,0,1)
  DirMode = 2
  FaceMakerClass = Part::FaceMakerBullseye
  LengthFwd = 3
  LengthRev = 0
  Placement = pos=(0,0,-2.7) rot=(0,0,1;0rad)
  Solid = true
  Symmetric = false
FEATURE [Sketcher::SketchObject] Sketch069  label="topSketch020"
  FullyConstrained = true
  sketch-geometry (6):
    g0: LineSegment StartX=19 StartY=38 StartZ=0 EndX=117 EndY=38 EndZ=0
    g1: ArcOfCircle CenterX=19 CenterY=19 CenterZ=0 NormalX=0 NormalY=0 NormalZ=1 AngleXU=0 Radius=19 StartAngle=1.5708 EndAngle=3.14159
    g2: LineSegment StartX=117 StartY=38 StartZ=0 EndX=117 EndY=19 EndZ=0
    g3: LineSegment StartX=98 StartY=1.0161e-12 StartZ=0 EndX=5.22862e-06 EndY=1.0161e-12 EndZ=0
    g4: LineSegment StartX=5.22862e-06 StartY=19 StartZ=0 EndX=5.22862e-06 EndY=1.0161e-12 EndZ=0
    g5: ArcOfCircle CenterX=98 CenterY=19 CenterZ=0 NormalX=0 NormalY=0 NormalZ=1 AngleXU=0 Radius=19 StartAngle=4.71239 EndAngle=6.28319
  constraints (16):
    c: Horizontal(g0)
    c: Distance(g0) = 98
    c: Coincident(g1,g0)
    c: Block(g1)
    c: Coincident(g2,g0)
    c: Vertical(g2)
    c: Distance(g2) = 19
    c: Horizontal(g3)
    c: Coincident(g4,g1)
    c: Vertical(g4)
    c: Coincident(g3,g4)
    c: Block(g3)
    c: Coincident(g5,g2)
    c: Coincident(g5,g3)
    c: Block(g0)
    c: Block(g5)
FEATURE [Part::Extrusion] Extrude060  label="sideB002"
  Base = -> Sketch069
  Dir = (0,0,1)
  DirMode = 2
  FaceMakerClass = Part::FaceMakerBullseye
  LengthFwd = 3
  LengthRev = 0
  Placement = pos=(0,0,71.7) rot=(0,0,1;0rad)
  Solid = true
  Symmetric = false
FEATURE [Part::MultiFuse] Fusion127  label="removeFromBottom001"
  Placement = pos=(2,0,0) rot=(0,0,1;0rad)
  Shapes = -> [Extrude059,Extrude060]
FEATURE [Part::Cylinder] Cylinder052
  Angle = 360
  AttacherType = Attacher::AttachEngine3D
  Height = 20
  Placement = pos=(0,0,36.15) rot=(0,0,1;0rad)
  Radius = 14
FEATURE [Part::Cylinder] Cylinder053
  Angle = 360
  AttacherType = Attacher::AttachEngine3D
  Height = 10
  Placement = pos=(0,0,36.15) rot=(0,0,1;0rad)
  Radius = 4
FEATURE [Part::MultiFuse] Fusion128  label="removeToCreteHoleForPlugHousing044"
  Placement = pos=(70,19,36) rot=(0,1,0;1.5708rad)
  Shapes = -> [Cylinder052,Cylinder053]
FEATURE [Part::Cut] Cut052  label="bottom011"
  Base = -> Extrude043
  Tool = -> Fusion128
FEATURE [Part::Cut] Cut054  label="bottom012"
  Base = -> Cut052
  Tool = -> Fusion115
FEATURE [Sketcher::SketchObject] Sketch070
  FullyConstrained = true
  Placement = pos=(117,19,0) rot=(0.57735,0.57735,0.57735;2.0944rad)
  sketch-geometry (48):
    g0: LineSegment StartX=-49.19 StartY=69.25 StartZ=0 EndX=-49.19 EndY=66.25 EndZ=0
    g1: LineSegment StartX=-49.19 StartY=63.5 StartZ=0 EndX=-49.19 EndY=60.5 EndZ=0
    g2: LineSegment StartX=-49.19 StartY=57.75 StartZ=0 EndX=-49.19 EndY=54.75 EndZ=0
    g3: LineSegment StartX=-49.19 StartY=52 StartZ=0 EndX=-49.19 EndY=49 EndZ=0
    g4: LineSegment StartX=-49.19 StartY=46.25 StartZ=0 EndX=-49.19 EndY=43.25 EndZ=0
    g5: LineSegment StartX=-49.19 StartY=40.5 StartZ=0 EndX=-49.19 EndY=37.5 EndZ=0
    g6: LineSegment StartX=-49.19 StartY=34.5 StartZ=0 EndX=-49.19 EndY=31.5 EndZ=0
    g7: LineSegment StartX=-49.19 StartY=28.75 StartZ=0 EndX=-49.19 EndY=25.75 EndZ=0
    g8: LineSegment StartX=-49.19 StartY=23 StartZ=0 EndX=-49.19 EndY=20 EndZ=0
    g9: LineSegment StartX=-49.19 StartY=17.25 StartZ=0 EndX=-49.19 EndY=14.25 EndZ=0
    g10: LineSegment StartX=-49.19 StartY=11.5 StartZ=0 EndX=-49.19 EndY=8.5 EndZ=0
    g11: LineSegment StartX=-49.19 StartY=5.75 StartZ=0 EndX=-49.19 EndY=2.75 EndZ=0
    g12: ArcOfCircle CenterX=-1.5 CenterY=67.75 CenterZ=0 NormalX=0 NormalY=0 NormalZ=1 AngleXU=0 Radius=1.5 StartAngle=4.71239 EndAngle=7.85398
    g13: ArcOfCircle CenterX=-1.5 CenterY=62 CenterZ=0 NormalX=0 NormalY=0 NormalZ=1 AngleXU=0 Radius=1.5 StartAngle=4.71239 EndAngle=7.85398
    g14: ArcOfCircle CenterX=-1.5 CenterY=56.25 CenterZ=0 NormalX=0 NormalY=0 NormalZ=1 AngleXU=0 Radius=1.5 StartAngle=4.71239 EndAngle=7.85398
    g15: ArcOfCircle CenterX=-11.49 CenterY=50.5 CenterZ=0 NormalX=0 NormalY=0 NormalZ=1 AngleXU=0 Radius=1.5 StartAngle=4.71239 EndAngle=7.85398
    g16: ArcOfCircle CenterX=-16.28 CenterY=44.75 CenterZ=0 NormalX=0 NormalY=0 NormalZ=1 AngleXU=0 Radius=1.5 StartAngle=4.71239 EndAngle=7.85398
    g17: ArcOfCircle CenterX=-18.2337 CenterY=39 CenterZ=0 NormalX=0 NormalY=0 NormalZ=1 AngleXU=0 Radius=1.5 StartAngle=4.71485 EndAngle=7.85398
    g18: ArcOfCircle CenterX=-16.2837 CenterY=27.25 CenterZ=0 NormalX=0 NormalY=0 NormalZ=1 AngleXU=0 Radius=1.5 StartAngle=4.71485 EndAngle=7.85398
    g19: ArcOfCircle CenterX=-18.2337 CenterY=33 CenterZ=0 NormalX=0 NormalY=0 NormalZ=1 AngleXU=0 Radius=1.5 StartAngle=4.71485 EndAngle=7.85398
    g20: ArcOfCircle CenterX=-11.49 CenterY=21.5 CenterZ=0 NormalX=0 NormalY=0 NormalZ=1 AngleXU=0 Radius=1.5 StartAngle=4.71239 EndAngle=7.85398
    g21: ArcOfCircle CenterX=-1.5 CenterY=4.25 CenterZ=0 NormalX=0 NormalY=0 NormalZ=1 AngleXU=0 Radius=1.5 StartAngle=4.71239 EndAngle=7.85398
    g22: ArcOfCircle CenterX=-1.5 CenterY=10 CenterZ=0 NormalX=0 NormalY=0 NormalZ=1 AngleXU=0 Radius=1.5 StartAngle=4.71239 EndAngle=7.85398
    g23: ArcOfCircle CenterX=-1.5 CenterY=15.75 CenterZ=0 NormalX=0 NormalY=0 NormalZ=1 AngleXU=0 Radius=1.5 StartAngle=4.71239 EndAngle=7.85398
    g24: LineSegment StartX=-49.19 StartY=69.25 StartZ=0 EndX=-1.5 EndY=69.25 EndZ=0
    g25: LineSegment StartX=-49.19 StartY=66.25 StartZ=0 EndX=-1.5 EndY=66.25 EndZ=0
    g26: LineSegment StartX=-49.19 StartY=63.5 StartZ=0 EndX=-1.5 EndY=63.5 EndZ=0
    g27: LineSegment StartX=-49.19 StartY=60.5 StartZ=0 EndX=-1.5 EndY=60.5 EndZ=0
    g28: LineSegment StartX=-49.19 StartY=57.75 StartZ=0 EndX=-1.5 EndY=57.75 EndZ=0
    g29: LineSegment StartX=-49.19 StartY=54.75 StartZ=0 EndX=-1.5 EndY=54.75 EndZ=0
    g30: LineSegment StartX=-49.19 StartY=52 StartZ=0 EndX=-11.49 EndY=52 EndZ=0
    g31: LineSegment StartX=-49.19 StartY=49 StartZ=0 EndX=-11.49 EndY=49 EndZ=0
    g32: LineSegment StartX=-49.19 StartY=46.25 StartZ=0 EndX=-16.28 EndY=46.25 EndZ=0
    g33: LineSegment StartX=-49.19 StartY=43.25 StartZ=0 EndX=-16.28 EndY=43.25 EndZ=0
    g34: LineSegment StartX=-49.19 StartY=40.5 StartZ=0 EndX=-18.2337 EndY=40.5 EndZ=0
    g35: LineSegment StartX=-49.19 StartY=37.5 StartZ=0 EndX=-18.23 EndY=37.5 EndZ=0
    g36: LineSegment StartX=-49.19 StartY=34.5 StartZ=0 EndX=-18.2337 EndY=34.5 EndZ=0
    g37: LineSegment StartX=-49.19 StartY=31.5 StartZ=0 EndX=-18.23 EndY=31.5 EndZ=0
    g38: LineSegment StartX=-49.19 StartY=28.75 StartZ=0 EndX=-16.2837 EndY=28.75 EndZ=0
    g39: LineSegment StartX=-49.19 StartY=25.75 StartZ=0 EndX=-16.28 EndY=25.75 EndZ=0
    g40: LineSegment StartX=-49.19 StartY=23 StartZ=0 EndX=-11.49 EndY=23 EndZ=0
    g41: LineSegment StartX=-49.19 StartY=20 StartZ=0 EndX=-11.49 EndY=20 EndZ=0
    g42: LineSegment StartX=-49.19 StartY=17.25 StartZ=0 EndX=-1.5 EndY=17.25 EndZ=0
    g43: LineSegment StartX=-49.19 StartY=14.25 StartZ=0 EndX=-1.5 EndY=14.25 EndZ=0
    g44: LineSegment StartX=-49.19 StartY=11.5 StartZ=0 EndX=-1.5 EndY=11.5 EndZ=0
    g45: LineSegment StartX=-49.19 StartY=8.5 StartZ=0 EndX=-1.5 EndY=8.5 EndZ=0
    g46: LineSegment StartX=-49.19 StartY=5.75 StartZ=0 EndX=-1.5 EndY=5.75 EndZ=0
    g47: LineSegment StartX=-49.19 StartY=2.75 StartZ=0 EndX=-1.5 EndY=2.75 EndZ=0
  constraints (120):
    c: Vertical(g0)
    c: Distance(g0) = 3
    c: Block(g0)
    c: Vertical(g1)
    c: Distance(g1) = 3
    c: Vertical(g2)
    c: Equal(g0,g2) = 3
    c: Block(g2)
    c: Vertical(g3)
    c: Equal(g1,g3) = 3
    c: Vertical(g4)
    c: Equal(g0,g4) = 3
    c: Block(g4)
    c: Vertical(g5)
    c: Equal(g1,g5) = 3
    c: Vertical(g6)
    c: Equal(g0,g6) = 3
    c: Block(g6)
    c: Vertical(g7)
    c: Equal(g1,g7) = 3
    c: Vertical(g8)
    c: Equal(g0,g8) = 3
    c: Block(g8)
    c: Vertical(g9)
    c: Equal(g1,g9) = 3
    c: Vertical(g10)
    c: Equal(g0,g10) = 3
    c: Block(g10)
    c: Vertical(g11)
    c: Equal(g1,g11) = 3
    c: Block(g12)
    c: Block(g13)
    c: Block(g14)
    c: Block(g15)
    c: Block(g16)
    c: Block(g17)
    c: Block(g18)
    c: Block(g19)
    c: Block(g20)
    c: Block(g21)
    c: Block(g22)
    c: Block(g23)
    c: Block(g11)
    c: Block(g9)
    c: Block(g7)
    c: Block(g5)
    c: Block(g3)
    c: Block(g1)
    c: Coincident(g24,g0)
    c: Coincident(g24,g12)
    c: Horizontal(g24)
    c: Coincident(g25,g0)
    c: Coincident(g25,g12)
    c: Horizontal(g25)
    c: Coincident(g26,g1)
    c: Coincident(g26,g13)
    c: Horizontal(g26)
    c: Coincident(g27,g1)
    c: Coincident(g27,g13)
    c: Horizontal(g27)
    c: Coincident(g28,g2)
    c: Coincident(g28,g14)
    c: Horizontal(g28)
    c: Coincident(g29,g2)
    c: Coincident(g29,g14)
    c: Horizontal(g29)
    c: Coincident(g30,g3)
    c: Coincident(g30,g15)
    c: Horizontal(g30)
    c: Coincident(g31,g3)
    c: Coincident(g31,g15)
    c: Horizontal(g31)
    c: Coincident(g32,g4)
    c: Coincident(g32,g16)
    c: Horizontal(g32)
    c: Coincident(g33,g4)
    c: Coincident(g33,g16)
    c: Horizontal(g33)
    c: Coincident(g34,g5)
    c: Coincident(g34,g17)
    c: Horizontal(g34)
    c: Coincident(g35,g5)
    c: Coincident(g35,g17)
    c: Horizontal(g35)
    c: Coincident(g36,g6)
    c: Coincident(g36,g19)
    c: Horizontal(g36)
    c: Coincident(g37,g6)
    c: Coincident(g37,g19)
    c: Horizontal(g37)
    c: Coincident(g38,g7)
    c: Coincident(g38,g18)
    c: Horizontal(g38)
    c: Coincident(g39,g7)
    c: Coincident(g39,g18)
    c: Horizontal(g39)
    c: Coincident(g40,g8)
    c: Coincident(g40,g20)
    c: Horizontal(g40)
    c: Coincident(g41,g8)
    c: Coincident(g41,g20)
    c: Horizontal(g41)
    c: Coincident(g42,g9)
    c: Coincident(g42,g23)
    c: Horizontal(g42)
    c: Coincident(g43,g9)
    c: Coincident(g43,g23)
    c: Horizontal(g43)
    c: Coincident(g44,g10)
    c: Coincident(g44,g22)
    c: Horizontal(g44)
    c: Coincident(g45,g10)
    c: Coincident(g45,g22)
    c: Horizontal(g45)
    c: Coincident(g46,g11)
    c: Coincident(g46,g21)
    c: Horizontal(g46)
    c: Coincident(g47,g11)
    c: Coincident(g47,g21)
    c: Horizontal(g47)
FEATURE [Part::Extrusion] Extrude061
  Base = -> Sketch070
  Dir = (1,0,0)
  DirMode = 2
  FaceMakerClass = Part::FaceMakerBullseye
  LengthFwd = 23
  LengthRev = 0
  Placement = pos=(-19,0,0) rot=(0,0,1;0rad)
  Solid = true
  Symmetric = false
FEATURE [Part::Fillet] Fillet052  label="removeToCreateVentalationHoles002"
  Base = -> Extrude061
  Edges = <same value as first occurrence — deduplicated (x6 in doc)>
  Placement = pos=(7,0.02,0) rot=(0,0,1;0rad)
FEATURE [Part::MultiFuse] Fusion130  label="bottom013"
  Shapes = -> [Cut054,Cut034]
FEATURE [Part::Cut] Cut055
  Base = -> Fusion130
  Tool = -> Fillet052
FEATURE [Part::Cylinder] Cylinder054
  Angle = 360
  AttacherType = Attacher::AttachEngine3D
  Height = 20
  Placement = pos=(0,0,36.15) rot=(0,0,1;0rad)
  Radius = 4
FEATURE [Sketcher::SketchObject] Sketch071  label="bottomSketch002"
  FullyConstrained = true
  sketch-geometry (32):
    g0: LineSegment StartX=3.3 StartY=-6.03275e-07 StartZ=0 EndX=98 EndY=-6.03275e-07 EndZ=0
    g1: ArcOfCircle CenterX=98 CenterY=19 CenterZ=0 NormalX=0 NormalY=0 NormalZ=1 AngleXU=0 Radius=19 StartAngle=4.71239 EndAngle=5.71103
    g2: LineSegment StartX=6.3 StartY=8 StartZ=0 EndX=3.3 EndY=8 EndZ=0
    g3: LineSegment StartX=3.3 StartY=8 StartZ=0 EndX=3.3 EndY=-6.03275e-07 EndZ=0
    g4: ArcOfCircle CenterX=8.3 CenterY=5 CenterZ=0 NormalX=0 NormalY=0 NormalZ=1 AngleXU=0 Radius=2 StartAngle=3.14159 EndAngle=4.71239
    g5: LineSegment StartX=6.3 StartY=8 StartZ=0 EndX=6.3 EndY=5 EndZ=0
    g6: ArcOfCircle CenterX=98 CenterY=19 CenterZ=0 NormalX=0 NormalY=0 NormalZ=1 AngleXU=0 Radius=12.7 StartAngle=4.71239 EndAngle=6.28319
    g7: LineSegment StartX=94.7 StartY=3 StartZ=0 EndX=8.3 EndY=3 EndZ=0
    g8-g12: Circle x5 (B-spline internal-alignment scaffolding for g13; pole/knot coordinates omitted)
    g13: BSplineCurve PolesCount=5 KnotsCount=3 Degree=3 IsPeriodic=0
    g14: GeomPoint X=98 Y=6.3 Z=0
    g15: GeomPoint X=96.3938 Y=4.71946 Z=0
    g16: GeomPoint X=94.7 Y=3 Z=0
    g17-g23: Circle x7 (B-spline internal-alignment scaffolding for g24; pole/knot coordinates omitted)
    g24: BSplineCurve PolesCount=7 KnotsCount=5 Degree=3 IsPeriodic=0
    g25-g29: GeomPoint x5 (B-spline internal-alignment scaffolding for g24; pole/knot coordinates omitted)
    g30: ArcOfCircle CenterX=98 CenterY=19 CenterZ=0 NormalX=0 NormalY=0 NormalZ=1 AngleXU=0 Radius=15.7 StartAngle=5.81226 EndAngle=6.28319
    g31: LineSegment StartX=110.7 StartY=19 StartZ=0 EndX=113.7 EndY=19 EndZ=0
  constraints (41):
    c: Horizontal(g0)
    c: Coincident(g1,g0)
    c: Block(g1)
    c: Horizontal(g2)
    c: Distance(g2) = 3
    c: Coincident(g3,g2)
    c: Vertical(g3)
    c: Coincident(g3,g0)
    c: Block(g4)
    c: Block(g2)
    c: Coincident(g5,g2)
    c: Coincident(g5,g4)
    c: Vertical(g5)
    c: Coincident(g6,g1)
    c: Block(g6)
    c: Coincident(g7,g4)
    c: Horizontal(g7)
    c: Block(g0)
    c: Block(g7)
    c: Block(g3)
    c: Coincident(g13,g6)
    c: Weight(g8) = 1
    c: Equal(g8, g9-g12) x4
    c: Coincident(g13,g7)
    c: InternalAlignment(g8-g12 -> g13) x5
    c: InternalAlignment(g14,g13)
    c: InternalAlignment(g15,g13)
    c: InternalAlignment(g16,g13)
    c: Block(g13)
    c: Weight(g17) = 1
    c: Equal(g17, g18-g23) x6
    c: Coincident(g24,g1)
    c: InternalAlignment(g17-g23 -> g24) x7
    c: InternalAlignment(g25-g29 -> g24) x5
    c: Block(g24)
    c: Coincident(g30,g24)
    c: Coincident(g31,g6)
    c: Coincident(g31,g30)
    c: Horizontal(g31)
    c: Block(g31)
    c: Block(g30)
FEATURE [Part::Extrusion] Extrude062  label="bottom014"
  Base = -> Sketch071
  Dir = (0,0,1)
  DirMode = 2
  FaceMakerClass = Part::FaceMakerBullseye
  LengthFwd = 71.4
  LengthRev = 0
  Placement = pos=(0,0,0.3) rot=(0,0,1;0rad)
  Solid = true
  Symmetric = false
FEATURE [Part::Fillet] Fillet054
  Base = -> Extrude062
  Edges = 1 edges r=2.4: [Edge17]
FEATURE [Part::Fillet] Fillet055  label="bottom015"
  Base = -> Fillet054
  Edges = 1 edges r=2.4: [Edge36]
FEATURE [Part::Cylinder] Cylinder055
  Angle = 360
  AttacherType = Attacher::AttachEngine3D
  Height = 10
  Placement = pos=(0,0,36.15) rot=(0,0,1;0rad)
  Radius = 4
FEATURE [Part::MultiFuse] Fusion131  label="removeToCreateHoleForPlugHousing002"
  Placement = pos=(70,19,36.15) rot=(0,1,0;1.5708rad)
  Shapes = -> [Cylinder054,Cylinder055]
FEATURE [Part::Cut] Cut056  label="Bottom001"
  Base = -> Fillet055
  Placement = pos=(9,0,0) rot=(0,0,1;0rad)
  Tool = -> Fusion131
FEATURE [Part::Cut] Cut057
  Base = -> Cut055
  Tool = -> Cut056
FEATURE [Sketcher::SketchObject] Sketch072  label="topSketch021"
  FullyConstrained = true
  sketch-geometry (4):
    g0: ArcOfCircle CenterX=105 CenterY=19 CenterZ=0 NormalX=0 NormalY=0 NormalZ=1 AngleXU=0 Radius=20.6155 StartAngle=5.54125 EndAngle=6.28319
    g1: ArcOfCircle CenterX=105 CenterY=19 CenterZ=0 NormalX=0 NormalY=0 NormalZ=1 AngleXU=0 Radius=13 StartAngle=5.54125 EndAngle=6.28319
    g2: LineSegment StartX=118 StartY=19 StartZ=0 EndX=125.616 EndY=19 EndZ=0
    g3: LineSegment StartX=114.583 StartY=10.2157 StartZ=0 EndX=120.197 EndY=5.06982 EndZ=0
  constraints (7):
    c: Block(g0)
    c: Block(g1)
    c: Coincident(g2,g1)
    c: Coincident(g2,g0)
    c: Horizontal(g2)
    c: Coincident(g3,g1)
    c: Coincident(g3,g0)
FEATURE [Part::Extrusion] Extrude063  label="bottomPlugHousingBit003"
  Base = -> Sketch072
  Dir = (0,0,1)
  DirMode = 2
  FaceMakerClass = Part::FaceMakerBullseye
  LengthFwd = 72
  LengthRev = 0
  Solid = true
  Symmetric = false
FEATURE [Part::Cylinder] Cylinder056
  Angle = 360
  AttacherType = Attacher::AttachEngine3D
  Height = 20
  Placement = pos=(0,0,36.15) rot=(0,0,1;0rad)
  Radius = 14.3
FEATURE [Part::Cylinder] Cylinder057
  Angle = 360
  AttacherType = Attacher::AttachEngine3D
  Height = 10
  Placement = pos=(0,0,36.15) rot=(0,0,1;0rad)
  Radius = 4
FEATURE [Part::Box] Box034  label="removeToCreteHoleForPlugHousing047"
  AttacherType = Attacher::AttachEngine3D
  Height = 28.6
  Length = 20
  Placement = pos=(106.15,0,21.7) rot=(0,0,1;0rad)
  Width = 19
FEATURE [Part::Cylinder] Cylinder058
  Angle = 360
  AttacherType = Attacher::AttachEngine3D
  Height = 20
  Placement = pos=(0,0,36.15) rot=(0,0,1;0rad)
  Radius = 14.3
FEATURE [Part::Cylinder] Cylinder059
  Angle = 360
  AttacherType = Attacher::AttachEngine3D
  Height = 10
  Placement = pos=(0,0,36.15) rot=(0,0,1;0rad)
  Radius = 4
FEATURE [Part::MultiFuse] Fusion134  label="removeToCreteHoleForPlugHousing046"
  Placement = pos=(70,19,36) rot=(0,1,0;1.5708rad)
  Shapes = -> [Cylinder058,Cylinder059]
FEATURE [Part::Cylinder] Cylinder060
  Angle = 360
  AttacherType = Attacher::AttachEngine3D
  Height = 20
  Placement = pos=(0,0,36.15) rot=(0,0,1;0rad)
  Radius = 14
FEATURE [Part::Cylinder] Cylinder061
  Angle = 360
  AttacherType = Attacher::AttachEngine3D
  Height = 10
  Placement = pos=(0,0,36.15) rot=(0,0,1;0rad)
  Radius = 4
FEATURE [Part::MultiFuse] Fusion135  label="removeToCreteHoleForPlugHousing048"
  Placement = pos=(70,19,36) rot=(0,1,0;1.5708rad)
  Shapes = -> [Cylinder060,Cylinder061]
FEATURE [Part::Box] Box035  label="removeToCreteHoleForPlugHousing049"
  AttacherType = Attacher::AttachEngine3D
  Height = 28.6
  Length = 20
  Placement = pos=(106.15,0,21.7) rot=(0,0,1;0rad)
  Width = 19
FEATURE [Part::MultiFuse] Fusion133  label="removeToCreteHoleForPlugHousing045"
  Placement = pos=(0,0,-28.3) rot=(0,0,1;0rad)
  Shapes = -> [Box035,Fusion134]
FEATURE [Part::MultiFuse] Fusion138  label="removeToCreteHoleForPlugHousing051"
  Placement = pos=(70,19,36) rot=(0,1,0;1.5708rad)
  Shapes = -> [Cylinder056,Cylinder057]
FEATURE [Part::MultiFuse] Fusion137  label="removeToCreteHoleForPlugHousing050"
  Placement = pos=(0,0,28.3) rot=(0,0,1;0rad)
  Shapes = -> [Box034,Fusion138]
FEATURE [Part::MultiFuse] Fusion132  label="removeToCreatePlugHousingBottomBit002"
  Shapes = -> [Fusion133,Fusion137]
FEATURE [Part::MultiFuse] Fusion136  label="removeToCreatePlugHousingBottomBit003"
  Shapes = -> [Fusion135,Fusion132]
FEATURE [Part::Cut] Cut058  label="bottomPlugHousingBit002"
  Base = -> Extrude063
  Placement = pos=(-0.09,0,0) rot=(0,0,1;0rad)
  Tool = -> Fusion136
FEATURE [Sketcher::SketchObject] Sketch073  label="bottomSketch003"
  FullyConstrained = true
  sketch-geometry (45):
    g0: LineSegment StartX=6.29999 StartY=8 StartZ=0 EndX=3.29999 EndY=8 EndZ=0
    g1: LineSegment StartX=3.29999 StartY=8 StartZ=0 EndX=3.29999 EndY=-6.03275e-07 EndZ=0
    g2: ArcOfCircle CenterX=8.29999 CenterY=5 CenterZ=0 NormalX=0 NormalY=0 NormalZ=1 AngleXU=0 Radius=2 StartAngle=3.14159 EndAngle=4.71239
    g3: LineSegment StartX=6.29999 StartY=8 StartZ=0 EndX=6.29999 EndY=5 EndZ=0
    g4: ArcOfCircle CenterX=105 CenterY=19 CenterZ=0 NormalX=0 NormalY=0 NormalZ=1 AngleXU=0 Radius=12.7 StartAngle=4.71239 EndAngle=5.94289
    g5-g11: Circle x7 (B-spline internal-alignment scaffolding for g12; pole/knot coordinates omitted)
    g12: BSplineCurve PolesCount=7 KnotsCount=5 Degree=3 IsPeriodic=0
    g13-g17: GeomPoint x5 (B-spline internal-alignment scaffolding for g12; pole/knot coordinates omitted)
    g18: ArcOfCircle CenterX=105 CenterY=19 CenterZ=0 NormalX=0 NormalY=0 NormalZ=1 AngleXU=0 Radius=15.7 StartAngle=5.81226 EndAngle=6.28319
    g19: BSplineCurve PolesCount=5 KnotsCount=3 Degree=3 IsPeriodic=0
    g20: LineSegment StartX=8.29999 StartY=3 StartZ=0 EndX=101.7 EndY=3 EndZ=0
    g21: LineSegment StartX=3.29999 StartY=-6.03275e-07 StartZ=0 EndX=105 EndY=-6.03275e-07 EndZ=0
    g22: LineSegment StartX=120.974 StartY=8.71251 StartZ=0 EndX=122.332 EndY=7.83778 EndZ=0
    g23: LineSegment StartX=105 StartY=-6.03274e-07 StartZ=0 EndX=113 EndY=-6.03274e-07 EndZ=0
    g24: ArcOfCircle CenterX=105 CenterY=19 CenterZ=0 NormalX=0 NormalY=0 NormalZ=1 AngleXU=0 Radius=20.6155 StartAngle=5.11091 EndAngle=5.71103
    g25: ArcOfCircle CenterX=117.7 CenterY=19 CenterZ=0 NormalX=0 NormalY=0 NormalZ=1 AngleXU=0 Radius=3 StartAngle=1.2e-15 EndAngle=2.10468
    g26: Circle CenterX=116.345 CenterY=16.3232 CenterZ=0 NormalX=0 NormalY=0 NormalZ=1 AngleXU=0 Radius=1
    g27: Circle CenterX=117.24 CenterY=15.7584 CenterZ=0 NormalX=0 NormalY=0 NormalZ=1 AngleXU=0 Radius=1
    g28: Circle CenterX=116.972 CenterY=14.7612 CenterZ=0 NormalX=0 NormalY=0 NormalZ=1 AngleXU=0 Radius=1
    g29: BSplineCurve PolesCount=3 KnotsCount=2 Degree=2 IsPeriodic=0
    g30: GeomPoint X=116.345 Y=16.3232 Z=0
    g31: GeomPoint X=116.972 Y=14.7612 Z=0
    g32: Circle CenterX=115.828 CenterY=17.157 CenterZ=0 NormalX=0 NormalY=0 NormalZ=1 AngleXU=0 Radius=1
    g33: Circle CenterX=115.841 CenterY=16.639 CenterZ=0 NormalX=0 NormalY=0 NormalZ=1 AngleXU=0 Radius=1
    g34: Circle CenterX=116.345 CenterY=16.3232 CenterZ=0 NormalX=0 NormalY=0 NormalZ=1 AngleXU=0 Radius=1
    g35: BSplineCurve PolesCount=3 KnotsCount=2 Degree=2 IsPeriodic=0
    g36: GeomPoint X=115.828 Y=17.157 Z=0
    g37: GeomPoint X=116.345 Y=16.3232 Z=0
    g38: LineSegment StartX=115.828 StartY=17.157 StartZ=0 EndX=115.828 EndY=20.8307 EndZ=0
    g39: Circle CenterX=115.828 CenterY=20.8307 CenterZ=0 NormalX=0 NormalY=0 NormalZ=1 AngleXU=0 Radius=1
    g40: Circle CenterX=115.831 CenterY=21.3396 CenterZ=0 NormalX=0 NormalY=0 NormalZ=1 AngleXU=0 Radius=1
    g41: Circle CenterX=116.173 CenterY=21.5825 CenterZ=0 NormalX=0 NormalY=0 NormalZ=1 AngleXU=0 Radius=1
    g42: BSplineCurve PolesCount=3 KnotsCount=2 Degree=2 IsPeriodic=0
    g43: GeomPoint X=115.828 Y=20.8307 Z=0
    g44: GeomPoint X=116.173 Y=21.5825 Z=0
  constraints (70):
    c: Horizontal(g0)
    c: Distance(g0) = 3
    c: Coincident(g1,g0)
    c: Vertical(g1)
    c: Block(g2)
    c: Block(g0)
    c: Coincident(g3,g0)
    c: Coincident(g3,g2)
    c: Vertical(g3)
    c: Block(g1)
    c: Block(g4)
    c: Coincident(g19,g4)
    c: Block(g19)
    c: Equal(g5, g6-g11) x6
    c: InternalAlignment(g5-g11 -> g12) x7
    c: InternalAlignment(g13-g17 -> g12) x5
    c: Block(g12)
    c: Coincident(g18,g12)
    c: Block(g18)
    c: Coincident(g20,g2)
    c: Coincident(g20,g19)
    c: Horizontal(g20)
    c: Distance(g20) = 93.4
    c: Coincident(g21,g1)
    c: Horizontal(g21)
    c: Distance(g21) = 101.7
    c: Horizontal(g23)
    c: Distance(g23) = 8
    c: Coincident(g24,g23)
    c: Block(g23)
    c: Coincident(g22,g24)
    c: Block(g24)
    c: Block(g22)
    c: Distance(g22) = 1.61553
    c: Coincident(g25,g18)
    c: Block(g25)
    c: Weight(g26) = 1
    c: Equal(g26,g27)
    c: Equal(g26,g28)
    c: Coincident(g29,g4)
    c: InternalAlignment(g26,g29)
    c: InternalAlignment(g27,g29)
    c: InternalAlignment(g28,g29)
    c: InternalAlignment(g30,g29)
    c: InternalAlignment(g31,g29)
    c: Block(g29)
    c: Weight(g32) = 1
    c: Equal(g32,g33)
    c: Equal(g32,g34)
    c: Coincident(g35,g29)
    c: InternalAlignment(g32,g35)
    c: InternalAlignment(g33,g35)
    c: InternalAlignment(g34,g35)
    c: InternalAlignment(g36,g35)
    c: InternalAlignment(g37,g35)
    c: Block(g35)
    c: Coincident(g38,g35)
    c: Vertical(g38)
    c: Block(g38)
    c: Coincident(g42,g38)
    c: Weight(g39) = 1
    c: Equal(g39,g40)
    c: Equal(g39,g41)
    c: Coincident(g42,g25)
    c: InternalAlignment(g39,g42)
    c: InternalAlignment(g40,g42)
    c: InternalAlignment(g41,g42)
    c: InternalAlignment(g43,g42)
    c: InternalAlignment(g44,g42)
    c: Block(g42)
FEATURE [Part::Extrusion] Extrude064  label="bottom016"
  Base = -> Sketch073
  Dir = (0,0,1)
  DirMode = 2
  FaceMakerClass = Part::FaceMakerBullseye
  LengthFwd = 71.4
  LengthRev = 0
  Placement = pos=(0,0,0.3) rot=(0,0,1;0rad)
  Solid = true
  Symmetric = false
FEATURE [Part::Revolution] Revolve157  label="removeToCreateScrewAndThreadedInsertHole063"
  Angle = 360
  Axis = (0,1,0)
  Base = (0,0,0)
  FaceMakerClass = Part::FaceMakerBullseye
  Placement = pos=(12.5,0,10) rot=(0,0,1;0rad)
  Solid = false
  Source = -> Face141
  Symmetric = false
FEATURE [Sketcher::SketchObject] Sketch074
  FullyConstrained = true
  Placement = pos=(117,19,0) rot=(0.57735,0.57735,0.57735;2.0944rad)
  sketch-geometry (48):
    g0: LineSegment StartX=-49.19 StartY=69.25 StartZ=0 EndX=-49.19 EndY=66.25 EndZ=0
    g1: LineSegment StartX=-49.19 StartY=63.5 StartZ=0 EndX=-49.19 EndY=60.5 EndZ=0
    g2: LineSegment StartX=-49.19 StartY=57.75 StartZ=0 EndX=-49.19 EndY=54.75 EndZ=0
    g3: LineSegment StartX=-49.19 StartY=52 StartZ=0 EndX=-49.19 EndY=49 EndZ=0
    g4: LineSegment StartX=-49.19 StartY=46.25 StartZ=0 EndX=-49.19 EndY=43.25 EndZ=0
    g5: LineSegment StartX=-49.19 StartY=40.5 StartZ=0 EndX=-49.19 EndY=37.5 EndZ=0
    g6: LineSegment StartX=-49.19 StartY=34.5 StartZ=0 EndX=-49.19 EndY=31.5 EndZ=0
    g7: LineSegment StartX=-49.19 StartY=28.75 StartZ=0 EndX=-49.19 EndY=25.75 EndZ=0
    g8: LineSegment StartX=-49.19 StartY=23 StartZ=0 EndX=-49.19 EndY=20 EndZ=0
    g9: LineSegment StartX=-49.19 StartY=17.25 StartZ=0 EndX=-49.19 EndY=14.25 EndZ=0
    g10: LineSegment StartX=-49.19 StartY=11.5 StartZ=0 EndX=-49.19 EndY=8.5 EndZ=0
    g11: LineSegment StartX=-49.19 StartY=5.75 StartZ=0 EndX=-49.19 EndY=2.75 EndZ=0
    g12: ArcOfCircle CenterX=-1.5 CenterY=67.75 CenterZ=0 NormalX=0 NormalY=0 NormalZ=1 AngleXU=0 Radius=1.5 StartAngle=4.71239 EndAngle=7.85398
    g13: ArcOfCircle CenterX=-1.5 CenterY=62 CenterZ=0 NormalX=0 NormalY=0 NormalZ=1 AngleXU=0 Radius=1.5 StartAngle=4.71239 EndAngle=7.85398
    g14: ArcOfCircle CenterX=-1.5 CenterY=56.25 CenterZ=0 NormalX=0 NormalY=0 NormalZ=1 AngleXU=0 Radius=1.5 StartAngle=4.71239 EndAngle=7.85398
    g15: ArcOfCircle CenterX=-11.49 CenterY=50.5 CenterZ=0 NormalX=0 NormalY=0 NormalZ=1 AngleXU=0 Radius=1.5 StartAngle=4.71239 EndAngle=7.85398
    g16: ArcOfCircle CenterX=-16.28 CenterY=44.75 CenterZ=0 NormalX=0 NormalY=0 NormalZ=1 AngleXU=0 Radius=1.5 StartAngle=4.71239 EndAngle=7.85398
    g17: ArcOfCircle CenterX=-18.2337 CenterY=39 CenterZ=0 NormalX=0 NormalY=0 NormalZ=1 AngleXU=0 Radius=1.5 StartAngle=4.71485 EndAngle=7.85398
    g18: ArcOfCircle CenterX=-16.2837 CenterY=27.25 CenterZ=0 NormalX=0 NormalY=0 NormalZ=1 AngleXU=0 Radius=1.5 StartAngle=4.71485 EndAngle=7.85398
    g19: ArcOfCircle CenterX=-18.2337 CenterY=33 CenterZ=0 NormalX=0 NormalY=0 NormalZ=1 AngleXU=0 Radius=1.5 StartAngle=4.71485 EndAngle=7.85398
    g20: ArcOfCircle CenterX=-11.49 CenterY=21.5 CenterZ=0 NormalX=0 NormalY=0 NormalZ=1 AngleXU=0 Radius=1.5 StartAngle=4.71239 EndAngle=7.85398
    g21: ArcOfCircle CenterX=-1.5 CenterY=4.25 CenterZ=0 NormalX=0 NormalY=0 NormalZ=1 AngleXU=0 Radius=1.5 StartAngle=4.71239 EndAngle=7.85398
    g22: ArcOfCircle CenterX=-1.5 CenterY=10 CenterZ=0 NormalX=0 NormalY=0 NormalZ=1 AngleXU=0 Radius=1.5 StartAngle=4.71239 EndAngle=7.85398
    g23: ArcOfCircle CenterX=-1.5 CenterY=15.75 CenterZ=0 NormalX=0 NormalY=0 NormalZ=1 AngleXU=0 Radius=1.5 StartAngle=4.71239 EndAngle=7.85398
    g24: LineSegment StartX=-49.19 StartY=69.25 StartZ=0 EndX=-1.5 EndY=69.25 EndZ=0
    g25: LineSegment StartX=-49.19 StartY=66.25 StartZ=0 EndX=-1.5 EndY=66.25 EndZ=0
    g26: LineSegment StartX=-49.19 StartY=63.5 StartZ=0 EndX=-1.5 EndY=63.5 EndZ=0
    g27: LineSegment StartX=-49.19 StartY=60.5 StartZ=0 EndX=-1.5 EndY=60.5 EndZ=0
    g28: LineSegment StartX=-49.19 StartY=57.75 StartZ=0 EndX=-1.5 EndY=57.75 EndZ=0
    g29: LineSegment StartX=-49.19 StartY=54.75 StartZ=0 EndX=-1.5 EndY=54.75 EndZ=0
    g30: LineSegment StartX=-49.19 StartY=52 StartZ=0 EndX=-11.49 EndY=52 EndZ=0
    g31: LineSegment StartX=-49.19 StartY=49 StartZ=0 EndX=-11.49 EndY=49 EndZ=0
    g32: LineSegment StartX=-49.19 StartY=46.25 StartZ=0 EndX=-16.28 EndY=46.25 EndZ=0
    g33: LineSegment StartX=-49.19 StartY=43.25 StartZ=0 EndX=-16.28 EndY=43.25 EndZ=0
    g34: LineSegment StartX=-49.19 StartY=40.5 StartZ=0 EndX=-18.2337 EndY=40.5 EndZ=0
    g35: LineSegment StartX=-49.19 StartY=37.5 StartZ=0 EndX=-18.23 EndY=37.5 EndZ=0
    g36: LineSegment StartX=-49.19 StartY=34.5 StartZ=0 EndX=-18.2337 EndY=34.5 EndZ=0
    g37: LineSegment StartX=-49.19 StartY=31.5 StartZ=0 EndX=-18.23 EndY=31.5 EndZ=0
    g38: LineSegment StartX=-49.19 StartY=28.75 StartZ=0 EndX=-16.2837 EndY=28.75 EndZ=0
    g39: LineSegment StartX=-49.19 StartY=25.75 StartZ=0 EndX=-16.28 EndY=25.75 EndZ=0
    g40: LineSegment StartX=-49.19 StartY=23 StartZ=0 EndX=-11.49 EndY=23 EndZ=0
    g41: LineSegment StartX=-49.19 StartY=20 StartZ=0 EndX=-11.49 EndY=20 EndZ=0
    g42: LineSegment StartX=-49.19 StartY=17.25 StartZ=0 EndX=-1.5 EndY=17.25 EndZ=0
    g43: LineSegment StartX=-49.19 StartY=14.25 StartZ=0 EndX=-1.5 EndY=14.25 EndZ=0
    g44: LineSegment StartX=-49.19 StartY=11.5 StartZ=0 EndX=-1.5 EndY=11.5 EndZ=0
    g45: LineSegment StartX=-49.19 StartY=8.5 StartZ=0 EndX=-1.5 EndY=8.5 EndZ=0
    g46: LineSegment StartX=-49.19 StartY=5.75 StartZ=0 EndX=-1.5 EndY=5.75 EndZ=0
    g47: LineSegment StartX=-49.19 StartY=2.75 StartZ=0 EndX=-1.5 EndY=2.75 EndZ=0
  constraints (120):
    c: Vertical(g0)
    c: Distance(g0) = 3
    c: Block(g0)
    c: Vertical(g1)
    c: Distance(g1) = 3
    c: Vertical(g2)
    c: Equal(g0,g2) = 3
    c: Block(g2)
    c: Vertical(g3)
    c: Equal(g1,g3) = 3
    c: Vertical(g4)
    c: Equal(g0,g4) = 3
    c: Block(g4)
    c: Vertical(g5)
    c: Equal(g1,g5) = 3
    c: Vertical(g6)
    c: Equal(g0,g6) = 3
    c: Block(g6)
    c: Vertical(g7)
    c: Equal(g1,g7) = 3
    c: Vertical(g8)
    c: Equal(g0,g8) = 3
    c: Block(g8)
    c: Vertical(g9)
    c: Equal(g1,g9) = 3
    c: Vertical(g10)
    c: Equal(g0,g10) = 3
    c: Block(g10)
    c: Vertical(g11)
    c: Equal(g1,g11) = 3
    c: Block(g12)
    c: Block(g13)
    c: Block(g14)
    c: Block(g15)
    c: Block(g16)
    c: Block(g17)
    c: Block(g18)
    c: Block(g19)
    c: Block(g20)
    c: Block(g21)
    c: Block(g22)
    c: Block(g23)
    c: Block(g11)
    c: Block(g9)
    c: Block(g7)
    c: Block(g5)
    c: Block(g3)
    c: Block(g1)
    c: Coincident(g24,g0)
    c: Coincident(g24,g12)
    c: Horizontal(g24)
    c: Coincident(g25,g0)
    c: Coincident(g25,g12)
    c: Horizontal(g25)
    c: Coincident(g26,g1)
    c: Coincident(g26,g13)
    c: Horizontal(g26)
    c: Coincident(g27,g1)
    c: Coincident(g27,g13)
    c: Horizontal(g27)
    c: Coincident(g28,g2)
    c: Coincident(g28,g14)
    c: Horizontal(g28)
    c: Coincident(g29,g2)
    c: Coincident(g29,g14)
    c: Horizontal(g29)
    c: Coincident(g30,g3)
    c: Coincident(g30,g15)
    c: Horizontal(g30)
    c: Coincident(g31,g3)
    c: Coincident(g31,g15)
    c: Horizontal(g31)
    c: Coincident(g32,g4)
    c: Coincident(g32,g16)
    c: Horizontal(g32)
    c: Coincident(g33,g4)
    c: Coincident(g33,g16)
    c: Horizontal(g33)
    c: Coincident(g34,g5)
    c: Coincident(g34,g17)
    c: Horizontal(g34)
    c: Coincident(g35,g5)
    c: Coincident(g35,g17)
    c: Horizontal(g35)
    c: Coincident(g36,g6)
    c: Coincident(g36,g19)
    c: Horizontal(g36)
    c: Coincident(g37,g6)
    c: Coincident(g37,g19)
    c: Horizontal(g37)
    c: Coincident(g38,g7)
    c: Coincident(g38,g18)
    c: Horizontal(g38)
    c: Coincident(g39,g7)
    c: Coincident(g39,g18)
    c: Horizontal(g39)
    c: Coincident(g40,g8)
    c: Coincident(g40,g20)
    c: Horizontal(g40)
    c: Coincident(g41,g8)
    c: Coincident(g41,g20)
    c: Horizontal(g41)
    c: Coincident(g42,g9)
    c: Coincident(g42,g23)
    c: Horizontal(g42)
    c: Coincident(g43,g9)
    c: Coincident(g43,g23)
    c: Horizontal(g43)
    c: Coincident(g44,g10)
    c: Coincident(g44,g22)
    c: Horizontal(g44)
    c: Coincident(g45,g10)
    c: Coincident(g45,g22)
    c: Horizontal(g45)
    c: Coincident(g46,g11)
    c: Coincident(g46,g21)
    c: Horizontal(g46)
    c: Coincident(g47,g11)
    c: Coincident(g47,g21)
    c: Horizontal(g47)
FEATURE [Part::Extrusion] Extrude065
  Base = -> Sketch074
  Dir = (1,0,0)
  DirMode = 2
  FaceMakerClass = Part::FaceMakerBullseye
  LengthFwd = 23
  LengthRev = 0
  Placement = pos=(-19,0,0) rot=(0,0,1;0rad)
  Solid = true
  Symmetric = false
FEATURE [Part::Fillet] Fillet056  label="removeToCreateVentalationHoles003"
  Base = -> Extrude065
  Edges = <same value as first occurrence — deduplicated (x6 in doc)>
  Placement = pos=(7,0.02,0) rot=(0,0,1;0rad)
FEATURE [Part::Revolution] Revolve158  label="removeToCreateScrewAndThreadedInsertHole065"
  Angle = 360
  Axis = (0,1,0)
  Base = (0,0,0)
  FaceMakerClass = Part::FaceMakerBullseye
  Placement = pos=(12.5,0,62) rot=(0,0,1;0rad)
  Solid = false
  Source = -> Face146
  Symmetric = false
FEATURE [Part::Revolution] Revolve159  label="removeToCreateScrewAndThreadedInsertHole066"
  Angle = 360
  Axis = (0,1,0)
  Base = (0,0,0)
  FaceMakerClass = Part::FaceMakerBullseye
  Placement = pos=(89.5,0,68.5) rot=(0,0,1;0rad)
  Solid = false
  Source = -> Face143
  Symmetric = false
FEATURE [Part::Revolution] Revolve160  label="removeToCreateScrewAndThreadedInsertHole067"
  Angle = 360
  Axis = (0,1,0)
  Base = (0,0,0)
  FaceMakerClass = Part::FaceMakerBullseye
  Placement = pos=(89.5,0,3.5) rot=(0,0,1;0rad)
  Solid = false
  Source = -> Face142
  Symmetric = false
FEATURE [Part::Revolution] Revolve161  label="removeToCreateScrewAndThreadedInsertHole068"
  Angle = 360
  Axis = (0,1,0)
  Base = (0,0,0)
  FaceMakerClass = Part::FaceMakerBullseye
  Placement = pos=(109.5,4.7,3.5) rot=(0,0,1;0rad)
  Solid = false
  Source = -> Face145
  Symmetric = false
FEATURE [Part::Revolution] Revolve162  label="removeToCreateScrewAndThreadedInsertHole069"
  Angle = 360
  Axis = (0,1,0)
  Base = (0,0,0)
  FaceMakerClass = Part::FaceMakerBullseye
  Placement = pos=(109.5,4.7,68.5) rot=(0,0,1;0rad)
  Solid = false
  Source = -> Face144
  Symmetric = false
FEATURE [Part::MultiFuse] Fusion141  label="removeToCreateScrewAndThreadedInsertHole064"
  Shapes = -> [Revolve162,Revolve161,Revolve160,Revolve159,Revolve158,Revolve157]
FEATURE [Part::Cylinder] Cylinder062
  Angle = 360
  AttacherType = Attacher::AttachEngine3D
  Height = 20
  Placement = pos=(0,0,36.15) rot=(0,0,1;0rad)
  Radius = 14
FEATURE [Part::Cylinder] Cylinder063
  Angle = 360
  AttacherType = Attacher::AttachEngine3D
  Height = 10
  Placement = pos=(0,0,36.15) rot=(0,0,1;0rad)
  Radius = 4
FEATURE [Part::MultiFuse] Fusion139  label="removeToCreteHoleForPlugHousing052"
  Placement = pos=(70,19,36) rot=(0,1,0;1.5708rad)
  Shapes = -> [Cylinder062,Cylinder063]
FEATURE [Part::Cut] Cut060  label="bottom017"
  Base = -> Extrude064
  Tool = -> Fusion139
FEATURE [Part::Cut] Cut061  label="bottom019"
  Base = -> Cut060
  Tool = -> Fusion141
FEATURE [Part::MultiFuse] Fusion140  label="bottom018"
  Shapes = -> [Cut061,Cut058]
FEATURE [Part::Cut] Cut059  label="bottom020"
  Base = -> Fusion140
  Tool = -> Fillet056
FEATURE [Part::Box] Box036  label="Cube021"
  AttacherType = Attacher::AttachEngine3D
  Height = 80
  Length = 26
  Placement = pos=(0,-1,-5) rot=(0,0,1;0rad)
  Width = 11
FEATURE [Part::Cut] Cut062  label="removeFromBottom002"
  Base = -> Cut057
  Tool = -> Box036
FEATURE [Part::Cut] Cut063
  Base = -> Cut059
  Tool = -> Cut062
FEATURE [Part::Cut] Cut064  label="pcbStands"
  Base = -> Fusion095
  Tool = -> Fusion127
FEATURE [Sketcher::SketchObject] Sketch075  label="topSketch022"
  FullyConstrained = true
  sketch-geometry (6):
    g0: LineSegment StartX=19 StartY=38 StartZ=0 EndX=117 EndY=38 EndZ=0
    g1: ArcOfCircle CenterX=19 CenterY=19 CenterZ=0 NormalX=0 NormalY=0 NormalZ=1 AngleXU=0 Radius=19 StartAngle=1.5708 EndAngle=3.14159
    g2: LineSegment StartX=117 StartY=38 StartZ=0 EndX=117 EndY=19 EndZ=0
    g3: LineSegment StartX=98 StartY=1.0161e-12 StartZ=0 EndX=5.22862e-06 EndY=1.0161e-12 EndZ=0
    g4: LineSegment StartX=5.22862e-06 StartY=19 StartZ=0 EndX=5.22862e-06 EndY=1.0161e-12 EndZ=0
    g5: ArcOfCircle CenterX=98 CenterY=19 CenterZ=0 NormalX=0 NormalY=0 NormalZ=1 AngleXU=0 Radius=19 StartAngle=4.71239 EndAngle=6.28319
  constraints (16):
    c: Horizontal(g0)
    c: Distance(g0) = 98
    c: Coincident(g1,g0)
    c: Block(g1)
    c: Coincident(g2,g0)
    c: Vertical(g2)
    c: Distance(g2) = 19
    c: Horizontal(g3)
    c: Coincident(g4,g1)
    c: Vertical(g4)
    c: Coincident(g3,g4)
    c: Block(g3)
    c: Coincident(g5,g2)
    c: Coincident(g5,g3)
    c: Block(g0)
    c: Block(g5)
FEATURE [Part::Extrusion] Extrude067  label="sideB003"
  Base = -> Sketch075
  Dir = (0,0,1)
  DirMode = 2
  FaceMakerClass = Part::FaceMakerBullseye
  LengthFwd = 3
  LengthRev = 0
  Placement = pos=(0,0,71.7) rot=(0,0,1;0rad)
  Solid = true
  Symmetric = false
FEATURE [Sketcher::SketchObject] Sketch076  label="topSketch023"
  FullyConstrained = true
  sketch-geometry (6):
    g0: LineSegment StartX=19 StartY=38 StartZ=0 EndX=117 EndY=38 EndZ=0
    g1: ArcOfCircle CenterX=19 CenterY=19 CenterZ=0 NormalX=0 NormalY=0 NormalZ=1 AngleXU=0 Radius=19 StartAngle=1.5708 EndAngle=3.14159
    g2: LineSegment StartX=117 StartY=38 StartZ=0 EndX=117 EndY=19 EndZ=0
    g3: LineSegment StartX=98 StartY=1.0161e-12 StartZ=0 EndX=5.22862e-06 EndY=1.0161e-12 EndZ=0
    g4: LineSegment StartX=5.22862e-06 StartY=19 StartZ=0 EndX=5.22862e-06 EndY=1.0161e-12 EndZ=0
    g5: ArcOfCircle CenterX=98 CenterY=19 CenterZ=0 NormalX=0 NormalY=0 NormalZ=1 AngleXU=0 Radius=19 StartAngle=4.71239 EndAngle=6.28319
  constraints (16):
    c: Horizontal(g0)
    c: Distance(g0) = 98
    c: Coincident(g1,g0)
    c: Block(g1)
    c: Coincident(g2,g0)
    c: Vertical(g2)
    c: Distance(g2) = 19
    c: Horizontal(g3)
    c: Coincident(g4,g1)
    c: Vertical(g4)
    c: Coincident(g3,g4)
    c: Block(g3)
    c: Coincident(g5,g2)
    c: Coincident(g5,g3)
    c: Block(g0)
    c: Block(g5)
FEATURE [Part::Extrusion] Extrude066  label="sideA003"
  Base = -> Sketch076
  Dir = (0,0,1)
  DirMode = 2
  FaceMakerClass = Part::FaceMakerBullseye
  LengthFwd = 3
  LengthRev = 0
  Placement = pos=(0,0,-2.7) rot=(0,0,1;0rad)
  Solid = true
  Symmetric = false
FEATURE [Part::MultiFuse] Fusion142  label="removeFromBottom003"
  Placement = pos=(2,0,0) rot=(0,0,1;0rad)
  Shapes = -> [Extrude066,Extrude067]
FEATURE [Part::Cut] Cut065  label="screwRetainers002"
  Base = -> Fusion096
  Tool = -> Fusion142
FEATURE [Sketcher::SketchObject] Sketch077
  FullyConstrained = true
  Placement = pos=(117,19,0) rot=(0.57735,0.57735,0.57735;2.0944rad)
  sketch-geometry (8):
    g0: LineSegment StartX=-49.19 StartY=63.5 StartZ=0 EndX=-49.19 EndY=60.5 EndZ=0
    g1: LineSegment StartX=-49.19 StartY=11.5 StartZ=0 EndX=-49.19 EndY=8.5 EndZ=0
    g2: ArcOfCircle CenterX=-1.5 CenterY=62 CenterZ=0 NormalX=0 NormalY=0 NormalZ=1 AngleXU=0 Radius=1.5 StartAngle=4.71239 EndAngle=7.85398
    g3: ArcOfCircle CenterX=-1.5 CenterY=10 CenterZ=0 NormalX=0 NormalY=0 NormalZ=1 AngleXU=0 Radius=1.5 StartAngle=4.71239 EndAngle=7.85398
    g4: LineSegment StartX=-49.19 StartY=63.5 StartZ=0 EndX=-1.5 EndY=63.5 EndZ=0
    g5: LineSegment StartX=-49.19 StartY=60.5 StartZ=0 EndX=-1.5 EndY=60.5 EndZ=0
    g6: LineSegment StartX=-49.19 StartY=11.5 StartZ=0 EndX=-1.5 EndY=11.5 EndZ=0
    g7: LineSegment StartX=-49.19 StartY=8.5 StartZ=0 EndX=-1.5 EndY=8.5 EndZ=0
  constraints (19):
    c: Vertical(g0)
    c: Distance(g0) = 3
    c: Vertical(g1)
    c: Block(g1)
    c: Block(g2)
    c: Block(g3)
    c: Block(g0)
    c: Coincident(g4,g0)
    c: Coincident(g4,g2)
    c: Horizontal(g4)
    c: Coincident(g5,g0)
    c: Coincident(g5,g2)
    c: Horizontal(g5)
    c: Coincident(g6,g1)
    c: Coincident(g6,g3)
    c: Horizontal(g6)
    c: Coincident(g7,g1)
    c: Coincident(g7,g3)
    c: Horizontal(g7)
FEATURE [Part::Extrusion] Extrude068
  Base = -> Sketch077
  Dir = (1,0,0)
  DirMode = 2
  FaceMakerClass = Part::FaceMakerBullseye
  LengthFwd = 10
  LengthRev = 0
  Solid = true
  Symmetric = false
FEATURE [Part::Fillet] Fillet057  label="removeFromtMoreFrontCaseScrewRetainers002"
  Base = -> Extrude068
  Edges = 4 edges r=1.49: [Edge6,Edge11,Edge18,Edge23]
  Placement = pos=(-12,0,0) rot=(0,0,1;0rad)
FEATURE [Sketcher::SketchObject] Sketch078
  FullyConstrained = true
  Placement = pos=(117,19,0) rot=(0.57735,0.57735,0.57735;2.0944rad)
  sketch-geometry (8):
    g0: LineSegment StartX=-49.19 StartY=69.25 StartZ=0 EndX=-49.19 EndY=66.25 EndZ=0
    g1: LineSegment StartX=-49.19 StartY=5.75 StartZ=0 EndX=-49.19 EndY=2.75 EndZ=0
    g2: ArcOfCircle CenterX=-1.5 CenterY=67.75 CenterZ=0 NormalX=0 NormalY=0 NormalZ=1 AngleXU=0 Radius=1.5 StartAngle=4.71239 EndAngle=7.85398
    g3: ArcOfCircle CenterX=-1.5 CenterY=4.25 CenterZ=0 NormalX=0 NormalY=0 NormalZ=1 AngleXU=0 Radius=1.5 StartAngle=4.71239 EndAngle=7.85398
    g4: LineSegment StartX=-49.19 StartY=69.25 StartZ=0 EndX=-1.5 EndY=69.25 EndZ=0
    g5: LineSegment StartX=-49.19 StartY=66.25 StartZ=0 EndX=-1.5 EndY=66.25 EndZ=0
    g6: LineSegment StartX=-49.19 StartY=5.75 StartZ=0 EndX=-1.5 EndY=5.75 EndZ=0
    g7: LineSegment StartX=-49.19 StartY=2.75 StartZ=0 EndX=-1.5 EndY=2.75 EndZ=0
  constraints (19):
    c: Vertical(g0)
    c: Distance(g0) = 3
    c: Block(g0)
    c: Vertical(g1)
    c: Block(g2)
    c: Block(g3)
    c: Block(g1)
    c: Coincident(g4,g0)
    c: Coincident(g4,g2)
    c: Horizontal(g4)
    c: Coincident(g5,g0)
    c: Coincident(g5,g2)
    c: Horizontal(g5)
    c: Coincident(g6,g1)
    c: Coincident(g6,g3)
    c: Horizontal(g6)
    c: Coincident(g7,g1)
    c: Coincident(g7,g3)
    c: Horizontal(g7)
FEATURE [Part::Extrusion] Extrude069
  Base = -> Sketch078
  Dir = (1,0,0)
  DirMode = 2
  FaceMakerClass = Part::FaceMakerBullseye
  LengthFwd = 10
  LengthRev = 0
  Solid = true
  Symmetric = false
FEATURE [Part::Fillet] Fillet058  label="removeFromtMoreFrontCaseScrewRetainers003"
  Base = -> Extrude069
  Edges = 4 edges r=1.49: [Edge6,Edge11,Edge18,Edge23]
  Placement = pos=(-4,0,0) rot=(0,0,1;0rad)
FEATURE [Part::Cut] Cut066
  Base = -> Cut065
  Tool = -> Fillet058
FEATURE [Part::Cut] Cut067  label="screwPillars"
  Base = -> Cut066
  Tool = -> Fillet057
FEATURE [Part::MultiFuse] Fusion143  label="bottom021"
  Shapes = -> [Cut031,Cut063]
FEATURE [Part::Cylinder] Cylinder
  Angle = 360
  AttacherType = Attacher::AttachEngine3D
  Height = 10
  Placement = pos=(20.65,12,4.68) rot=(1,0,0;1.5708rad)
  Radius = 2
FEATURE [Part::Cylinder] Cylinder064
  Angle = 360
  AttacherType = Attacher::AttachEngine3D
  Height = 10
  Placement = pos=(20.65,12,67.38) rot=(1,0,0;1.5708rad)
  Radius = 2
FEATURE [Part::Cylinder] Cylinder065
  Angle = 360
  AttacherType = Attacher::AttachEngine3D
  Height = 10
  Placement = pos=(77.15,12,67.38) rot=(1,0,0;1.5708rad)
  Radius = 2
FEATURE [Part::Cylinder] Cylinder066
  Angle = 360
  AttacherType = Attacher::AttachEngine3D
  Height = 10
  Placement = pos=(77.15,12,4.68) rot=(1,0,0;1.5708rad)
  Radius = 2
FEATURE [Part::MultiFuse] Fusion144  label="removeFromThreadedInsertHousing"
  Shapes = -> [Cylinder065,Cylinder064,Cylinder,Cylinder066]
FEATURE [Part::Cut] Cut068  label="pcbStands001"
  Base = -> Cut064
  Tool = -> Fusion144
FEATURE [Part::MultiFuse] Fusion145
  Shapes = -> [Cut068,Fusion143]
FEATURE [Part::MultiFuse] Fusion146
  Shapes = -> [Fusion145]
FEATURE [Part::MultiFuse] Fusion147  label="bottom022"
  Shapes = -> [Cut067,Fusion146]
FEATURE [Part::MultiFuse] Fusion148  label="casePillars005"
  Shapes = -> [Cut047,Fusion092]
FEATURE [Part::MultiFuse] Fusion149  label="bottom023"
  Shapes = -> [Fusion124,Fusion113,Fusion147]
FEATURE [Part::MultiFuse] Fusion150  label="topBits"
  Shapes = -> [Cut025,Fusion148,Cut030,Fillet034]
FEATURE [Part::Feature] Face149 .. Face152  x4 (patterned run collapsed; names and placements below)
  shape: bbox 3.2 x 1.5 x 2e-07 mm, 1 faces, 0 solids (baked)
FEATURE [Part::Feature] Face153
  shape: bbox 3.6 x 3.2 x 2e-07 mm, 1 faces, 0 solids (baked)
FEATURE [Part::Feature] Face154
  shape: bbox 3.6 x 3.2 x 2e-07 mm, 1 faces, 0 solids (baked)
FEATURE [Sketcher::SketchObject] Sketch079  label="topSketch024"
  FullyConstrained = true
  sketch-geometry (6):
    g0: LineSegment StartX=19 StartY=38 StartZ=0 EndX=117 EndY=38 EndZ=0
    g1: ArcOfCircle CenterX=19 CenterY=19 CenterZ=0 NormalX=0 NormalY=0 NormalZ=1 AngleXU=0 Radius=19 StartAngle=1.5708 EndAngle=3.14159
    g2: LineSegment StartX=117 StartY=38 StartZ=0 EndX=117 EndY=19 EndZ=0
    g3: LineSegment StartX=98 StartY=1.0161e-12 StartZ=0 EndX=5.22862e-06 EndY=1.0161e-12 EndZ=0
    g4: LineSegment StartX=5.22862e-06 StartY=19 StartZ=0 EndX=5.22862e-06 EndY=1.0161e-12 EndZ=0
    g5: ArcOfCircle CenterX=98 CenterY=19 CenterZ=0 NormalX=0 NormalY=0 NormalZ=1 AngleXU=0 Radius=19 StartAngle=4.71239 EndAngle=6.28319
  constraints (16):
    c: Horizontal(g0)
    c: Distance(g0) = 98
    c: Coincident(g1,g0)
    c: Block(g1)
    c: Coincident(g2,g0)
    c: Vertical(g2)
    c: Distance(g2) = 19
    c: Horizontal(g3)
    c: Coincident(g4,g1)
    c: Vertical(g4)
    c: Coincident(g3,g4)
    c: Block(g3)
    c: Coincident(g5,g2)
    c: Coincident(g5,g3)
    c: Block(g0)
    c: Block(g5)
FEATURE [Sketcher::SketchObject] Sketch080  label="topSketch025"
  FullyConstrained = true
  sketch-geometry (6):
    g0: LineSegment StartX=19 StartY=38 StartZ=0 EndX=117 EndY=38 EndZ=0
    g1: ArcOfCircle CenterX=19 CenterY=19 CenterZ=0 NormalX=0 NormalY=0 NormalZ=1 AngleXU=0 Radius=19 StartAngle=1.5708 EndAngle=3.14159
    g2: LineSegment StartX=117 StartY=38 StartZ=0 EndX=117 EndY=19 EndZ=0
    g3: LineSegment StartX=98 StartY=1.0161e-12 StartZ=0 EndX=5.22862e-06 EndY=1.0161e-12 EndZ=0
    g4: LineSegment StartX=5.22862e-06 StartY=19 StartZ=0 EndX=5.22862e-06 EndY=1.0161e-12 EndZ=0
    g5: ArcOfCircle CenterX=98 CenterY=19 CenterZ=0 NormalX=0 NormalY=0 NormalZ=1 AngleXU=0 Radius=19 StartAngle=4.71239 EndAngle=6.28319
  constraints (16):
    c: Horizontal(g0)
    c: Distance(g0) = 98
    c: Coincident(g1,g0)
    c: Block(g1)
    c: Coincident(g2,g0)
    c: Vertical(g2)
    c: Distance(g2) = 19
    c: Horizontal(g3)
    c: Coincident(g4,g1)
    c: Vertical(g4)
    c: Coincident(g3,g4)
    c: Block(g3)
    c: Coincident(g5,g2)
    c: Coincident(g5,g3)
    c: Block(g0)
    c: Block(g5)
FEATURE [Part::Extrusion] Extrude070  label="sideA004"
  Base = -> Sketch080
  Dir = (0,0,1)
  DirMode = 2
  FaceMakerClass = Part::FaceMakerBullseye
  LengthFwd = 3
  LengthRev = 0
  Placement = pos=(0,0,-2.7) rot=(0,0,1;0rad)
  Solid = true
  Symmetric = false
FEATURE [Sketcher::SketchObject] Sketch081
  FullyConstrained = true
  Placement = pos=(117,19,0) rot=(0.57735,0.57735,0.57735;2.0944rad)
  sketch-geometry (8):
    g0: LineSegment StartX=-49.19 StartY=63.5 StartZ=0 EndX=-49.19 EndY=60.5 EndZ=0
    g1: LineSegment StartX=-49.19 StartY=11.5 StartZ=0 EndX=-49.19 EndY=8.5 EndZ=0
    g2: ArcOfCircle CenterX=-1.5 CenterY=62 CenterZ=0 NormalX=0 NormalY=0 NormalZ=1 AngleXU=0 Radius=1.5 StartAngle=4.71239 EndAngle=7.85398
    g3: ArcOfCircle CenterX=-1.5 CenterY=10 CenterZ=0 NormalX=0 NormalY=0 NormalZ=1 AngleXU=0 Radius=1.5 StartAngle=4.71239 EndAngle=7.85398
    g4: LineSegment StartX=-49.19 StartY=63.5 StartZ=0 EndX=-1.5 EndY=63.5 EndZ=0
    g5: LineSegment StartX=-49.19 StartY=60.5 StartZ=0 EndX=-1.5 EndY=60.5 EndZ=0
    g6: LineSegment StartX=-49.19 StartY=11.5 StartZ=0 EndX=-1.5 EndY=11.5 EndZ=0
    g7: LineSegment StartX=-49.19 StartY=8.5 StartZ=0 EndX=-1.5 EndY=8.5 EndZ=0
  constraints (19):
    c: Vertical(g0)
    c: Distance(g0) = 3
    c: Vertical(g1)
    c: Block(g1)
    c: Block(g2)
    c: Block(g3)
    c: Block(g0)
    c: Coincident(g4,g0)
    c: Coincident(g4,g2)
    c: Horizontal(g4)
    c: Coincident(g5,g0)
    c: Coincident(g5,g2)
    c: Horizontal(g5)
    c: Coincident(g6,g1)
    c: Coincident(g6,g3)
    c: Horizontal(g6)
    c: Coincident(g7,g1)
    c: Coincident(g7,g3)
    c: Horizontal(g7)
FEATURE [Part::Extrusion] Extrude071  label="sideB004"
  Base = -> Sketch079
  Dir = (0,0,1)
  DirMode = 2
  FaceMakerClass = Part::FaceMakerBullseye
  LengthFwd = 3
  LengthRev = 0
  Placement = pos=(0,0,71.7) rot=(0,0,1;0rad)
  Solid = true
  Symmetric = false
FEATURE [Part::MultiFuse] Fusion152  label="removeFromBottom004"
  Placement = pos=(2,0,0) rot=(0,0,1;0rad)
  Shapes = -> [Extrude070,Extrude071]
FEATURE [Part::Extrusion] Extrude072
  Base = -> Sketch081
  Dir = (1,0,0)
  DirMode = 2
  FaceMakerClass = Part::FaceMakerBullseye
  LengthFwd = 10
  LengthRev = 0
  Solid = true
  Symmetric = false
FEATURE [Part::Fillet] Fillet059  label="removeFromtMoreFrontCaseScrewRetainers004"
  Base = -> Extrude072
  Edges = 4 edges r=1.49: [Edge6,Edge11,Edge18,Edge23]
  Placement = pos=(-12,0,0) rot=(0,0,1;0rad)
FEATURE [Sketcher::SketchObject] Sketch082
  FullyConstrained = true
  Placement = pos=(117,19,0) rot=(0.57735,0.57735,0.57735;2.0944rad)
  sketch-geometry (8):
    g0: LineSegment StartX=-49.19 StartY=69.25 StartZ=0 EndX=-49.19 EndY=66.25 EndZ=0
    g1: LineSegment StartX=-49.19 StartY=5.75 StartZ=0 EndX=-49.19 EndY=2.75 EndZ=0
    g2: ArcOfCircle CenterX=-1.5 CenterY=67.75 CenterZ=0 NormalX=0 NormalY=0 NormalZ=1 AngleXU=0 Radius=1.5 StartAngle=4.71239 EndAngle=7.85398
    g3: ArcOfCircle CenterX=-1.5 CenterY=4.25 CenterZ=0 NormalX=0 NormalY=0 NormalZ=1 AngleXU=0 Radius=1.5 StartAngle=4.71239 EndAngle=7.85398
    g4: LineSegment StartX=-49.19 StartY=69.25 StartZ=0 EndX=-1.5 EndY=69.25 EndZ=0
    g5: LineSegment StartX=-49.19 StartY=66.25 StartZ=0 EndX=-1.5 EndY=66.25 EndZ=0
    g6: LineSegment StartX=-49.19 StartY=5.75 StartZ=0 EndX=-1.5 EndY=5.75 EndZ=0
    g7: LineSegment StartX=-49.19 StartY=2.75 StartZ=0 EndX=-1.5 EndY=2.75 EndZ=0
  constraints (19):
    c: Vertical(g0)
    c: Distance(g0) = 3
    c: Block(g0)
    c: Vertical(g1)
    c: Block(g2)
    c: Block(g3)
    c: Block(g1)
    c: Coincident(g4,g0)
    c: Coincident(g4,g2)
    c: Horizontal(g4)
    c: Coincident(g5,g0)
    c: Coincident(g5,g2)
    c: Horizontal(g5)
    c: Coincident(g6,g1)
    c: Coincident(g6,g3)
    c: Horizontal(g6)
    c: Coincident(g7,g1)
    c: Coincident(g7,g3)
    c: Horizontal(g7)
FEATURE [Part::Extrusion] Extrude073
  Base = -> Sketch082
  Dir = (1,0,0)
  DirMode = 2
  FaceMakerClass = Part::FaceMakerBullseye
  LengthFwd = 10
  LengthRev = 0
  Solid = true
  Symmetric = false
FEATURE [Part::Fillet] Fillet060  label="removeFromtMoreFrontCaseScrewRetainers005"
  Base = -> Extrude073
  Edges = 4 edges r=1.49: [Edge6,Edge11,Edge18,Edge23]
  Placement = pos=(-4,0,0) rot=(0,0,1;0rad)
FEATURE [Part::Revolution] Revolve163  label="backCaseScrewRetainer004"
  Angle = 360
  Axis = (0,1,0)
  Base = (0,0,0)
  FaceMakerClass = Part::FaceMakerBullseye
  Placement = pos=(12.5,3,62) rot=(0,0,1;0rad)
  Solid = false
  Source = -> Face149
  Symmetric = false
FEATURE [Part::Revolution] Revolve164  label="frontCaseScrewRetainer006"
  Angle = 360
  Axis = (0,1,0)
  Base = (0,0,0)
  FaceMakerClass = Part::FaceMakerBullseye
  Placement = pos=(89.5,3,68.5) rot=(0,0,1;0rad)
  Solid = false
  Source = -> Face151
  Symmetric = false
FEATURE [Part::Revolution] Revolve165  label="frontCaseScrewRetainer007"
  Angle = 360
  Axis = (0,1,0)
  Base = (0,0,0)
  FaceMakerClass = Part::FaceMakerBullseye
  Placement = pos=(89.5,3,3.5) rot=(0,0,1;0rad)
  Solid = false
  Source = -> Face152
  Symmetric = false
FEATURE [Part::Revolution] Revolve166  label="backCaseScrewRetainer005"
  Angle = 360
  Axis = (0,1,0)
  Base = (0,0,0)
  FaceMakerClass = Part::FaceMakerBullseye
  Placement = pos=(12.5,3,10) rot=(0,0,1;0rad)
  Solid = false
  Source = -> Face150
  Symmetric = false
FEATURE [Part::Revolution] Revolve167  label="moreFrontCaseScrewRetainer006"
  Angle = 360
  Axis = (0,1,0)
  Base = (0,0,0)
  FaceMakerClass = Part::FaceMakerBullseye
  Placement = pos=(109.5,4.5,68.5) rot=(0,0,1;0rad)
  Solid = false
  Source = -> Face153
  Symmetric = false
FEATURE [Part::Revolution] Revolve168  label="moreFrontCaseScrewRetainer007"
  Angle = 360
  Axis = (0,1,0)
  Base = (0,0,0)
  FaceMakerClass = Part::FaceMakerBullseye
  Placement = pos=(109.5,4.5,3.5) rot=(0,0,1;0rad)
  Solid = false
  Source = -> Face154
  Symmetric = false
FEATURE [Part::MultiFuse] Fusion151  label="screwRetainers003"
  Shapes = -> [Revolve168,Revolve167,Revolve166,Revolve165,Revolve164,Revolve163]
FEATURE [Part::Cut] Cut069  label="screwRetainers004"
  Base = -> Fusion151
  Tool = -> Fusion152
FEATURE [Part::Cut] Cut070
  Base = -> Cut069
  Tool = -> Fillet060
FEATURE [Part::Cut] Cut071  label="screwPillars001"
  Base = -> Cut070
  Tool = -> Fillet059
FEATURE [Part::MultiFuse] Fusion153  label="bottom024"
  Shapes = -> [Fusion149,Cut071]
FEATURE [Part::Cylinder] Cylinder067
  Angle = 360
  AttacherType = Attacher::AttachEngine3D
  Height = 10
  Placement = pos=(20.65,12,4.68) rot=(1,0,0;1.5708rad)
  Radius = 2
FEATURE [Part::Cylinder] Cylinder068
  Angle = 360
  AttacherType = Attacher::AttachEngine3D
  Height = 10
  Placement = pos=(20.65,12,67.38) rot=(1,0,0;1.5708rad)
  Radius = 2
FEATURE [Part::Cylinder] Cylinder069
  Angle = 360
  AttacherType = Attacher::AttachEngine3D
  Height = 10
  Placement = pos=(77.15,12,67.38) rot=(1,0,0;1.5708rad)
  Radius = 2
FEATURE [Part::Cylinder] Cylinder070
  Angle = 360
  AttacherType = Attacher::AttachEngine3D
  Height = 10
  Placement = pos=(77.15,12,4.68) rot=(1,0,0;1.5708rad)
  Radius = 2
FEATURE [Part::MultiFuse] Fusion154  label="removeFromThreadedInsertHousing001"
  Shapes = -> [Cylinder069,Cylinder068,Cylinder067,Cylinder070]
FEATURE [Part::Cut] Cut072  label="bottom025"
  Base = -> Fusion153
  Tool = -> Fusion154
FEATURE [Image::ImagePlane] ImagePlane
  XSize = 339
  YSize = 72
FEATURE [Sketcher::SketchObject] Sketch083
  FullyConstrained = true
  MapMode = 5
  Support = -> [XY_Plane]
  sketch-geometry (338):
    g0: LineSegment StartX=-151.619 StartY=28.8932 StartZ=0 EndX=-140.819 EndY=28.8932 EndZ=0
    g1: LineSegment StartX=-151.619 StartY=24.0313 StartZ=0 EndX=-151.619 EndY=28.8932 EndZ=0
    g2: LineSegment StartX=-140.819 StartY=17.7713 StartZ=0 EndX=-151.619 EndY=17.7713 EndZ=0
    g3: LineSegment StartX=-151.619 StartY=17.7713 StartZ=0 EndX=-151.619 EndY=22.6313 EndZ=0
    g4: LineSegment StartX=-151.619 StartY=22.6313 StartZ=0 EndX=-145.128 EndY=22.6313 EndZ=0
    g5: LineSegment StartX=-145.128 StartY=24.0313 StartZ=0 EndX=-140.819 EndY=28.8932 EndZ=0
    g6: LineSegment StartX=-145.128 StartY=22.6313 StartZ=0 EndX=-140.819 EndY=17.7713 EndZ=0
    g7: ArcOfCircle CenterX=-155.157 CenterY=23.3323 CenterZ=0 NormalX=0 NormalY=0 NormalZ=1 AngleXU=0 Radius=6.92354 StartAngle=1.03434 EndAngle=5.24885
    g8: ArcOfCircle CenterX=-155.157 CenterY=23.3323 CenterZ=0 NormalX=0 NormalY=0 NormalZ=1 AngleXU=0 Radius=12.6269 StartAngle=1.28675 EndAngle=4.99643
    g9: LineSegment StartX=-151.619 StartY=35.4532 StartZ=0 EndX=-151.619 EndY=29.2832 EndZ=0
    g10: LineSegment StartX=-151.619 StartY=17.3813 StartZ=0 EndX=-151.619 EndY=11.2113 EndZ=0
    g11-g21: Circle x11 (B-spline internal-alignment scaffolding for g22; pole/knot coordinates omitted)
    g22: BSplineCurve PolesCount=11 KnotsCount=9 Degree=3 IsPeriodic=0
    g23-g31: GeomPoint x9 (B-spline internal-alignment scaffolding for g22; pole/knot coordinates omitted)
    g32-g49: Circle x18 (B-spline internal-alignment scaffolding for g50; pole/knot coordinates omitted)
    g50: BSplineCurve PolesCount=18 KnotsCount=16 Degree=3 IsPeriodic=0
    g51-g66: GeomPoint x16 (B-spline internal-alignment scaffolding for g50; pole/knot coordinates omitted)
    g67: LineSegment StartX=-117.124 StartY=30.093 StartZ=0 EndX=-117.603 EndY=26.5272 EndZ=0
    g68: LineSegment StartX=-117.603 StartY=17.8472 StartZ=0 EndX=-117.124 EndY=14.2659 EndZ=0
    g69: Ellipse CenterX=-109.671 CenterY=20.025 CenterZ=0 NormalX=0 NormalY=0 NormalZ=1 MajorRadius=3.34798 MinorRadius=2.71052 AngleXU=-1.56793
    g70: GeomPoint X=-109.666 Y=18.0598 Z=0
    g71: GeomPoint X=-109.677 Y=21.9902 Z=0
    g72: Ellipse CenterX=-109.671 CenterY=20.0123 CenterZ=0 NormalX=0 NormalY=0 NormalZ=1 MajorRadius=6.93002 MinorRadius=6.36273 AngleXU=-3.13976
    g73: GeomPoint X=-112.417 Y=20.0073 Z=0
    g74: GeomPoint X=-106.925 Y=20.0173 Z=0
    g75: Ellipse CenterX=-51.7682 CenterY=20.1463 CenterZ=0 NormalX=0 NormalY=0 NormalZ=1 MajorRadius=3.19279 MinorRadius=2.71052 AngleXU=-1.52774
    g76: GeomPoint X=-51.6955 Y=18.4606 Z=0
    g77: GeomPoint X=-51.8408 Y=21.832 Z=0
    g78: GeomPoint X=-54.5142 Y=20.1413 Z=0
    g79: GeomPoint X=-49.0221 Y=20.1513 Z=0
    g80: Ellipse CenterX=-51.7682 CenterY=20.1463 CenterZ=0 NormalX=0 NormalY=0 NormalZ=1 MajorRadius=6.93002 MinorRadius=6.36273 AngleXU=-3.13976
    g81: Ellipse CenterX=-22.8436 CenterY=20.1783 CenterZ=0 NormalX=0 NormalY=0 NormalZ=1 MajorRadius=3.31512 MinorRadius=2.71052 AngleXU=-1.60214
    g82: GeomPoint X=-22.9034 Y=18.2706 Z=0
    g83: GeomPoint X=-22.7838 Y=22.0861 Z=0
    g84: GeomPoint X=-25.5897 Y=20.1733 Z=0
    g85: GeomPoint X=-20.0976 Y=20.1833 Z=0
    g86: Ellipse CenterX=-22.8436 CenterY=20.1783 CenterZ=0 NormalX=0 NormalY=0 NormalZ=1 MajorRadius=6.93002 MinorRadius=6.36273 AngleXU=-3.13976
    g87: LineSegment StartX=-101.889 StartY=14.1107 StartZ=0 EndX=-97.7455 EndY=14.1107 EndZ=0
    g88: LineSegment StartX=-93.8155 StartY=14.1107 StartZ=0 EndX=-89.6755 EndY=14.1107 EndZ=0
    g89: LineSegment StartX=-85.7455 StartY=14.1107 StartZ=0 EndX=-81.6055 EndY=14.1107 EndZ=0
    g90: LineSegment StartX=-101.889 StartY=14.1107 StartZ=0 EndX=-101.889 EndY=25.9907 EndZ=0
    g91: LineSegment StartX=-101.889 StartY=25.9907 StartZ=0 EndX=-97.8594 EndY=25.9907 EndZ=0
    g92: LineSegment StartX=-97.8594 StartY=25.9907 StartZ=0 EndX=-97.8594 EndY=24.0907 EndZ=0
    g93: LineSegment StartX=-97.7455 StartY=14.1107 StartZ=0 EndX=-97.7455 EndY=19.9107 EndZ=0
    g94: LineSegment StartX=-89.6755 StartY=14.1107 StartZ=0 EndX=-89.6755 EndY=19.9107 EndZ=0
    g95: LineSegment StartX=-93.8155 StartY=14.1107 StartZ=0 EndX=-93.8155 EndY=21.0107 EndZ=0
    g96-g106: Circle x11 (B-spline internal-alignment scaffolding for g107; pole/knot coordinates omitted)
    g107: BSplineCurve PolesCount=11 KnotsCount=9 Degree=3 IsPeriodic=0
    g108-g116: GeomPoint x9 (B-spline internal-alignment scaffolding for g107; pole/knot coordinates omitted)
    g117: BSplineCurve PolesCount=11 KnotsCount=9 Degree=3 IsPeriodic=0
    g118-g125: Circle x8 (B-spline internal-alignment scaffolding for g126; pole/knot coordinates omitted)
    g126: BSplineCurve PolesCount=8 KnotsCount=6 Degree=3 IsPeriodic=0
    g127-g132: GeomPoint x6 (B-spline internal-alignment scaffolding for g126; pole/knot coordinates omitted)
    g133: BSplineCurve PolesCount=8 KnotsCount=6 Degree=3 IsPeriodic=0
    g134: LineSegment StartX=-85.7455 StartY=21.0107 StartZ=0 EndX=-85.7455 EndY=14.1107 EndZ=0
    g135: LineSegment StartX=-80.0879 StartY=14.1107 StartZ=0 EndX=-75.944 EndY=14.1107 EndZ=0
    g136: LineSegment StartX=-72.014 StartY=14.1107 StartZ=0 EndX=-67.874 EndY=14.1107 EndZ=0
    g137: LineSegment StartX=-63.944 StartY=14.1107 StartZ=0 EndX=-59.804 EndY=14.1107 EndZ=0
    g138: LineSegment StartX=-80.0879 StartY=14.1107 StartZ=0 EndX=-80.0879 EndY=25.9907 EndZ=0
    g139: LineSegment StartX=-80.0879 StartY=25.9907 StartZ=0 EndX=-76.0579 EndY=25.9907 EndZ=0
    g140: LineSegment StartX=-76.0579 StartY=25.9907 StartZ=0 EndX=-76.0579 EndY=24.0907 EndZ=0
    g141: LineSegment StartX=-75.944 StartY=14.1107 StartZ=0 EndX=-75.944 EndY=19.9107 EndZ=0
    g142: LineSegment StartX=-67.874 StartY=14.1107 StartZ=0 EndX=-67.874 EndY=19.9107 EndZ=0
    g143: LineSegment StartX=-72.014 StartY=14.1107 StartZ=0 EndX=-72.014 EndY=21.0107 EndZ=0
    g144-g148: Circle x5 (B-spline internal-alignment scaffolding for g149; pole/knot coordinates omitted)
    g149: BSplineCurve PolesCount=11 KnotsCount=9 Degree=3 IsPeriodic=0
    g150-g158: GeomPoint x9 (B-spline internal-alignment scaffolding for g149; pole/knot coordinates omitted)
    g159: BSplineCurve PolesCount=11 KnotsCount=9 Degree=3 IsPeriodic=0
    g160-g167: Circle x8 (B-spline internal-alignment scaffolding for g168; pole/knot coordinates omitted)
    g168: BSplineCurve PolesCount=8 KnotsCount=6 Degree=3 IsPeriodic=0
    g169-g174: GeomPoint x6 (B-spline internal-alignment scaffolding for g168; pole/knot coordinates omitted)
    g175: BSplineCurve PolesCount=8 KnotsCount=6 Degree=3 IsPeriodic=0
    g176: LineSegment StartX=-63.944 StartY=21.0107 StartZ=0 EndX=-63.944 EndY=14.1107 EndZ=0
    g177: LineSegment StartX=-59.804 StartY=14.1107 StartZ=0 EndX=-59.804 EndY=21.5868 EndZ=0
    g178: BSplineCurve PolesCount=4 KnotsCount=2 Degree=3 IsPeriodic=0
    g179: GeomPoint X=-59.804 Y=21.5868 Z=0
    g180: GeomPoint X=-60.2379 Y=24.0907 Z=0
    g181: LineSegment StartX=-81.6055 StartY=14.1107 StartZ=0 EndX=-81.6055 EndY=21.5868 EndZ=0
    g182: LineSegment StartX=-151.619 StartY=24.0313 StartZ=0 EndX=-145.128 EndY=24.0313 EndZ=0
    g183: Circle CenterX=-82.0394 CenterY=24.0907 CenterZ=0 NormalX=0 NormalY=0 NormalZ=1 AngleXU=0 Radius=1
    g184: Circle CenterX=-81.7131 CenterY=23.2736 CenterZ=0 NormalX=0 NormalY=0 NormalZ=1 AngleXU=0 Radius=1
    g185: Circle CenterX=-81.6055 CenterY=21.5868 CenterZ=0 NormalX=0 NormalY=0 NormalZ=1 AngleXU=0 Radius=1
    g186: BSplineCurve PolesCount=3 KnotsCount=2 Degree=2 IsPeriodic=0
    g187: GeomPoint X=-82.0394 Y=24.0907 Z=0
    g188: GeomPoint X=-81.6055 Y=21.5868 Z=0
    g189: Ellipse CenterX=-37.3522 CenterY=19.9515 CenterZ=0 NormalX=0 NormalY=0 NormalZ=1 MajorRadius=2.99755 MinorRadius=2.49 AngleXU=1.5708
    g190: GeomPoint X=-37.3522 Y=21.6203 Z=0
    g191: GeomPoint X=-37.3522 Y=18.2826 Z=0
    g192: ArcOfEllipse CenterX=-38.7647 CenterY=20.06 CenterZ=0 NormalX=0 NormalY=0 NormalZ=1 MajorRadius=6.30025 MinorRadius=5.3849 AngleXU=1.57276 StartAngle=5.50632 EndAngle=10.3035
    g193: GeomPoint X=-38.7711 Y=23.3304 Z=0
    g194: GeomPoint X=-38.7583 Y=16.7895 Z=0
    g195: LineSegment StartX=-34.6109 StartY=14.1107 StartZ=0 EndX=-30.8984 EndY=14.1107 EndZ=0
    g196: LineSegment StartX=-30.8984 StartY=14.1107 StartZ=0 EndX=-30.8984 EndY=31.1784 EndZ=0
    g197: LineSegment StartX=-30.8984 StartY=31.1784 StartZ=0 EndX=-34.9984 EndY=31.1784 EndZ=0
    g198: LineSegment StartX=-34.9984 StartY=24.5602 StartZ=0 EndX=-34.9984 EndY=31.1784 EndZ=0
    g199: LineSegment StartX=-34.6109 StartY=16.0476 StartZ=0 EndX=-34.6109 EndY=14.1107 EndZ=0
    g200: LineSegment StartX=-14.8781 StartY=14.1107 StartZ=0 EndX=-10.5106 EndY=14.1107 EndZ=0
    g201: LineSegment StartX=-14.8781 StartY=14.1107 StartZ=0 EndX=-14.8781 EndY=25.8504 EndZ=0
    g202: LineSegment StartX=-14.8781 StartY=25.8504 StartZ=0 EndX=-10.8534 EndY=25.8504 EndZ=0
    g203: LineSegment StartX=-10.8534 StartY=25.8504 StartZ=0 EndX=-10.8534 EndY=24.0923 EndZ=0
    g204: LineSegment StartX=-10.5106 StartY=14.1107 StartZ=0 EndX=-10.5106 EndY=19.7752 EndZ=0
    g205: LineSegment StartX=-5.96397 StartY=25.9304 StartZ=0 EndX=-5.96397 EndY=22.574 EndZ=0
    g206-g214: Circle x9 (B-spline internal-alignment scaffolding for g215; pole/knot coordinates omitted)
    g215: BSplineCurve PolesCount=9 KnotsCount=7 Degree=3 IsPeriodic=0
    g216-g222: GeomPoint x7 (B-spline internal-alignment scaffolding for g215; pole/knot coordinates omitted)
    g223-g232: Circle x10 (B-spline internal-alignment scaffolding for g233; pole/knot coordinates omitted)
    g233: BSplineCurve PolesCount=10 KnotsCount=8 Degree=3 IsPeriodic=0
    g234-g241: GeomPoint x8 (B-spline internal-alignment scaffolding for g233; pole/knot coordinates omitted)
    g242: LineSegment StartX=-1.58923 StartY=21.0696 StartZ=0 EndX=2.62034 EndY=21.0696 EndZ=0
    g243: LineSegment StartX=-1.55856 StartY=18.7342 StartZ=0 EndX=6.45946 EndY=18.7342 EndZ=0
    g244: LineSegment StartX=5.29231 StartY=17.386 StartZ=0 EndX=5.29231 EndY=14.3674 EndZ=0
    g245-g269: Circle x25 (B-spline internal-alignment scaffolding for g270; pole/knot coordinates omitted)
    g270: BSplineCurve PolesCount=25 KnotsCount=23 Degree=3 IsPeriodic=0
    g271-g293: GeomPoint x23 (B-spline internal-alignment scaffolding for g270; pole/knot coordinates omitted)
    g294-g304: Circle x11 (B-spline internal-alignment scaffolding for g305; pole/knot coordinates omitted)
    g305: BSplineCurve PolesCount=11 KnotsCount=9 Degree=3 IsPeriodic=0
    g306-g314: GeomPoint x9 (B-spline internal-alignment scaffolding for g305; pole/knot coordinates omitted)
    g315-g326: Circle x12 (B-spline internal-alignment scaffolding for g327; pole/knot coordinates omitted)
    g327: BSplineCurve PolesCount=12 KnotsCount=10 Degree=3 IsPeriodic=0
    g328-g337: GeomPoint x10 (B-spline internal-alignment scaffolding for g327; pole/knot coordinates omitted)
  constraints (252):
    c: Coincident(g1,g0)
    c: Horizontal(g0)
    c: Vertical(g1)
    c: Coincident(g2,g3)
    c: Coincident(g3,g4)
    c: Horizontal(g4)
    c: Horizontal(g2)
    c: Vertical(g3)
    c: Block(g1)
    c: Distance(g3) = 4.86
    c: Block(g4)
    c: Distance(g0) = 10.8
    c: Distance(g2) = 10.8
    c: Coincident(g5,g0)
    c: Coincident(g6,g4)
    c: Coincident(g6,g2)
    c: Block(g8)
    c: Block(g7)
    c: Coincident(g9,g8)
    c: Coincident(g9,g7)
    c: Vertical(g9)
    c: Coincident(g10,g7)
    c: Coincident(g10,g8)
    c: Vertical(g10)
    c: Weight(g11) = 1
    c: Equal(g11, g12-g21) x10
    c: InternalAlignment(g11-g21 -> g22) x11
    c: InternalAlignment(g23-g31 -> g22) x9
    c: Block(g22)
    c: Weight(g32) = 1
    c: Equal(g32, g33-g49) x17
    c: InternalAlignment(g32-g49 -> g50) x18
    c: InternalAlignment(g51-g66 -> g50) x16
    c: Block(g50)
    c: Coincident(g67,g50)
    c: Coincident(g67,g22)
    c: Coincident(g68,g22)
    c: Coincident(g68,g50)
    c: InternalAlignment(g70,g69)
    c: InternalAlignment(g71,g69)
    c: Block(g69)
    c: InternalAlignment(g73,g72)
    c: InternalAlignment(g74,g72)
    c: Block(g72)
    c: InternalAlignment(g76,g75)
    c: InternalAlignment(g77,g75)
    c: InternalAlignment(g78,g80)
    c: InternalAlignment(g79,g80)
    c: Block(g80)
    c: Coincident(g75,g80)
    c: Block(g75)
    c: InternalAlignment(g82,g81)
    c: InternalAlignment(g83,g81)
    c: InternalAlignment(g84,g86)
    c: InternalAlignment(g85,g86)
    c: Block(g86)
    c: Coincident(g81,g86)
    c: Block(g81)
    c: Horizontal(g87)
    c: Block(g87)
    c: Horizontal(g88)
    c: Distance(g88) = 4.14
    c: Horizontal(g89)
    c: Equal(g88,g89) = 4.14
    c: Block(g89)
    c: Block(g88)
    c: Coincident(g90,g87)
    c: Vertical(g90)
    c: Distance(g90) = 11.88
    c: Coincident(g91,g90)
    c: Horizontal(g91)
    c: Coincident(g92,g91)
    c: Vertical(g92)
    c: Distance(g91) = 4.03
    c: Distance(g92) = 1.9
    c: Coincident(g93,g87)
    c: Vertical(g93)
    c: Vertical(g94)
    c: Coincident(g94,g88)
    c: Distance(g93) = 5.8
    c: Distance(g94) = 5.8
    c: Vertical(g95)
    c: Coincident(g95,g88)
    c: Distance(g95) = 6.9
    c: Coincident(g107,g92)
    c: Weight(g96) = 1
    c: Equal(g96, g97-g106) x10
    c: InternalAlignment(g96-g106 -> g107) x11
    c: InternalAlignment(g108-g116 -> g107) x9
    c: Block(g107)
    c: Block(g117)
    c: Coincident(g126,g93)
    c: Weight(g118) = 1
    c: Equal(g118, g119-g125) x7
    c: Coincident(g126,g95)
    c: InternalAlignment(g118-g125 -> g126) x8
    c: InternalAlignment(g127-g132 -> g126) x6
    c: Coincident(g133,g94)
    c: Block(g126)
    c: Block(g133)
    c: Coincident(g134,g133)
    c: Coincident(g134,g89)
    c: Vertical(g134)
    c: Horizontal(g135)
    c: Block(g135)
    c: Horizontal(g136)
    c: Equal(g88,g136) = 4.14
    c: Horizontal(g137)
    c: Equal(g136,g137) = 4.14
    c: Block(g137)
    c: Block(g136)
    c: Coincident(g138,g135)
    c: Vertical(g138)
    c: Equal(g90,g138) = 11.88
    c: Coincident(g139,g138)
    c: Horizontal(g139)
    c: Coincident(g140,g139)
    c: Vertical(g140)
    c: Equal(g91,g139) = 4.03
    c: Equal(g92,g140) = 1.9
    c: Coincident(g141,g135)
    c: Vertical(g141)
    c: Vertical(g142)
    c: Coincident(g142,g136)
    c: Equal(g93,g141) = 5.8
    c: Equal(g94,g142) = 5.8
    c: Vertical(g143)
    c: Coincident(g143,g136)
    c: Equal(g95,g143) = 6.9
    c: Coincident(g149,g140)
    c: Equal(g96,g144) = 1
    c: Equal(g144, g145-g148) x4
    c: InternalAlignment(g144-g148 -> g149) x5
    c: InternalAlignment(g150-g158 -> g149) x9
    c: Block(g149)
    c: Block(g159)
    c: Coincident(g168,g141)
    c: Equal(g118,g160) = 1
    c: Equal(g160, g161-g167) x7
    c: Coincident(g168,g143)
    c: InternalAlignment(g160-g167 -> g168) x8
    c: InternalAlignment(g169-g174 -> g168) x6
    c: Coincident(g175,g142)
    c: Block(g168)
    c: Block(g175)
    c: Coincident(g176,g175)
    c: Coincident(g176,g137)
    c: Vertical(g176)
    c: Coincident(g177,g137)
    c: Vertical(g177)
    c: Coincident(g178,g177)
    c: Coincident(g178,g159)
    c: InternalAlignment(g179,g178)
    c: InternalAlignment(g180,g178)
    c: Block(g178)
    c: Vertical(g181)
    c: Coincident(g181,g89)
    c: Block(g5)
    c: Coincident(g182,g1)
    c: Coincident(g182,g5)
    c: Horizontal(g182)
    c: Coincident(g186,g117)
    c: Weight(g183) = 1
    c: Equal(g183,g184)
    c: Equal(g183,g185)
    c: Coincident(g186,g181)
    c: InternalAlignment(g183,g186)
    c: InternalAlignment(g184,g186)
    c: InternalAlignment(g185,g186)
    c: InternalAlignment(g187,g186)
    c: InternalAlignment(g188,g186)
    c: Block(g186)
    c: InternalAlignment(g190,g189)
    c: InternalAlignment(g191,g189)
    c: Block(g189)
    c: InternalAlignment(g193,g192)
    c: InternalAlignment(g194,g192)
    c: Block(g192)
    c: Horizontal(g195)
    c: Block(g195)
    c: Coincident(g196,g195)
    c: Vertical(g196)
    c: Block(g196)
    c: Distance(g195) = 3.71244
    c: Coincident(g197,g196)
    c: Horizontal(g197)
    c: Distance(g197) = 4.1
    c: Coincident(g198,g192)
    c: Coincident(g198,g197)
    c: Vertical(g198)
    c: Block(g198)
    c: Coincident(g199,g192)
    c: Coincident(g199,g195)
    c: Vertical(g199)
    c: Block(g199)
    c: Horizontal(g200)
    c: Block(g200)
    c: Coincident(g201,g200)
    c: Vertical(g201)
    c: Block(g201)
    c: Coincident(g202,g201)
    c: Horizontal(g202)
    c: Block(g202)
    c: Coincident(g203,g202)
    c: Vertical(g203)
    c: Block(g203)
    c: Coincident(g204,g200)
    c: Vertical(g204)
    c: Block(g204)
    c: Coincident(g215,g203)
    c: Weight(g206) = 1
    c: Equal(g206, g207-g214) x8
    c: Coincident(g215,g205)
    c: InternalAlignment(g206-g214 -> g215) x9
    c: InternalAlignment(g216-g222 -> g215) x7
    c: Coincident(g233,g204)
    c: Weight(g223) = 1
    c: Equal(g223, g224-g232) x9
    c: Coincident(g233,g205)
    c: InternalAlignment(g223-g232 -> g233) x10
    c: InternalAlignment(g234-g241 -> g233) x8
    c: Vertical(g205)
    c: Block(g205)
    c: Block(g215)
    c: Block(g233)
    c: Horizontal(g242)
    c: Horizontal(g243)
    c: Block(g242)
    c: Block(g243)
    c: Vertical(g244)
    c: Block(g244)
    c: Coincident(g270,g243)
    c: Weight(g245) = 1
    c: Equal(g245, g246-g269) x24
    c: Coincident(g270,g244)
    c: InternalAlignment(g245-g269 -> g270) x25
    c: InternalAlignment(g271-g293 -> g270) x23
    c: Block(g270)
    c: Coincident(g305,g242)
    c: Weight(g294) = 1
    c: Equal(g294, g295-g304) x10
    c: Coincident(g305,g242)
    c: InternalAlignment(g294-g304 -> g305) x11
    c: InternalAlignment(g306-g314 -> g305) x9
    c: Block(g305)
    c: Coincident(g327,g243)
    c: Weight(g315) = 1
    c: Equal(g315, g316-g326) x11
    c: Coincident(g327,g244)
    c: InternalAlignment(g315-g326 -> g327) x12
    c: InternalAlignment(g328-g337 -> g327) x10
    c: Block(g327)
FEATURE [PartDesign::Body] Body
  Group = -> [Sketch083]
  Origin = -> Origin
FEATURE [Sketcher::SketchObject] Sketch084
  FullyConstrained = true
  MapMode = 5
  Support = -> [XY_Plane001]
FEATURE [PartDesign::Body] Body001
  Group = -> [Sketch084]
  Origin = -> Origin001
